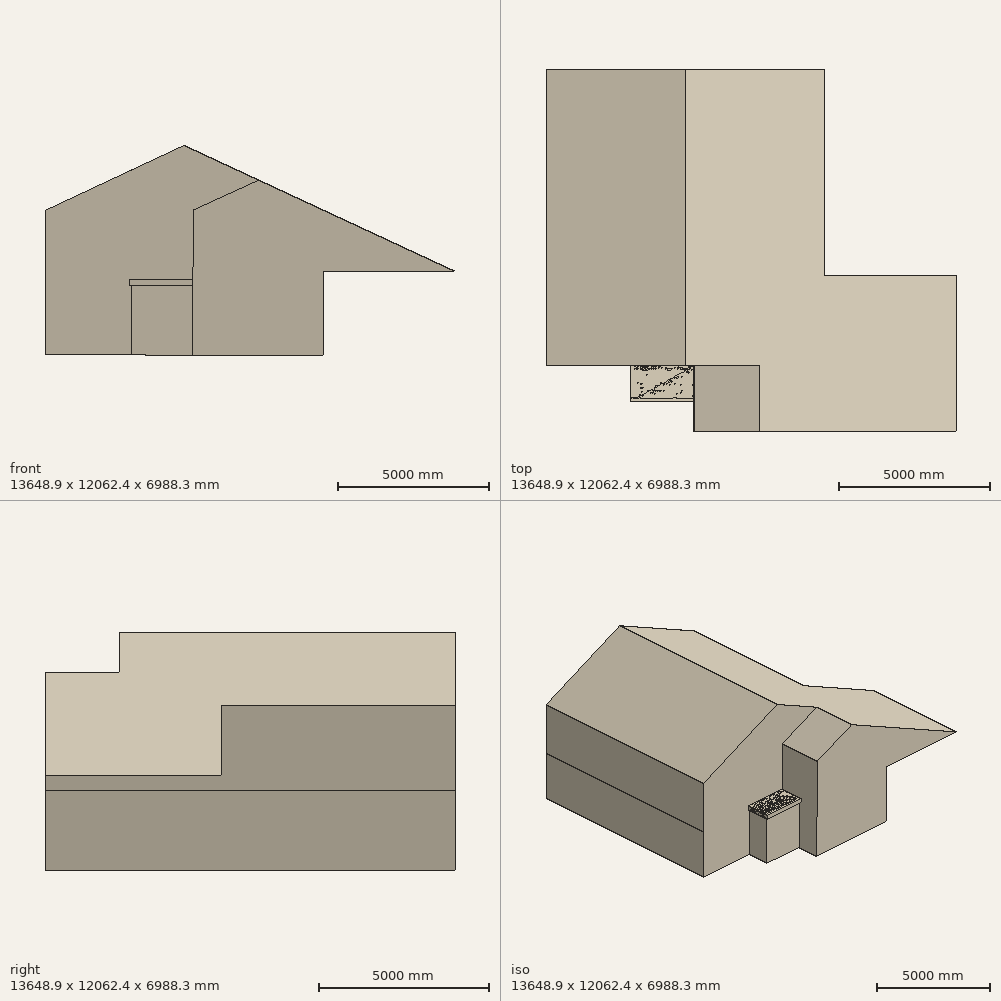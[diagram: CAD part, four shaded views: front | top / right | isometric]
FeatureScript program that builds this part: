
annotation { "Feature Type Name" : "Feature", "Feature Type Description" : "" }
export const myFeature = defineFeature(function(context is Context, id is Id, definition is map)
    precondition{}
    {
        {
            var Q0;
            Q0=qCreatedBy(makeId("Front.planeOp"),FACE);
            var sketch = newSketch(context, id + "F0", { "sketchPlane" : qUnion([Q0])});
            skLineSegment(sketch, "E0", {"start": v(18452.44, -7592.59) * mm, "end": v(18454.44, -7609.59) * mm});
            skLineSegment(sketch, "E1", {"start": v(18454.44, -7609.59) * mm, "end": v(18476.44, -7643.59) * mm});
            skLineSegment(sketch, "E2", {"start": v(18476.44, -7643.59) * mm, "end": v(21925.27, -7643.59) * mm});
            skLineSegment(sketch, "E3", {"start": v(-8455.23, 8336.41) * mm, "end": v(-8450.23, 8869.41) * mm});
            skLineSegment(sketch, "E4", {"start": v(9184.83, 9869.41) * mm, "end": v(9184.83, 10021.41) * mm});
            skLineSegment(sketch, "E5", {"start": v(9184.83, 10021.41) * mm, "end": v(9032.83, 10021.41) * mm});
            skLineSegment(sketch, "E6", {"start": v(9032.83, 10021.41) * mm, "end": v(9032.83, 9869.41) * mm});
            skLineSegment(sketch, "E7", {"start": v(9032.83, 9869.41) * mm, "end": v(9184.83, 9869.41) * mm});
            skLineSegment(sketch, "E8", {"start": v(-1174.56, -11014.59) * mm, "end": v(-1463.56, -11004.59) * mm});
            skLineSegment(sketch, "E9", {"start": v(3088.44, -8773.59) * mm, "end": v(3052.44, -8708.59) * mm});
            skLineSegment(sketch, "E10", {"start": v(3052.44, -8708.59) * mm, "end": v(2987.44, -8744.59) * mm});
            skLineSegment(sketch, "E11", {"start": v(2987.44, -8744.59) * mm, "end": v(3023.44, -8809.59) * mm});
            skLineSegment(sketch, "E12", {"start": v(3023.44, -8809.59) * mm, "end": v(3088.44, -8773.59) * mm});
            skLineSegment(sketch, "E13", {"start": v(4326.44, -9193.59) * mm, "end": v(4325.44, -9258.59) * mm});
            skLineSegment(sketch, "E14", {"start": v(4325.44, -9258.59) * mm, "end": v(4390.44, -9259.59) * mm});
            skLineSegment(sketch, "E15", {"start": v(4320.44, -9221.59) * mm, "end": v(4251.44, -9176.59) * mm});
            skLineSegment(sketch, "E16", {"start": v(4251.44, -9176.59) * mm, "end": v(4312.44, -9166.59) * mm});
            skLineSegment(sketch, "E17", {"start": v(-2874.56, -11901.59) * mm, "end": v(-2882.56, -11385.59) * mm});
            skLineSegment(sketch, "E18", {"start": v(-2949.56, -11902.59) * mm, "end": v(-2957.56, -11387.59) * mm});
            skLineSegment(sketch, "E19", {"start": v(-2882.56, -11385.59) * mm, "end": v(-2888.56, -11264.59) * mm});
            skLineSegment(sketch, "E20", {"start": v(-2957.56, -11387.59) * mm, "end": v(-2963.56, -11268.59) * mm});
            skLineSegment(sketch, "E21", {"start": v(-2888.56, -11264.59) * mm, "end": v(-2895.56, -11106.59) * mm});
            skLineSegment(sketch, "E22", {"start": v(-2963.56, -11268.59) * mm, "end": v(-2970.56, -11109.59) * mm});
            skArc(sketch, "E23", {"start": v(-10647.23, 10596.41) * mm, "mid": v(-10679.4, 10606.41) * mm, "end": v(-10711.23, 10595.41) * mm});
            skLineSegment(sketch, "E24", {"start": v(-10711.23, 10595.41) * mm, "end": v(-10798.23, 10527.41) * mm});
            skLineSegment(sketch, "E25", {"start": v(-10798.23, 10527.41) * mm, "end": v(-10806.23, 10504.41) * mm});
            skLineSegment(sketch, "E26", {"start": v(-10806.23, 10504.41) * mm, "end": v(-11091.23, 10388.41) * mm});
            skLineSegment(sketch, "E27", {"start": v(-11091.23, 10388.41) * mm, "end": v(-13024.23, 9421.41) * mm});
            skLineSegment(sketch, "E28", {"start": v(-10557.23, 10534.41) * mm, "end": v(-10611.23, 10573.41) * mm});
            skLineSegment(sketch, "E29", {"start": v(-10611.23, 10573.41) * mm, "end": v(-10647.23, 10596.41) * mm});
            skLineSegment(sketch, "E30", {"start": v(-10557.23, 10534.41) * mm, "end": v(-10550.83, 10516) * mm});
            skLineSegment(sketch, "E31", {"start": v(-10695.7, 10488.12) * mm, "end": v(-8590.23, 9450.41) * mm});
            skLineSegment(sketch, "E32", {"start": v(-8056.23, 9293.41) * mm, "end": v(-8040.23, 9323.41) * mm});
            skLineSegment(sketch, "E33", {"start": v(-8040.23, 9323.41) * mm, "end": v(-8319.23, 9433.41) * mm});
            skLineSegment(sketch, "E34", {"start": v(-8319.23, 9433.41) * mm, "end": v(-10253.23, 10396.41) * mm});
            skLineSegment(sketch, "E35", {"start": v(-10253.23, 10396.41) * mm, "end": v(-10522.23, 10504.41) * mm});
            skLineSegment(sketch, "E36", {"start": v(-10522.23, 10504.41) * mm, "end": v(-10550.83, 10516) * mm});
            skLineSegment(sketch, "E37", {"start": v(-8121.23, 9297.41) * mm, "end": v(-8056.23, 9293.41) * mm});
            skArc(sketch, "E38", {"start": v(-8144.23, 9285.42) * mm, "mid": v(-8077.27, 9212.5) * mm, "end": v(-7999.23, 9273.42) * mm});
            skLineSegment(sketch, "E39", {"start": v(-7999.23, 9273.42) * mm, "end": v(-8144.23, 9285.41) * mm});
            skArc(sketch, "E40", {"start": v(-8153.68, 9046.58) * mm, "mid": v(-8134.16, 9057.59) * mm, "end": v(-8124.4, 9077.76) * mm});
            skArc(sketch, "E41", {"start": v(-8347.8, 9005.21) * mm, "mid": v(-8418.14, 8951.74) * mm, "end": v(-8450.23, 8869.42) * mm});
            skLineSegment(sketch, "E42", {"start": v(-8347.8, 9005.21) * mm, "end": v(-8153.68, 9046.58) * mm});
            skArc(sketch, "E43", {"start": v(-8312.07, 8935.4) * mm, "mid": v(-8354.55, 8902.55) * mm, "end": v(-8376.23, 8853.42) * mm});
            skArc(sketch, "E44", {"start": v(-8112.54, 8979.42) * mm, "mid": v(-8073.98, 9001.36) * mm, "end": v(-8054.57, 9041.26) * mm});
            skLineSegment(sketch, "E45", {"start": v(-8312.07, 8935.4) * mm, "end": v(-8112.54, 8979.42) * mm});
            skLineSegment(sketch, "E46", {"start": v(-8054.57, 9041.26) * mm, "end": v(-8025.82, 9228.12) * mm});
            skLineSegment(sketch, "E47", {"start": v(-8124.4, 9077.76) * mm, "end": v(-8103.38, 9219.7) * mm});
            skLineSegment(sketch, "E48", {"start": v(-8578.23, 9283.41) * mm, "end": v(-9845.23, 9908.41) * mm});
            skLineSegment(sketch, "E49", {"start": v(-8578.23, 9165.66) * mm, "end": v(-8578.23, 9283.41) * mm});
            skLineSegment(sketch, "E50", {"start": v(-8141.4, 9155) * mm, "end": v(-8578.23, 9165.66) * mm});
            skLineSegment(sketch, "E51", {"start": v(-8135.9, 9300.67) * mm, "end": v(-8136.5, 9284.77) * mm});
            skLineSegment(sketch, "E52", {"start": v(-8137.63, 9254.9) * mm, "end": v(-8141.4, 9155) * mm});
            skLineSegment(sketch, "E53", {"start": v(-8485.65, 6827.41) * mm, "end": v(-8490.38, 9163.52) * mm});
            skLineSegment(sketch, "E54", {"start": v(-11690.04, 7524.24) * mm, "end": v(-9647.23, 7524.24) * mm});
            skLineSegment(sketch, "E55", {"start": v(-9714.9, 7595.41) * mm, "end": v(-11621.96, 7595.41) * mm});
            skLineSegment(sketch, "E56", {"start": v(-11690.04, 7524.24) * mm, "end": v(-11690.27, 7577.41) * mm});
            skLineSegment(sketch, "E57", {"start": v(-9647.23, 7577.41) * mm, "end": v(-11690.27, 7577.41) * mm});
            skLineSegment(sketch, "E58", {"start": v(-9647.23, 7524.24) * mm, "end": v(-9647.23, 7577.41) * mm});
            skLineSegment(sketch, "E59", {"start": v(-9714.9, 9403.41) * mm, "end": v(-9714.9, 7577.41) * mm});
            skLineSegment(sketch, "E60", {"start": v(-11621.96, 9403.41) * mm, "end": v(-11621.96, 7577.41) * mm});
            skLineSegment(sketch, "E61", {"start": v(-11621.96, 9403.41) * mm, "end": v(-9714.9, 9403.41) * mm});
            skLineSegment(sketch, "E62", {"start": v(-9744.23, 7627.41) * mm, "end": v(-10336.23, 7627.41) * mm});
            skLineSegment(sketch, "E63", {"start": v(-10336.23, 7627.41) * mm, "end": v(-10336.23, 8738.41) * mm});
            skLineSegment(sketch, "E64", {"start": v(-10336.23, 8738.41) * mm, "end": v(-9744.23, 8738.41) * mm});
            skLineSegment(sketch, "E65", {"start": v(-9744.23, 8738.41) * mm, "end": v(-9744.23, 7627.41) * mm});
            skLineSegment(sketch, "E66", {"start": v(-9808.23, 7689.41) * mm, "end": v(-10274.23, 7689.41) * mm});
            skLineSegment(sketch, "E67", {"start": v(-10274.23, 7689.41) * mm, "end": v(-10274.23, 8676.41) * mm});
            skLineSegment(sketch, "E68", {"start": v(-10274.23, 8676.41) * mm, "end": v(-9808.23, 8676.41) * mm});
            skLineSegment(sketch, "E69", {"start": v(-9808.23, 8676.41) * mm, "end": v(-9808.23, 7689.41) * mm});
            skLineSegment(sketch, "E70", {"start": v(-9755.23, 7636.41) * mm, "end": v(-10327.23, 7636.41) * mm});
            skLineSegment(sketch, "E71", {"start": v(-10327.23, 7636.41) * mm, "end": v(-10327.23, 8729.41) * mm});
            skLineSegment(sketch, "E72", {"start": v(-10327.23, 8729.41) * mm, "end": v(-9755.23, 8729.41) * mm});
            skLineSegment(sketch, "E73", {"start": v(-9755.23, 8729.41) * mm, "end": v(-9755.23, 7636.41) * mm});
            skLineSegment(sketch, "E74", {"start": v(-9819.23, 7700.41) * mm, "end": v(-10263.23, 7700.41) * mm});
            skLineSegment(sketch, "E75", {"start": v(-10263.23, 7700.41) * mm, "end": v(-10263.23, 8665.41) * mm});
            skLineSegment(sketch, "E76", {"start": v(-10263.23, 8665.41) * mm, "end": v(-9819.23, 8665.41) * mm});
            skLineSegment(sketch, "E77", {"start": v(-9819.23, 8665.41) * mm, "end": v(-9819.23, 7700.41) * mm});
            skLineSegment(sketch, "E78", {"start": v(-10336.23, 8751.41) * mm, "end": v(-9744.23, 8751.41) * mm});
            skLineSegment(sketch, "E79", {"start": v(-9744.23, 8751.41) * mm, "end": v(-9744.23, 9144.41) * mm});
            skLineSegment(sketch, "E80", {"start": v(-9744.23, 9144.41) * mm, "end": v(-10336.23, 9144.41) * mm});
            skLineSegment(sketch, "E81", {"start": v(-10336.23, 9144.41) * mm, "end": v(-10336.23, 8751.41) * mm});
            skLineSegment(sketch, "E82", {"start": v(-10325.23, 8762.41) * mm, "end": v(-9755.23, 8762.41) * mm});
            skLineSegment(sketch, "E83", {"start": v(-9755.23, 8762.41) * mm, "end": v(-9755.23, 9133.41) * mm});
            skLineSegment(sketch, "E84", {"start": v(-9755.23, 9133.41) * mm, "end": v(-10325.23, 9133.41) * mm});
            skLineSegment(sketch, "E85", {"start": v(-10325.23, 9133.41) * mm, "end": v(-10325.23, 8762.41) * mm});
            skLineSegment(sketch, "E86", {"start": v(-10268.23, 8805.41) * mm, "end": v(-9798.23, 8805.41) * mm});
            skLineSegment(sketch, "E87", {"start": v(-10268.23, 9090.42) * mm, "end": v(-10268.23, 8805.41) * mm});
            skLineSegment(sketch, "E88", {"start": v(-9798.23, 9090.42) * mm, "end": v(-10268.23, 9090.42) * mm});
            skLineSegment(sketch, "E89", {"start": v(-9798.43, 8805.41) * mm, "end": v(-9798.43, 9090.42) * mm});
            skLineSegment(sketch, "E90", {"start": v(-9809.23, 9079.41) * mm, "end": v(-10257.23, 9079.41) * mm});
            skLineSegment(sketch, "E91", {"start": v(-9809.23, 8816.41) * mm, "end": v(-9809.23, 9079.41) * mm});
            skLineSegment(sketch, "E92", {"start": v(-10257.23, 8816.41) * mm, "end": v(-9809.23, 8816.41) * mm});
            skLineSegment(sketch, "E93", {"start": v(-10257.23, 9079.41) * mm, "end": v(-10257.23, 8816.41) * mm});
            skLineSegment(sketch, "E94", {"start": v(-9837.23, 9118.41) * mm, "end": v(-10240.23, 9118.41) * mm});
            skLineSegment(sketch, "E95", {"start": v(-10240.23, 9118.41) * mm, "end": v(-10240.23, 9100.41) * mm});
            skLineSegment(sketch, "E96", {"start": v(-10240.23, 9100.41) * mm, "end": v(-9837.23, 9100.41) * mm});
            skLineSegment(sketch, "E97", {"start": v(-9837.23, 9100.41) * mm, "end": v(-9837.23, 9118.41) * mm});
            skLineSegment(sketch, "E98", {"start": v(-10996.23, 7627.41) * mm, "end": v(-11588.23, 7627.41) * mm});
            skLineSegment(sketch, "E99", {"start": v(-11588.23, 7627.41) * mm, "end": v(-11588.23, 8738.41) * mm});
            skLineSegment(sketch, "E100", {"start": v(-11588.23, 8738.41) * mm, "end": v(-10996.23, 8738.41) * mm});
            skLineSegment(sketch, "E101", {"start": v(-10996.23, 8738.41) * mm, "end": v(-10996.23, 7627.41) * mm});
            skLineSegment(sketch, "E102", {"start": v(-11060.23, 7689.41) * mm, "end": v(-11526.23, 7689.41) * mm});
            skLineSegment(sketch, "E103", {"start": v(-11526.23, 7689.41) * mm, "end": v(-11526.23, 8676.41) * mm});
            skLineSegment(sketch, "E104", {"start": v(-11526.23, 8676.41) * mm, "end": v(-11060.23, 8676.41) * mm});
            skLineSegment(sketch, "E105", {"start": v(-11060.23, 8676.41) * mm, "end": v(-11060.23, 7689.41) * mm});
            skLineSegment(sketch, "E106", {"start": v(-11007.23, 7636.41) * mm, "end": v(-11579.23, 7636.41) * mm});
            skLineSegment(sketch, "E107", {"start": v(-11579.23, 7636.41) * mm, "end": v(-11579.23, 8729.41) * mm});
            skLineSegment(sketch, "E108", {"start": v(-11579.23, 8729.41) * mm, "end": v(-11007.23, 8729.41) * mm});
            skLineSegment(sketch, "E109", {"start": v(-11007.23, 8729.41) * mm, "end": v(-11007.23, 7636.41) * mm});
            skLineSegment(sketch, "E110", {"start": v(-11071.23, 7700.41) * mm, "end": v(-11515.23, 7700.41) * mm});
            skLineSegment(sketch, "E111", {"start": v(-11515.23, 7700.41) * mm, "end": v(-11515.23, 8665.41) * mm});
            skLineSegment(sketch, "E112", {"start": v(-11515.23, 8665.41) * mm, "end": v(-11071.23, 8665.41) * mm});
            skLineSegment(sketch, "E113", {"start": v(-11071.23, 8665.41) * mm, "end": v(-11071.23, 7700.41) * mm});
            skLineSegment(sketch, "E114", {"start": v(-11588.23, 8751.41) * mm, "end": v(-10996.23, 8751.41) * mm});
            skLineSegment(sketch, "E115", {"start": v(-10996.23, 8751.41) * mm, "end": v(-10996.23, 9144.41) * mm});
            skLineSegment(sketch, "E116", {"start": v(-10996.23, 9144.41) * mm, "end": v(-11588.23, 9144.41) * mm});
            skLineSegment(sketch, "E117", {"start": v(-11588.23, 9144.41) * mm, "end": v(-11588.23, 8751.41) * mm});
            skLineSegment(sketch, "E118", {"start": v(-11577.23, 8762.41) * mm, "end": v(-11007.23, 8762.41) * mm});
            skLineSegment(sketch, "E119", {"start": v(-11007.23, 8762.41) * mm, "end": v(-11007.23, 9133.41) * mm});
            skLineSegment(sketch, "E120", {"start": v(-11007.23, 9133.41) * mm, "end": v(-11577.23, 9133.41) * mm});
            skLineSegment(sketch, "E121", {"start": v(-11577.23, 9133.41) * mm, "end": v(-11577.23, 8762.41) * mm});
            skLineSegment(sketch, "E122", {"start": v(-11520.23, 8805.41) * mm, "end": v(-11050.23, 8805.41) * mm});
            skLineSegment(sketch, "E123", {"start": v(-11520.23, 9090.42) * mm, "end": v(-11520.23, 8805.41) * mm});
            skLineSegment(sketch, "E124", {"start": v(-11050.23, 9090.42) * mm, "end": v(-11520.23, 9090.42) * mm});
            skLineSegment(sketch, "E125", {"start": v(-11050.43, 8805.41) * mm, "end": v(-11050.43, 9090.42) * mm});
            skLineSegment(sketch, "E126", {"start": v(-11061.23, 9079.41) * mm, "end": v(-11509.23, 9079.41) * mm});
            skLineSegment(sketch, "E127", {"start": v(-11061.23, 8816.41) * mm, "end": v(-11061.23, 9079.41) * mm});
            skLineSegment(sketch, "E128", {"start": v(-11509.23, 8816.41) * mm, "end": v(-11061.23, 8816.41) * mm});
            skLineSegment(sketch, "E129", {"start": v(-11509.23, 9079.41) * mm, "end": v(-11509.23, 8816.41) * mm});
            skLineSegment(sketch, "E130", {"start": v(-11089.23, 9118.41) * mm, "end": v(-11492.23, 9118.41) * mm});
            skLineSegment(sketch, "E131", {"start": v(-11492.23, 9118.41) * mm, "end": v(-11492.23, 9100.41) * mm});
            skLineSegment(sketch, "E132", {"start": v(-11492.23, 9100.41) * mm, "end": v(-11089.23, 9100.41) * mm});
            skLineSegment(sketch, "E133", {"start": v(-11089.23, 9100.41) * mm, "end": v(-11089.23, 9118.41) * mm});
            skLineSegment(sketch, "E134", {"start": v(-11515.23, 8663.41) * mm, "end": v(-11515.23, 8654.41) * mm});
            skLineSegment(sketch, "E135", {"start": v(-11621.96, 9177.41) * mm, "end": v(-9714.9, 9177.41) * mm});
            skLineSegment(sketch, "E136", {"start": v(-11621.96, 9150.41) * mm, "end": v(-9714.9, 9150.41) * mm});
            skLineSegment(sketch, "E137", {"start": v(-9210.23, 7574.41) * mm, "end": v(-9049.23, 7574.41) * mm});
            skLineSegment(sketch, "E138", {"start": v(-9049.23, 7574.41) * mm, "end": v(-9049.23, 7462.41) * mm});
            skLineSegment(sketch, "E139", {"start": v(-9049.23, 7462.41) * mm, "end": v(-9210.23, 7462.41) * mm});
            skLineSegment(sketch, "E140", {"start": v(-9210.23, 7462.41) * mm, "end": v(-9210.23, 7574.41) * mm});
            skLineSegment(sketch, "E141", {"start": v(-9199.23, 7421.41) * mm, "end": v(-9061.23, 7421.41) * mm});
            skLineSegment(sketch, "E142", {"start": v(-9199.23, 7462.41) * mm, "end": v(-9199.23, 7421.41) * mm});
            skLineSegment(sketch, "E143", {"start": v(-9061.23, 7421.41) * mm, "end": v(-9061.23, 7462.41) * mm});
            skCircle(sketch, "E144", {"center": v(-9756.73, 7030.41) * mm, "radius": 12 * mm});
            skLineSegment(sketch, "E145", {"start": v(-9845.23, 9908.41) * mm, "end": v(-10687.65, 10323) * mm});
            skLineSegment(sketch, "E146", {"start": v(-10687.65, 10323) * mm, "end": v(-12771.23, 9266.78) * mm});
            skLineSegment(sketch, "E147", {"start": v(-12771.23, 9266.78) * mm, "end": v(-12771.23, 9159.73) * mm});
            skLineSegment(sketch, "E148", {"start": v(-12771.23, 9159.73) * mm, "end": v(-13205.42, 9148.16) * mm});
            skLineSegment(sketch, "E149", {"start": v(-12852.09, 9157.58) * mm, "end": v(-12857.83, 6827.41) * mm});
            skArc(sketch, "E150", {"start": v(-13346.23, 9258.41) * mm, "mid": v(-13267.7, 9198.8) * mm, "end": v(-13203.24, 9273.41) * mm});
            skLineSegment(sketch, "E151", {"start": v(-13203.23, 9273.42) * mm, "end": v(-13346.23, 9258.41) * mm});
            skArc(sketch, "E152", {"start": v(-13288.68, 9031.06) * mm, "mid": v(-13273, 8995.2) * mm, "end": v(-13241.38, 8972.14) * mm});
            skArc(sketch, "E153", {"start": v(-13217.6, 9063.8) * mm, "mid": v(-13209.7, 9045.88) * mm, "end": v(-13193.84, 9034.39) * mm});
            skArc(sketch, "E154", {"start": v(-12960.23, 8838.45) * mm, "mid": v(-12966.83, 8859.69) * mm, "end": v(-12984.3, 8873.46) * mm});
            skLineSegment(sketch, "E155", {"start": v(-12984.3, 8873.46) * mm, "end": v(-13241.38, 8972.14) * mm});
            skArc(sketch, "E156", {"start": v(-12885.23, 8865.38) * mm, "mid": v(-12898.5, 8907.97) * mm, "end": v(-12933.6, 8935.5) * mm});
            skLineSegment(sketch, "E157", {"start": v(-12933.6, 8935.5) * mm, "end": v(-13193.84, 9034.39) * mm});
            skLineSegment(sketch, "E158", {"start": v(-13217.6, 9063.8) * mm, "end": v(-13239.48, 9207.9) * mm});
            skLineSegment(sketch, "E159", {"start": v(-13288.68, 9031.06) * mm, "end": v(-13315.55, 9210.76) * mm});
            skLineSegment(sketch, "E160", {"start": v(-13300.8, 9274.63) * mm, "end": v(-13042.23, 9329.41) * mm});
            skLineSegment(sketch, "E161", {"start": v(-13042.23, 9329.41) * mm, "end": v(-12947.23, 9351.41) * mm});
            skLineSegment(sketch, "E162", {"start": v(-12947.23, 9351.41) * mm, "end": v(-12906.23, 9365.41) * mm});
            skLineSegment(sketch, "E163", {"start": v(-12906.23, 9365.41) * mm, "end": v(-12630.23, 9507.41) * mm});
            skLineSegment(sketch, "E164", {"start": v(-12630.23, 9507.41) * mm, "end": v(-10695.7, 10488.12) * mm});
            skLineSegment(sketch, "E165", {"start": v(-13300.8, 9274.63) * mm, "end": v(-13311.94, 9301.29) * mm});
            skLineSegment(sketch, "E166", {"start": v(-13311.94, 9301.29) * mm, "end": v(-13024.23, 9421.41) * mm});
            skLineSegment(sketch, "E167", {"start": v(-13211.52, 9272.55) * mm, "end": v(-13212.53, 9293.33) * mm});
            skLineSegment(sketch, "E168", {"start": v(-13205.42, 9148.16) * mm, "end": v(-13209.92, 9240) * mm});
            skLineSegment(sketch, "E169", {"start": v(-13923.23, 7019.41) * mm, "end": v(-13923.23, 7048.41) * mm});
            skLineSegment(sketch, "E170", {"start": v(-13877.93, 9067.41) * mm, "end": v(-13877.93, 7043.41) * mm});
            skLineSegment(sketch, "E171", {"start": v(-13877.93, 7043.41) * mm, "end": v(-13911.9, 7043.41) * mm});
            skLineSegment(sketch, "E172", {"start": v(-13911.9, 9101.41) * mm, "end": v(-13911.9, 7043.41) * mm});
            skLineSegment(sketch, "E173", {"start": v(-13923.23, 7048.41) * mm, "end": v(-13911.9, 7048.41) * mm});
            skLineSegment(sketch, "E174", {"start": v(-13842.22, 9045.41) * mm, "end": v(-13842.22, 7058.41) * mm});
            skLineSegment(sketch, "E175", {"start": v(-13802.73, 7988.44) * mm, "end": v(-13802.23, 7957.41) * mm});
            skLineSegment(sketch, "E176", {"start": v(-13805.35, 8257.4) * mm, "end": v(-13806.23, 8288.41) * mm});
            skCircle(sketch, "E177", {"center": v(-13785.88, 8117.68) * mm, "radius": 24.33 * mm});
            skLineSegment(sketch, "E178", {"start": v(-13724.23, 8282.36) * mm, "end": v(-13724.23, 8931.41) * mm});
            skLineSegment(sketch, "E179", {"start": v(-13739.23, 8285.67) * mm, "end": v(-13739.23, 8946.41) * mm});
            skLineSegment(sketch, "E180", {"start": v(-13724.23, 7996.26) * mm, "end": v(-13724.23, 8250.03) * mm});
            skLineSegment(sketch, "E181", {"start": v(-13739.23, 7992.7) * mm, "end": v(-13739.23, 8254.02) * mm});
            skCircle(sketch, "E182", {"center": v(-13748.23, 7086.41) * mm, "radius": 14 * mm});
            skLineSegment(sketch, "E183", {"start": v(-13877.93, 7058.41) * mm, "end": v(-12978.12, 7058.41) * mm});
            skLineSegment(sketch, "E184", {"start": v(-13103.23, 7234.41) * mm, "end": v(-13739.23, 7234.41) * mm});
            skLineSegment(sketch, "E185", {"start": v(-13739.23, 7234.41) * mm, "end": v(-13739.23, 7961.24) * mm});
            skLineSegment(sketch, "E186", {"start": v(-13118.23, 7249.41) * mm, "end": v(-13724.23, 7249.41) * mm});
            skLineSegment(sketch, "E187", {"start": v(-13724.23, 7249.41) * mm, "end": v(-13724.23, 7964.14) * mm});
            skLineSegment(sketch, "E188", {"start": v(-13103.23, 8919.11) * mm, "end": v(-13103.23, 7234.41) * mm});
            skLineSegment(sketch, "E189", {"start": v(-13739.23, 8946.41) * mm, "end": v(-13174.37, 8946.41) * mm});
            skLineSegment(sketch, "E190", {"start": v(-13724.23, 8931.41) * mm, "end": v(-13135.29, 8931.41) * mm});
            skLineSegment(sketch, "E191", {"start": v(-13118.23, 8924.87) * mm, "end": v(-13118.23, 7249.41) * mm});
            skLineSegment(sketch, "E192", {"start": v(-13002.45, 8880.43) * mm, "end": v(-13002.45, 7058.41) * mm});
            skLineSegment(sketch, "E193", {"start": v(-13002.45, 9045.41) * mm, "end": v(-13002.45, 8961.66) * mm});
            skLineSegment(sketch, "E194", {"start": v(-12978.12, 9067.41) * mm, "end": v(-12978.12, 8952.41) * mm});
            skLineSegment(sketch, "E195", {"start": v(-12940.58, 9101.41) * mm, "end": v(-12940.58, 8937.76) * mm});
            skLineSegment(sketch, "E196", {"start": v(-12978.12, 8871.09) * mm, "end": v(-12978.12, 7040.41) * mm});
            skLineSegment(sketch, "E197", {"start": v(-13289.43, 9045.41) * mm, "end": v(-13842.22, 9045.41) * mm});
            skLineSegment(sketch, "E198", {"start": v(-13294.11, 9067.41) * mm, "end": v(-13877.93, 9067.41) * mm});
            skLineSegment(sketch, "E199", {"start": v(-13299.2, 9101.41) * mm, "end": v(-13911.9, 9101.41) * mm});
            skLineSegment(sketch, "E200", {"start": v(-12940.58, 9101.41) * mm, "end": v(-13223.31, 9101.41) * mm});
            skLineSegment(sketch, "E201", {"start": v(-12978.12, 9067.41) * mm, "end": v(-13218.15, 9067.41) * mm});
            skLineSegment(sketch, "E202", {"start": v(-12885.23, 6998.23) * mm, "end": v(-12885.23, 8865.38) * mm});
            skLineSegment(sketch, "E203", {"start": v(-12960.23, 6998.28) * mm, "end": v(-12960.23, 8838.45) * mm});
            skLineSegment(sketch, "E204", {"start": v(-13923.23, 7040.41) * mm, "end": v(-12960.23, 7040.41) * mm});
            skLineSegment(sketch, "E205", {"start": v(-12960.23, 7019.41) * mm, "end": v(-13923.23, 7019.41) * mm});
            skLineSegment(sketch, "E206", {"start": v(-12857.41, 6998.21) * mm, "end": v(-14857.16, 6999.45) * mm});
            skLineSegment(sketch, "E207", {"start": v(-14857.25, 6847.41) * mm, "end": v(-14857.16, 6999.45) * mm});
            skArc(sketch, "E208", {"start": v(-14372.13, 8991.8) * mm, "mid": v(-14381.35, 9001.01) * mm, "end": v(-14390.57, 8991.8) * mm});
            skLineSegment(sketch, "E209", {"start": v(-14358.23, 8899.54) * mm, "end": v(-14358.23, 8886.41) * mm});
            skLineSegment(sketch, "E210", {"start": v(-14372.13, 8899.54) * mm, "end": v(-14358.23, 8899.54) * mm});
            skLineSegment(sketch, "E211", {"start": v(-14372.13, 8991.8) * mm, "end": v(-14372.13, 8899.54) * mm});
            skLineSegment(sketch, "E212", {"start": v(-14404.47, 8899.54) * mm, "end": v(-14404.47, 8886.41) * mm});
            skLineSegment(sketch, "E213", {"start": v(-14390.57, 8899.54) * mm, "end": v(-14404.47, 8899.54) * mm});
            skLineSegment(sketch, "E214", {"start": v(-14390.57, 8991.8) * mm, "end": v(-14390.57, 8899.54) * mm});
            skLineSegment(sketch, "E215", {"start": v(-14445.47, 8846.41) * mm, "end": v(-14445.47, 8726.41) * mm});
            skArc(sketch, "E216", {"start": v(-14445.47, 8726.41) * mm, "mid": v(-14381.35, 8660.14) * mm, "end": v(-14317.23, 8726.41) * mm});
            skLineSegment(sketch, "E217", {"start": v(-14317.23, 8846.41) * mm, "end": v(-14317.23, 8726.41) * mm});
            skArc(sketch, "E218", {"start": v(-14372.13, 8937.19) * mm, "mid": v(-14381.35, 9047.17) * mm, "end": v(-14390.57, 8937.19) * mm});
            skLineSegment(sketch, "E219", {"start": v(-14445.47, 8846.41) * mm, "end": v(-14317.23, 8846.41) * mm});
            skLineSegment(sketch, "E220", {"start": v(-14404.47, 8886.41) * mm, "end": v(-14357.14, 8886.19) * mm});
            skLineSegment(sketch, "E221", {"start": v(-14372.13, 8899.54) * mm, "end": v(-14390.57, 8899.54) * mm});
            skLineSegment(sketch, "E222", {"start": v(-14529.23, 8086.41) * mm, "end": v(-14233.23, 8086.41) * mm});
            skLineSegment(sketch, "E223", {"start": v(-14233.23, 8086.41) * mm, "end": v(-14233.23, 8150.41) * mm});
            skLineSegment(sketch, "E224", {"start": v(-14233.23, 8150.41) * mm, "end": v(-14529.23, 8150.41) * mm});
            skLineSegment(sketch, "E225", {"start": v(-14529.23, 8150.41) * mm, "end": v(-14529.23, 8086.41) * mm});
            skLineSegment(sketch, "E226", {"start": v(-13956.23, 8444.41) * mm, "end": v(-13956.04, 8443.63) * mm});
            skLineSegment(sketch, "E227", {"start": v(-13956.04, 8443.63) * mm, "end": v(-13955.8, 8442.87) * mm});
            skLineSegment(sketch, "E228", {"start": v(-13955.8, 8442.87) * mm, "end": v(-13955.52, 8442.1) * mm});
            skLineSegment(sketch, "E229", {"start": v(-13955.52, 8442.1) * mm, "end": v(-13955.2, 8441.37) * mm});
            skLineSegment(sketch, "E230", {"start": v(-13955.2, 8441.37) * mm, "end": v(-13954.85, 8440.65) * mm});
            skLineSegment(sketch, "E231", {"start": v(-13954.85, 8440.65) * mm, "end": v(-13954.46, 8439.94) * mm});
            skLineSegment(sketch, "E232", {"start": v(-13954.46, 8439.94) * mm, "end": v(-13954.03, 8439.26) * mm});
            skLineSegment(sketch, "E233", {"start": v(-13954.03, 8439.26) * mm, "end": v(-13953.57, 8438.6) * mm});
            skLineSegment(sketch, "E234", {"start": v(-13953.57, 8438.6) * mm, "end": v(-13953.07, 8437.97) * mm});
            skLineSegment(sketch, "E235", {"start": v(-13953.07, 8437.97) * mm, "end": v(-13952.54, 8437.37) * mm});
            skLineSegment(sketch, "E236", {"start": v(-13952.54, 8437.37) * mm, "end": v(-13951.98, 8436.79) * mm});
            skLineSegment(sketch, "E237", {"start": v(-13951.98, 8436.79) * mm, "end": v(-13951.39, 8436.24) * mm});
            skLineSegment(sketch, "E238", {"start": v(-13951.39, 8436.24) * mm, "end": v(-13950.77, 8435.73) * mm});
            skLineSegment(sketch, "E239", {"start": v(-13950.77, 8435.73) * mm, "end": v(-13950.12, 8435.24) * mm});
            skLineSegment(sketch, "E240", {"start": v(-13950.12, 8435.24) * mm, "end": v(-13949.45, 8434.8) * mm});
            skLineSegment(sketch, "E241", {"start": v(-13949.45, 8434.8) * mm, "end": v(-13948.76, 8434.38) * mm});
            skLineSegment(sketch, "E242", {"start": v(-13948.76, 8434.38) * mm, "end": v(-13948.05, 8434) * mm});
            skLineSegment(sketch, "E243", {"start": v(-13948.05, 8434) * mm, "end": v(-13947.32, 8433.67) * mm});
            skLineSegment(sketch, "E244", {"start": v(-13947.32, 8433.67) * mm, "end": v(-13946.57, 8433.37) * mm});
            skLineSegment(sketch, "E245", {"start": v(-13946.57, 8433.37) * mm, "end": v(-13945.81, 8433.11) * mm});
            skLineSegment(sketch, "E246", {"start": v(-13945.81, 8433.11) * mm, "end": v(-13945.04, 8432.9) * mm});
            skLineSegment(sketch, "E247", {"start": v(-13945.04, 8432.9) * mm, "end": v(-13944.25, 8432.71) * mm});
            skLineSegment(sketch, "E248", {"start": v(-13944.25, 8432.71) * mm, "end": v(-13943.46, 8432.58) * mm});
            skLineSegment(sketch, "E249", {"start": v(-13943.46, 8432.58) * mm, "end": v(-13942.66, 8432.48) * mm});
            skLineSegment(sketch, "E250", {"start": v(-13942.66, 8432.48) * mm, "end": v(-13941.86, 8432.43) * mm});
            skLineSegment(sketch, "E251", {"start": v(-13941.86, 8432.43) * mm, "end": v(-13941.05, 8432.42) * mm});
            skLineSegment(sketch, "E252", {"start": v(-13941.05, 8432.42) * mm, "end": v(-13940.25, 8432.45) * mm});
            skLineSegment(sketch, "E253", {"start": v(-13940.25, 8432.45) * mm, "end": v(-13939.45, 8432.52) * mm});
            skLineSegment(sketch, "E254", {"start": v(-13939.45, 8432.52) * mm, "end": v(-13938.65, 8432.63) * mm});
            skLineSegment(sketch, "E255", {"start": v(-13938.65, 8432.63) * mm, "end": v(-13937.86, 8432.79) * mm});
            skLineSegment(sketch, "E256", {"start": v(-13937.86, 8432.79) * mm, "end": v(-13937.08, 8432.99) * mm});
            skLineSegment(sketch, "E257", {"start": v(-13937.08, 8432.99) * mm, "end": v(-13936.31, 8433.22) * mm});
            skLineSegment(sketch, "E258", {"start": v(-13936.31, 8433.22) * mm, "end": v(-13935.55, 8433.5) * mm});
            skLineSegment(sketch, "E259", {"start": v(-13935.55, 8433.5) * mm, "end": v(-13934.81, 8433.82) * mm});
            skLineSegment(sketch, "E260", {"start": v(-13934.81, 8433.82) * mm, "end": v(-13934.1, 8434.17) * mm});
            skLineSegment(sketch, "E261", {"start": v(-13934.1, 8434.17) * mm, "end": v(-13933.39, 8434.57) * mm});
            skLineSegment(sketch, "E262", {"start": v(-13933.39, 8434.57) * mm, "end": v(-13932.7, 8435) * mm});
            skLineSegment(sketch, "E263", {"start": v(-13932.7, 8435) * mm, "end": v(-13932.05, 8435.46) * mm});
            skLineSegment(sketch, "E264", {"start": v(-13932.05, 8435.46) * mm, "end": v(-13931.42, 8435.96) * mm});
            skLineSegment(sketch, "E265", {"start": v(-13931.42, 8435.96) * mm, "end": v(-13930.81, 8436.49) * mm});
            skLineSegment(sketch, "E266", {"start": v(-13930.81, 8436.49) * mm, "end": v(-13930.23, 8437.05) * mm});
            skLineSegment(sketch, "E267", {"start": v(-13930.23, 8437.05) * mm, "end": v(-13929.69, 8437.64) * mm});
            skLineSegment(sketch, "E268", {"start": v(-13929.69, 8437.64) * mm, "end": v(-13929.17, 8438.26) * mm});
            skLineSegment(sketch, "E269", {"start": v(-13929.17, 8438.26) * mm, "end": v(-13928.69, 8438.9) * mm});
            skLineSegment(sketch, "E270", {"start": v(-13928.69, 8438.9) * mm, "end": v(-13928.24, 8439.57) * mm});
            skLineSegment(sketch, "E271", {"start": v(-13928.24, 8439.57) * mm, "end": v(-13927.83, 8440.26) * mm});
            skLineSegment(sketch, "E272", {"start": v(-13927.83, 8440.26) * mm, "end": v(-13927.45, 8440.97) * mm});
            skLineSegment(sketch, "E273", {"start": v(-13927.45, 8440.97) * mm, "end": v(-13927.12, 8441.7) * mm});
            skLineSegment(sketch, "E274", {"start": v(-13927.12, 8441.7) * mm, "end": v(-13926.82, 8442.45) * mm});
            skLineSegment(sketch, "E275", {"start": v(-13926.82, 8442.45) * mm, "end": v(-13926.56, 8443.21) * mm});
            skLineSegment(sketch, "E276", {"start": v(-13926.56, 8443.21) * mm, "end": v(-13926.34, 8443.99) * mm});
            skLineSegment(sketch, "E277", {"start": v(-13926.34, 8443.99) * mm, "end": v(-13926.23, 8444.41) * mm});
            skLineSegment(sketch, "E278", {"start": v(-13926.23, 8444.41) * mm, "end": v(-13926.23, 8482.41) * mm});
            skLineSegment(sketch, "E279", {"start": v(-13926.23, 8482.41) * mm, "end": v(-13926.37, 8483.2) * mm});
            skLineSegment(sketch, "E280", {"start": v(-13926.37, 8483.2) * mm, "end": v(-13926.54, 8483.97) * mm});
            skLineSegment(sketch, "E281", {"start": v(-13926.54, 8483.97) * mm, "end": v(-13926.76, 8484.73) * mm});
            skLineSegment(sketch, "E282", {"start": v(-13926.76, 8484.73) * mm, "end": v(-13927, 8485.49) * mm});
            skLineSegment(sketch, "E283", {"start": v(-13927, 8485.49) * mm, "end": v(-13927.3, 8486.22) * mm});
            skLineSegment(sketch, "E284", {"start": v(-13927.3, 8486.22) * mm, "end": v(-13927.63, 8486.94) * mm});
            skLineSegment(sketch, "E285", {"start": v(-13927.63, 8486.94) * mm, "end": v(-13928, 8487.65) * mm});
            skLineSegment(sketch, "E286", {"start": v(-13928, 8487.65) * mm, "end": v(-13928.4, 8488.33) * mm});
            skLineSegment(sketch, "E287", {"start": v(-13928.4, 8488.33) * mm, "end": v(-13928.85, 8488.99) * mm});
            skLineSegment(sketch, "E288", {"start": v(-13928.85, 8488.99) * mm, "end": v(-13929.32, 8489.63) * mm});
            skLineSegment(sketch, "E289", {"start": v(-13929.32, 8489.63) * mm, "end": v(-13929.83, 8490.24) * mm});
            skLineSegment(sketch, "E290", {"start": v(-13929.83, 8490.24) * mm, "end": v(-13930.37, 8490.82) * mm});
            skLineSegment(sketch, "E291", {"start": v(-13930.37, 8490.82) * mm, "end": v(-13930.93, 8491.37) * mm});
            skLineSegment(sketch, "E292", {"start": v(-13930.93, 8491.37) * mm, "end": v(-13931.53, 8491.9) * mm});
            skLineSegment(sketch, "E293", {"start": v(-13931.53, 8491.9) * mm, "end": v(-13932.15, 8492.4) * mm});
            skLineSegment(sketch, "E294", {"start": v(-13932.15, 8492.4) * mm, "end": v(-13932.8, 8492.85) * mm});
            skLineSegment(sketch, "E295", {"start": v(-13932.8, 8492.85) * mm, "end": v(-13933.47, 8493.27) * mm});
            skLineSegment(sketch, "E296", {"start": v(-13933.47, 8493.27) * mm, "end": v(-13934.16, 8493.66) * mm});
            skLineSegment(sketch, "E297", {"start": v(-13934.16, 8493.66) * mm, "end": v(-13934.87, 8494.01) * mm});
            skLineSegment(sketch, "E298", {"start": v(-13934.87, 8494.01) * mm, "end": v(-13935.6, 8494.33) * mm});
            skLineSegment(sketch, "E299", {"start": v(-13935.6, 8494.33) * mm, "end": v(-13936.34, 8494.6) * mm});
            skLineSegment(sketch, "E300", {"start": v(-13936.34, 8494.6) * mm, "end": v(-13937.1, 8494.84) * mm});
            skLineSegment(sketch, "E301", {"start": v(-13937.1, 8494.84) * mm, "end": v(-13937.87, 8495.04) * mm});
            skLineSegment(sketch, "E302", {"start": v(-13937.87, 8495.04) * mm, "end": v(-13938.65, 8495.2) * mm});
            skLineSegment(sketch, "E303", {"start": v(-13938.65, 8495.2) * mm, "end": v(-13939.43, 8495.3) * mm});
            skLineSegment(sketch, "E304", {"start": v(-13939.43, 8495.3) * mm, "end": v(-13940.22, 8495.38) * mm});
            skLineSegment(sketch, "E305", {"start": v(-13940.22, 8495.38) * mm, "end": v(-13941.01, 8495.41) * mm});
            skLineSegment(sketch, "E306", {"start": v(-13941.01, 8495.41) * mm, "end": v(-13941.8, 8495.4) * mm});
            skLineSegment(sketch, "E307", {"start": v(-13941.8, 8495.4) * mm, "end": v(-13942.6, 8495.35) * mm});
            skLineSegment(sketch, "E308", {"start": v(-13942.6, 8495.35) * mm, "end": v(-13943.39, 8495.26) * mm});
            skLineSegment(sketch, "E309", {"start": v(-13943.39, 8495.26) * mm, "end": v(-13944.17, 8495.13) * mm});
            skLineSegment(sketch, "E310", {"start": v(-13944.17, 8495.13) * mm, "end": v(-13944.94, 8494.95) * mm});
            skLineSegment(sketch, "E311", {"start": v(-13944.94, 8494.95) * mm, "end": v(-13945.7, 8494.74) * mm});
            skLineSegment(sketch, "E312", {"start": v(-13945.7, 8494.74) * mm, "end": v(-13946.46, 8494.49) * mm});
            skLineSegment(sketch, "E313", {"start": v(-13946.46, 8494.49) * mm, "end": v(-13947.2, 8494.2) * mm});
            skLineSegment(sketch, "E314", {"start": v(-13947.2, 8494.2) * mm, "end": v(-13947.92, 8493.86) * mm});
            skLineSegment(sketch, "E315", {"start": v(-13947.92, 8493.86) * mm, "end": v(-13948.62, 8493.5) * mm});
            skLineSegment(sketch, "E316", {"start": v(-13948.62, 8493.5) * mm, "end": v(-13949.3, 8493.09) * mm});
            skLineSegment(sketch, "E317", {"start": v(-13949.3, 8493.09) * mm, "end": v(-13949.96, 8492.65) * mm});
            skLineSegment(sketch, "E318", {"start": v(-13949.96, 8492.65) * mm, "end": v(-13950.6, 8492.17) * mm});
            skLineSegment(sketch, "E319", {"start": v(-13950.6, 8492.17) * mm, "end": v(-13951.21, 8491.67) * mm});
            skLineSegment(sketch, "E320", {"start": v(-13951.21, 8491.67) * mm, "end": v(-13951.8, 8491.13) * mm});
            skLineSegment(sketch, "E321", {"start": v(-13951.8, 8491.13) * mm, "end": v(-13952.35, 8490.56) * mm});
            skLineSegment(sketch, "E322", {"start": v(-13952.35, 8490.56) * mm, "end": v(-13952.87, 8489.97) * mm});
            skLineSegment(sketch, "E323", {"start": v(-13952.87, 8489.97) * mm, "end": v(-13953.36, 8489.34) * mm});
            skLineSegment(sketch, "E324", {"start": v(-13953.36, 8489.34) * mm, "end": v(-13953.82, 8488.7) * mm});
            skLineSegment(sketch, "E325", {"start": v(-13953.82, 8488.7) * mm, "end": v(-13954.25, 8488.03) * mm});
            skLineSegment(sketch, "E326", {"start": v(-13954.25, 8488.03) * mm, "end": v(-13954.64, 8487.33) * mm});
            skLineSegment(sketch, "E327", {"start": v(-13954.64, 8487.33) * mm, "end": v(-13954.99, 8486.62) * mm});
            skLineSegment(sketch, "E328", {"start": v(-13954.99, 8486.62) * mm, "end": v(-13955.3, 8485.9) * mm});
            skLineSegment(sketch, "E329", {"start": v(-13955.3, 8485.9) * mm, "end": v(-13955.58, 8485.15) * mm});
            skLineSegment(sketch, "E330", {"start": v(-13955.58, 8485.15) * mm, "end": v(-13955.81, 8484.4) * mm});
            skLineSegment(sketch, "E331", {"start": v(-13955.81, 8484.4) * mm, "end": v(-13956.01, 8483.63) * mm});
            skLineSegment(sketch, "E332", {"start": v(-13956.01, 8483.63) * mm, "end": v(-13956.17, 8482.85) * mm});
            skLineSegment(sketch, "E333", {"start": v(-13956.17, 8482.85) * mm, "end": v(-13956.23, 8482.41) * mm});
            skLineSegment(sketch, "E334", {"start": v(-13956.23, 8482.41) * mm, "end": v(-13956.23, 8444.41) * mm});
            skCircle(sketch, "E335", {"center": v(-13940.73, 8462.91) * mm, "radius": 10.12 * mm});
            skLineSegment(sketch, "E336", {"start": v(-12857.83, 6827.41) * mm, "end": v(-14885.8, 6847.7) * mm});
            skLineSegment(sketch, "E337", {"start": v(-14851.53, 9154.72) * mm, "end": v(-14851.53, 6999.45) * mm});
            skLineSegment(sketch, "E338", {"start": v(-14885.8, 9154.47) * mm, "end": v(-14885.8, 6847.7) * mm});
            skLineSegment(sketch, "E339", {"start": v(-14467.23, 8390.69) * mm, "end": v(-14276.23, 8390.69) * mm});
            skLineSegment(sketch, "E340", {"start": v(-14276.23, 8390.69) * mm, "end": v(-14276.23, 8538.41) * mm});
            skLineSegment(sketch, "E341", {"start": v(-14276.23, 8538.41) * mm, "end": v(-14467.23, 8538.41) * mm});
            skLineSegment(sketch, "E342", {"start": v(-14467.23, 8538.41) * mm, "end": v(-14467.23, 8390.69) * mm});
            skLineSegment(sketch, "E343", {"start": v(-15072.23, 9268.41) * mm, "end": v(-13305.54, 9285.97) * mm});
            skLineSegment(sketch, "E344", {"start": v(-13233.16, 9166.26) * mm, "end": v(-13206.32, 9166.45) * mm});
            skLineSegment(sketch, "E345", {"start": v(-13002.45, 9045.41) * mm, "end": v(-13209.32, 9045.41) * mm});
            skLineSegment(sketch, "E346", {"start": v(-13338.72, 9236.45) * mm, "end": v(-15011.23, 9213.41) * mm});
            skLineSegment(sketch, "E347", {"start": v(-14946.3, 9214.3) * mm, "end": v(-14945.88, 9154.05) * mm});
            skLineSegment(sketch, "E348", {"start": v(-13158.35, 9365.41) * mm, "end": v(-14648.23, 9365.41) * mm});
            skLineSegment(sketch, "E349", {"start": v(-14648.23, 9365.41) * mm, "end": v(-14973.98, 9360.84) * mm});
            skLineSegment(sketch, "E350", {"start": v(-14973.98, 9360.84) * mm, "end": v(-14976.01, 9269.37) * mm});
            skLineSegment(sketch, "E351", {"start": v(-14902.57, 7834.41) * mm, "end": v(-16815.1, 7834.41) * mm});
            skLineSegment(sketch, "E352", {"start": v(-14902.57, 9133.41) * mm, "end": v(-16815.1, 9133.41) * mm});
            skLineSegment(sketch, "E353", {"start": v(-14902.57, 7801.41) * mm, "end": v(-16815.1, 7801.41) * mm});
            skLineSegment(sketch, "E354", {"start": v(-14945.88, 9154.05) * mm, "end": v(-13308.81, 9165.72) * mm});
            skLineSegment(sketch, "E355", {"start": v(-14902.57, 9154.36) * mm, "end": v(-14902.57, 7801.41) * mm});
            skLineSegment(sketch, "E356", {"start": v(-16815.1, 9157.56) * mm, "end": v(-16815.1, 7801.41) * mm});
            skLineSegment(sketch, "E357", {"start": v(-14902.57, 7858.41) * mm, "end": v(-16815.1, 7858.41) * mm});
            skLineSegment(sketch, "E358", {"start": v(-16295.23, 9086.41) * mm, "end": v(-16698.23, 9086.41) * mm});
            skLineSegment(sketch, "E359", {"start": v(-16698.23, 9086.41) * mm, "end": v(-16698.23, 9068.41) * mm});
            skLineSegment(sketch, "E360", {"start": v(-16698.23, 9068.41) * mm, "end": v(-16295.23, 9068.41) * mm});
            skLineSegment(sketch, "E361", {"start": v(-16295.23, 9068.41) * mm, "end": v(-16295.23, 9086.41) * mm});
            skLineSegment(sketch, "E362", {"start": v(-16279.23, 7970.41) * mm, "end": v(-16723.23, 7970.41) * mm});
            skLineSegment(sketch, "E363", {"start": v(-16268.23, 7959.41) * mm, "end": v(-16734.23, 7959.41) * mm});
            skLineSegment(sketch, "E364", {"start": v(-16215.23, 7906.41) * mm, "end": v(-16787.23, 7906.41) * mm});
            skLineSegment(sketch, "E365", {"start": v(-16204.23, 7897.41) * mm, "end": v(-16796.23, 7897.41) * mm});
            skLineSegment(sketch, "E366", {"start": v(-16279.23, 9038.41) * mm, "end": v(-16279.23, 7970.41) * mm});
            skLineSegment(sketch, "E367", {"start": v(-16268.23, 9049.41) * mm, "end": v(-16268.23, 7959.41) * mm});
            skLineSegment(sketch, "E368", {"start": v(-16215.23, 9102.41) * mm, "end": v(-16215.23, 7906.41) * mm});
            skLineSegment(sketch, "E369", {"start": v(-16204.23, 9111.41) * mm, "end": v(-16204.23, 7897.41) * mm});
            skLineSegment(sketch, "E370", {"start": v(-16723.23, 7970.41) * mm, "end": v(-16723.23, 9038.41) * mm});
            skLineSegment(sketch, "E371", {"start": v(-16723.23, 9038.41) * mm, "end": v(-16279.23, 9038.41) * mm});
            skLineSegment(sketch, "E372", {"start": v(-16734.23, 9049.41) * mm, "end": v(-16268.23, 9049.41) * mm});
            skLineSegment(sketch, "E373", {"start": v(-16734.23, 7959.41) * mm, "end": v(-16734.23, 9049.41) * mm});
            skLineSegment(sketch, "E374", {"start": v(-16787.23, 7906.41) * mm, "end": v(-16787.23, 9102.41) * mm});
            skLineSegment(sketch, "E375", {"start": v(-16787.23, 9102.41) * mm, "end": v(-16215.23, 9102.41) * mm});
            skLineSegment(sketch, "E376", {"start": v(-16796.23, 9111.41) * mm, "end": v(-16204.23, 9111.41) * mm});
            skLineSegment(sketch, "E377", {"start": v(-16796.23, 7897.41) * mm, "end": v(-16796.23, 9111.41) * mm});
            skLineSegment(sketch, "E378", {"start": v(-10984.23, 9133.41) * mm, "end": v(-10349.23, 9133.41) * mm});
            skLineSegment(sketch, "E379", {"start": v(-10349.23, 9133.41) * mm, "end": v(-10349.23, 7635.41) * mm});
            skLineSegment(sketch, "E380", {"start": v(-10349.23, 7635.41) * mm, "end": v(-10984.23, 7635.41) * mm});
            skLineSegment(sketch, "E381", {"start": v(-10984.23, 7635.41) * mm, "end": v(-10984.23, 9133.41) * mm});
            skLineSegment(sketch, "E382", {"start": v(-10965.23, 9114.41) * mm, "end": v(-10368.23, 9114.41) * mm});
            skLineSegment(sketch, "E383", {"start": v(-10368.23, 9114.41) * mm, "end": v(-10368.23, 7654.41) * mm});
            skLineSegment(sketch, "E384", {"start": v(-10368.23, 7654.41) * mm, "end": v(-10965.23, 7654.41) * mm});
            skLineSegment(sketch, "E385", {"start": v(-10965.23, 7654.41) * mm, "end": v(-10965.23, 9114.41) * mm});
            skLineSegment(sketch, "E386", {"start": v(-15018.23, 9085.41) * mm, "end": v(-15421.23, 9085.41) * mm});
            skLineSegment(sketch, "E387", {"start": v(-15421.23, 9085.41) * mm, "end": v(-15421.23, 9067.41) * mm});
            skLineSegment(sketch, "E388", {"start": v(-15421.23, 9067.41) * mm, "end": v(-15018.23, 9067.41) * mm});
            skLineSegment(sketch, "E389", {"start": v(-15018.23, 9067.41) * mm, "end": v(-15018.23, 9085.41) * mm});
            skLineSegment(sketch, "E390", {"start": v(-15002.23, 7969.41) * mm, "end": v(-15446.23, 7969.41) * mm});
            skLineSegment(sketch, "E391", {"start": v(-14991.23, 7958.41) * mm, "end": v(-15457.23, 7958.41) * mm});
            skLineSegment(sketch, "E392", {"start": v(-14938.23, 7905.41) * mm, "end": v(-15510.23, 7905.41) * mm});
            skLineSegment(sketch, "E393", {"start": v(-14927.23, 7896.41) * mm, "end": v(-15519.23, 7896.41) * mm});
            skLineSegment(sketch, "E394", {"start": v(-15002.23, 9037.41) * mm, "end": v(-15002.23, 7969.41) * mm});
            skLineSegment(sketch, "E395", {"start": v(-14991.23, 9048.41) * mm, "end": v(-14991.23, 7958.41) * mm});
            skLineSegment(sketch, "E396", {"start": v(-14938.23, 9101.41) * mm, "end": v(-14938.23, 7905.41) * mm});
            skLineSegment(sketch, "E397", {"start": v(-14927.23, 9110.41) * mm, "end": v(-14927.23, 7896.41) * mm});
            skLineSegment(sketch, "E398", {"start": v(-15446.23, 7969.41) * mm, "end": v(-15446.23, 9037.41) * mm});
            skLineSegment(sketch, "E399", {"start": v(-15446.23, 9037.41) * mm, "end": v(-15002.23, 9037.41) * mm});
            skLineSegment(sketch, "E400", {"start": v(-15457.23, 9048.41) * mm, "end": v(-14991.23, 9048.41) * mm});
            skLineSegment(sketch, "E401", {"start": v(-15457.23, 7958.41) * mm, "end": v(-15457.23, 9048.41) * mm});
            skLineSegment(sketch, "E402", {"start": v(-15510.23, 7905.41) * mm, "end": v(-15510.23, 9101.41) * mm});
            skLineSegment(sketch, "E403", {"start": v(-15510.23, 9101.41) * mm, "end": v(-14938.23, 9101.41) * mm});
            skLineSegment(sketch, "E404", {"start": v(-15519.23, 9110.41) * mm, "end": v(-14927.23, 9110.41) * mm});
            skLineSegment(sketch, "E405", {"start": v(-15519.23, 7896.41) * mm, "end": v(-15519.23, 9110.41) * mm});
            skLineSegment(sketch, "E406", {"start": v(-14885.8, 6847.7) * mm, "end": v(-17738.13, 6856.46) * mm});
            skLineSegment(sketch, "E407", {"start": v(-17739.24, 9152.34) * mm, "end": v(-17738.13, 6856.46) * mm});
            skLineSegment(sketch, "E408", {"start": v(-18035.63, 9266.6) * mm, "end": v(-18035.23, 9212.42) * mm});
            skLineSegment(sketch, "E409", {"start": v(-17955.57, 9275.35) * mm, "end": v(-17955.53, 9267.3) * mm});
            skLineSegment(sketch, "E410", {"start": v(-17955.22, 9213) * mm, "end": v(-17954.87, 9151.12) * mm});
            skLineSegment(sketch, "E411", {"start": v(-15053.68, 9234.01) * mm, "end": v(-18035.23, 9212.42) * mm});
            skLineSegment(sketch, "E412", {"start": v(-14975.32, 9300.73) * mm, "end": v(-16889.07, 9283.2) * mm});
            skLineSegment(sketch, "E413", {"start": v(-16889.07, 9283.2) * mm, "end": v(-17760.26, 9272.19) * mm});
            skLineSegment(sketch, "E414", {"start": v(-17760.26, 9272.19) * mm, "end": v(-18010.71, 9276.24) * mm});
            skLineSegment(sketch, "E415", {"start": v(-17954.87, 9151.12) * mm, "end": v(-14945.98, 9168.12) * mm});
            skLineSegment(sketch, "E416", {"start": v(-14975.5, 9292.69) * mm, "end": v(-18035.63, 9266.6) * mm});
            skLineSegment(sketch, "E417", {"start": v(-18010.71, 9276.24) * mm, "end": v(-18002.23, 10025.41) * mm});
            skLineSegment(sketch, "E418", {"start": v(-18002.23, 10025.41) * mm, "end": v(-17992.23, 11067.41) * mm});
            skLineSegment(sketch, "E419", {"start": v(-17992.23, 11067.41) * mm, "end": v(-18004.23, 11624.41) * mm});
            skLineSegment(sketch, "E420", {"start": v(-18004.23, 11624.41) * mm, "end": v(-18004.23, 11744.89) * mm});
            skLineSegment(sketch, "E421", {"start": v(-18004.23, 11744.89) * mm, "end": v(-17859.23, 11739.41) * mm});
            skArc(sketch, "E422", {"start": v(9151.83, 11739.42) * mm, "mid": v(9114.75, 11744.93) * mm, "end": v(9077.83, 11738.42) * mm});
            skLineSegment(sketch, "E423", {"start": v(14089.1, 9291.47) * mm, "end": v(13813.83, 9445.41) * mm});
            skLineSegment(sketch, "E424", {"start": v(13813.83, 9445.41) * mm, "end": v(11724.83, 10460.41) * mm});
            skLineSegment(sketch, "E425", {"start": v(11724.83, 10460.41) * mm, "end": v(9546.83, 11513.41) * mm});
            skLineSegment(sketch, "E426", {"start": v(9546.83, 11513.41) * mm, "end": v(9266.78, 11631.72) * mm});
            skLineSegment(sketch, "E427", {"start": v(9162.83, 11731.41) * mm, "end": v(9151.83, 11739.41) * mm});
            skLineSegment(sketch, "E428", {"start": v(9249.52, 11658.64) * mm, "end": v(9162.83, 11731.41) * mm});
            skLineSegment(sketch, "E429", {"start": v(9266.78, 11631.72) * mm, "end": v(9249.52, 11658.64) * mm});
            skLineSegment(sketch, "E430", {"start": v(-14974.98, 9315.96) * mm, "end": v(-16889.23, 9298.41) * mm});
            skLineSegment(sketch, "E431", {"start": v(-16889.23, 9298.41) * mm, "end": v(-17760.23, 9287.41) * mm});
            skLineSegment(sketch, "E432", {"start": v(-17760.23, 9287.41) * mm, "end": v(-18010.54, 9291.47) * mm});
            skLineSegment(sketch, "E433", {"start": v(13751.68, 6880.96) * mm, "end": v(13702.7, 6929.94) * mm});
            skLineSegment(sketch, "E434", {"start": v(13702.7, 6929.94) * mm, "end": v(13678.43, 6856.54) * mm});
            skLineSegment(sketch, "E435", {"start": v(13678.43, 6856.54) * mm, "end": v(13751.68, 6880.96) * mm});
            skLineSegment(sketch, "E436", {"start": v(-17762.63, 6929.96) * mm, "end": v(-17811.62, 6880.97) * mm});
            skLineSegment(sketch, "E437", {"start": v(-17811.62, 6880.97) * mm, "end": v(-17738.22, 6856.7) * mm});
            skLineSegment(sketch, "E438", {"start": v(-17738.22, 6856.7) * mm, "end": v(-17762.63, 6929.96) * mm});
            skLineSegment(sketch, "E439", {"start": v(-18028.37, 9126.62) * mm, "end": v(-17979.39, 9077.63) * mm});
            skLineSegment(sketch, "E440", {"start": v(-17979.39, 9077.63) * mm, "end": v(-17955.12, 9151.03) * mm});
            skLineSegment(sketch, "E441", {"start": v(-17955.12, 9151.03) * mm, "end": v(-18028.37, 9126.62) * mm});
            skLineSegment(sketch, "E442", {"start": v(13596.9, 9261.5) * mm, "end": v(11222.83, 10431.41) * mm});
            skLineSegment(sketch, "E443", {"start": v(13595.75, 9170.36) * mm, "end": v(13596.9, 9261.5) * mm});
            skLineSegment(sketch, "E444", {"start": v(14036.83, 9151.12) * mm, "end": v(13595.75, 9170.36) * mm});
            skLineSegment(sketch, "E445", {"start": v(13678.18, 6856.46) * mm, "end": v(13681.83, 9166.1) * mm});
            skLineSegment(sketch, "E446", {"start": v(14061.33, 9077.62) * mm, "end": v(14110.31, 9126.6) * mm});
            skLineSegment(sketch, "E447", {"start": v(14110.31, 9126.6) * mm, "end": v(14036.91, 9150.87) * mm});
            skLineSegment(sketch, "E448", {"start": v(14036.91, 9150.87) * mm, "end": v(14061.33, 9077.62) * mm});
            skLineSegment(sketch, "E449", {"start": v(14044.18, 9266.64) * mm, "end": v(14187.96, 9266.6) * mm});
            skEllipticalArc(sketch, "E450", {});
            skLineSegment(sketch, "E451", {"start": v(13927.83, 9306.41) * mm, "end": v(14086.47, 9276.24) * mm});
            skLineSegment(sketch, "E452", {"start": v(14086.47, 9276.24) * mm, "end": v(14089.1, 9291.47) * mm});
            skLineSegment(sketch, "E453", {"start": v(14036.83, 9285.68) * mm, "end": v(14036.83, 9151.12) * mm});
            skLineSegment(sketch, "E454", {"start": v(9149.75, 11814.93) * mm, "end": v(9079.77, 11814.93) * mm});
            skLineSegment(sketch, "E455", {"start": v(9079.77, 11814.93) * mm, "end": v(9114.87, 11745.16) * mm});
            skLineSegment(sketch, "E456", {"start": v(9114.87, 11745.16) * mm, "end": v(9149.75, 11814.93) * mm});
            skLineSegment(sketch, "E457", {"start": v(-17969.23, 11814.89) * mm, "end": v(-18039.2, 11814.89) * mm});
            skLineSegment(sketch, "E458", {"start": v(-18039.2, 11814.89) * mm, "end": v(-18004.12, 11745.12) * mm});
            skLineSegment(sketch, "E459", {"start": v(-18004.12, 11745.12) * mm, "end": v(-17969.23, 11814.89) * mm});
            skLineSegment(sketch, "E460", {"start": v(-8550.23, 11722.41) * mm, "end": v(-8209.23, 11726.41) * mm});
            skLineSegment(sketch, "E461", {"start": v(-8441.23, 8330.41) * mm, "end": v(-8441.23, 6827.41) * mm});
            skLineSegment(sketch, "E462", {"start": v(-8488.7, 8330.41) * mm, "end": v(-8441.23, 8330.41) * mm});
            skLineSegment(sketch, "E463", {"start": v(-12857.83, 6827.41) * mm, "end": v(-8395.83, 6827.41) * mm});
            skLineSegment(sketch, "E464", {"start": v(-8395.83, 6827.41) * mm, "end": v(-8376.23, 8853.41) * mm});
            skLineSegment(sketch, "E465", {"start": v(-8203.82, 9429.16) * mm, "end": v(-8224.23, 10783.41) * mm});
            skLineSegment(sketch, "E466", {"start": v(-8224.23, 10783.41) * mm, "end": v(-8214.23, 11626.41) * mm});
            skLineSegment(sketch, "E467", {"start": v(-8214.23, 11626.41) * mm, "end": v(-8207.23, 11656.41) * mm});
            skLineSegment(sketch, "E468", {"start": v(-8207.23, 11656.41) * mm, "end": v(-8209.23, 11726.41) * mm});
            skLineSegment(sketch, "E469", {"start": v(-8203.82, 9429.16) * mm, "end": v(-8312.13, 9430.61) * mm});
            skLineSegment(sketch, "E470", {"start": v(-8204.22, 9455.4) * mm, "end": v(-8367.8, 9457.6) * mm});
            skArc(sketch, "E471", {"start": v(3219.44, -8529.59) * mm, "mid": v(3190.47, -8523.51) * mm, "end": v(3161.63, -8530.15) * mm});
            skLineSegment(sketch, "E472", {"start": v(-1416.56, -10794.59) * mm, "end": v(-1144.56, -10627.59) * mm});
            skLineSegment(sketch, "E473", {"start": v(-1144.56, -10627.59) * mm, "end": v(-849.56, -10474.59) * mm});
            skLineSegment(sketch, "E474", {"start": v(-849.56, -10474.59) * mm, "end": v(644.44, -9754.59) * mm});
            skLineSegment(sketch, "E475", {"start": v(644.44, -9754.59) * mm, "end": v(2808.44, -8718.59) * mm});
            skLineSegment(sketch, "E476", {"start": v(2808.44, -8718.59) * mm, "end": v(3039.87, -8623.59) * mm});
            skLineSegment(sketch, "E477", {"start": v(3052.87, -8593.59) * mm, "end": v(3161.63, -8530.15) * mm});
            skLineSegment(sketch, "E478", {"start": v(3039.87, -8623.59) * mm, "end": v(3052.87, -8593.59) * mm});
            skLineSegment(sketch, "E479", {"start": v(-1400.44, -10820.84) * mm, "end": v(-1416.56, -10794.59) * mm});
            skLineSegment(sketch, "E480", {"start": v(-1197.56, -10753.59) * mm, "end": v(-1400.44, -10820.84) * mm});
            skLineSegment(sketch, "E481", {"start": v(-1335.56, -10890.02) * mm, "end": v(-1300.56, -10890.59) * mm});
            skLineSegment(sketch, "E482", {"start": v(-1335.56, -10890.02) * mm, "end": v(-1335.56, -10799.33) * mm});
            skLineSegment(sketch, "E483", {"start": v(-3775.56, -10408.59) * mm, "end": v(-3781.88, -10956.59) * mm});
            skLineSegment(sketch, "E484", {"start": v(-3781.54, -10926.59) * mm, "end": v(-2368.56, -10943.59) * mm});
            skLineSegment(sketch, "E485", {"start": v(-2368.56, -10943.59) * mm, "end": v(-1575.56, -10954.59) * mm});
            skLineSegment(sketch, "E486", {"start": v(-1575.56, -10954.59) * mm, "end": v(-1301.53, -10950.57) * mm});
            skLineSegment(sketch, "E487", {"start": v(-1300.56, -10890.59) * mm, "end": v(-1301.53, -10950.57) * mm});
            skLineSegment(sketch, "E488", {"start": v(-1301.53, -10950.57) * mm, "end": v(-1301.69, -10979.28) * mm});
            skLineSegment(sketch, "E489", {"start": v(-3781.88, -10956.59) * mm, "end": v(-2368.92, -10973.22) * mm});
            skLineSegment(sketch, "E490", {"start": v(-2368.92, -10973.22) * mm, "end": v(-1301.69, -10979.28) * mm});
            skLineSegment(sketch, "E491", {"start": v(-3793.6, -11037.57) * mm, "end": v(-3019.56, -11040.59) * mm});
            skLineSegment(sketch, "E492", {"start": v(-3790.7, -10976.58) * mm, "end": v(-3793.6, -11037.57) * mm});
            skLineSegment(sketch, "E493", {"start": v(-3790.7, -10976.58) * mm, "end": v(-3016.65, -10979.6) * mm});
            skArc(sketch, "E494", {"start": v(-1229.28, -11065.65) * mm, "mid": v(-1191.62, -11051.16) * mm, "end": v(-1174.56, -11014.58) * mm});
            skLineSegment(sketch, "E495", {"start": v(-3016.65, -10979.6) * mm, "end": v(-1463.56, -11004.59) * mm});
            skLineSegment(sketch, "E496", {"start": v(-1229.28, -11065.65) * mm, "end": v(-1447.89, -11058.08) * mm});
            skLineSegment(sketch, "E497", {"start": v(-3725, -10957.26) * mm, "end": v(-3725.23, -10976.84) * mm});
            skLineSegment(sketch, "E498", {"start": v(-3725.91, -11037.84) * mm, "end": v(-3726.55, -11095) * mm});
            skLineSegment(sketch, "E499", {"start": v(-3796.56, -9643.59) * mm, "end": v(-3793.55, -9711.34) * mm});
            skLineSegment(sketch, "E500", {"start": v(-3792.22, -9747.12) * mm, "end": v(-3775.56, -10408.59) * mm});
            skLineSegment(sketch, "E501", {"start": v(-3792.22, -9747.12) * mm, "end": v(-3793.55, -9711.34) * mm});
            skLineSegment(sketch, "E502", {"start": v(-3792.22, -9747.12) * mm, "end": v(-1944.14, -9768.06) * mm});
            skLineSegment(sketch, "E503", {"start": v(-1944.14, -9768.06) * mm, "end": v(-540.51, -9795.05) * mm});
            skLineSegment(sketch, "E504", {"start": v(-540.51, -9795.05) * mm, "end": v(519.7, -9814.7) * mm});
            skLineSegment(sketch, "E505", {"start": v(-3793.55, -9711.34) * mm, "end": v(-1943.6, -9732.3) * mm});
            skLineSegment(sketch, "E506", {"start": v(-1943.6, -9732.3) * mm, "end": v(-539.84, -9759.3) * mm});
            skLineSegment(sketch, "E507", {"start": v(-539.84, -9759.3) * mm, "end": v(591.17, -9780.26) * mm});
            skLineSegment(sketch, "E508", {"start": v(-3761.56, -9573.59) * mm, "end": v(-3831.53, -9573.59) * mm});
            skLineSegment(sketch, "E509", {"start": v(-3831.53, -9573.59) * mm, "end": v(-3796.44, -9643.35) * mm});
            skLineSegment(sketch, "E510", {"start": v(-3796.44, -9643.35) * mm, "end": v(-3761.56, -9573.59) * mm});
            skLineSegment(sketch, "E511", {"start": v(-10644.4, 10676.41) * mm, "end": v(-10714.37, 10676.41) * mm});
            skLineSegment(sketch, "E512", {"start": v(-10714.37, 10676.41) * mm, "end": v(-10679.28, 10606.65) * mm});
            skLineSegment(sketch, "E513", {"start": v(-10679.28, 10606.65) * mm, "end": v(-10644.4, 10676.41) * mm});
            skLineSegment(sketch, "E514", {"start": v(-8165.9, 9228.5) * mm, "end": v(-8214.88, 9179.52) * mm});
            skLineSegment(sketch, "E515", {"start": v(-8214.88, 9179.52) * mm, "end": v(-8141.48, 9155.25) * mm});
            skLineSegment(sketch, "E516", {"start": v(-8141.48, 9155.25) * mm, "end": v(-8165.9, 9228.5) * mm});
            skLineSegment(sketch, "E517", {"start": v(-3800.05, -11119.5) * mm, "end": v(-3751.07, -11168.48) * mm});
            skLineSegment(sketch, "E518", {"start": v(-3751.07, -11168.48) * mm, "end": v(-3726.8, -11095.08) * mm});
            skLineSegment(sketch, "E519", {"start": v(-3726.8, -11095.08) * mm, "end": v(-3800.05, -11119.5) * mm});
            skLineSegment(sketch, "E520", {"start": v(-3555.36, -13422.59) * mm, "end": v(-3560.58, -11095.96) * mm});
            skLineSegment(sketch, "E521", {"start": v(3720.44, -13344.59) * mm, "end": v(1958.44, -13366.59) * mm});
            skLineSegment(sketch, "E522", {"start": v(1958.44, -13366.59) * mm, "end": v(-1225.56, -13345.59) * mm});
            skLineSegment(sketch, "E523", {"start": v(-1225.56, -13345.59) * mm, "end": v(-3555.36, -13422.59) * mm});
            skLineSegment(sketch, "E524", {"start": v(-2850.03, -11042.47) * mm, "end": v(-1447.89, -11058.08) * mm});
            skLineSegment(sketch, "E525", {"start": v(-2895.56, -11106.59) * mm, "end": v(-2850.03, -11042.47) * mm});
            skLineSegment(sketch, "E526", {"start": v(-2970.56, -11109.59) * mm, "end": v(-3019.56, -11040.59) * mm});
            skLineSegment(sketch, "E527", {"start": v(-2890.78, -11099.85) * mm, "end": v(-2076.56, -11104.59) * mm});
            skLineSegment(sketch, "E528", {"start": v(-3726.55, -11095) * mm, "end": v(-2977.83, -11099.35) * mm});
            skLineSegment(sketch, "E529", {"start": v(-2874.56, -11901.59) * mm, "end": v(-2871.2, -13399.97) * mm});
            skLineSegment(sketch, "E530", {"start": v(-2949.56, -11902.59) * mm, "end": v(-2946.2, -13402.45) * mm});
            skLineSegment(sketch, "E531", {"start": v(-2076.56, -11104.59) * mm, "end": v(-1316.11, -11116.72) * mm});
            skLineSegment(sketch, "E532", {"start": v(-1313.08, -10979.21) * mm, "end": v(-1313.76, -11009.77) * mm});
            skLineSegment(sketch, "E533", {"start": v(-1314.92, -11062.68) * mm, "end": v(-1316.11, -11116.72) * mm});
            skLineSegment(sketch, "E534", {"start": v(-3579.86, -13349.09) * mm, "end": v(-3628.84, -13398.07) * mm});
            skLineSegment(sketch, "E535", {"start": v(-3628.84, -13398.07) * mm, "end": v(-3555.44, -13422.34) * mm});
            skLineSegment(sketch, "E536", {"start": v(-3555.44, -13422.34) * mm, "end": v(-3579.86, -13349.09) * mm});
            skLineSegment(sketch, "E537", {"start": v(-8510.15, 6900.91) * mm, "end": v(-8559.13, 6851.93) * mm});
            skLineSegment(sketch, "E538", {"start": v(-8559.13, 6851.93) * mm, "end": v(-8485.73, 6827.66) * mm});
            skLineSegment(sketch, "E539", {"start": v(-8485.73, 6827.66) * mm, "end": v(-8510.15, 6900.91) * mm});
            skLineSegment(sketch, "E540", {"start": v(-8174.23, 11796.41) * mm, "end": v(-8244.2, 11796.41) * mm});
            skLineSegment(sketch, "E541", {"start": v(-8244.2, 11796.41) * mm, "end": v(-8209.12, 11726.65) * mm});
            skLineSegment(sketch, "E542", {"start": v(-8209.12, 11726.65) * mm, "end": v(-8174.23, 11796.41) * mm});
            skLineSegment(sketch, "E543", {"start": v(3225.47, -8453.51) * mm, "end": v(3155.5, -8453.51) * mm});
            skLineSegment(sketch, "E544", {"start": v(3155.5, -8453.51) * mm, "end": v(3190.59, -8523.28) * mm});
            skLineSegment(sketch, "E545", {"start": v(3190.59, -8523.28) * mm, "end": v(3225.47, -8453.51) * mm});
            skLineSegment(sketch, "E546", {"start": v(-1381.56, -10724.59) * mm, "end": v(-1451.53, -10724.59) * mm});
            skLineSegment(sketch, "E547", {"start": v(-1451.53, -10724.59) * mm, "end": v(-1416.44, -10794.35) * mm});
            skLineSegment(sketch, "E548", {"start": v(-1416.44, -10794.35) * mm, "end": v(-1381.56, -10724.59) * mm});
            skLineSegment(sketch, "E549", {"start": v(-8214.23, 11626.41) * mm, "end": v(-10372.31, 11609.3) * mm});
            skLineSegment(sketch, "E550", {"start": v(-8207.23, 11656.41) * mm, "end": v(-10372.2, 11637.84) * mm});
            skLineSegment(sketch, "E551", {"start": v(-8550.23, 11722.41) * mm, "end": v(-10371.94, 11712.28) * mm});
            skLineSegment(sketch, "E552", {"start": v(-11065.06, 11708.42) * mm, "end": v(-12864.23, 11698.41) * mm});
            skLineSegment(sketch, "E553", {"start": v(-12864.23, 11698.41) * mm, "end": v(-17859.23, 11739.41) * mm});
            skLineSegment(sketch, "E554", {"start": v(-11064.72, 11631.9) * mm, "end": v(-12864.34, 11616.45) * mm});
            skLineSegment(sketch, "E555", {"start": v(-12864.34, 11616.45) * mm, "end": v(-18004.23, 11658.64) * mm});
            skLineSegment(sketch, "E556", {"start": v(-11064.6, 11603.8) * mm, "end": v(-12864.38, 11589.53) * mm});
            skLineSegment(sketch, "E557", {"start": v(-12864.38, 11589.53) * mm, "end": v(-18004.23, 11631.72) * mm});
            skLineSegment(sketch, "E558", {"start": v(-13131.92, 9172.66) * mm, "end": v(-13180.9, 9221.64) * mm});
            skLineSegment(sketch, "E559", {"start": v(-13180.9, 9221.64) * mm, "end": v(-13205.17, 9148.24) * mm});
            skLineSegment(sketch, "E560", {"start": v(-13205.17, 9148.24) * mm, "end": v(-13131.92, 9172.66) * mm});
            skLineSegment(sketch, "E561", {"start": v(16065.33, 9074.66) * mm, "end": v(16114.31, 9123.64) * mm});
            skLineSegment(sketch, "E562", {"start": v(16114.31, 9123.64) * mm, "end": v(16040.91, 9147.9) * mm});
            skLineSegment(sketch, "E563", {"start": v(16040.91, 9147.9) * mm, "end": v(16065.33, 9074.66) * mm});
            skLineSegment(sketch, "E564", {"start": v(-22906.23, 10772.41) * mm, "end": v(-21881.23, 10772.41) * mm});
            skLineSegment(sketch, "E565", {"start": v(-22906.23, 9303.41) * mm, "end": v(-22906.23, 10772.41) * mm});
            skLineSegment(sketch, "E566", {"start": v(-21839.4, 9303.41) * mm, "end": v(-21839.4, 9384.41) * mm});
            skLineSegment(sketch, "E567", {"start": v(-21839.4, 9303.41) * mm, "end": v(-22906.23, 9303.41) * mm});
            skLineSegment(sketch, "E568", {"start": v(-21839.4, 9384.41) * mm, "end": v(-22906.23, 9384.41) * mm});
            skLineSegment(sketch, "E569", {"start": v(-21881.23, 10772.41) * mm, "end": v(-21881.23, 9384.41) * mm});
            skLineSegment(sketch, "E570", {"start": v(-20058.56, 6357.41) * mm, "end": v(-20349.06, 6357.41) * mm});
            skLineSegment(sketch, "E571", {"start": v(-20269.26, 11272.33) * mm, "end": v(-22906, 11273.53) * mm});
            skLineSegment(sketch, "E572", {"start": v(-20269.23, 11330.41) * mm, "end": v(-20269.26, 11272.33) * mm});
            skLineSegment(sketch, "E573", {"start": v(-20269.23, 11330.41) * mm, "end": v(-22905.98, 11331.61) * mm});
            skLineSegment(sketch, "E574", {"start": v(-20349.06, 6357.41) * mm, "end": v(-20349.06, 11272.36) * mm});
            skLineSegment(sketch, "E575", {"start": v(-20349.06, 11120.7) * mm, "end": v(-22906.08, 11121.85) * mm});
            skLineSegment(sketch, "E576", {"start": v(-20349.06, 11183.07) * mm, "end": v(-22906.05, 11184.23) * mm});
            skLineSegment(sketch, "E577", {"start": v(-21873.23, 8249.41) * mm, "end": v(-21873.23, 8558.41) * mm});
            skLineSegment(sketch, "E578", {"start": v(-21873.23, 8558.41) * mm, "end": v(-22993.23, 8558.41) * mm});
            skLineSegment(sketch, "E579", {"start": v(-22993.23, 8558.41) * mm, "end": v(-22993.23, 8249.41) * mm});
            skLineSegment(sketch, "E580", {"start": v(-20126.96, 14002.1) * mm, "end": v(-20159.23, 14029.41) * mm});
            skLineSegment(sketch, "E581", {"start": v(-20159.23, 14029.41) * mm, "end": v(-20162.35, 14091.81) * mm});
            skLineSegment(sketch, "E582", {"start": v(-20099.23, 13167.41) * mm, "end": v(-20642.19, 13151.36) * mm});
            skLineSegment(sketch, "E583", {"start": v(-20099.23, 13101.41) * mm, "end": v(-20099.23, 13167.41) * mm});
            skLineSegment(sketch, "E584", {"start": v(-20099.23, 13101.41) * mm, "end": v(-20640.23, 13085.41) * mm});
            skLineSegment(sketch, "E585", {"start": v(-20112.77, 12607.03) * mm, "end": v(-20120.78, 13100.78) * mm});
            skLineSegment(sketch, "E586", {"start": v(-20640.23, 13085.41) * mm, "end": v(-20642.19, 13151.36) * mm});
            skLineSegment(sketch, "E587", {"start": v(-20609.78, 13086.32) * mm, "end": v(-20598.23, 12705.41) * mm});
            skLineSegment(sketch, "E588", {"start": v(-20598.23, 12705.41) * mm, "end": v(-20650.23, 12581.41) * mm});
            skLineSegment(sketch, "E589", {"start": v(-20650.23, 12581.41) * mm, "end": v(-20534.23, 12578.41) * mm});
            skLineSegment(sketch, "E590", {"start": v(-20534.23, 12578.41) * mm, "end": v(-20112.77, 12607.03) * mm});
            skLineSegment(sketch, "E591", {"start": v(-20616.35, 13152.12) * mm, "end": v(-20630.53, 13661.4) * mm});
            skLineSegment(sketch, "E592", {"start": v(-20128.49, 13166.55) * mm, "end": v(-20142.72, 13677.7) * mm});
            skLineSegment(sketch, "E593", {"start": v(-20102.79, 13853.96) * mm, "end": v(-20099.9, 13767.6) * mm});
            skLineSegment(sketch, "E594", {"start": v(-20089.23, 13922.41) * mm, "end": v(-20086.97, 13854.5) * mm});
            skLineSegment(sketch, "E595", {"start": v(-20162.35, 14091.81) * mm, "end": v(-20653.23, 14075.41) * mm});
            skLineSegment(sketch, "E596", {"start": v(-20159.23, 14029.41) * mm, "end": v(-20651.3, 14012.98) * mm});
            skLineSegment(sketch, "E597", {"start": v(-20686.23, 13983.42) * mm, "end": v(-20651.3, 14012.98) * mm});
            skLineSegment(sketch, "E598", {"start": v(-20126.96, 14002.1) * mm, "end": v(-20686.23, 13983.42) * mm});
            skLineSegment(sketch, "E599", {"start": v(-20683.53, 13902.57) * mm, "end": v(-20686.23, 13983.42) * mm});
            skLineSegment(sketch, "E600", {"start": v(-20122.23, 13678.38) * mm, "end": v(-20125.18, 13766.75) * mm});
            skLineSegment(sketch, "E601", {"start": v(-20099.9, 13767.6) * mm, "end": v(-20691.97, 13747.82) * mm});
            skLineSegment(sketch, "E602", {"start": v(-20086.97, 13854.5) * mm, "end": v(-20713.82, 13833.55) * mm});
            skLineSegment(sketch, "E603", {"start": v(-20122.23, 13678.38) * mm, "end": v(-20660.52, 13660.4) * mm});
            skLineSegment(sketch, "E604", {"start": v(-20660.52, 13660.4) * mm, "end": v(-20666.67, 13748.66) * mm});
            skLineSegment(sketch, "E605", {"start": v(-20698, 13834.08) * mm, "end": v(-20691.97, 13747.82) * mm});
            skLineSegment(sketch, "E606", {"start": v(-20718.56, 13901.4) * mm, "end": v(-20713.82, 13833.55) * mm});
            skLineSegment(sketch, "E607", {"start": v(-20089.23, 13922.41) * mm, "end": v(-20718.56, 13901.4) * mm});
            skLineSegment(sketch, "E608", {"start": v(-20651.3, 14012.98) * mm, "end": v(-20653.23, 14075.41) * mm});
            skLineSegment(sketch, "E609", {"start": v(-20373.23, 14697.41) * mm, "end": v(-20255.38, 14704.46) * mm});
            skLineSegment(sketch, "E610", {"start": v(-20224.08, 14180.54) * mm, "end": v(-20255.38, 14704.46) * mm});
            skLineSegment(sketch, "E611", {"start": v(-20344.68, 14219.5) * mm, "end": v(-20373.23, 14697.41) * mm});
            skLineSegment(sketch, "E612", {"start": v(-20609.63, 13081.4) * mm, "end": v(-23709.23, 13104.41) * mm});
            skLineSegment(sketch, "E613", {"start": v(-20605.9, 12958.1) * mm, "end": v(-23710.15, 12981.15) * mm});
            skLineSegment(sketch, "E614", {"start": v(-20606.47, 12977.14) * mm, "end": v(-23710, 13000.17) * mm});
            skLineSegment(sketch, "E615", {"start": v(-20318.43, 11330.44) * mm, "end": v(-20069.84, 12651.44) * mm});
            skLineSegment(sketch, "E616", {"start": v(-20113.62, 12659.68) * mm, "end": v(-20069.84, 12651.44) * mm});
            skLineSegment(sketch, "E617", {"start": v(-11103.23, 12553.41) * mm, "end": v(-11103.23, 12498.41) * mm});
            skLineSegment(sketch, "E618", {"start": v(-10337.23, 12498.41) * mm, "end": v(-11103.23, 12498.41) * mm});
            skLineSegment(sketch, "E619", {"start": v(-10337.23, 12553.41) * mm, "end": v(-10337.23, 12498.41) * mm});
            skLineSegment(sketch, "E620", {"start": v(-10337.23, 12553.41) * mm, "end": v(-11103.23, 12553.41) * mm});
            skLineSegment(sketch, "E621", {"start": v(-22124.43, 13162.91) * mm, "end": v(-22194.4, 13162.91) * mm});
            skLineSegment(sketch, "E622", {"start": v(-22194.4, 13162.91) * mm, "end": v(-22159.31, 13093.15) * mm});
            skLineSegment(sketch, "E623", {"start": v(-22159.31, 13093.15) * mm, "end": v(-22124.43, 13162.91) * mm});
            skLineSegment(sketch, "E624", {"start": v(-20195.73, 11354.91) * mm, "end": v(-20244.72, 11403.9) * mm});
            skLineSegment(sketch, "E625", {"start": v(-20244.72, 11403.9) * mm, "end": v(-20268.99, 11330.5) * mm});
            skLineSegment(sketch, "E626", {"start": v(-20268.99, 11330.5) * mm, "end": v(-20195.73, 11354.91) * mm});
            skLineSegment(sketch, "E627", {"start": v(-20023.56, 6427.41) * mm, "end": v(-20093.54, 6427.41) * mm});
            skLineSegment(sketch, "E628", {"start": v(-20093.54, 6427.41) * mm, "end": v(-20058.45, 6357.65) * mm});
            skLineSegment(sketch, "E629", {"start": v(-20058.45, 6357.65) * mm, "end": v(-20023.56, 6427.41) * mm});
            skArc(sketch, "E630", {"start": v(8137.44, -10965.58) * mm, "mid": v(8201.5, -11037.59) * mm, "end": v(8274.44, -10974.58) * mm});
            skLineSegment(sketch, "E631", {"start": v(8137.44, -10965.59) * mm, "end": v(8274.44, -10974.59) * mm});
            skArc(sketch, "E632", {"start": v(7904.59, -11388.96) * mm, "mid": v(7888.37, -11402.8) * mm, "end": v(7882.32, -11423.23) * mm});
            skArc(sketch, "E633", {"start": v(8132.6, -11203.9) * mm, "mid": v(8147.08, -11192.08) * mm, "end": v(8154.06, -11174.73) * mm});
            skArc(sketch, "E634", {"start": v(7850.89, -11333.92) * mm, "mid": v(7819.14, -11361.6) * mm, "end": v(7807.32, -11402.01) * mm});
            skLineSegment(sketch, "E635", {"start": v(8132.6, -11203.9) * mm, "end": v(7850.89, -11333.92) * mm});
            skArc(sketch, "E636", {"start": v(8183.23, -11265.12) * mm, "mid": v(8213.33, -11240.83) * mm, "end": v(8227.32, -11204.78) * mm});
            skLineSegment(sketch, "E637", {"start": v(8183.23, -11265.12) * mm, "end": v(7904.59, -11388.96) * mm});
            skLineSegment(sketch, "E638", {"start": v(8247.18, -11024.02) * mm, "end": v(8227.32, -11204.78) * mm});
            skLineSegment(sketch, "E639", {"start": v(8173.13, -11029.35) * mm, "end": v(8154.06, -11174.73) * mm});
            skLineSegment(sketch, "E640", {"start": v(8138.07, -10936.28) * mm, "end": v(8137.87, -10965.61) * mm});
            skLineSegment(sketch, "E641", {"start": v(8137.8, -10976.89) * mm, "end": v(8137.05, -11086.71) * mm});
            skLineSegment(sketch, "E642", {"start": v(7882.32, -11423.23) * mm, "end": v(7882.32, -13291.52) * mm});
            skLineSegment(sketch, "E643", {"start": v(7882.32, -13291.52) * mm, "end": v(3720.44, -13344.59) * mm});
            skLineSegment(sketch, "E644", {"start": v(7807.32, -11402.01) * mm, "end": v(7807.32, -13292.48) * mm});
            skLineSegment(sketch, "E645", {"start": v(7776.82, -11079.14) * mm, "end": v(7776.82, -11409.58) * mm});
            skLineSegment(sketch, "E646", {"start": v(7778.44, -11409.58) * mm, "end": v(7716.44, -11409.58) * mm});
            skLineSegment(sketch, "E647", {"start": v(7716.44, -11409.58) * mm, "end": v(7716.44, -13293.64) * mm});
            skLineSegment(sketch, "E648", {"start": v(7778.44, -11409.58) * mm, "end": v(7778.44, -13292.85) * mm});
            skLineSegment(sketch, "E649", {"start": v(4434.55, -10916.59) * mm, "end": v(3583.03, -10916.59) * mm});
            skLineSegment(sketch, "E650", {"start": v(4434.55, -10916.59) * mm, "end": v(4434.55, -13199.59) * mm});
            skLineSegment(sketch, "E651", {"start": v(3583.03, -13199.59) * mm, "end": v(4434.55, -13199.59) * mm});
            skLineSegment(sketch, "E652", {"start": v(3583.03, -10916.59) * mm, "end": v(3583.03, -13199.59) * mm});
            skLineSegment(sketch, "E653", {"start": v(3583.03, -13171.59) * mm, "end": v(4434.55, -13171.59) * mm});
            skLineSegment(sketch, "E654", {"start": v(4434.55, -11140.59) * mm, "end": v(3583.03, -11140.59) * mm});
            skLineSegment(sketch, "E655", {"start": v(4381.01, -11200.59) * mm, "end": v(3638.72, -11200.59) * mm});
            skLineSegment(sketch, "E656", {"start": v(4434.55, -11168.59) * mm, "end": v(3583.03, -11168.59) * mm});
            skLineSegment(sketch, "E657", {"start": v(3638.72, -11200.59) * mm, "end": v(3638.72, -13161.59) * mm});
            skLineSegment(sketch, "E658", {"start": v(4381.01, -11200.59) * mm, "end": v(4381.01, -13161.59) * mm});
            skLineSegment(sketch, "E659", {"start": v(4381.01, -13161.59) * mm, "end": v(4434.55, -13161.59) * mm});
            skLineSegment(sketch, "E660", {"start": v(3638.72, -13161.59) * mm, "end": v(3583.03, -13161.59) * mm});
            skLineSegment(sketch, "E661", {"start": v(3638.72, -13140.59) * mm, "end": v(4381.01, -13140.59) * mm});
            skLineSegment(sketch, "E662", {"start": v(3638.72, -13087.59) * mm, "end": v(4381.01, -13087.59) * mm});
            skArc(sketch, "E663", {"start": v(4341.44, -12167.58) * mm, "mid": v(4350.45, -12158.05) * mm, "end": v(4341.46, -12148.5) * mm});
            skLineSegment(sketch, "E664", {"start": v(4341.44, -12167.59) * mm, "end": v(4248.44, -12163.59) * mm});
            skLineSegment(sketch, "E665", {"start": v(4248.9, -12152.75) * mm, "end": v(4248.44, -12163.59) * mm});
            skLineSegment(sketch, "E666", {"start": v(4248.9, -12152.75) * mm, "end": v(4341.46, -12148.5) * mm});
            skLineSegment(sketch, "E667", {"start": v(4320.44, -12149.46) * mm, "end": v(4320.44, -12108.59) * mm});
            skLineSegment(sketch, "E668", {"start": v(4320.44, -12108.59) * mm, "end": v(4361.44, -12108.59) * mm});
            skLineSegment(sketch, "E669", {"start": v(4361.44, -12108.59) * mm, "end": v(4361.44, -12258.59) * mm});
            skLineSegment(sketch, "E670", {"start": v(4361.44, -12258.59) * mm, "end": v(4320.44, -12258.59) * mm});
            skLineSegment(sketch, "E671", {"start": v(4320.44, -12258.59) * mm, "end": v(4320.44, -12166.68) * mm});
            skLineSegment(sketch, "E672", {"start": v(4272.44, -12997.59) * mm, "end": v(4067.44, -12997.59) * mm});
            skLineSegment(sketch, "E673", {"start": v(4067.44, -12997.59) * mm, "end": v(4067.44, -12438.59) * mm});
            skLineSegment(sketch, "E674", {"start": v(4067.44, -12438.59) * mm, "end": v(4272.44, -12438.59) * mm});
            skLineSegment(sketch, "E675", {"start": v(4272.44, -12438.59) * mm, "end": v(4272.44, -12997.59) * mm});
            skLineSegment(sketch, "E676", {"start": v(4249.44, -12974.59) * mm, "end": v(4090.44, -12974.59) * mm});
            skLineSegment(sketch, "E677", {"start": v(4090.44, -12974.59) * mm, "end": v(4090.44, -12461.59) * mm});
            skLineSegment(sketch, "E678", {"start": v(4090.44, -12461.59) * mm, "end": v(4249.44, -12461.59) * mm});
            skLineSegment(sketch, "E679", {"start": v(4249.44, -12461.59) * mm, "end": v(4249.44, -12974.59) * mm});
            skLineSegment(sketch, "E680", {"start": v(4282.44, -13007.59) * mm, "end": v(4057.44, -13007.59) * mm});
            skLineSegment(sketch, "E681", {"start": v(4057.44, -13007.59) * mm, "end": v(4057.44, -12428.59) * mm});
            skLineSegment(sketch, "E682", {"start": v(4057.44, -12428.59) * mm, "end": v(4282.44, -12428.59) * mm});
            skLineSegment(sketch, "E683", {"start": v(4282.44, -12428.59) * mm, "end": v(4282.44, -13007.59) * mm});
            skLineSegment(sketch, "E684", {"start": v(3949.44, -12998.59) * mm, "end": v(3744.44, -12998.59) * mm});
            skLineSegment(sketch, "E685", {"start": v(3744.44, -12998.59) * mm, "end": v(3744.44, -12439.59) * mm});
            skLineSegment(sketch, "E686", {"start": v(3744.44, -12439.59) * mm, "end": v(3949.44, -12439.59) * mm});
            skLineSegment(sketch, "E687", {"start": v(3949.44, -12439.59) * mm, "end": v(3949.44, -12998.59) * mm});
            skLineSegment(sketch, "E688", {"start": v(3926.44, -12975.59) * mm, "end": v(3767.44, -12975.59) * mm});
            skLineSegment(sketch, "E689", {"start": v(3767.44, -12975.59) * mm, "end": v(3767.44, -12462.59) * mm});
            skLineSegment(sketch, "E690", {"start": v(3767.44, -12462.59) * mm, "end": v(3926.44, -12462.59) * mm});
            skLineSegment(sketch, "E691", {"start": v(3926.44, -12462.59) * mm, "end": v(3926.44, -12975.59) * mm});
            skLineSegment(sketch, "E692", {"start": v(3959.44, -13008.59) * mm, "end": v(3734.44, -13008.59) * mm});
            skLineSegment(sketch, "E693", {"start": v(3734.44, -13008.59) * mm, "end": v(3734.44, -12429.59) * mm});
            skLineSegment(sketch, "E694", {"start": v(3734.44, -12429.59) * mm, "end": v(3959.44, -12429.59) * mm});
            skLineSegment(sketch, "E695", {"start": v(3959.44, -12429.59) * mm, "end": v(3959.44, -13008.59) * mm});
            skLineSegment(sketch, "E696", {"start": v(4055.44, -12305.59) * mm, "end": v(4280.44, -12305.59) * mm});
            skLineSegment(sketch, "E697", {"start": v(4065.44, -12295.59) * mm, "end": v(4270.44, -12295.59) * mm});
            skLineSegment(sketch, "E698", {"start": v(4088.44, -12272.59) * mm, "end": v(4247.44, -12272.59) * mm});
            skLineSegment(sketch, "E699", {"start": v(4247.44, -12272.59) * mm, "end": v(4247.44, -11699.59) * mm});
            skLineSegment(sketch, "E700", {"start": v(4088.44, -11699.59) * mm, "end": v(4088.44, -12272.59) * mm});
            skLineSegment(sketch, "E701", {"start": v(4247.44, -11699.59) * mm, "end": v(4088.44, -11699.59) * mm});
            skLineSegment(sketch, "E702", {"start": v(4065.44, -11676.59) * mm, "end": v(4065.44, -12295.59) * mm});
            skLineSegment(sketch, "E703", {"start": v(4270.44, -11676.59) * mm, "end": v(4065.44, -11676.59) * mm});
            skLineSegment(sketch, "E704", {"start": v(4280.44, -11666.59) * mm, "end": v(4055.44, -11666.59) * mm});
            skLineSegment(sketch, "E705", {"start": v(4055.44, -11666.59) * mm, "end": v(4055.44, -12305.59) * mm});
            skLineSegment(sketch, "E706", {"start": v(3733.44, -12306.59) * mm, "end": v(3958.44, -12306.59) * mm});
            skLineSegment(sketch, "E707", {"start": v(3743.44, -12296.59) * mm, "end": v(3948.44, -12296.59) * mm});
            skLineSegment(sketch, "E708", {"start": v(3766.44, -12273.59) * mm, "end": v(3925.44, -12273.59) * mm});
            skLineSegment(sketch, "E709", {"start": v(3958.44, -12306.59) * mm, "end": v(3958.44, -11667.59) * mm});
            skLineSegment(sketch, "E710", {"start": v(3948.44, -12296.59) * mm, "end": v(3948.44, -11677.59) * mm});
            skLineSegment(sketch, "E711", {"start": v(3925.44, -12273.59) * mm, "end": v(3925.44, -11700.59) * mm});
            skLineSegment(sketch, "E712", {"start": v(3766.44, -11700.59) * mm, "end": v(3766.44, -12273.59) * mm});
            skLineSegment(sketch, "E713", {"start": v(3925.44, -11700.59) * mm, "end": v(3766.44, -11700.59) * mm});
            skLineSegment(sketch, "E714", {"start": v(3743.44, -11677.59) * mm, "end": v(3743.44, -12296.59) * mm});
            skLineSegment(sketch, "E715", {"start": v(3948.44, -11677.59) * mm, "end": v(3743.44, -11677.59) * mm});
            skLineSegment(sketch, "E716", {"start": v(3958.44, -11667.59) * mm, "end": v(3733.44, -11667.59) * mm});
            skLineSegment(sketch, "E717", {"start": v(3733.44, -11667.59) * mm, "end": v(3733.44, -12306.59) * mm});
            skLineSegment(sketch, "E718", {"start": v(4280.44, -12151.3) * mm, "end": v(4280.44, -11666.59) * mm});
            skLineSegment(sketch, "E719", {"start": v(4280.44, -12305.59) * mm, "end": v(4280.44, -12164.96) * mm});
            skLineSegment(sketch, "E720", {"start": v(4270.44, -12295.59) * mm, "end": v(4270.44, -12164.53) * mm});
            skLineSegment(sketch, "E721", {"start": v(4270.44, -12151.76) * mm, "end": v(4270.44, -11676.59) * mm});
            skLineSegment(sketch, "E722", {"start": v(3733.44, -11569.59) * mm, "end": v(4283.48, -11569.59) * mm});
            skLineSegment(sketch, "E723", {"start": v(4283.48, -11569.59) * mm, "end": v(4282.89, -11555.2) * mm});
            skLineSegment(sketch, "E724", {"start": v(4282.89, -11555.2) * mm, "end": v(4281.55, -11540.86) * mm});
            skLineSegment(sketch, "E725", {"start": v(4281.55, -11540.86) * mm, "end": v(4279.46, -11526.61) * mm});
            skLineSegment(sketch, "E726", {"start": v(4279.46, -11526.61) * mm, "end": v(4276.63, -11512.5) * mm});
            skLineSegment(sketch, "E727", {"start": v(4276.63, -11512.5) * mm, "end": v(4273.06, -11498.54) * mm});
            skLineSegment(sketch, "E728", {"start": v(4273.06, -11498.54) * mm, "end": v(4268.77, -11484.8) * mm});
            skLineSegment(sketch, "E729", {"start": v(4268.77, -11484.8) * mm, "end": v(4263.76, -11471.3) * mm});
            skLineSegment(sketch, "E730", {"start": v(4263.76, -11471.3) * mm, "end": v(4258.05, -11458.08) * mm});
            skLineSegment(sketch, "E731", {"start": v(4258.05, -11458.08) * mm, "end": v(4251.66, -11445.17) * mm});
            skLineSegment(sketch, "E732", {"start": v(4251.66, -11445.17) * mm, "end": v(4244.6, -11432.62) * mm});
            skLineSegment(sketch, "E733", {"start": v(4244.6, -11432.62) * mm, "end": v(4236.9, -11420.45) * mm});
            skLineSegment(sketch, "E734", {"start": v(4236.9, -11420.45) * mm, "end": v(4228.58, -11408.7) * mm});
            skLineSegment(sketch, "E735", {"start": v(4228.58, -11408.7) * mm, "end": v(4219.64, -11397.41) * mm});
            skLineSegment(sketch, "E736", {"start": v(4219.64, -11397.41) * mm, "end": v(4210.13, -11386.6) * mm});
            skLineSegment(sketch, "E737", {"start": v(4210.13, -11386.6) * mm, "end": v(4200.06, -11376.3) * mm});
            skLineSegment(sketch, "E738", {"start": v(4200.06, -11376.3) * mm, "end": v(4189.47, -11366.55) * mm});
            skLineSegment(sketch, "E739", {"start": v(4189.47, -11366.55) * mm, "end": v(4178.39, -11357.36) * mm});
            skLineSegment(sketch, "E740", {"start": v(4178.39, -11357.36) * mm, "end": v(4166.84, -11348.76) * mm});
            skLineSegment(sketch, "E741", {"start": v(4166.84, -11348.76) * mm, "end": v(4154.85, -11340.78) * mm});
            skLineSegment(sketch, "E742", {"start": v(4154.85, -11340.78) * mm, "end": v(4142.46, -11333.44) * mm});
            skLineSegment(sketch, "E743", {"start": v(4142.46, -11333.44) * mm, "end": v(4129.7, -11326.75) * mm});
            skLineSegment(sketch, "E744", {"start": v(4129.7, -11326.75) * mm, "end": v(4116.62, -11320.74) * mm});
            skLineSegment(sketch, "E745", {"start": v(4116.62, -11320.74) * mm, "end": v(4103.24, -11315.43) * mm});
            skLineSegment(sketch, "E746", {"start": v(4103.24, -11315.43) * mm, "end": v(4089.6, -11310.82) * mm});
            skLineSegment(sketch, "E747", {"start": v(4089.6, -11310.82) * mm, "end": v(4075.73, -11306.94) * mm});
            skLineSegment(sketch, "E748", {"start": v(4075.73, -11306.94) * mm, "end": v(4061.68, -11303.78) * mm});
            skLineSegment(sketch, "E749", {"start": v(4061.68, -11303.78) * mm, "end": v(4047.48, -11301.37) * mm});
            skLineSegment(sketch, "E750", {"start": v(4047.48, -11301.37) * mm, "end": v(4033.18, -11299.7) * mm});
            skLineSegment(sketch, "E751", {"start": v(4033.18, -11299.7) * mm, "end": v(4018.81, -11298.78) * mm});
            skLineSegment(sketch, "E752", {"start": v(4018.81, -11298.78) * mm, "end": v(4004.41, -11298.61) * mm});
            skLineSegment(sketch, "E753", {"start": v(4004.41, -11298.61) * mm, "end": v(3990.03, -11299.2) * mm});
            skLineSegment(sketch, "E754", {"start": v(3990.03, -11299.2) * mm, "end": v(3975.69, -11300.54) * mm});
            skLineSegment(sketch, "E755", {"start": v(3975.69, -11300.54) * mm, "end": v(3961.44, -11302.63) * mm});
            skLineSegment(sketch, "E756", {"start": v(3961.44, -11302.63) * mm, "end": v(3947.32, -11305.46) * mm});
            skLineSegment(sketch, "E757", {"start": v(3947.32, -11305.46) * mm, "end": v(3933.37, -11309.03) * mm});
            skLineSegment(sketch, "E758", {"start": v(3933.37, -11309.03) * mm, "end": v(3919.62, -11313.32) * mm});
            skLineSegment(sketch, "E759", {"start": v(3919.62, -11313.32) * mm, "end": v(3906.12, -11318.33) * mm});
            skLineSegment(sketch, "E760", {"start": v(3906.12, -11318.33) * mm, "end": v(3892.9, -11324.04) * mm});
            skLineSegment(sketch, "E761", {"start": v(3892.9, -11324.04) * mm, "end": v(3880, -11330.43) * mm});
            skLineSegment(sketch, "E762", {"start": v(3880, -11330.43) * mm, "end": v(3867.45, -11337.48) * mm});
            skLineSegment(sketch, "E763", {"start": v(3867.45, -11337.48) * mm, "end": v(3855.28, -11345.19) * mm});
            skLineSegment(sketch, "E764", {"start": v(3855.28, -11345.19) * mm, "end": v(3843.53, -11353.52) * mm});
            skLineSegment(sketch, "E765", {"start": v(3843.53, -11353.52) * mm, "end": v(3832.24, -11362.45) * mm});
            skLineSegment(sketch, "E766", {"start": v(3832.24, -11362.45) * mm, "end": v(3821.43, -11371.96) * mm});
            skLineSegment(sketch, "E767", {"start": v(3821.43, -11371.96) * mm, "end": v(3811.13, -11382.03) * mm});
            skLineSegment(sketch, "E768", {"start": v(3811.13, -11382.03) * mm, "end": v(3801.37, -11392.62) * mm});
            skLineSegment(sketch, "E769", {"start": v(3801.37, -11392.62) * mm, "end": v(3792.18, -11403.7) * mm});
            skLineSegment(sketch, "E770", {"start": v(3792.18, -11403.7) * mm, "end": v(3783.59, -11415.25) * mm});
            skLineSegment(sketch, "E771", {"start": v(3783.59, -11415.25) * mm, "end": v(3775.6, -11427.24) * mm});
            skLineSegment(sketch, "E772", {"start": v(3775.6, -11427.24) * mm, "end": v(3768.26, -11439.63) * mm});
            skLineSegment(sketch, "E773", {"start": v(3768.26, -11439.63) * mm, "end": v(3761.58, -11452.38) * mm});
            skLineSegment(sketch, "E774", {"start": v(3761.58, -11452.38) * mm, "end": v(3755.57, -11465.47) * mm});
            skLineSegment(sketch, "E775", {"start": v(3755.57, -11465.47) * mm, "end": v(3750.26, -11478.85) * mm});
            skLineSegment(sketch, "E776", {"start": v(3750.26, -11478.85) * mm, "end": v(3745.65, -11492.5) * mm});
            skLineSegment(sketch, "E777", {"start": v(3745.65, -11492.5) * mm, "end": v(3741.76, -11506.36) * mm});
            skLineSegment(sketch, "E778", {"start": v(3741.76, -11506.36) * mm, "end": v(3738.6, -11520.41) * mm});
            skLineSegment(sketch, "E779", {"start": v(3738.6, -11520.41) * mm, "end": v(3736.2, -11534.6) * mm});
            skLineSegment(sketch, "E780", {"start": v(3736.2, -11534.6) * mm, "end": v(3734.52, -11548.9) * mm});
            skLineSegment(sketch, "E781", {"start": v(3734.52, -11548.9) * mm, "end": v(3733.6, -11563.28) * mm});
            skLineSegment(sketch, "E782", {"start": v(3733.6, -11563.28) * mm, "end": v(3733.44, -11569.59) * mm});
            skLineSegment(sketch, "E783", {"start": v(4186.56, -11376.94) * mm, "end": v(4183.14, -11373.8) * mm});
            skLineSegment(sketch, "E784", {"start": v(4183.14, -11373.8) * mm, "end": v(4172.44, -11364.92) * mm});
            skLineSegment(sketch, "E785", {"start": v(4172.44, -11364.92) * mm, "end": v(4161.3, -11356.63) * mm});
            skLineSegment(sketch, "E786", {"start": v(4161.3, -11356.63) * mm, "end": v(4149.73, -11348.92) * mm});
            skLineSegment(sketch, "E787", {"start": v(4149.73, -11348.92) * mm, "end": v(4137.78, -11341.84) * mm});
            skLineSegment(sketch, "E788", {"start": v(4137.78, -11341.84) * mm, "end": v(4125.47, -11335.39) * mm});
            skLineSegment(sketch, "E789", {"start": v(4125.47, -11335.39) * mm, "end": v(4112.84, -11329.6) * mm});
            skLineSegment(sketch, "E790", {"start": v(4112.84, -11329.6) * mm, "end": v(4099.92, -11324.46) * mm});
            skLineSegment(sketch, "E791", {"start": v(4099.92, -11324.46) * mm, "end": v(4086.76, -11320.02) * mm});
            skLineSegment(sketch, "E792", {"start": v(4086.76, -11320.02) * mm, "end": v(4073.38, -11316.27) * mm});
            skLineSegment(sketch, "E793", {"start": v(4073.38, -11316.27) * mm, "end": v(4059.82, -11313.22) * mm});
            skLineSegment(sketch, "E794", {"start": v(4059.82, -11313.22) * mm, "end": v(4046.12, -11310.9) * mm});
            skLineSegment(sketch, "E795", {"start": v(4046.12, -11310.9) * mm, "end": v(4032.32, -11309.28) * mm});
            skLineSegment(sketch, "E796", {"start": v(4032.32, -11309.28) * mm, "end": v(4022.44, -11308.65) * mm});
            skLineSegment(sketch, "E797", {"start": v(3991.44, -11308.77) * mm, "end": v(3990.67, -11308.8) * mm});
            skLineSegment(sketch, "E798", {"start": v(3990.67, -11308.8) * mm, "end": v(3976.83, -11310.1) * mm});
            skLineSegment(sketch, "E799", {"start": v(3976.83, -11310.1) * mm, "end": v(3963.08, -11312.11) * mm});
            skLineSegment(sketch, "E800", {"start": v(3963.08, -11312.11) * mm, "end": v(3949.46, -11314.85) * mm});
            skLineSegment(sketch, "E801", {"start": v(3949.46, -11314.85) * mm, "end": v(3936, -11318.29) * mm});
            skLineSegment(sketch, "E802", {"start": v(3936, -11318.29) * mm, "end": v(3922.73, -11322.43) * mm});
            skLineSegment(sketch, "E803", {"start": v(3922.73, -11322.43) * mm, "end": v(3909.7, -11327.26) * mm});
            skLineSegment(sketch, "E804", {"start": v(3909.7, -11327.26) * mm, "end": v(3896.94, -11332.77) * mm});
            skLineSegment(sketch, "E805", {"start": v(3896.94, -11332.77) * mm, "end": v(3884.5, -11338.93) * mm});
            skLineSegment(sketch, "E806", {"start": v(3884.5, -11338.93) * mm, "end": v(3872.38, -11345.74) * mm});
            skLineSegment(sketch, "E807", {"start": v(3872.38, -11345.74) * mm, "end": v(3860.64, -11353.18) * mm});
            skLineSegment(sketch, "E808", {"start": v(3860.64, -11353.18) * mm, "end": v(3849.3, -11361.22) * mm});
            skLineSegment(sketch, "E809", {"start": v(3849.3, -11361.22) * mm, "end": v(3838.4, -11369.84) * mm});
            skLineSegment(sketch, "E810", {"start": v(3838.4, -11369.84) * mm, "end": v(3831.64, -11375.8) * mm});
            skArc(sketch, "E811", {"start": v(4039.9, -11527.79) * mm, "mid": v(4031.43, -11523.78) * mm, "end": v(4022.44, -11521.07) * mm});
            skArc(sketch, "E812", {"start": v(3991.44, -11522.03) * mm, "mid": v(3986.09, -11523.84) * mm, "end": v(3980.92, -11526.1) * mm});
            skLineSegment(sketch, "E813", {"start": v(4039.9, -11527.79) * mm, "end": v(4186.56, -11376.94) * mm});
            skLineSegment(sketch, "E814", {"start": v(4060.56, -11546.66) * mm, "end": v(4206.28, -11396.78) * mm});
            skLineSegment(sketch, "E815", {"start": v(4022.44, -11521.07) * mm, "end": v(4022.44, -11308.65) * mm});
            skLineSegment(sketch, "E816", {"start": v(3991.44, -11522.03) * mm, "end": v(3991.44, -11308.77) * mm});
            skLineSegment(sketch, "E817", {"start": v(3980.92, -11526.1) * mm, "end": v(3831.64, -11375.8) * mm});
            skLineSegment(sketch, "E818", {"start": v(3957.26, -11546.44) * mm, "end": v(3809.66, -11397.82) * mm});
            skLineSegment(sketch, "E819", {"start": v(3809.66, -11397.82) * mm, "end": v(3808.62, -11398.95) * mm});
            skLineSegment(sketch, "E820", {"start": v(3808.62, -11398.95) * mm, "end": v(3799.75, -11409.65) * mm});
            skLineSegment(sketch, "E821", {"start": v(3799.75, -11409.65) * mm, "end": v(3791.45, -11420.8) * mm});
            skLineSegment(sketch, "E822", {"start": v(3791.45, -11420.8) * mm, "end": v(3783.75, -11432.36) * mm});
            skLineSegment(sketch, "E823", {"start": v(3783.75, -11432.36) * mm, "end": v(3776.67, -11444.31) * mm});
            skLineSegment(sketch, "E824", {"start": v(3776.67, -11444.31) * mm, "end": v(3770.22, -11456.62) * mm});
            skLineSegment(sketch, "E825", {"start": v(3770.22, -11456.62) * mm, "end": v(3764.42, -11469.25) * mm});
            skLineSegment(sketch, "E826", {"start": v(3764.42, -11469.25) * mm, "end": v(3759.3, -11482.17) * mm});
            skLineSegment(sketch, "E827", {"start": v(3759.3, -11482.17) * mm, "end": v(3754.84, -11495.33) * mm});
            skLineSegment(sketch, "E828", {"start": v(3754.84, -11495.33) * mm, "end": v(3751.1, -11508.71) * mm});
            skLineSegment(sketch, "E829", {"start": v(3751.1, -11508.71) * mm, "end": v(3748.05, -11522.27) * mm});
            skLineSegment(sketch, "E830", {"start": v(3748.05, -11522.27) * mm, "end": v(3745.72, -11535.97) * mm});
            skLineSegment(sketch, "E831", {"start": v(3745.72, -11535.97) * mm, "end": v(3744.1, -11549.77) * mm});
            skLineSegment(sketch, "E832", {"start": v(3744.1, -11549.77) * mm, "end": v(3743.46, -11559.97) * mm});
            skArc(sketch, "E833", {"start": v(3957.26, -11546.43) * mm, "mid": v(3953.25, -11552.98) * mm, "end": v(3950.06, -11559.97) * mm});
            skArc(sketch, "E834", {"start": v(4067.6, -11559.97) * mm, "mid": v(4064.48, -11553.1) * mm, "end": v(4060.56, -11546.66) * mm});
            skLineSegment(sketch, "E835", {"start": v(4067.6, -11559.97) * mm, "end": v(4273.46, -11559.97) * mm});
            skLineSegment(sketch, "E836", {"start": v(4273.46, -11559.97) * mm, "end": v(4273.29, -11555.84) * mm});
            skLineSegment(sketch, "E837", {"start": v(4273.29, -11555.84) * mm, "end": v(4272, -11542) * mm});
            skLineSegment(sketch, "E838", {"start": v(4272, -11542) * mm, "end": v(4269.98, -11528.26) * mm});
            skLineSegment(sketch, "E839", {"start": v(4269.98, -11528.26) * mm, "end": v(4267.24, -11514.63) * mm});
            skLineSegment(sketch, "E840", {"start": v(4267.24, -11514.63) * mm, "end": v(4263.8, -11501.17) * mm});
            skLineSegment(sketch, "E841", {"start": v(4263.8, -11501.17) * mm, "end": v(4259.66, -11487.9) * mm});
            skLineSegment(sketch, "E842", {"start": v(4259.66, -11487.9) * mm, "end": v(4254.83, -11474.88) * mm});
            skLineSegment(sketch, "E843", {"start": v(4254.83, -11474.88) * mm, "end": v(4249.32, -11462.12) * mm});
            skLineSegment(sketch, "E844", {"start": v(4249.32, -11462.12) * mm, "end": v(4243.16, -11449.67) * mm});
            skLineSegment(sketch, "E845", {"start": v(4243.16, -11449.67) * mm, "end": v(4236.35, -11437.55) * mm});
            skLineSegment(sketch, "E846", {"start": v(4236.35, -11437.55) * mm, "end": v(4228.91, -11425.81) * mm});
            skLineSegment(sketch, "E847", {"start": v(4228.91, -11425.81) * mm, "end": v(4220.87, -11414.48) * mm});
            skLineSegment(sketch, "E848", {"start": v(4220.87, -11414.48) * mm, "end": v(4212.25, -11403.58) * mm});
            skLineSegment(sketch, "E849", {"start": v(4212.25, -11403.58) * mm, "end": v(4206.28, -11396.78) * mm});
            skLineSegment(sketch, "E850", {"start": v(3743.46, -11559.97) * mm, "end": v(3950.06, -11559.97) * mm});
            skLineSegment(sketch, "E851", {"start": v(4728.44, -11645.59) * mm, "end": v(4529.44, -11645.59) * mm});
            skLineSegment(sketch, "E852", {"start": v(4529.44, -11645.59) * mm, "end": v(4529.44, -11796.59) * mm});
            skLineSegment(sketch, "E853", {"start": v(4529.44, -11796.59) * mm, "end": v(4728.44, -11796.59) * mm});
            skLineSegment(sketch, "E854", {"start": v(4728.44, -11796.59) * mm, "end": v(4728.44, -11645.59) * mm});
            skLineSegment(sketch, "E855", {"start": v(5020.44, -11210.59) * mm, "end": v(7298.44, -11210.59) * mm});
            skLineSegment(sketch, "E856", {"start": v(7298.44, -11210.59) * mm, "end": v(7298.44, -10985.59) * mm});
            skLineSegment(sketch, "E857", {"start": v(7298.44, -10985.59) * mm, "end": v(5020.44, -10985.59) * mm});
            skLineSegment(sketch, "E858", {"start": v(5020.44, -10985.59) * mm, "end": v(5020.44, -11210.59) * mm});
            skLineSegment(sketch, "E859", {"start": v(3028.23, -11062.59) * mm, "end": v(1481.79, -11062.59) * mm});
            skLineSegment(sketch, "E860", {"start": v(3028.23, -12207.59) * mm, "end": v(1481.79, -12207.59) * mm});
            skLineSegment(sketch, "E861", {"start": v(3084.37, -12233.59) * mm, "end": v(1442.35, -12233.59) * mm});
            skLineSegment(sketch, "E862", {"start": v(3084.44, -12218.59) * mm, "end": v(3084.21, -12267.59) * mm});
            skLineSegment(sketch, "E863", {"start": v(3084.21, -12267.59) * mm, "end": v(1442.2, -12267.59) * mm});
            skLineSegment(sketch, "E864", {"start": v(1442.42, -12218.59) * mm, "end": v(1442.2, -12267.59) * mm});
            skLineSegment(sketch, "E865", {"start": v(3084.44, -12218.59) * mm, "end": v(1442.42, -12218.59) * mm});
            skLineSegment(sketch, "E866", {"start": v(3028.23, -10838.59) * mm, "end": v(3028.23, -12218.59) * mm});
            skLineSegment(sketch, "E867", {"start": v(1481.79, -10838.59) * mm, "end": v(1481.79, -12218.59) * mm});
            skLineSegment(sketch, "E868", {"start": v(3028.23, -10838.59) * mm, "end": v(1481.79, -10838.59) * mm});
            skLineSegment(sketch, "E869", {"start": v(1586.44, -11172.59) * mm, "end": v(1586.44, -12094.59) * mm});
            skLineSegment(sketch, "E870", {"start": v(1575.44, -11161.59) * mm, "end": v(1575.44, -12105.59) * mm});
            skLineSegment(sketch, "E871", {"start": v(1522.44, -11108.59) * mm, "end": v(1522.44, -12158.59) * mm});
            skLineSegment(sketch, "E872", {"start": v(1511.44, -11099.59) * mm, "end": v(1511.44, -12167.59) * mm});
            skLineSegment(sketch, "E873", {"start": v(1963.44, -11161.59) * mm, "end": v(1575.44, -11161.59) * mm});
            skLineSegment(sketch, "E874", {"start": v(1952.44, -11172.59) * mm, "end": v(1586.44, -11172.59) * mm});
            skLineSegment(sketch, "E875", {"start": v(1586.44, -12094.59) * mm, "end": v(1952.44, -12094.59) * mm});
            skLineSegment(sketch, "E876", {"start": v(1952.44, -12094.59) * mm, "end": v(1952.44, -11172.59) * mm});
            skLineSegment(sketch, "E877", {"start": v(1963.44, -12105.59) * mm, "end": v(1963.44, -11161.59) * mm});
            skLineSegment(sketch, "E878", {"start": v(1575.44, -12105.59) * mm, "end": v(1963.44, -12105.59) * mm});
            skLineSegment(sketch, "E879", {"start": v(1522.44, -12158.59) * mm, "end": v(2016.44, -12158.59) * mm});
            skLineSegment(sketch, "E880", {"start": v(1511.44, -12167.59) * mm, "end": v(2025.44, -12167.59) * mm});
            skLineSegment(sketch, "E881", {"start": v(2016.44, -12158.59) * mm, "end": v(2016.44, -11108.59) * mm});
            skLineSegment(sketch, "E882", {"start": v(2016.44, -11108.59) * mm, "end": v(1522.44, -11108.59) * mm});
            skLineSegment(sketch, "E883", {"start": v(2025.44, -12167.59) * mm, "end": v(2025.44, -11099.59) * mm});
            skLineSegment(sketch, "E884", {"start": v(2025.44, -11099.59) * mm, "end": v(1511.44, -11099.59) * mm});
            skLineSegment(sketch, "E885", {"start": v(-15606.23, 9038.41) * mm, "end": v(-16117.23, 9038.41) * mm});
            skLineSegment(sketch, "E886", {"start": v(-15595.43, 9049.41) * mm, "end": v(-16128.23, 9049.41) * mm});
            skLineSegment(sketch, "E887", {"start": v(-15606.23, 8842.41) * mm, "end": v(-15606.23, 9038.41) * mm});
            skLineSegment(sketch, "E888", {"start": v(-15595.43, 8831.41) * mm, "end": v(-15595.43, 9049.41) * mm});
            skLineSegment(sketch, "E889", {"start": v(-16117.23, 8842.41) * mm, "end": v(-15606.23, 8842.41) * mm});
            skLineSegment(sketch, "E890", {"start": v(-16117.23, 9038.41) * mm, "end": v(-16117.23, 8842.41) * mm});
            skLineSegment(sketch, "E891", {"start": v(-16128.23, 8831.41) * mm, "end": v(-15595.43, 8831.41) * mm});
            skLineSegment(sketch, "E892", {"start": v(-16128.23, 9049.41) * mm, "end": v(-16128.23, 8831.41) * mm});
            skLineSegment(sketch, "E893", {"start": v(-16171.43, 8788.41) * mm, "end": v(-15552.23, 8788.41) * mm});
            skLineSegment(sketch, "E894", {"start": v(-16182.43, 8777.41) * mm, "end": v(-15541.23, 8777.41) * mm});
            skLineSegment(sketch, "E895", {"start": v(-16171.43, 8788.41) * mm, "end": v(-16171.43, 9092.41) * mm});
            skLineSegment(sketch, "E896", {"start": v(-16182.43, 8777.41) * mm, "end": v(-16182.43, 9103.41) * mm});
            skLineSegment(sketch, "E897", {"start": v(-15552.23, 8788.41) * mm, "end": v(-15552.23, 9092.41) * mm});
            skLineSegment(sketch, "E898", {"start": v(-15552.23, 9092.41) * mm, "end": v(-16171.43, 9092.41) * mm});
            skLineSegment(sketch, "E899", {"start": v(-15541.23, 9103.41) * mm, "end": v(-16182.43, 9103.41) * mm});
            skLineSegment(sketch, "E900", {"start": v(-15541.23, 8777.41) * mm, "end": v(-15541.23, 9103.41) * mm});
            skLineSegment(sketch, "E901", {"start": v(-16176.23, 7904.41) * mm, "end": v(-15541.23, 7904.41) * mm});
            skLineSegment(sketch, "E902", {"start": v(-15541.23, 7904.41) * mm, "end": v(-15541.23, 8747.41) * mm});
            skLineSegment(sketch, "E903", {"start": v(-15541.23, 8747.41) * mm, "end": v(-16176.23, 8747.41) * mm});
            skLineSegment(sketch, "E904", {"start": v(-16176.23, 8747.41) * mm, "end": v(-16176.23, 7904.41) * mm});
            skLineSegment(sketch, "E905", {"start": v(-16157.23, 7923.41) * mm, "end": v(-15560.23, 7923.41) * mm});
            skLineSegment(sketch, "E906", {"start": v(-15560.23, 7923.41) * mm, "end": v(-15560.23, 8728.41) * mm});
            skLineSegment(sketch, "E907", {"start": v(-15560.23, 8728.41) * mm, "end": v(-16157.23, 8728.41) * mm});
            skLineSegment(sketch, "E908", {"start": v(-16157.23, 8728.41) * mm, "end": v(-16157.23, 7923.41) * mm});
            skLineSegment(sketch, "E909", {"start": v(2559.44, -11173.59) * mm, "end": v(2559.44, -12095.59) * mm});
            skLineSegment(sketch, "E910", {"start": v(2548.44, -11162.58) * mm, "end": v(2548.44, -12106.59) * mm});
            skLineSegment(sketch, "E911", {"start": v(2495.44, -11109.59) * mm, "end": v(2495.44, -12159.58) * mm});
            skLineSegment(sketch, "E912", {"start": v(2484.44, -11100.59) * mm, "end": v(2484.44, -12168.59) * mm});
            skLineSegment(sketch, "E913", {"start": v(2936.44, -11162.58) * mm, "end": v(2548.44, -11162.58) * mm});
            skLineSegment(sketch, "E914", {"start": v(2925.44, -11173.59) * mm, "end": v(2559.44, -11173.59) * mm});
            skLineSegment(sketch, "E915", {"start": v(2559.44, -12095.59) * mm, "end": v(2925.44, -12095.59) * mm});
            skLineSegment(sketch, "E916", {"start": v(2925.44, -12095.59) * mm, "end": v(2925.44, -11173.59) * mm});
            skLineSegment(sketch, "E917", {"start": v(2936.44, -12106.59) * mm, "end": v(2936.44, -11162.58) * mm});
            skLineSegment(sketch, "E918", {"start": v(2548.44, -12106.59) * mm, "end": v(2936.44, -12106.59) * mm});
            skLineSegment(sketch, "E919", {"start": v(2495.44, -12159.58) * mm, "end": v(2989.44, -12159.58) * mm});
            skLineSegment(sketch, "E920", {"start": v(2484.44, -12168.59) * mm, "end": v(2998.44, -12168.59) * mm});
            skLineSegment(sketch, "E921", {"start": v(2989.44, -12159.58) * mm, "end": v(2989.44, -11109.59) * mm});
            skLineSegment(sketch, "E922", {"start": v(2989.44, -11109.59) * mm, "end": v(2495.44, -11109.59) * mm});
            skLineSegment(sketch, "E923", {"start": v(2998.44, -12168.59) * mm, "end": v(2998.44, -11100.59) * mm});
            skLineSegment(sketch, "E924", {"start": v(2998.44, -11100.59) * mm, "end": v(2484.44, -11100.59) * mm});
            skLineSegment(sketch, "E925", {"start": v(2056.24, -11108.59) * mm, "end": v(2453.64, -11108.59) * mm});
            skLineSegment(sketch, "E926", {"start": v(2453.64, -11108.59) * mm, "end": v(2453.64, -11311.59) * mm});
            skLineSegment(sketch, "E927", {"start": v(2453.64, -11311.59) * mm, "end": v(2056.24, -11311.59) * mm});
            skLineSegment(sketch, "E928", {"start": v(2056.24, -11311.59) * mm, "end": v(2056.24, -11108.59) * mm});
            skLineSegment(sketch, "E929", {"start": v(2047.24, -11099.59) * mm, "end": v(2462.64, -11099.59) * mm});
            skLineSegment(sketch, "E930", {"start": v(2462.64, -11099.59) * mm, "end": v(2462.64, -11320.59) * mm});
            skLineSegment(sketch, "E931", {"start": v(2462.64, -11320.59) * mm, "end": v(2047.24, -11320.59) * mm});
            skLineSegment(sketch, "E932", {"start": v(2047.24, -11320.59) * mm, "end": v(2047.24, -11099.59) * mm});
            skLineSegment(sketch, "E933", {"start": v(2441.44, -11350.59) * mm, "end": v(2068.44, -11350.59) * mm});
            skLineSegment(sketch, "E934", {"start": v(2068.44, -11350.59) * mm, "end": v(2068.44, -12159.58) * mm});
            skLineSegment(sketch, "E935", {"start": v(2068.44, -12159.58) * mm, "end": v(2441.44, -12159.58) * mm});
            skLineSegment(sketch, "E936", {"start": v(2441.44, -12159.58) * mm, "end": v(2441.44, -11350.59) * mm});
            skLineSegment(sketch, "E937", {"start": v(2430.44, -11361.59) * mm, "end": v(2079.44, -11361.59) * mm});
            skLineSegment(sketch, "E938", {"start": v(2079.44, -11361.59) * mm, "end": v(2079.44, -12148.59) * mm});
            skLineSegment(sketch, "E939", {"start": v(2079.44, -12148.59) * mm, "end": v(2430.44, -12148.59) * mm});
            skLineSegment(sketch, "E940", {"start": v(2430.44, -12148.59) * mm, "end": v(2430.44, -11361.59) * mm});
            skLineSegment(sketch, "E941", {"start": v(1952.44, -11126.59) * mm, "end": v(1549.44, -11126.59) * mm});
            skLineSegment(sketch, "E942", {"start": v(1549.44, -11126.59) * mm, "end": v(1549.44, -11144.59) * mm});
            skLineSegment(sketch, "E943", {"start": v(1549.44, -11144.59) * mm, "end": v(1952.44, -11144.59) * mm});
            skLineSegment(sketch, "E944", {"start": v(1952.44, -11144.59) * mm, "end": v(1952.44, -11126.59) * mm});
            skLineSegment(sketch, "E945", {"start": v(2955.44, -11126.59) * mm, "end": v(2552.44, -11126.59) * mm});
            skLineSegment(sketch, "E946", {"start": v(2552.44, -11126.59) * mm, "end": v(2552.44, -11144.59) * mm});
            skLineSegment(sketch, "E947", {"start": v(2552.44, -11144.59) * mm, "end": v(2955.44, -11144.59) * mm});
            skLineSegment(sketch, "E948", {"start": v(2955.44, -11144.59) * mm, "end": v(2955.44, -11126.59) * mm});
            skLineSegment(sketch, "E949", {"start": v(2122.24, -11144.59) * mm, "end": v(2387.64, -11144.59) * mm});
            skLineSegment(sketch, "E950", {"start": v(2111.24, -11133.59) * mm, "end": v(2398.64, -11133.59) * mm});
            skLineSegment(sketch, "E951", {"start": v(2387.64, -11144.59) * mm, "end": v(2387.64, -11275.59) * mm});
            skLineSegment(sketch, "E952", {"start": v(2398.64, -11133.59) * mm, "end": v(2398.64, -11286.59) * mm});
            skLineSegment(sketch, "E953", {"start": v(2387.64, -11275.59) * mm, "end": v(2122.24, -11275.59) * mm});
            skLineSegment(sketch, "E954", {"start": v(2122.24, -11144.59) * mm, "end": v(2122.24, -11275.59) * mm});
            skLineSegment(sketch, "E955", {"start": v(2111.24, -11133.59) * mm, "end": v(2111.24, -11286.59) * mm});
            skLineSegment(sketch, "E956", {"start": v(2398.64, -11286.59) * mm, "end": v(2111.24, -11286.59) * mm});
            skLineSegment(sketch, "E957", {"start": v(1467.44, -10443.59) * mm, "end": v(1621.44, -10443.59) * mm});
            skLineSegment(sketch, "E958", {"start": v(1621.44, -10443.59) * mm, "end": v(1621.44, -10289.59) * mm});
            skLineSegment(sketch, "E959", {"start": v(1621.44, -10289.59) * mm, "end": v(1467.44, -10289.59) * mm});
            skLineSegment(sketch, "E960", {"start": v(1467.44, -10289.59) * mm, "end": v(1467.44, -10443.59) * mm});
            skLineSegment(sketch, "E961", {"start": v(3100.44, -10205.59) * mm, "end": v(3119.44, -10205.59) * mm});
            skLineSegment(sketch, "E962", {"start": v(3119.44, -10205.59) * mm, "end": v(3119.44, -10100.59) * mm});
            skLineSegment(sketch, "E963", {"start": v(3119.44, -10100.59) * mm, "end": v(3100.44, -10100.59) * mm});
            skLineSegment(sketch, "E964", {"start": v(3100.44, -10100.59) * mm, "end": v(3100.44, -10205.59) * mm});
            skCircle(sketch, "E965", {"center": v(3266.25, -9145.26) * mm, "radius": 82.28 * mm});
            skCircle(sketch, "E966", {"center": v(3266.25, -9145.26) * mm, "radius": 38.52 * mm});
            skCircle(sketch, "E967", {"center": v(3266.25, -9145.26) * mm, "radius": 12.59 * mm});
            skLineSegment(sketch, "E968", {"start": v(3333.44, -8624.59) * mm, "end": v(3313.44, -8601.58) * mm});
            skLineSegment(sketch, "E969", {"start": v(3313.44, -8601.58) * mm, "end": v(3219.44, -8529.59) * mm});
            skLineSegment(sketch, "E970", {"start": v(3185.82, -8626.6) * mm, "end": v(6261.44, -10088.59) * mm});
            skLineSegment(sketch, "E971", {"start": v(6261.44, -10088.59) * mm, "end": v(7813.44, -10863.59) * mm});
            skLineSegment(sketch, "E972", {"start": v(7813.44, -10863.59) * mm, "end": v(7846.44, -10876.59) * mm});
            skLineSegment(sketch, "E973", {"start": v(7846.44, -10876.59) * mm, "end": v(8144.44, -10937.59) * mm});
            skLineSegment(sketch, "E974", {"start": v(8144.44, -10937.59) * mm, "end": v(8191.44, -10963.59) * mm});
            skLineSegment(sketch, "E975", {"start": v(8191.44, -10963.59) * mm, "end": v(8200.44, -10937.59) * mm});
            skLineSegment(sketch, "E976", {"start": v(8200.44, -10937.59) * mm, "end": v(6094.44, -9880.59) * mm});
            skLineSegment(sketch, "E977", {"start": v(6094.44, -9880.59) * mm, "end": v(3621.44, -8731.59) * mm});
            skLineSegment(sketch, "E978", {"start": v(3621.44, -8731.59) * mm, "end": v(3333.44, -8624.59) * mm});
            skLineSegment(sketch, "E979", {"start": v(-1197.56, -10753.59) * mm, "end": v(-157.56, -10245.59) * mm});
            skLineSegment(sketch, "E980", {"start": v(-157.56, -10245.59) * mm, "end": v(2080.44, -9159.58) * mm});
            skLineSegment(sketch, "E981", {"start": v(2080.44, -9159.58) * mm, "end": v(3185.82, -8626.6) * mm});
            skLineSegment(sketch, "E982", {"start": v(3178.37, -8834.59) * mm, "end": v(3209.94, -8834.59) * mm});
            skLineSegment(sketch, "E983", {"start": v(3245.48, -8654.95) * mm, "end": v(3209.94, -8834.59) * mm});
            skLineSegment(sketch, "E984", {"start": v(3209.44, -8751.59) * mm, "end": v(3186.44, -8751.59) * mm});
            skLineSegment(sketch, "E985", {"start": v(3186.44, -8751.59) * mm, "end": v(3186.44, -8657.59) * mm});
            skLineSegment(sketch, "E986", {"start": v(3186.44, -8657.59) * mm, "end": v(3209.44, -8657.59) * mm});
            skLineSegment(sketch, "E987", {"start": v(3209.44, -8657.59) * mm, "end": v(3209.44, -8751.59) * mm});
            skLineSegment(sketch, "E988", {"start": v(3127.04, -8654.94) * mm, "end": v(3178.37, -8834.59) * mm});
            skLineSegment(sketch, "E989", {"start": v(3168.47, -8799.93) * mm, "end": v(-1275.56, -10956.59) * mm});
            skLineSegment(sketch, "E990", {"start": v(-1275.56, -10956.59) * mm, "end": v(-1301.7, -10960.8) * mm});
            skLineSegment(sketch, "E991", {"start": v(4320.44, -9221.59) * mm, "end": v(4312.44, -9166.59) * mm});
            skLineSegment(sketch, "E992", {"start": v(4390.44, -9259.59) * mm, "end": v(4391.36, -9199.65) * mm});
            skLineSegment(sketch, "E993", {"start": v(4380.36, -9194.41) * mm, "end": v(4326.44, -9193.59) * mm});
            skLineSegment(sketch, "E994", {"start": v(6268.44, -12805.59) * mm, "end": v(6471.46, -12805.59) * mm});
            skLineSegment(sketch, "E995", {"start": v(6471.46, -12805.59) * mm, "end": v(6471.52, -12800.27) * mm});
            skLineSegment(sketch, "E996", {"start": v(6471.52, -12800.27) * mm, "end": v(6471.3, -12794.95) * mm});
            skLineSegment(sketch, "E997", {"start": v(6471.3, -12794.95) * mm, "end": v(6470.8, -12789.66) * mm});
            skLineSegment(sketch, "E998", {"start": v(6470.8, -12789.66) * mm, "end": v(6470.01, -12784.4) * mm});
            skLineSegment(sketch, "E999", {"start": v(6470.01, -12784.4) * mm, "end": v(6468.96, -12779.19) * mm});
            skLineSegment(sketch, "E1000", {"start": v(6468.96, -12779.19) * mm, "end": v(6467.64, -12774.04) * mm});
            skLineSegment(sketch, "E1001", {"start": v(6467.64, -12774.04) * mm, "end": v(6466.05, -12768.96) * mm});
            skLineSegment(sketch, "E1002", {"start": v(6466.05, -12768.96) * mm, "end": v(6464.2, -12763.98) * mm});
            skLineSegment(sketch, "E1003", {"start": v(6464.2, -12763.98) * mm, "end": v(6462.08, -12759.1) * mm});
            skLineSegment(sketch, "E1004", {"start": v(6462.08, -12759.1) * mm, "end": v(6459.71, -12754.33) * mm});
            skLineSegment(sketch, "E1005", {"start": v(6459.71, -12754.33) * mm, "end": v(6457.1, -12749.7) * mm});
            skLineSegment(sketch, "E1006", {"start": v(6457.1, -12749.7) * mm, "end": v(6454.25, -12745.21) * mm});
            skLineSegment(sketch, "E1007", {"start": v(6454.25, -12745.21) * mm, "end": v(6451.17, -12740.88) * mm});
            skLineSegment(sketch, "E1008", {"start": v(6451.17, -12740.88) * mm, "end": v(6447.86, -12736.71) * mm});
            skLineSegment(sketch, "E1009", {"start": v(6447.86, -12736.71) * mm, "end": v(6444.35, -12732.72) * mm});
            skLineSegment(sketch, "E1010", {"start": v(6444.35, -12732.72) * mm, "end": v(6440.63, -12728.92) * mm});
            skLineSegment(sketch, "E1011", {"start": v(6440.63, -12728.92) * mm, "end": v(6436.7, -12725.32) * mm});
            skLineSegment(sketch, "E1012", {"start": v(6436.7, -12725.32) * mm, "end": v(6432.61, -12721.94) * mm});
            skLineSegment(sketch, "E1013", {"start": v(6432.61, -12721.94) * mm, "end": v(6428.34, -12718.77) * mm});
            skLineSegment(sketch, "E1014", {"start": v(6428.34, -12718.77) * mm, "end": v(6423.91, -12715.82) * mm});
            skLineSegment(sketch, "E1015", {"start": v(6423.91, -12715.82) * mm, "end": v(6419.33, -12713.12) * mm});
            skLineSegment(sketch, "E1016", {"start": v(6419.33, -12713.12) * mm, "end": v(6414.62, -12710.66) * mm});
            skLineSegment(sketch, "E1017", {"start": v(6414.62, -12710.66) * mm, "end": v(6409.78, -12708.44) * mm});
            skLineSegment(sketch, "E1018", {"start": v(6409.78, -12708.44) * mm, "end": v(6404.84, -12706.49) * mm});
            skLineSegment(sketch, "E1019", {"start": v(6404.84, -12706.49) * mm, "end": v(6399.8, -12704.8) * mm});
            skLineSegment(sketch, "E1020", {"start": v(6399.8, -12704.8) * mm, "end": v(6394.68, -12703.36) * mm});
            skLineSegment(sketch, "E1021", {"start": v(6394.68, -12703.36) * mm, "end": v(6389.49, -12702.2) * mm});
            skLineSegment(sketch, "E1022", {"start": v(6389.49, -12702.2) * mm, "end": v(6384.24, -12701.32) * mm});
            skLineSegment(sketch, "E1023", {"start": v(6384.24, -12701.32) * mm, "end": v(6378.96, -12700.7) * mm});
            skLineSegment(sketch, "E1024", {"start": v(6378.96, -12700.7) * mm, "end": v(6373.65, -12700.37) * mm});
            skLineSegment(sketch, "E1025", {"start": v(6373.65, -12700.37) * mm, "end": v(6368.33, -12700.32) * mm});
            skLineSegment(sketch, "E1026", {"start": v(6368.33, -12700.32) * mm, "end": v(6363.02, -12700.54) * mm});
            skLineSegment(sketch, "E1027", {"start": v(6363.02, -12700.54) * mm, "end": v(6357.73, -12701.05) * mm});
            skLineSegment(sketch, "E1028", {"start": v(6357.73, -12701.05) * mm, "end": v(6352.47, -12701.82) * mm});
            skLineSegment(sketch, "E1029", {"start": v(6352.47, -12701.82) * mm, "end": v(6347.25, -12702.88) * mm});
            skLineSegment(sketch, "E1030", {"start": v(6347.25, -12702.88) * mm, "end": v(6342.1, -12704.2) * mm});
            skLineSegment(sketch, "E1031", {"start": v(6342.1, -12704.2) * mm, "end": v(6337.03, -12705.8) * mm});
            skLineSegment(sketch, "E1032", {"start": v(6337.03, -12705.8) * mm, "end": v(6332.04, -12707.65) * mm});
            skLineSegment(sketch, "E1033", {"start": v(6332.04, -12707.65) * mm, "end": v(6327.16, -12709.76) * mm});
            skLineSegment(sketch, "E1034", {"start": v(6327.16, -12709.76) * mm, "end": v(6322.4, -12712.12) * mm});
            skLineSegment(sketch, "E1035", {"start": v(6322.4, -12712.12) * mm, "end": v(6317.77, -12714.74) * mm});
            skLineSegment(sketch, "E1036", {"start": v(6317.77, -12714.74) * mm, "end": v(6313.28, -12717.59) * mm});
            skLineSegment(sketch, "E1037", {"start": v(6313.28, -12717.59) * mm, "end": v(6308.94, -12720.67) * mm});
            skLineSegment(sketch, "E1038", {"start": v(6308.94, -12720.67) * mm, "end": v(6304.78, -12723.97) * mm});
            skLineSegment(sketch, "E1039", {"start": v(6304.78, -12723.97) * mm, "end": v(6300.79, -12727.5) * mm});
            skLineSegment(sketch, "E1040", {"start": v(6300.79, -12727.5) * mm, "end": v(6296.99, -12731.21) * mm});
            skLineSegment(sketch, "E1041", {"start": v(6296.99, -12731.21) * mm, "end": v(6293.4, -12735.13) * mm});
            skLineSegment(sketch, "E1042", {"start": v(6293.4, -12735.13) * mm, "end": v(6290, -12739.23) * mm});
            skLineSegment(sketch, "E1043", {"start": v(6290, -12739.23) * mm, "end": v(6286.83, -12743.5) * mm});
            skLineSegment(sketch, "E1044", {"start": v(6286.83, -12743.5) * mm, "end": v(6283.89, -12747.93) * mm});
            skLineSegment(sketch, "E1045", {"start": v(6283.89, -12747.93) * mm, "end": v(6281.18, -12752.5) * mm});
            skLineSegment(sketch, "E1046", {"start": v(6281.18, -12752.5) * mm, "end": v(6278.72, -12757.22) * mm});
            skLineSegment(sketch, "E1047", {"start": v(6278.72, -12757.22) * mm, "end": v(6276.5, -12762.05) * mm});
            skLineSegment(sketch, "E1048", {"start": v(6276.5, -12762.05) * mm, "end": v(6274.55, -12767) * mm});
            skLineSegment(sketch, "E1049", {"start": v(6274.55, -12767) * mm, "end": v(6272.86, -12772.04) * mm});
            skLineSegment(sketch, "E1050", {"start": v(6272.86, -12772.04) * mm, "end": v(6271.43, -12777.16) * mm});
            skLineSegment(sketch, "E1051", {"start": v(6271.43, -12777.16) * mm, "end": v(6270.27, -12782.35) * mm});
            skLineSegment(sketch, "E1052", {"start": v(6270.27, -12782.35) * mm, "end": v(6269.38, -12787.6) * mm});
            skLineSegment(sketch, "E1053", {"start": v(6269.38, -12787.6) * mm, "end": v(6268.77, -12792.88) * mm});
            skLineSegment(sketch, "E1054", {"start": v(6268.77, -12792.88) * mm, "end": v(6268.44, -12798.19) * mm});
            skLineSegment(sketch, "E1055", {"start": v(6268.44, -12798.19) * mm, "end": v(6268.39, -12803.5) * mm});
            skLineSegment(sketch, "E1056", {"start": v(6268.39, -12803.5) * mm, "end": v(6268.44, -12805.59) * mm});
            skLineSegment(sketch, "E1057", {"start": v(2135.42, -12802.59) * mm, "end": v(2338.44, -12802.59) * mm});
            skLineSegment(sketch, "E1058", {"start": v(2338.44, -12802.59) * mm, "end": v(2338.5, -12797.27) * mm});
            skLineSegment(sketch, "E1059", {"start": v(2338.5, -12797.27) * mm, "end": v(2338.27, -12791.95) * mm});
            skLineSegment(sketch, "E1060", {"start": v(2338.27, -12791.95) * mm, "end": v(2337.77, -12786.66) * mm});
            skLineSegment(sketch, "E1061", {"start": v(2337.77, -12786.66) * mm, "end": v(2337, -12781.4) * mm});
            skLineSegment(sketch, "E1062", {"start": v(2337, -12781.4) * mm, "end": v(2335.94, -12776.19) * mm});
            skLineSegment(sketch, "E1063", {"start": v(2335.94, -12776.19) * mm, "end": v(2334.61, -12771.04) * mm});
            skLineSegment(sketch, "E1064", {"start": v(2334.61, -12771.04) * mm, "end": v(2333.02, -12765.96) * mm});
            skLineSegment(sketch, "E1065", {"start": v(2333.02, -12765.96) * mm, "end": v(2331.17, -12760.98) * mm});
            skLineSegment(sketch, "E1066", {"start": v(2331.17, -12760.98) * mm, "end": v(2329.06, -12756.1) * mm});
            skLineSegment(sketch, "E1067", {"start": v(2329.06, -12756.1) * mm, "end": v(2326.7, -12751.33) * mm});
            skLineSegment(sketch, "E1068", {"start": v(2326.7, -12751.33) * mm, "end": v(2324.08, -12746.7) * mm});
            skLineSegment(sketch, "E1069", {"start": v(2324.08, -12746.7) * mm, "end": v(2321.23, -12742.21) * mm});
            skLineSegment(sketch, "E1070", {"start": v(2321.23, -12742.21) * mm, "end": v(2318.15, -12737.88) * mm});
            skLineSegment(sketch, "E1071", {"start": v(2318.15, -12737.88) * mm, "end": v(2314.84, -12733.71) * mm});
            skLineSegment(sketch, "E1072", {"start": v(2314.84, -12733.71) * mm, "end": v(2311.32, -12729.72) * mm});
            skLineSegment(sketch, "E1073", {"start": v(2311.32, -12729.72) * mm, "end": v(2307.6, -12725.92) * mm});
            skLineSegment(sketch, "E1074", {"start": v(2307.6, -12725.92) * mm, "end": v(2303.69, -12722.32) * mm});
            skLineSegment(sketch, "E1075", {"start": v(2303.69, -12722.32) * mm, "end": v(2299.59, -12718.94) * mm});
            skLineSegment(sketch, "E1076", {"start": v(2299.59, -12718.94) * mm, "end": v(2295.32, -12715.77) * mm});
            skLineSegment(sketch, "E1077", {"start": v(2295.32, -12715.77) * mm, "end": v(2290.89, -12712.82) * mm});
            skLineSegment(sketch, "E1078", {"start": v(2290.89, -12712.82) * mm, "end": v(2286.3, -12710.12) * mm});
            skLineSegment(sketch, "E1079", {"start": v(2286.3, -12710.12) * mm, "end": v(2281.6, -12707.66) * mm});
            skLineSegment(sketch, "E1080", {"start": v(2281.6, -12707.66) * mm, "end": v(2276.76, -12705.44) * mm});
            skLineSegment(sketch, "E1081", {"start": v(2276.76, -12705.44) * mm, "end": v(2271.81, -12703.49) * mm});
            skLineSegment(sketch, "E1082", {"start": v(2271.81, -12703.49) * mm, "end": v(2266.77, -12701.8) * mm});
            skLineSegment(sketch, "E1083", {"start": v(2266.77, -12701.8) * mm, "end": v(2261.65, -12700.36) * mm});
            skLineSegment(sketch, "E1084", {"start": v(2261.65, -12700.36) * mm, "end": v(2256.46, -12699.2) * mm});
            skLineSegment(sketch, "E1085", {"start": v(2256.46, -12699.2) * mm, "end": v(2251.22, -12698.32) * mm});
            skLineSegment(sketch, "E1086", {"start": v(2251.22, -12698.32) * mm, "end": v(2245.94, -12697.7) * mm});
            skLineSegment(sketch, "E1087", {"start": v(2245.94, -12697.7) * mm, "end": v(2240.63, -12697.37) * mm});
            skLineSegment(sketch, "E1088", {"start": v(2240.63, -12697.37) * mm, "end": v(2235.3, -12697.32) * mm});
            skLineSegment(sketch, "E1089", {"start": v(2235.3, -12697.32) * mm, "end": v(2230, -12697.54) * mm});
            skLineSegment(sketch, "E1090", {"start": v(2230, -12697.54) * mm, "end": v(2224.7, -12698.05) * mm});
            skLineSegment(sketch, "E1091", {"start": v(2224.7, -12698.05) * mm, "end": v(2219.44, -12698.82) * mm});
            skLineSegment(sketch, "E1092", {"start": v(2219.44, -12698.82) * mm, "end": v(2214.23, -12699.88) * mm});
            skLineSegment(sketch, "E1093", {"start": v(2214.23, -12699.88) * mm, "end": v(2209.08, -12701.2) * mm});
            skLineSegment(sketch, "E1094", {"start": v(2209.08, -12701.2) * mm, "end": v(2204, -12702.8) * mm});
            skLineSegment(sketch, "E1095", {"start": v(2204, -12702.8) * mm, "end": v(2199.02, -12704.65) * mm});
            skLineSegment(sketch, "E1096", {"start": v(2199.02, -12704.65) * mm, "end": v(2194.14, -12706.76) * mm});
            skLineSegment(sketch, "E1097", {"start": v(2194.14, -12706.76) * mm, "end": v(2189.38, -12709.12) * mm});
            skLineSegment(sketch, "E1098", {"start": v(2189.38, -12709.12) * mm, "end": v(2184.74, -12711.74) * mm});
            skLineSegment(sketch, "E1099", {"start": v(2184.74, -12711.74) * mm, "end": v(2180.25, -12714.59) * mm});
            skLineSegment(sketch, "E1100", {"start": v(2180.25, -12714.59) * mm, "end": v(2175.92, -12717.67) * mm});
            skLineSegment(sketch, "E1101", {"start": v(2175.92, -12717.67) * mm, "end": v(2171.75, -12720.97) * mm});
            skLineSegment(sketch, "E1102", {"start": v(2171.75, -12720.97) * mm, "end": v(2167.76, -12724.5) * mm});
            skLineSegment(sketch, "E1103", {"start": v(2167.76, -12724.5) * mm, "end": v(2163.97, -12728.21) * mm});
            skLineSegment(sketch, "E1104", {"start": v(2163.97, -12728.21) * mm, "end": v(2160.37, -12732.13) * mm});
            skLineSegment(sketch, "E1105", {"start": v(2160.37, -12732.13) * mm, "end": v(2156.98, -12736.23) * mm});
            skLineSegment(sketch, "E1106", {"start": v(2156.98, -12736.23) * mm, "end": v(2153.8, -12740.5) * mm});
            skLineSegment(sketch, "E1107", {"start": v(2153.8, -12740.5) * mm, "end": v(2150.87, -12744.93) * mm});
            skLineSegment(sketch, "E1108", {"start": v(2150.87, -12744.93) * mm, "end": v(2148.16, -12749.5) * mm});
            skLineSegment(sketch, "E1109", {"start": v(2148.16, -12749.5) * mm, "end": v(2145.7, -12754.22) * mm});
            skLineSegment(sketch, "E1110", {"start": v(2145.7, -12754.22) * mm, "end": v(2143.49, -12759.05) * mm});
            skLineSegment(sketch, "E1111", {"start": v(2143.49, -12759.05) * mm, "end": v(2141.53, -12764) * mm});
            skLineSegment(sketch, "E1112", {"start": v(2141.53, -12764) * mm, "end": v(2139.83, -12769.04) * mm});
            skLineSegment(sketch, "E1113", {"start": v(2139.83, -12769.04) * mm, "end": v(2138.4, -12774.16) * mm});
            skLineSegment(sketch, "E1114", {"start": v(2138.4, -12774.16) * mm, "end": v(2137.24, -12779.35) * mm});
            skLineSegment(sketch, "E1115", {"start": v(2137.24, -12779.35) * mm, "end": v(2136.36, -12784.6) * mm});
            skLineSegment(sketch, "E1116", {"start": v(2136.36, -12784.6) * mm, "end": v(2135.75, -12789.88) * mm});
            skLineSegment(sketch, "E1117", {"start": v(2135.75, -12789.88) * mm, "end": v(2135.42, -12795.19) * mm});
            skLineSegment(sketch, "E1118", {"start": v(2135.42, -12795.19) * mm, "end": v(2135.36, -12800.5) * mm});
            skLineSegment(sketch, "E1119", {"start": v(2135.36, -12800.5) * mm, "end": v(2135.42, -12802.59) * mm});
            skLineSegment(sketch, "E1120", {"start": v(94.42, -12791.59) * mm, "end": v(297.44, -12791.59) * mm});
            skLineSegment(sketch, "E1121", {"start": v(297.44, -12791.59) * mm, "end": v(297.5, -12786.27) * mm});
            skLineSegment(sketch, "E1122", {"start": v(297.5, -12786.27) * mm, "end": v(297.27, -12780.95) * mm});
            skLineSegment(sketch, "E1123", {"start": v(297.27, -12780.95) * mm, "end": v(296.77, -12775.66) * mm});
            skLineSegment(sketch, "E1124", {"start": v(296.77, -12775.66) * mm, "end": v(296, -12770.4) * mm});
            skLineSegment(sketch, "E1125", {"start": v(296, -12770.4) * mm, "end": v(294.94, -12765.19) * mm});
            skLineSegment(sketch, "E1126", {"start": v(294.94, -12765.19) * mm, "end": v(293.61, -12760.04) * mm});
            skLineSegment(sketch, "E1127", {"start": v(293.61, -12760.04) * mm, "end": v(292.02, -12754.96) * mm});
            skLineSegment(sketch, "E1128", {"start": v(292.02, -12754.96) * mm, "end": v(290.17, -12749.98) * mm});
            skLineSegment(sketch, "E1129", {"start": v(290.17, -12749.98) * mm, "end": v(288.06, -12745.1) * mm});
            skLineSegment(sketch, "E1130", {"start": v(288.06, -12745.1) * mm, "end": v(285.69, -12740.33) * mm});
            skLineSegment(sketch, "E1131", {"start": v(285.69, -12740.33) * mm, "end": v(283.08, -12735.7) * mm});
            skLineSegment(sketch, "E1132", {"start": v(283.08, -12735.7) * mm, "end": v(280.23, -12731.21) * mm});
            skLineSegment(sketch, "E1133", {"start": v(280.23, -12731.21) * mm, "end": v(277.15, -12726.88) * mm});
            skLineSegment(sketch, "E1134", {"start": v(277.15, -12726.88) * mm, "end": v(273.84, -12722.71) * mm});
            skLineSegment(sketch, "E1135", {"start": v(273.84, -12722.71) * mm, "end": v(270.32, -12718.72) * mm});
            skLineSegment(sketch, "E1136", {"start": v(270.32, -12718.72) * mm, "end": v(266.6, -12714.92) * mm});
            skLineSegment(sketch, "E1137", {"start": v(266.6, -12714.92) * mm, "end": v(262.69, -12711.32) * mm});
            skLineSegment(sketch, "E1138", {"start": v(262.69, -12711.32) * mm, "end": v(258.59, -12707.94) * mm});
            skLineSegment(sketch, "E1139", {"start": v(258.59, -12707.94) * mm, "end": v(254.32, -12704.77) * mm});
            skLineSegment(sketch, "E1140", {"start": v(254.32, -12704.77) * mm, "end": v(249.89, -12701.82) * mm});
            skLineSegment(sketch, "E1141", {"start": v(249.89, -12701.82) * mm, "end": v(245.3, -12699.12) * mm});
            skLineSegment(sketch, "E1142", {"start": v(245.3, -12699.12) * mm, "end": v(240.6, -12696.66) * mm});
            skLineSegment(sketch, "E1143", {"start": v(240.6, -12696.66) * mm, "end": v(235.76, -12694.44) * mm});
            skLineSegment(sketch, "E1144", {"start": v(235.76, -12694.44) * mm, "end": v(230.81, -12692.49) * mm});
            skLineSegment(sketch, "E1145", {"start": v(230.81, -12692.49) * mm, "end": v(225.77, -12690.8) * mm});
            skLineSegment(sketch, "E1146", {"start": v(225.77, -12690.8) * mm, "end": v(220.65, -12689.36) * mm});
            skLineSegment(sketch, "E1147", {"start": v(220.65, -12689.36) * mm, "end": v(215.46, -12688.2) * mm});
            skLineSegment(sketch, "E1148", {"start": v(215.46, -12688.2) * mm, "end": v(210.22, -12687.32) * mm});
            skLineSegment(sketch, "E1149", {"start": v(210.22, -12687.32) * mm, "end": v(204.93, -12686.7) * mm});
            skLineSegment(sketch, "E1150", {"start": v(204.93, -12686.7) * mm, "end": v(199.63, -12686.37) * mm});
            skLineSegment(sketch, "E1151", {"start": v(199.63, -12686.37) * mm, "end": v(194.3, -12686.32) * mm});
            skLineSegment(sketch, "E1152", {"start": v(194.3, -12686.32) * mm, "end": v(189, -12686.54) * mm});
            skLineSegment(sketch, "E1153", {"start": v(189, -12686.54) * mm, "end": v(183.7, -12687.05) * mm});
            skLineSegment(sketch, "E1154", {"start": v(183.7, -12687.05) * mm, "end": v(178.44, -12687.82) * mm});
            skLineSegment(sketch, "E1155", {"start": v(178.44, -12687.82) * mm, "end": v(173.23, -12688.88) * mm});
            skLineSegment(sketch, "E1156", {"start": v(173.23, -12688.88) * mm, "end": v(168.08, -12690.2) * mm});
            skLineSegment(sketch, "E1157", {"start": v(168.08, -12690.2) * mm, "end": v(163, -12691.8) * mm});
            skLineSegment(sketch, "E1158", {"start": v(163, -12691.8) * mm, "end": v(158.02, -12693.65) * mm});
            skLineSegment(sketch, "E1159", {"start": v(158.02, -12693.65) * mm, "end": v(153.14, -12695.76) * mm});
            skLineSegment(sketch, "E1160", {"start": v(153.14, -12695.76) * mm, "end": v(148.38, -12698.13) * mm});
            skLineSegment(sketch, "E1161", {"start": v(148.38, -12698.13) * mm, "end": v(143.74, -12700.74) * mm});
            skLineSegment(sketch, "E1162", {"start": v(143.74, -12700.74) * mm, "end": v(139.25, -12703.59) * mm});
            skLineSegment(sketch, "E1163", {"start": v(139.25, -12703.59) * mm, "end": v(134.92, -12706.67) * mm});
            skLineSegment(sketch, "E1164", {"start": v(134.92, -12706.67) * mm, "end": v(130.75, -12709.97) * mm});
            skLineSegment(sketch, "E1165", {"start": v(130.75, -12709.97) * mm, "end": v(126.76, -12713.5) * mm});
            skLineSegment(sketch, "E1166", {"start": v(126.76, -12713.5) * mm, "end": v(122.97, -12717.21) * mm});
            skLineSegment(sketch, "E1167", {"start": v(122.97, -12717.21) * mm, "end": v(119.37, -12721.13) * mm});
            skLineSegment(sketch, "E1168", {"start": v(119.37, -12721.13) * mm, "end": v(115.98, -12725.23) * mm});
            skLineSegment(sketch, "E1169", {"start": v(115.98, -12725.23) * mm, "end": v(112.8, -12729.5) * mm});
            skLineSegment(sketch, "E1170", {"start": v(112.8, -12729.5) * mm, "end": v(109.87, -12733.93) * mm});
            skLineSegment(sketch, "E1171", {"start": v(109.87, -12733.93) * mm, "end": v(107.16, -12738.5) * mm});
            skLineSegment(sketch, "E1172", {"start": v(107.16, -12738.5) * mm, "end": v(104.7, -12743.22) * mm});
            skLineSegment(sketch, "E1173", {"start": v(104.7, -12743.22) * mm, "end": v(102.48, -12748.05) * mm});
            skLineSegment(sketch, "E1174", {"start": v(102.48, -12748.05) * mm, "end": v(100.53, -12753) * mm});
            skLineSegment(sketch, "E1175", {"start": v(100.53, -12753) * mm, "end": v(98.83, -12758.04) * mm});
            skLineSegment(sketch, "E1176", {"start": v(98.83, -12758.04) * mm, "end": v(97.4, -12763.16) * mm});
            skLineSegment(sketch, "E1177", {"start": v(97.4, -12763.16) * mm, "end": v(96.24, -12768.35) * mm});
            skLineSegment(sketch, "E1178", {"start": v(96.24, -12768.35) * mm, "end": v(95.36, -12773.6) * mm});
            skLineSegment(sketch, "E1179", {"start": v(95.36, -12773.6) * mm, "end": v(94.75, -12778.88) * mm});
            skLineSegment(sketch, "E1180", {"start": v(94.75, -12778.88) * mm, "end": v(94.42, -12784.19) * mm});
            skLineSegment(sketch, "E1181", {"start": v(94.42, -12784.19) * mm, "end": v(94.36, -12789.5) * mm});
            skLineSegment(sketch, "E1182", {"start": v(94.36, -12789.5) * mm, "end": v(94.42, -12791.59) * mm});
            skLineSegment(sketch, "E1183", {"start": v(-1957.58, -12788.59) * mm, "end": v(-1754.56, -12788.59) * mm});
            skLineSegment(sketch, "E1184", {"start": v(-1754.56, -12788.59) * mm, "end": v(-1754.5, -12783.27) * mm});
            skLineSegment(sketch, "E1185", {"start": v(-1754.5, -12783.27) * mm, "end": v(-1754.73, -12777.95) * mm});
            skLineSegment(sketch, "E1186", {"start": v(-1754.73, -12777.95) * mm, "end": v(-1755.23, -12772.66) * mm});
            skLineSegment(sketch, "E1187", {"start": v(-1755.23, -12772.66) * mm, "end": v(-1756, -12767.4) * mm});
            skLineSegment(sketch, "E1188", {"start": v(-1756, -12767.4) * mm, "end": v(-1757.06, -12762.19) * mm});
            skLineSegment(sketch, "E1189", {"start": v(-1757.06, -12762.19) * mm, "end": v(-1758.38, -12757.04) * mm});
            skLineSegment(sketch, "E1190", {"start": v(-1758.38, -12757.04) * mm, "end": v(-1759.98, -12751.96) * mm});
            skLineSegment(sketch, "E1191", {"start": v(-1759.98, -12751.96) * mm, "end": v(-1761.83, -12746.98) * mm});
            skLineSegment(sketch, "E1192", {"start": v(-1761.83, -12746.98) * mm, "end": v(-1763.94, -12742.1) * mm});
            skLineSegment(sketch, "E1193", {"start": v(-1763.94, -12742.1) * mm, "end": v(-1766.31, -12737.33) * mm});
            skLineSegment(sketch, "E1194", {"start": v(-1766.31, -12737.33) * mm, "end": v(-1768.92, -12732.7) * mm});
            skLineSegment(sketch, "E1195", {"start": v(-1768.92, -12732.7) * mm, "end": v(-1771.77, -12728.21) * mm});
            skLineSegment(sketch, "E1196", {"start": v(-1771.77, -12728.21) * mm, "end": v(-1774.85, -12723.88) * mm});
            skLineSegment(sketch, "E1197", {"start": v(-1774.85, -12723.88) * mm, "end": v(-1778.16, -12719.71) * mm});
            skLineSegment(sketch, "E1198", {"start": v(-1778.16, -12719.71) * mm, "end": v(-1781.68, -12715.72) * mm});
            skLineSegment(sketch, "E1199", {"start": v(-1781.68, -12715.72) * mm, "end": v(-1785.4, -12711.92) * mm});
            skLineSegment(sketch, "E1200", {"start": v(-1785.4, -12711.92) * mm, "end": v(-1789.31, -12708.32) * mm});
            skLineSegment(sketch, "E1201", {"start": v(-1789.31, -12708.32) * mm, "end": v(-1793.41, -12704.94) * mm});
            skLineSegment(sketch, "E1202", {"start": v(-1793.41, -12704.94) * mm, "end": v(-1797.68, -12701.77) * mm});
            skLineSegment(sketch, "E1203", {"start": v(-1797.68, -12701.77) * mm, "end": v(-1802.11, -12698.82) * mm});
            skLineSegment(sketch, "E1204", {"start": v(-1802.11, -12698.82) * mm, "end": v(-1806.69, -12696.12) * mm});
            skLineSegment(sketch, "E1205", {"start": v(-1806.69, -12696.12) * mm, "end": v(-1811.4, -12693.66) * mm});
            skLineSegment(sketch, "E1206", {"start": v(-1811.4, -12693.66) * mm, "end": v(-1816.24, -12691.44) * mm});
            skLineSegment(sketch, "E1207", {"start": v(-1816.24, -12691.44) * mm, "end": v(-1821.19, -12689.49) * mm});
            skLineSegment(sketch, "E1208", {"start": v(-1821.19, -12689.49) * mm, "end": v(-1826.23, -12687.8) * mm});
            skLineSegment(sketch, "E1209", {"start": v(-1826.23, -12687.8) * mm, "end": v(-1831.35, -12686.36) * mm});
            skLineSegment(sketch, "E1210", {"start": v(-1831.35, -12686.36) * mm, "end": v(-1836.54, -12685.2) * mm});
            skLineSegment(sketch, "E1211", {"start": v(-1836.54, -12685.2) * mm, "end": v(-1841.78, -12684.32) * mm});
            skLineSegment(sketch, "E1212", {"start": v(-1841.78, -12684.32) * mm, "end": v(-1847.07, -12683.7) * mm});
            skLineSegment(sketch, "E1213", {"start": v(-1847.07, -12683.7) * mm, "end": v(-1852.37, -12683.37) * mm});
            skLineSegment(sketch, "E1214", {"start": v(-1852.37, -12683.37) * mm, "end": v(-1857.7, -12683.32) * mm});
            skLineSegment(sketch, "E1215", {"start": v(-1857.7, -12683.32) * mm, "end": v(-1863, -12683.54) * mm});
            skLineSegment(sketch, "E1216", {"start": v(-1863, -12683.54) * mm, "end": v(-1868.3, -12684.05) * mm});
            skLineSegment(sketch, "E1217", {"start": v(-1868.3, -12684.05) * mm, "end": v(-1873.56, -12684.82) * mm});
            skLineSegment(sketch, "E1218", {"start": v(-1873.56, -12684.82) * mm, "end": v(-1878.77, -12685.88) * mm});
            skLineSegment(sketch, "E1219", {"start": v(-1878.77, -12685.88) * mm, "end": v(-1883.92, -12687.2) * mm});
            skLineSegment(sketch, "E1220", {"start": v(-1883.92, -12687.2) * mm, "end": v(-1889, -12688.8) * mm});
            skLineSegment(sketch, "E1221", {"start": v(-1889, -12688.8) * mm, "end": v(-1893.98, -12690.65) * mm});
            skLineSegment(sketch, "E1222", {"start": v(-1893.98, -12690.65) * mm, "end": v(-1898.86, -12692.76) * mm});
            skLineSegment(sketch, "E1223", {"start": v(-1898.86, -12692.76) * mm, "end": v(-1903.62, -12695.13) * mm});
            skLineSegment(sketch, "E1224", {"start": v(-1903.62, -12695.13) * mm, "end": v(-1908.26, -12697.74) * mm});
            skLineSegment(sketch, "E1225", {"start": v(-1908.26, -12697.74) * mm, "end": v(-1912.75, -12700.59) * mm});
            skLineSegment(sketch, "E1226", {"start": v(-1912.75, -12700.59) * mm, "end": v(-1917.08, -12703.67) * mm});
            skLineSegment(sketch, "E1227", {"start": v(-1917.08, -12703.67) * mm, "end": v(-1921.25, -12706.97) * mm});
            skLineSegment(sketch, "E1228", {"start": v(-1921.25, -12706.97) * mm, "end": v(-1925.24, -12710.5) * mm});
            skLineSegment(sketch, "E1229", {"start": v(-1925.24, -12710.5) * mm, "end": v(-1929.03, -12714.21) * mm});
            skLineSegment(sketch, "E1230", {"start": v(-1929.03, -12714.21) * mm, "end": v(-1932.63, -12718.13) * mm});
            skLineSegment(sketch, "E1231", {"start": v(-1932.63, -12718.13) * mm, "end": v(-1936.02, -12722.23) * mm});
            skLineSegment(sketch, "E1232", {"start": v(-1936.02, -12722.23) * mm, "end": v(-1939.2, -12726.5) * mm});
            skLineSegment(sketch, "E1233", {"start": v(-1939.2, -12726.5) * mm, "end": v(-1942.13, -12730.93) * mm});
            skLineSegment(sketch, "E1234", {"start": v(-1942.13, -12730.93) * mm, "end": v(-1944.84, -12735.5) * mm});
            skLineSegment(sketch, "E1235", {"start": v(-1944.84, -12735.5) * mm, "end": v(-1947.3, -12740.22) * mm});
            skLineSegment(sketch, "E1236", {"start": v(-1947.3, -12740.22) * mm, "end": v(-1949.51, -12745.05) * mm});
            skLineSegment(sketch, "E1237", {"start": v(-1949.51, -12745.05) * mm, "end": v(-1951.47, -12750) * mm});
            skLineSegment(sketch, "E1238", {"start": v(-1951.47, -12750) * mm, "end": v(-1953.17, -12755.04) * mm});
            skLineSegment(sketch, "E1239", {"start": v(-1953.17, -12755.04) * mm, "end": v(-1954.6, -12760.16) * mm});
            skLineSegment(sketch, "E1240", {"start": v(-1954.6, -12760.16) * mm, "end": v(-1955.76, -12765.35) * mm});
            skLineSegment(sketch, "E1241", {"start": v(-1955.76, -12765.35) * mm, "end": v(-1956.64, -12770.6) * mm});
            skLineSegment(sketch, "E1242", {"start": v(-1956.64, -12770.6) * mm, "end": v(-1957.25, -12775.88) * mm});
            skLineSegment(sketch, "E1243", {"start": v(-1957.25, -12775.88) * mm, "end": v(-1957.58, -12781.19) * mm});
            skLineSegment(sketch, "E1244", {"start": v(-1957.58, -12781.19) * mm, "end": v(-1957.64, -12786.5) * mm});
            skLineSegment(sketch, "E1245", {"start": v(-1957.64, -12786.5) * mm, "end": v(-1957.58, -12788.59) * mm});
            skLineSegment(sketch, "E1246", {"start": v(2848.83, -12391.86) * mm, "end": v(2863.34, -12389.95) * mm});
            skLineSegment(sketch, "E1247", {"start": v(2863.34, -12389.95) * mm, "end": v(2863.58, -12390.08) * mm});
            skLineSegment(sketch, "E1248", {"start": v(2863.58, -12390.08) * mm, "end": v(2863.83, -12390.22) * mm});
            skLineSegment(sketch, "E1249", {"start": v(2863.83, -12390.22) * mm, "end": v(2864.07, -12390.36) * mm});
            skLineSegment(sketch, "E1250", {"start": v(2864.07, -12390.36) * mm, "end": v(2864.31, -12390.5) * mm});
            skLineSegment(sketch, "E1251", {"start": v(2864.31, -12390.5) * mm, "end": v(2864.55, -12390.64) * mm});
            skLineSegment(sketch, "E1252", {"start": v(2864.55, -12390.64) * mm, "end": v(2864.79, -12390.79) * mm});
            skLineSegment(sketch, "E1253", {"start": v(2864.79, -12390.79) * mm, "end": v(2865.02, -12390.93) * mm});
            skLineSegment(sketch, "E1254", {"start": v(2865.02, -12390.93) * mm, "end": v(2865.25, -12391.09) * mm});
            skLineSegment(sketch, "E1255", {"start": v(2865.25, -12391.09) * mm, "end": v(2865.47, -12391.24) * mm});
            skLineSegment(sketch, "E1256", {"start": v(2865.47, -12391.24) * mm, "end": v(2865.68, -12391.4) * mm});
            skLineSegment(sketch, "E1257", {"start": v(2865.68, -12391.4) * mm, "end": v(2865.9, -12391.57) * mm});
            skLineSegment(sketch, "E1258", {"start": v(2865.9, -12391.57) * mm, "end": v(2866.1, -12391.74) * mm});
            skLineSegment(sketch, "E1259", {"start": v(2866.1, -12391.74) * mm, "end": v(2866.29, -12391.92) * mm});
            skLineSegment(sketch, "E1260", {"start": v(2866.29, -12391.92) * mm, "end": v(2866.47, -12392.11) * mm});
            skLineSegment(sketch, "E1261", {"start": v(2866.47, -12392.11) * mm, "end": v(2866.65, -12392.3) * mm});
            skLineSegment(sketch, "E1262", {"start": v(2866.65, -12392.3) * mm, "end": v(2866.81, -12392.5) * mm});
            skLineSegment(sketch, "E1263", {"start": v(2866.81, -12392.5) * mm, "end": v(2866.97, -12392.72) * mm});
            skLineSegment(sketch, "E1264", {"start": v(2866.97, -12392.72) * mm, "end": v(2867.11, -12392.94) * mm});
            skLineSegment(sketch, "E1265", {"start": v(2867.11, -12392.94) * mm, "end": v(2867.24, -12393.17) * mm});
            skLineSegment(sketch, "E1266", {"start": v(2867.24, -12393.17) * mm, "end": v(2867.37, -12393.41) * mm});
            skLineSegment(sketch, "E1267", {"start": v(2867.37, -12393.41) * mm, "end": v(2867.47, -12393.66) * mm});
            skLineSegment(sketch, "E1268", {"start": v(2867.47, -12393.66) * mm, "end": v(2867.56, -12393.93) * mm});
            skLineSegment(sketch, "E1269", {"start": v(2867.56, -12393.93) * mm, "end": v(2867.64, -12394.2) * mm});
            skLineSegment(sketch, "E1270", {"start": v(2867.64, -12394.2) * mm, "end": v(2867.7, -12394.49) * mm});
            skLineSegment(sketch, "E1271", {"start": v(2867.7, -12394.49) * mm, "end": v(2867.76, -12394.78) * mm});
            skLineSegment(sketch, "E1272", {"start": v(2867.76, -12394.78) * mm, "end": v(2867.79, -12395.08) * mm});
            skLineSegment(sketch, "E1273", {"start": v(2867.79, -12395.08) * mm, "end": v(2867.81, -12395.38) * mm});
            skLineSegment(sketch, "E1274", {"start": v(2867.81, -12395.38) * mm, "end": v(2867.82, -12395.7) * mm});
            skLineSegment(sketch, "E1275", {"start": v(2867.82, -12395.7) * mm, "end": v(2867.82, -12396) * mm});
            skLineSegment(sketch, "E1276", {"start": v(2867.82, -12396) * mm, "end": v(2867.8, -12396.31) * mm});
            skLineSegment(sketch, "E1277", {"start": v(2867.8, -12396.31) * mm, "end": v(2867.77, -12396.62) * mm});
            skLineSegment(sketch, "E1278", {"start": v(2867.77, -12396.62) * mm, "end": v(2867.72, -12396.93) * mm});
            skLineSegment(sketch, "E1279", {"start": v(2867.72, -12396.93) * mm, "end": v(2867.66, -12397.23) * mm});
            skLineSegment(sketch, "E1280", {"start": v(2867.66, -12397.23) * mm, "end": v(2867.6, -12397.53) * mm});
            skLineSegment(sketch, "E1281", {"start": v(2867.6, -12397.53) * mm, "end": v(2867.51, -12397.81) * mm});
            skLineSegment(sketch, "E1282", {"start": v(2867.51, -12397.81) * mm, "end": v(2867.42, -12398.1) * mm});
            skLineSegment(sketch, "E1283", {"start": v(2867.42, -12398.1) * mm, "end": v(2867.3, -12398.37) * mm});
            skLineSegment(sketch, "E1284", {"start": v(2867.3, -12398.37) * mm, "end": v(2867.18, -12398.64) * mm});
            skLineSegment(sketch, "E1285", {"start": v(2867.18, -12398.64) * mm, "end": v(2867.04, -12398.9) * mm});
            skLineSegment(sketch, "E1286", {"start": v(2867.04, -12398.9) * mm, "end": v(2866.9, -12399.14) * mm});
            skLineSegment(sketch, "E1287", {"start": v(2866.9, -12399.14) * mm, "end": v(2866.74, -12399.38) * mm});
            skLineSegment(sketch, "E1288", {"start": v(2866.74, -12399.38) * mm, "end": v(2866.57, -12399.6) * mm});
            skLineSegment(sketch, "E1289", {"start": v(2866.57, -12399.6) * mm, "end": v(2866.4, -12399.83) * mm});
            skLineSegment(sketch, "E1290", {"start": v(2866.4, -12399.83) * mm, "end": v(2866.2, -12400.04) * mm});
            skLineSegment(sketch, "E1291", {"start": v(2866.2, -12400.04) * mm, "end": v(2866.01, -12400.25) * mm});
            skLineSegment(sketch, "E1292", {"start": v(2866.01, -12400.25) * mm, "end": v(2865.81, -12400.44) * mm});
            skLineSegment(sketch, "E1293", {"start": v(2865.81, -12400.44) * mm, "end": v(2865.6, -12400.64) * mm});
            skLineSegment(sketch, "E1294", {"start": v(2865.6, -12400.64) * mm, "end": v(2865.4, -12400.83) * mm});
            skLineSegment(sketch, "E1295", {"start": v(2865.4, -12400.83) * mm, "end": v(2865.18, -12401.01) * mm});
            skLineSegment(sketch, "E1296", {"start": v(2865.18, -12401.01) * mm, "end": v(2864.97, -12401.2) * mm});
            skLineSegment(sketch, "E1297", {"start": v(2864.97, -12401.2) * mm, "end": v(2864.74, -12401.37) * mm});
            skLineSegment(sketch, "E1298", {"start": v(2864.74, -12401.37) * mm, "end": v(2864.52, -12401.54) * mm});
            skLineSegment(sketch, "E1299", {"start": v(2864.52, -12401.54) * mm, "end": v(2864.3, -12401.72) * mm});
            skLineSegment(sketch, "E1300", {"start": v(2864.3, -12401.72) * mm, "end": v(2864.07, -12401.9) * mm});
            skLineSegment(sketch, "E1301", {"start": v(2864.07, -12401.9) * mm, "end": v(2848.58, -12399.75) * mm});
            skLineSegment(sketch, "E1302", {"start": v(2850.38, -12466.33) * mm, "end": v(2850.38, -12476.5) * mm});
            skLineSegment(sketch, "E1303", {"start": v(2834.5, -12466.33) * mm, "end": v(2834.5, -12476.5) * mm});
            skLineSegment(sketch, "E1304", {"start": v(2835.56, -12391.15) * mm, "end": v(2822.41, -12389.4) * mm});
            skLineSegment(sketch, "E1305", {"start": v(2822.41, -12389.4) * mm, "end": v(2820.91, -12390.33) * mm});
            skLineSegment(sketch, "E1306", {"start": v(2820.91, -12390.33) * mm, "end": v(2819.56, -12391.36) * mm});
            skLineSegment(sketch, "E1307", {"start": v(2819.56, -12391.36) * mm, "end": v(2818.5, -12392.58) * mm});
            skLineSegment(sketch, "E1308", {"start": v(2818.5, -12392.58) * mm, "end": v(2817.9, -12394.1) * mm});
            skLineSegment(sketch, "E1309", {"start": v(2817.9, -12394.1) * mm, "end": v(2817.82, -12395.83) * mm});
            skLineSegment(sketch, "E1310", {"start": v(2817.82, -12395.83) * mm, "end": v(2818.18, -12397.63) * mm});
            skLineSegment(sketch, "E1311", {"start": v(2818.18, -12397.63) * mm, "end": v(2818.91, -12399.26) * mm});
            skLineSegment(sketch, "E1312", {"start": v(2818.91, -12399.26) * mm, "end": v(2819.93, -12400.44) * mm});
            skLineSegment(sketch, "E1313", {"start": v(2819.93, -12400.44) * mm, "end": v(2821.17, -12401.01) * mm});
            skLineSegment(sketch, "E1314", {"start": v(2821.17, -12401.01) * mm, "end": v(2822.56, -12401.11) * mm});
            skLineSegment(sketch, "E1315", {"start": v(2822.56, -12401.11) * mm, "end": v(2824.01, -12400.99) * mm});
            skLineSegment(sketch, "E1316", {"start": v(2824.01, -12400.99) * mm, "end": v(2835.75, -12399.59) * mm});
            skLineSegment(sketch, "E1317", {"start": v(2835.52, -12389.22) * mm, "end": v(2835.81, -12402.43) * mm});
            skLineSegment(sketch, "E1318", {"start": v(2835.81, -12402.43) * mm, "end": v(2836.15, -12402.85) * mm});
            skLineSegment(sketch, "E1319", {"start": v(2836.15, -12402.85) * mm, "end": v(2836.52, -12403.24) * mm});
            skLineSegment(sketch, "E1320", {"start": v(2836.52, -12403.24) * mm, "end": v(2836.9, -12403.61) * mm});
            skLineSegment(sketch, "E1321", {"start": v(2836.9, -12403.61) * mm, "end": v(2837.29, -12403.96) * mm});
            skLineSegment(sketch, "E1322", {"start": v(2837.29, -12403.96) * mm, "end": v(2837.7, -12404.28) * mm});
            skLineSegment(sketch, "E1323", {"start": v(2837.7, -12404.28) * mm, "end": v(2838.11, -12404.57) * mm});
            skLineSegment(sketch, "E1324", {"start": v(2838.11, -12404.57) * mm, "end": v(2838.54, -12404.83) * mm});
            skLineSegment(sketch, "E1325", {"start": v(2838.54, -12404.83) * mm, "end": v(2838.98, -12405.06) * mm});
            skLineSegment(sketch, "E1326", {"start": v(2838.98, -12405.06) * mm, "end": v(2839.43, -12405.27) * mm});
            skLineSegment(sketch, "E1327", {"start": v(2839.43, -12405.27) * mm, "end": v(2839.9, -12405.45) * mm});
            skLineSegment(sketch, "E1328", {"start": v(2839.9, -12405.45) * mm, "end": v(2840.36, -12405.6) * mm});
            skLineSegment(sketch, "E1329", {"start": v(2840.36, -12405.6) * mm, "end": v(2840.83, -12405.71) * mm});
            skLineSegment(sketch, "E1330", {"start": v(2840.83, -12405.71) * mm, "end": v(2841.3, -12405.8) * mm});
            skLineSegment(sketch, "E1331", {"start": v(2841.3, -12405.8) * mm, "end": v(2841.78, -12405.85) * mm});
            skLineSegment(sketch, "E1332", {"start": v(2841.78, -12405.85) * mm, "end": v(2842.26, -12405.87) * mm});
            skLineSegment(sketch, "E1333", {"start": v(2842.26, -12405.87) * mm, "end": v(2842.74, -12405.86) * mm});
            skLineSegment(sketch, "E1334", {"start": v(2842.74, -12405.86) * mm, "end": v(2843.22, -12405.83) * mm});
            skLineSegment(sketch, "E1335", {"start": v(2843.22, -12405.83) * mm, "end": v(2843.7, -12405.76) * mm});
            skLineSegment(sketch, "E1336", {"start": v(2843.7, -12405.76) * mm, "end": v(2844.17, -12405.65) * mm});
            skLineSegment(sketch, "E1337", {"start": v(2844.17, -12405.65) * mm, "end": v(2844.64, -12405.52) * mm});
            skLineSegment(sketch, "E1338", {"start": v(2844.64, -12405.52) * mm, "end": v(2845.1, -12405.36) * mm});
            skLineSegment(sketch, "E1339", {"start": v(2845.1, -12405.36) * mm, "end": v(2845.55, -12405.17) * mm});
            skLineSegment(sketch, "E1340", {"start": v(2845.55, -12405.17) * mm, "end": v(2846, -12404.95) * mm});
            skLineSegment(sketch, "E1341", {"start": v(2846, -12404.95) * mm, "end": v(2846.44, -12404.7) * mm});
            skLineSegment(sketch, "E1342", {"start": v(2846.44, -12404.7) * mm, "end": v(2846.86, -12404.42) * mm});
            skLineSegment(sketch, "E1343", {"start": v(2846.86, -12404.42) * mm, "end": v(2847.27, -12404.11) * mm});
            skLineSegment(sketch, "E1344", {"start": v(2847.27, -12404.11) * mm, "end": v(2847.67, -12403.78) * mm});
            skLineSegment(sketch, "E1345", {"start": v(2847.67, -12403.78) * mm, "end": v(2848.06, -12403.42) * mm});
            skLineSegment(sketch, "E1346", {"start": v(2848.06, -12403.42) * mm, "end": v(2848.42, -12403.04) * mm});
            skLineSegment(sketch, "E1347", {"start": v(2848.42, -12403.04) * mm, "end": v(2848.48, -12402.98) * mm});
            skLineSegment(sketch, "E1348", {"start": v(2848.48, -12402.98) * mm, "end": v(2848.92, -12388.86) * mm});
            skLineSegment(sketch, "E1349", {"start": v(2848.92, -12388.86) * mm, "end": v(2848.76, -12389.28) * mm});
            skLineSegment(sketch, "E1350", {"start": v(2848.76, -12389.28) * mm, "end": v(2848.57, -12389.7) * mm});
            skLineSegment(sketch, "E1351", {"start": v(2848.57, -12389.7) * mm, "end": v(2848.37, -12390.11) * mm});
            skLineSegment(sketch, "E1352", {"start": v(2848.37, -12390.11) * mm, "end": v(2848.14, -12390.51) * mm});
            skLineSegment(sketch, "E1353", {"start": v(2848.14, -12390.51) * mm, "end": v(2847.9, -12390.9) * mm});
            skLineSegment(sketch, "E1354", {"start": v(2847.9, -12390.9) * mm, "end": v(2847.65, -12391.26) * mm});
            skLineSegment(sketch, "E1355", {"start": v(2847.65, -12391.26) * mm, "end": v(2847.38, -12391.6) * mm});
            skLineSegment(sketch, "E1356", {"start": v(2847.38, -12391.6) * mm, "end": v(2847.1, -12391.94) * mm});
            skLineSegment(sketch, "E1357", {"start": v(2847.1, -12391.94) * mm, "end": v(2846.8, -12392.25) * mm});
            skLineSegment(sketch, "E1358", {"start": v(2846.8, -12392.25) * mm, "end": v(2846.5, -12392.55) * mm});
            skLineSegment(sketch, "E1359", {"start": v(2846.5, -12392.55) * mm, "end": v(2846.18, -12392.82) * mm});
            skLineSegment(sketch, "E1360", {"start": v(2846.18, -12392.82) * mm, "end": v(2845.84, -12393.07) * mm});
            skLineSegment(sketch, "E1361", {"start": v(2845.84, -12393.07) * mm, "end": v(2845.5, -12393.3) * mm});
            skLineSegment(sketch, "E1362", {"start": v(2845.5, -12393.3) * mm, "end": v(2845.15, -12393.5) * mm});
            skLineSegment(sketch, "E1363", {"start": v(2845.15, -12393.5) * mm, "end": v(2844.79, -12393.69) * mm});
            skLineSegment(sketch, "E1364", {"start": v(2844.79, -12393.69) * mm, "end": v(2844.42, -12393.85) * mm});
            skLineSegment(sketch, "E1365", {"start": v(2844.42, -12393.85) * mm, "end": v(2844.05, -12393.98) * mm});
            skLineSegment(sketch, "E1366", {"start": v(2844.05, -12393.98) * mm, "end": v(2843.67, -12394.1) * mm});
            skLineSegment(sketch, "E1367", {"start": v(2843.67, -12394.1) * mm, "end": v(2843.29, -12394.18) * mm});
            skLineSegment(sketch, "E1368", {"start": v(2843.29, -12394.18) * mm, "end": v(2842.9, -12394.24) * mm});
            skLineSegment(sketch, "E1369", {"start": v(2842.9, -12394.24) * mm, "end": v(2842.51, -12394.28) * mm});
            skLineSegment(sketch, "E1370", {"start": v(2842.51, -12394.28) * mm, "end": v(2842.12, -12394.3) * mm});
            skLineSegment(sketch, "E1371", {"start": v(2842.12, -12394.3) * mm, "end": v(2841.74, -12394.28) * mm});
            skLineSegment(sketch, "E1372", {"start": v(2841.74, -12394.28) * mm, "end": v(2841.35, -12394.24) * mm});
            skLineSegment(sketch, "E1373", {"start": v(2841.35, -12394.24) * mm, "end": v(2840.96, -12394.17) * mm});
            skLineSegment(sketch, "E1374", {"start": v(2840.96, -12394.17) * mm, "end": v(2840.58, -12394.08) * mm});
            skLineSegment(sketch, "E1375", {"start": v(2840.58, -12394.08) * mm, "end": v(2840.2, -12393.97) * mm});
            skLineSegment(sketch, "E1376", {"start": v(2840.2, -12393.97) * mm, "end": v(2839.83, -12393.83) * mm});
            skLineSegment(sketch, "E1377", {"start": v(2839.83, -12393.83) * mm, "end": v(2839.46, -12393.67) * mm});
            skLineSegment(sketch, "E1378", {"start": v(2839.46, -12393.67) * mm, "end": v(2839.1, -12393.48) * mm});
            skLineSegment(sketch, "E1379", {"start": v(2839.1, -12393.48) * mm, "end": v(2838.75, -12393.27) * mm});
            skLineSegment(sketch, "E1380", {"start": v(2838.75, -12393.27) * mm, "end": v(2838.41, -12393.04) * mm});
            skLineSegment(sketch, "E1381", {"start": v(2838.41, -12393.04) * mm, "end": v(2838.08, -12392.78) * mm});
            skLineSegment(sketch, "E1382", {"start": v(2838.08, -12392.78) * mm, "end": v(2837.76, -12392.5) * mm});
            skLineSegment(sketch, "E1383", {"start": v(2837.76, -12392.5) * mm, "end": v(2837.46, -12392.21) * mm});
            skLineSegment(sketch, "E1384", {"start": v(2837.46, -12392.21) * mm, "end": v(2837.16, -12391.9) * mm});
            skLineSegment(sketch, "E1385", {"start": v(2837.16, -12391.9) * mm, "end": v(2836.88, -12391.56) * mm});
            skLineSegment(sketch, "E1386", {"start": v(2836.88, -12391.56) * mm, "end": v(2836.61, -12391.21) * mm});
            skLineSegment(sketch, "E1387", {"start": v(2836.61, -12391.21) * mm, "end": v(2836.36, -12390.84) * mm});
            skLineSegment(sketch, "E1388", {"start": v(2836.36, -12390.84) * mm, "end": v(2836.13, -12390.46) * mm});
            skLineSegment(sketch, "E1389", {"start": v(2836.13, -12390.46) * mm, "end": v(2835.9, -12390.06) * mm});
            skLineSegment(sketch, "E1390", {"start": v(2835.9, -12390.06) * mm, "end": v(2835.7, -12389.65) * mm});
            skLineSegment(sketch, "E1391", {"start": v(2835.7, -12389.65) * mm, "end": v(2835.52, -12389.22) * mm});
            skLineSegment(sketch, "E1392", {"start": v(2835.52, -12389.22) * mm, "end": v(2835.52, -12389.21) * mm});
            skLineSegment(sketch, "E1393", {"start": v(2835.52, -12389.21) * mm, "end": v(2835.75, -12388.78) * mm});
            skLineSegment(sketch, "E1394", {"start": v(2835.75, -12388.78) * mm, "end": v(2836, -12388.36) * mm});
            skLineSegment(sketch, "E1395", {"start": v(2836, -12388.36) * mm, "end": v(2836.27, -12387.96) * mm});
            skLineSegment(sketch, "E1396", {"start": v(2836.27, -12387.96) * mm, "end": v(2836.55, -12387.57) * mm});
            skLineSegment(sketch, "E1397", {"start": v(2836.55, -12387.57) * mm, "end": v(2836.84, -12387.2) * mm});
            skLineSegment(sketch, "E1398", {"start": v(2836.84, -12387.2) * mm, "end": v(2837.16, -12386.86) * mm});
            skLineSegment(sketch, "E1399", {"start": v(2837.16, -12386.86) * mm, "end": v(2837.48, -12386.54) * mm});
            skLineSegment(sketch, "E1400", {"start": v(2837.48, -12386.54) * mm, "end": v(2837.82, -12386.23) * mm});
            skLineSegment(sketch, "E1401", {"start": v(2837.82, -12386.23) * mm, "end": v(2838.17, -12385.95) * mm});
            skLineSegment(sketch, "E1402", {"start": v(2838.17, -12385.95) * mm, "end": v(2838.54, -12385.7) * mm});
            skLineSegment(sketch, "E1403", {"start": v(2838.54, -12385.7) * mm, "end": v(2838.91, -12385.46) * mm});
            skLineSegment(sketch, "E1404", {"start": v(2838.91, -12385.46) * mm, "end": v(2839.3, -12385.25) * mm});
            skLineSegment(sketch, "E1405", {"start": v(2839.3, -12385.25) * mm, "end": v(2839.69, -12385.07) * mm});
            skLineSegment(sketch, "E1406", {"start": v(2839.69, -12385.07) * mm, "end": v(2840.08, -12384.91) * mm});
            skLineSegment(sketch, "E1407", {"start": v(2840.08, -12384.91) * mm, "end": v(2840.49, -12384.78) * mm});
            skLineSegment(sketch, "E1408", {"start": v(2840.49, -12384.78) * mm, "end": v(2840.9, -12384.67) * mm});
            skLineSegment(sketch, "E1409", {"start": v(2840.9, -12384.67) * mm, "end": v(2841.31, -12384.6) * mm});
            skLineSegment(sketch, "E1410", {"start": v(2841.31, -12384.6) * mm, "end": v(2841.73, -12384.54) * mm});
            skLineSegment(sketch, "E1411", {"start": v(2841.73, -12384.54) * mm, "end": v(2842.15, -12384.52) * mm});
            skLineSegment(sketch, "E1412", {"start": v(2842.15, -12384.52) * mm, "end": v(2842.56, -12384.52) * mm});
            skLineSegment(sketch, "E1413", {"start": v(2842.56, -12384.52) * mm, "end": v(2842.98, -12384.55) * mm});
            skLineSegment(sketch, "E1414", {"start": v(2842.98, -12384.55) * mm, "end": v(2843.4, -12384.6) * mm});
            skLineSegment(sketch, "E1415", {"start": v(2843.4, -12384.6) * mm, "end": v(2843.8, -12384.7) * mm});
            skLineSegment(sketch, "E1416", {"start": v(2843.8, -12384.7) * mm, "end": v(2844.22, -12384.8) * mm});
            skLineSegment(sketch, "E1417", {"start": v(2844.22, -12384.8) * mm, "end": v(2844.62, -12384.94) * mm});
            skLineSegment(sketch, "E1418", {"start": v(2844.62, -12384.94) * mm, "end": v(2845.02, -12385.1) * mm});
            skLineSegment(sketch, "E1419", {"start": v(2845.02, -12385.1) * mm, "end": v(2845.4, -12385.3) * mm});
            skLineSegment(sketch, "E1420", {"start": v(2845.4, -12385.3) * mm, "end": v(2845.79, -12385.5) * mm});
            skLineSegment(sketch, "E1421", {"start": v(2845.79, -12385.5) * mm, "end": v(2846.16, -12385.74) * mm});
            skLineSegment(sketch, "E1422", {"start": v(2846.16, -12385.74) * mm, "end": v(2846.52, -12386) * mm});
            skLineSegment(sketch, "E1423", {"start": v(2846.52, -12386) * mm, "end": v(2846.87, -12386.29) * mm});
            skLineSegment(sketch, "E1424", {"start": v(2846.87, -12386.29) * mm, "end": v(2847.2, -12386.6) * mm});
            skLineSegment(sketch, "E1425", {"start": v(2847.2, -12386.6) * mm, "end": v(2847.53, -12386.93) * mm});
            skLineSegment(sketch, "E1426", {"start": v(2847.53, -12386.93) * mm, "end": v(2847.84, -12387.28) * mm});
            skLineSegment(sketch, "E1427", {"start": v(2847.84, -12387.28) * mm, "end": v(2848.14, -12387.65) * mm});
            skLineSegment(sketch, "E1428", {"start": v(2848.14, -12387.65) * mm, "end": v(2848.42, -12388.03) * mm});
            skLineSegment(sketch, "E1429", {"start": v(2848.42, -12388.03) * mm, "end": v(2848.68, -12388.44) * mm});
            skLineSegment(sketch, "E1430", {"start": v(2848.68, -12388.44) * mm, "end": v(2848.92, -12388.86) * mm});
            skLineSegment(sketch, "E1431", {"start": v(2837.85, -12408.77) * mm, "end": v(2832.75, -12414.02) * mm});
            skLineSegment(sketch, "E1432", {"start": v(2832.75, -12414.02) * mm, "end": v(2832.46, -12429.22) * mm});
            skLineSegment(sketch, "E1433", {"start": v(2832.46, -12429.22) * mm, "end": v(2833.94, -12429.82) * mm});
            skLineSegment(sketch, "E1434", {"start": v(2833.94, -12429.82) * mm, "end": v(2835.44, -12430.32) * mm});
            skLineSegment(sketch, "E1435", {"start": v(2835.44, -12430.32) * mm, "end": v(2836.96, -12430.72) * mm});
            skLineSegment(sketch, "E1436", {"start": v(2836.96, -12430.72) * mm, "end": v(2838.5, -12431.02) * mm});
            skLineSegment(sketch, "E1437", {"start": v(2838.5, -12431.02) * mm, "end": v(2840.04, -12431.23) * mm});
            skLineSegment(sketch, "E1438", {"start": v(2840.04, -12431.23) * mm, "end": v(2841.59, -12431.33) * mm});
            skLineSegment(sketch, "E1439", {"start": v(2841.59, -12431.33) * mm, "end": v(2843.14, -12431.33) * mm});
            skLineSegment(sketch, "E1440", {"start": v(2843.14, -12431.33) * mm, "end": v(2844.69, -12431.23) * mm});
            skLineSegment(sketch, "E1441", {"start": v(2844.69, -12431.23) * mm, "end": v(2846.24, -12431.03) * mm});
            skLineSegment(sketch, "E1442", {"start": v(2846.24, -12431.03) * mm, "end": v(2847.77, -12430.73) * mm});
            skLineSegment(sketch, "E1443", {"start": v(2847.77, -12430.73) * mm, "end": v(2849.29, -12430.33) * mm});
            skLineSegment(sketch, "E1444", {"start": v(2849.29, -12430.33) * mm, "end": v(2850.79, -12429.83) * mm});
            skLineSegment(sketch, "E1445", {"start": v(2850.79, -12429.83) * mm, "end": v(2852.08, -12429.31) * mm});
            skLineSegment(sketch, "E1446", {"start": v(2852.08, -12429.31) * mm, "end": v(2851.54, -12414.92) * mm});
            skLineSegment(sketch, "E1447", {"start": v(2851.54, -12414.92) * mm, "end": v(2847.03, -12408.59) * mm});
            skLineSegment(sketch, "E1448", {"start": v(2837.85, -12404.39) * mm, "end": v(2837.85, -12417.68) * mm});
            skLineSegment(sketch, "E1449", {"start": v(2837.85, -12417.68) * mm, "end": v(2838.83, -12417.94) * mm});
            skLineSegment(sketch, "E1450", {"start": v(2838.83, -12417.94) * mm, "end": v(2839.83, -12418.14) * mm});
            skLineSegment(sketch, "E1451", {"start": v(2839.83, -12418.14) * mm, "end": v(2840.83, -12418.27) * mm});
            skLineSegment(sketch, "E1452", {"start": v(2840.83, -12418.27) * mm, "end": v(2841.83, -12418.34) * mm});
            skLineSegment(sketch, "E1453", {"start": v(2841.83, -12418.34) * mm, "end": v(2842.84, -12418.34) * mm});
            skLineSegment(sketch, "E1454", {"start": v(2842.84, -12418.34) * mm, "end": v(2843.84, -12418.28) * mm});
            skLineSegment(sketch, "E1455", {"start": v(2843.84, -12418.28) * mm, "end": v(2844.84, -12418.15) * mm});
            skLineSegment(sketch, "E1456", {"start": v(2844.84, -12418.15) * mm, "end": v(2845.83, -12417.96) * mm});
            skLineSegment(sketch, "E1457", {"start": v(2845.83, -12417.96) * mm, "end": v(2846.82, -12417.7) * mm});
            skLineSegment(sketch, "E1458", {"start": v(2846.82, -12417.7) * mm, "end": v(2847.03, -12417.64) * mm});
            skLineSegment(sketch, "E1459", {"start": v(2847.03, -12417.64) * mm, "end": v(2847.03, -12404.3) * mm});
            skLineSegment(sketch, "E1460", {"start": v(2832.46, -12429.22) * mm, "end": v(2828.67, -12429.22) * mm});
            skLineSegment(sketch, "E1461", {"start": v(2828.67, -12429.22) * mm, "end": v(2828.67, -12466.33) * mm});
            skLineSegment(sketch, "E1462", {"start": v(2828.67, -12466.33) * mm, "end": v(2855.87, -12466.33) * mm});
            skLineSegment(sketch, "E1463", {"start": v(2855.87, -12466.33) * mm, "end": v(2855.87, -12429.31) * mm});
            skLineSegment(sketch, "E1464", {"start": v(2855.87, -12429.31) * mm, "end": v(2852.08, -12429.31) * mm});
            skLineSegment(sketch, "E1465", {"start": v(2828.88, -12476.5) * mm, "end": v(2856, -12476.5) * mm});
            skLineSegment(sketch, "E1466", {"start": v(2856, -12476.5) * mm, "end": v(2856, -12488.5) * mm});
            skLineSegment(sketch, "E1467", {"start": v(2856, -12488.5) * mm, "end": v(2828.88, -12488.5) * mm});
            skLineSegment(sketch, "E1468", {"start": v(2828.88, -12488.5) * mm, "end": v(2828.88, -12476.5) * mm});
            skEllipticalArc(sketch, "E1469", {});
            skEllipticalArc(sketch, "E1470", {});
            skArc(sketch, "E1471", {"start": v(2669.33, -12801.65) * mm, "mid": v(2649.44, -12781.65) * mm, "end": v(2629.34, -12801.44) * mm});
            skLineSegment(sketch, "E1472", {"start": v(2626.38, -13358.25) * mm, "end": v(2629.34, -12801.44) * mm});
            skLineSegment(sketch, "E1473", {"start": v(2666.39, -13357.75) * mm, "end": v(2669.33, -12801.65) * mm});
            skArc(sketch, "E1474", {"start": v(2738.77, -13255.22) * mm, "mid": v(2728.82, -13260.41) * mm, "end": v(2722.97, -13269.99) * mm});
            skLineSegment(sketch, "E1475", {"start": v(2722.96, -13269.99) * mm, "end": v(2719.14, -13283.38) * mm});
            skLineSegment(sketch, "E1476", {"start": v(3340.44, -13126.59) * mm, "end": v(2738.77, -13255.22) * mm});
            skArc(sketch, "E1477", {"start": v(2717.8, -13216.62) * mm, "mid": v(2697.84, -13227) * mm, "end": v(2686.09, -13246.18) * mm});
            skLineSegment(sketch, "E1478", {"start": v(2686.09, -13246.18) * mm, "end": v(2678.75, -13271.84) * mm});
            skLineSegment(sketch, "E1479", {"start": v(3334.44, -13086.59) * mm, "end": v(2717.8, -13216.62) * mm});
            skLineSegment(sketch, "E1480", {"start": v(2719.14, -13283.38) * mm, "end": v(2678.75, -13271.84) * mm});
            skArc(sketch, "E1481", {"start": v(3420.97, -13119.82) * mm, "mid": v(3448.37, -13106.4) * mm, "end": v(3459.45, -13077.98) * mm});
            skLineSegment(sketch, "E1482", {"start": v(3420.97, -13119.82) * mm, "end": v(3340.44, -13126.59) * mm});
            skArc(sketch, "E1483", {"start": v(3399.93, -13081.96) * mm, "mid": v(3413.8, -13075.33) * mm, "end": v(3419.45, -13061.02) * mm});
            skLineSegment(sketch, "E1484", {"start": v(3399.93, -13081.96) * mm, "end": v(3334.44, -13086.59) * mm});
            skArc(sketch, "E1485", {"start": v(3460.43, -10270.12) * mm, "mid": v(3440.18, -10250.64) * mm, "end": v(3420.43, -10270.64) * mm});
            skLineSegment(sketch, "E1486", {"start": v(3460.43, -10270.12) * mm, "end": v(3459.45, -13077.98) * mm});
            skLineSegment(sketch, "E1487", {"start": v(3420.43, -10270.64) * mm, "end": v(3419.45, -13061.02) * mm});
            skLineSegment(sketch, "E1488", {"start": v(3288.44, -10516.59) * mm, "end": v(3308.44, -10516.59) * mm});
            skLineSegment(sketch, "E1489", {"start": v(3295.33, -13227.3) * mm, "end": v(4218.44, -13237.59) * mm});
            skLineSegment(sketch, "E1490", {"start": v(3275.28, -13247.16) * mm, "end": v(4218.44, -13257.59) * mm});
            skLineSegment(sketch, "E1491", {"start": v(3295.77, -13136.14) * mm, "end": v(3295.33, -13227.3) * mm});
            skLineSegment(sketch, "E1492", {"start": v(3308.44, -10516.59) * mm, "end": v(3295.97, -13094.7) * mm});
            skLineSegment(sketch, "E1493", {"start": v(3275.8, -13140.4) * mm, "end": v(3275.28, -13247.16) * mm});
            skLineSegment(sketch, "E1494", {"start": v(3288.44, -10516.59) * mm, "end": v(3276, -13098.91) * mm});
            skLineSegment(sketch, "E1495", {"start": v(2236.93, -12802.59) * mm, "end": v(2236.93, -12812.59) * mm});
            skCircle(sketch, "E1496", {"center": v(4826.04, -11091.87) * mm, "radius": 32.63 * mm});
            skCircle(sketch, "E1497", {"center": v(194.44, -13279.59) * mm, "radius": 32.63 * mm});
            skCircle(sketch, "E1498", {"center": v(6361.44, -13268.59) * mm, "radius": 32.63 * mm});
            skLineSegment(sketch, "E1499", {"start": v(-1817.56, -12788.59) * mm, "end": v(-1817.56, -12812.59) * mm});
            skLineSegment(sketch, "E1500", {"start": v(94.37, -12788.59) * mm, "end": v(-1754.56, -12788.59) * mm});
            skLineSegment(sketch, "E1501", {"start": v(2135.9, -12788.59) * mm, "end": v(297.47, -12788.59) * mm});
            skLineSegment(sketch, "E1502", {"start": v(2236.93, -12812.59) * mm, "end": v(206.44, -12812.59) * mm});
            skLineSegment(sketch, "E1503", {"start": v(182.44, -12812.59) * mm, "end": v(-1817.56, -12812.59) * mm});
            skLineSegment(sketch, "E1504", {"start": v(206.44, -13249.24) * mm, "end": v(206.44, -12812.59) * mm});
            skLineSegment(sketch, "E1505", {"start": v(182.44, -13249.24) * mm, "end": v(182.44, -12812.59) * mm});
            skLineSegment(sketch, "E1506", {"start": v(6373.57, -13238.3) * mm, "end": v(6375.5, -12805.59) * mm});
            skLineSegment(sketch, "E1507", {"start": v(6349.58, -13238.2) * mm, "end": v(6351.5, -12805.59) * mm});
            skLineSegment(sketch, "E1508", {"start": v(2681.24, -13263.15) * mm, "end": v(2666.89, -13263.18) * mm});
            skLineSegment(sketch, "E1509", {"start": v(2626.76, -13287.25) * mm, "end": v(224.8, -13291.53) * mm});
            skLineSegment(sketch, "E1510", {"start": v(2626.89, -13263.25) * mm, "end": v(224.76, -13267.53) * mm});
            skLineSegment(sketch, "E1511", {"start": v(1481.44, -13174.59) * mm, "end": v(1481.44, -13156.59) * mm});
            skLineSegment(sketch, "E1512", {"start": v(1481.44, -13156.59) * mm, "end": v(2627.45, -13156.59) * mm});
            skLineSegment(sketch, "E1513", {"start": v(1481.44, -13174.59) * mm, "end": v(2627.36, -13174.59) * mm});
            skLineSegment(sketch, "E1514", {"start": v(2667.45, -13156.59) * mm, "end": v(3002.5, -13156.59) * mm});
            skLineSegment(sketch, "E1515", {"start": v(2667.36, -13174.59) * mm, "end": v(2917.15, -13174.59) * mm});
            skLineSegment(sketch, "E1516", {"start": v(3115.92, -13174.59) * mm, "end": v(3275.58, -13174.59) * mm});
            skLineSegment(sketch, "E1517", {"start": v(3200.12, -13156.59) * mm, "end": v(3275.58, -13156.59) * mm});
            skLineSegment(sketch, "E1518", {"start": v(5049.44, -12541.59) * mm, "end": v(4970.44, -12541.59) * mm});
            skLineSegment(sketch, "E1519", {"start": v(4970.44, -12541.59) * mm, "end": v(4970.44, -12640.59) * mm});
            skLineSegment(sketch, "E1520", {"start": v(4970.44, -12640.59) * mm, "end": v(5049.44, -12640.59) * mm});
            skLineSegment(sketch, "E1521", {"start": v(5049.44, -12640.59) * mm, "end": v(5049.44, -12541.59) * mm});
            skCircle(sketch, "E1522", {"center": v(5022.44, -12766.59) * mm, "radius": 32.63 * mm});
            skCircle(sketch, "E1523", {"center": v(4822.44, -12768.59) * mm, "radius": 32.63 * mm});
            skLineSegment(sketch, "E1524", {"start": v(5073.44, -13028.59) * mm, "end": v(5460.44, -13028.59) * mm});
            skLineSegment(sketch, "E1525", {"start": v(5460.44, -13028.59) * mm, "end": v(5460.44, -12536.59) * mm});
            skLineSegment(sketch, "E1526", {"start": v(5460.44, -12536.59) * mm, "end": v(5073.44, -12536.59) * mm});
            skLineSegment(sketch, "E1527", {"start": v(5073.44, -12536.59) * mm, "end": v(5073.44, -13028.59) * mm});
            skLineSegment(sketch, "E1528", {"start": v(5140.07, -13326.49) * mm, "end": v(5124.39, -13028.59) * mm});
            skLineSegment(sketch, "E1529", {"start": v(5107.14, -13326.9) * mm, "end": v(5091.44, -13028.59) * mm});
            skArc(sketch, "E1530", {"start": v(5050.28, -13258.92) * mm, "mid": v(5019.38, -13236.96) * mm, "end": v(4988.57, -13259.03) * mm});
            skArc(sketch, "E1531", {"start": v(4989.71, -13283.03) * mm, "mid": v(5019.5, -13302.21) * mm, "end": v(5049.22, -13282.93) * mm});
            skLineSegment(sketch, "E1532", {"start": v(4218.44, -13257.59) * mm, "end": v(4991.13, -13253.36) * mm});
            skLineSegment(sketch, "E1533", {"start": v(6331.12, -13280.64) * mm, "end": v(5137.77, -13282.77) * mm});
            skLineSegment(sketch, "E1534", {"start": v(6331.08, -13256.64) * mm, "end": v(5136.5, -13258.77) * mm});
            skLineSegment(sketch, "E1535", {"start": v(5136.18, -13252.57) * mm, "end": v(5423.45, -13251) * mm});
            skLineSegment(sketch, "E1536", {"start": v(5135.13, -13232.62) * mm, "end": v(5403.75, -13231.16) * mm});
            skLineSegment(sketch, "E1537", {"start": v(5047.57, -13253.05) * mm, "end": v(5103.24, -13252.75) * mm});
            skLineSegment(sketch, "E1538", {"start": v(5103.56, -13258.83) * mm, "end": v(2726.42, -13263.07) * mm});
            skLineSegment(sketch, "E1539", {"start": v(5104.82, -13282.83) * mm, "end": v(2666.76, -13287.18) * mm});
            skLineSegment(sketch, "E1540", {"start": v(5403.75, -13231.16) * mm, "end": v(5407.91, -13028.59) * mm});
            skLineSegment(sketch, "E1541", {"start": v(5423.45, -13251) * mm, "end": v(5427.9, -13028.59) * mm});
            skLineSegment(sketch, "E1542", {"start": v(4938.44, -11411.59) * mm, "end": v(4691.44, -11411.59) * mm});
            skLineSegment(sketch, "E1543", {"start": v(4895.44, -11398.59) * mm, "end": v(4734.44, -11398.59) * mm});
            skLineSegment(sketch, "E1544", {"start": v(4859.44, -11232.14) * mm, "end": v(4859.44, -11290.59) * mm});
            skLineSegment(sketch, "E1545", {"start": v(4770.44, -11232.14) * mm, "end": v(4770.44, -11290.59) * mm});
            skLineSegment(sketch, "E1546", {"start": v(4809.94, -11124.59) * mm, "end": v(4819.94, -11124.59) * mm});
            skLineSegment(sketch, "E1547", {"start": v(4819.94, -11124.59) * mm, "end": v(4819.94, -11197.59) * mm});
            skLineSegment(sketch, "E1548", {"start": v(4819.94, -11197.59) * mm, "end": v(4809.94, -11197.59) * mm});
            skLineSegment(sketch, "E1549", {"start": v(4809.94, -11197.59) * mm, "end": v(4809.94, -11124.59) * mm});
            skLineSegment(sketch, "E1550", {"start": v(4892.44, -11365.59) * mm, "end": v(4895.44, -11398.59) * mm});
            skLineSegment(sketch, "E1551", {"start": v(4895.44, -11398.59) * mm, "end": v(4938.44, -11411.59) * mm});
            skLineSegment(sketch, "E1552", {"start": v(4938.44, -11411.59) * mm, "end": v(4938.44, -11417.59) * mm});
            skLineSegment(sketch, "E1553", {"start": v(4938.44, -11417.59) * mm, "end": v(4691.44, -11417.59) * mm});
            skLineSegment(sketch, "E1554", {"start": v(4691.44, -11417.59) * mm, "end": v(4691.44, -11411.59) * mm});
            skLineSegment(sketch, "E1555", {"start": v(4691.44, -11411.59) * mm, "end": v(4734.44, -11398.59) * mm});
            skLineSegment(sketch, "E1556", {"start": v(4734.44, -11398.59) * mm, "end": v(4737.44, -11365.59) * mm});
            skLineSegment(sketch, "E1557", {"start": v(4737.44, -11365.59) * mm, "end": v(4892.44, -11365.59) * mm});
            skLineSegment(sketch, "E1558", {"start": v(4863.89, -11417.59) * mm, "end": v(4863.37, -11420.35) * mm});
            skLineSegment(sketch, "E1559", {"start": v(4863.37, -11420.35) * mm, "end": v(4862.84, -11423.1) * mm});
            skLineSegment(sketch, "E1560", {"start": v(4862.84, -11423.1) * mm, "end": v(4862.3, -11425.85) * mm});
            skLineSegment(sketch, "E1561", {"start": v(4862.3, -11425.85) * mm, "end": v(4861.75, -11428.59) * mm});
            skLineSegment(sketch, "E1562", {"start": v(4861.75, -11428.59) * mm, "end": v(4861.18, -11431.31) * mm});
            skLineSegment(sketch, "E1563", {"start": v(4861.18, -11431.31) * mm, "end": v(4860.58, -11434.02) * mm});
            skLineSegment(sketch, "E1564", {"start": v(4860.58, -11434.02) * mm, "end": v(4859.96, -11436.7) * mm});
            skLineSegment(sketch, "E1565", {"start": v(4859.96, -11436.7) * mm, "end": v(4859.3, -11439.37) * mm});
            skLineSegment(sketch, "E1566", {"start": v(4859.3, -11439.37) * mm, "end": v(4858.59, -11442) * mm});
            skLineSegment(sketch, "E1567", {"start": v(4858.59, -11442) * mm, "end": v(4857.84, -11444.6) * mm});
            skLineSegment(sketch, "E1568", {"start": v(4857.84, -11444.6) * mm, "end": v(4857.04, -11447.18) * mm});
            skLineSegment(sketch, "E1569", {"start": v(4857.04, -11447.18) * mm, "end": v(4856.19, -11449.7) * mm});
            skLineSegment(sketch, "E1570", {"start": v(4856.19, -11449.7) * mm, "end": v(4855.27, -11452.2) * mm});
            skLineSegment(sketch, "E1571", {"start": v(4855.27, -11452.2) * mm, "end": v(4854.29, -11454.64) * mm});
            skLineSegment(sketch, "E1572", {"start": v(4854.29, -11454.64) * mm, "end": v(4853.24, -11457.03) * mm});
            skLineSegment(sketch, "E1573", {"start": v(4853.24, -11457.03) * mm, "end": v(4852.1, -11459.38) * mm});
            skLineSegment(sketch, "E1574", {"start": v(4852.1, -11459.38) * mm, "end": v(4850.9, -11461.66) * mm});
            skLineSegment(sketch, "E1575", {"start": v(4850.9, -11461.66) * mm, "end": v(4849.6, -11463.9) * mm});
            skLineSegment(sketch, "E1576", {"start": v(4849.6, -11463.9) * mm, "end": v(4848.22, -11466.06) * mm});
            skLineSegment(sketch, "E1577", {"start": v(4848.22, -11466.06) * mm, "end": v(4846.74, -11468.16) * mm});
            skLineSegment(sketch, "E1578", {"start": v(4846.74, -11468.16) * mm, "end": v(4845.1, -11470.25) * mm});
            skLineSegment(sketch, "E1579", {"start": v(4845.1, -11470.25) * mm, "end": v(4843.37, -11472.28) * mm});
            skLineSegment(sketch, "E1580", {"start": v(4843.37, -11472.28) * mm, "end": v(4841.54, -11474.24) * mm});
            skLineSegment(sketch, "E1581", {"start": v(4841.54, -11474.24) * mm, "end": v(4839.63, -11476.15) * mm});
            skLineSegment(sketch, "E1582", {"start": v(4839.63, -11476.15) * mm, "end": v(4837.64, -11478) * mm});
            skLineSegment(sketch, "E1583", {"start": v(4837.64, -11478) * mm, "end": v(4835.57, -11479.8) * mm});
            skLineSegment(sketch, "E1584", {"start": v(4835.57, -11479.8) * mm, "end": v(4833.44, -11481.55) * mm});
            skLineSegment(sketch, "E1585", {"start": v(4833.44, -11481.55) * mm, "end": v(4831.25, -11483.27) * mm});
            skLineSegment(sketch, "E1586", {"start": v(4831.25, -11483.27) * mm, "end": v(4829.02, -11484.95) * mm});
            skLineSegment(sketch, "E1587", {"start": v(4829.02, -11484.95) * mm, "end": v(4826.74, -11486.6) * mm});
            skLineSegment(sketch, "E1588", {"start": v(4826.74, -11486.6) * mm, "end": v(4824.42, -11488.23) * mm});
            skLineSegment(sketch, "E1589", {"start": v(4824.42, -11488.23) * mm, "end": v(4822.08, -11489.83) * mm});
            skLineSegment(sketch, "E1590", {"start": v(4822.08, -11489.83) * mm, "end": v(4819.7, -11491.43) * mm});
            skLineSegment(sketch, "E1591", {"start": v(4819.7, -11491.43) * mm, "end": v(4817.33, -11493) * mm});
            skLineSegment(sketch, "E1592", {"start": v(4817.33, -11493) * mm, "end": v(4814.94, -11494.59) * mm});
            skLineSegment(sketch, "E1593", {"start": v(4814.94, -11494.59) * mm, "end": v(4812.55, -11493) * mm});
            skLineSegment(sketch, "E1594", {"start": v(4812.55, -11493) * mm, "end": v(4810.17, -11491.43) * mm});
            skLineSegment(sketch, "E1595", {"start": v(4810.17, -11491.43) * mm, "end": v(4807.8, -11489.83) * mm});
            skLineSegment(sketch, "E1596", {"start": v(4807.8, -11489.83) * mm, "end": v(4805.46, -11488.23) * mm});
            skLineSegment(sketch, "E1597", {"start": v(4805.46, -11488.23) * mm, "end": v(4803.14, -11486.6) * mm});
            skLineSegment(sketch, "E1598", {"start": v(4803.14, -11486.6) * mm, "end": v(4800.86, -11484.95) * mm});
            skLineSegment(sketch, "E1599", {"start": v(4800.86, -11484.95) * mm, "end": v(4798.63, -11483.27) * mm});
            skLineSegment(sketch, "E1600", {"start": v(4798.63, -11483.27) * mm, "end": v(4796.44, -11481.55) * mm});
            skLineSegment(sketch, "E1601", {"start": v(4796.44, -11481.55) * mm, "end": v(4794.31, -11479.8) * mm});
            skLineSegment(sketch, "E1602", {"start": v(4794.31, -11479.8) * mm, "end": v(4792.25, -11478) * mm});
            skLineSegment(sketch, "E1603", {"start": v(4792.25, -11478) * mm, "end": v(4790.25, -11476.15) * mm});
            skLineSegment(sketch, "E1604", {"start": v(4790.25, -11476.15) * mm, "end": v(4788.34, -11474.24) * mm});
            skLineSegment(sketch, "E1605", {"start": v(4788.34, -11474.24) * mm, "end": v(4786.51, -11472.28) * mm});
            skLineSegment(sketch, "E1606", {"start": v(4786.51, -11472.28) * mm, "end": v(4784.78, -11470.25) * mm});
            skLineSegment(sketch, "E1607", {"start": v(4784.78, -11470.25) * mm, "end": v(4783.14, -11468.16) * mm});
            skLineSegment(sketch, "E1608", {"start": v(4783.14, -11468.16) * mm, "end": v(4781.66, -11466.06) * mm});
            skLineSegment(sketch, "E1609", {"start": v(4781.66, -11466.06) * mm, "end": v(4780.28, -11463.9) * mm});
            skLineSegment(sketch, "E1610", {"start": v(4780.28, -11463.9) * mm, "end": v(4778.98, -11461.66) * mm});
            skLineSegment(sketch, "E1611", {"start": v(4778.98, -11461.66) * mm, "end": v(4777.77, -11459.38) * mm});
            skLineSegment(sketch, "E1612", {"start": v(4777.77, -11459.38) * mm, "end": v(4776.64, -11457.03) * mm});
            skLineSegment(sketch, "E1613", {"start": v(4776.64, -11457.03) * mm, "end": v(4775.6, -11454.64) * mm});
            skLineSegment(sketch, "E1614", {"start": v(4775.6, -11454.64) * mm, "end": v(4774.6, -11452.2) * mm});
            skLineSegment(sketch, "E1615", {"start": v(4774.6, -11452.2) * mm, "end": v(4773.7, -11449.7) * mm});
            skLineSegment(sketch, "E1616", {"start": v(4773.7, -11449.7) * mm, "end": v(4772.84, -11447.18) * mm});
            skLineSegment(sketch, "E1617", {"start": v(4772.84, -11447.18) * mm, "end": v(4772.04, -11444.6) * mm});
            skLineSegment(sketch, "E1618", {"start": v(4772.04, -11444.6) * mm, "end": v(4771.3, -11442) * mm});
            skLineSegment(sketch, "E1619", {"start": v(4771.3, -11442) * mm, "end": v(4770.59, -11439.37) * mm});
            skLineSegment(sketch, "E1620", {"start": v(4770.59, -11439.37) * mm, "end": v(4769.92, -11436.7) * mm});
            skLineSegment(sketch, "E1621", {"start": v(4769.92, -11436.7) * mm, "end": v(4769.3, -11434.02) * mm});
            skLineSegment(sketch, "E1622", {"start": v(4769.3, -11434.02) * mm, "end": v(4768.7, -11431.31) * mm});
            skLineSegment(sketch, "E1623", {"start": v(4768.7, -11431.31) * mm, "end": v(4768.13, -11428.59) * mm});
            skLineSegment(sketch, "E1624", {"start": v(4768.13, -11428.59) * mm, "end": v(4767.58, -11425.85) * mm});
            skLineSegment(sketch, "E1625", {"start": v(4767.58, -11425.85) * mm, "end": v(4767.04, -11423.1) * mm});
            skLineSegment(sketch, "E1626", {"start": v(4767.04, -11423.1) * mm, "end": v(4766.51, -11420.35) * mm});
            skLineSegment(sketch, "E1627", {"start": v(4766.51, -11420.35) * mm, "end": v(4766, -11417.59) * mm});
            skLineSegment(sketch, "E1628", {"start": v(4883.44, -11365.59) * mm, "end": v(4882.44, -11314.59) * mm});
            skLineSegment(sketch, "E1629", {"start": v(4882.44, -11314.59) * mm, "end": v(4882.3, -11311.1) * mm});
            skLineSegment(sketch, "E1630", {"start": v(4882.3, -11311.1) * mm, "end": v(4882.07, -11307.7) * mm});
            skLineSegment(sketch, "E1631", {"start": v(4882.07, -11307.7) * mm, "end": v(4881.66, -11304.46) * mm});
            skLineSegment(sketch, "E1632", {"start": v(4881.66, -11304.46) * mm, "end": v(4880.98, -11301.48) * mm});
            skLineSegment(sketch, "E1633", {"start": v(4880.98, -11301.48) * mm, "end": v(4879.94, -11298.82) * mm});
            skLineSegment(sketch, "E1634", {"start": v(4879.94, -11298.82) * mm, "end": v(4878.44, -11296.59) * mm});
            skLineSegment(sketch, "E1635", {"start": v(4878.44, -11296.59) * mm, "end": v(4876.6, -11294.93) * mm});
            skLineSegment(sketch, "E1636", {"start": v(4876.6, -11294.93) * mm, "end": v(4874.34, -11293.65) * mm});
            skLineSegment(sketch, "E1637", {"start": v(4874.34, -11293.65) * mm, "end": v(4871.76, -11292.67) * mm});
            skLineSegment(sketch, "E1638", {"start": v(4871.76, -11292.67) * mm, "end": v(4868.92, -11291.93) * mm});
            skLineSegment(sketch, "E1639", {"start": v(4868.92, -11291.93) * mm, "end": v(4865.87, -11291.38) * mm});
            skLineSegment(sketch, "E1640", {"start": v(4865.87, -11291.38) * mm, "end": v(4862.69, -11290.95) * mm});
            skLineSegment(sketch, "E1641", {"start": v(4862.69, -11290.95) * mm, "end": v(4859.44, -11290.59) * mm});
            skLineSegment(sketch, "E1642", {"start": v(4859.44, -11290.59) * mm, "end": v(4770.44, -11290.59) * mm});
            skLineSegment(sketch, "E1643", {"start": v(4770.44, -11290.59) * mm, "end": v(4767.6, -11290.9) * mm});
            skLineSegment(sketch, "E1644", {"start": v(4767.6, -11290.9) * mm, "end": v(4764.8, -11291.27) * mm});
            skLineSegment(sketch, "E1645", {"start": v(4764.8, -11291.27) * mm, "end": v(4762.09, -11291.7) * mm});
            skLineSegment(sketch, "E1646", {"start": v(4762.09, -11291.7) * mm, "end": v(4759.51, -11292.28) * mm});
            skLineSegment(sketch, "E1647", {"start": v(4759.51, -11292.28) * mm, "end": v(4757.11, -11293) * mm});
            skLineSegment(sketch, "E1648", {"start": v(4757.11, -11293) * mm, "end": v(4754.94, -11293.94) * mm});
            skLineSegment(sketch, "E1649", {"start": v(4754.94, -11293.94) * mm, "end": v(4753.03, -11295.12) * mm});
            skLineSegment(sketch, "E1650", {"start": v(4753.03, -11295.12) * mm, "end": v(4751.44, -11296.59) * mm});
            skLineSegment(sketch, "E1651", {"start": v(4751.44, -11296.59) * mm, "end": v(4750.27, -11298.22) * mm});
            skLineSegment(sketch, "E1652", {"start": v(4750.27, -11298.22) * mm, "end": v(4749.37, -11300.1) * mm});
            skLineSegment(sketch, "E1653", {"start": v(4749.37, -11300.1) * mm, "end": v(4748.7, -11302.2) * mm});
            skLineSegment(sketch, "E1654", {"start": v(4748.7, -11302.2) * mm, "end": v(4748.22, -11304.46) * mm});
            skLineSegment(sketch, "E1655", {"start": v(4748.22, -11304.46) * mm, "end": v(4747.89, -11306.87) * mm});
            skLineSegment(sketch, "E1656", {"start": v(4747.89, -11306.87) * mm, "end": v(4747.67, -11309.38) * mm});
            skLineSegment(sketch, "E1657", {"start": v(4747.67, -11309.38) * mm, "end": v(4747.54, -11311.97) * mm});
            skLineSegment(sketch, "E1658", {"start": v(4747.54, -11311.97) * mm, "end": v(4747.44, -11314.59) * mm});
            skLineSegment(sketch, "E1659", {"start": v(4747.44, -11314.59) * mm, "end": v(4746.44, -11365.59) * mm});
            skLineSegment(sketch, "E1660", {"start": v(4873.44, -11219.59) * mm, "end": v(4851.44, -11197.59) * mm});
            skLineSegment(sketch, "E1661", {"start": v(4851.44, -11197.59) * mm, "end": v(4778.44, -11197.59) * mm});
            skLineSegment(sketch, "E1662", {"start": v(4778.44, -11197.59) * mm, "end": v(4756.44, -11219.59) * mm});
            skLineSegment(sketch, "E1663", {"start": v(4756.44, -11219.59) * mm, "end": v(4873.44, -11219.59) * mm});
            skLineSegment(sketch, "E1664", {"start": v(4873.44, -11219.59) * mm, "end": v(4873.44, -11232.14) * mm});
            skLineSegment(sketch, "E1665", {"start": v(4873.44, -11232.14) * mm, "end": v(4756.44, -11232.14) * mm});
            skLineSegment(sketch, "E1666", {"start": v(4756.44, -11232.14) * mm, "end": v(4756.44, -11219.59) * mm});
            skLineSegment(sketch, "E1667", {"start": v(4854.38, -12775.27) * mm, "end": v(4990.64, -12773.9) * mm});
            skLineSegment(sketch, "E1668", {"start": v(4854.24, -12761.27) * mm, "end": v(4990.5, -12759.9) * mm});
            skLineSegment(sketch, "E1669", {"start": v(5029.25, -12798.5) * mm, "end": v(5026.63, -13237.76) * mm});
            skLineSegment(sketch, "E1670", {"start": v(5015.25, -12798.41) * mm, "end": v(5012.63, -13237.68) * mm});
            skLineSegment(sketch, "E1671", {"start": v(4218.44, -13237.59) * mm, "end": v(5012.66, -13233.28) * mm});
            skLineSegment(sketch, "E1672", {"start": v(5026.66, -13233.2) * mm, "end": v(5102.19, -13232.8) * mm});
            skLineSegment(sketch, "E1673", {"start": v(4830.45, -11124.2) * mm, "end": v(4830.4, -11197.59) * mm});
            skLineSegment(sketch, "E1674", {"start": v(4830.23, -11484.04) * mm, "end": v(4829.46, -12736.72) * mm});
            skLineSegment(sketch, "E1675", {"start": v(4816.45, -11123.05) * mm, "end": v(4816.45, -11124.59) * mm});
            skLineSegment(sketch, "E1676", {"start": v(4816.23, -11493.74) * mm, "end": v(4815.46, -12736.71) * mm});
            skLineSegment(sketch, "E1677", {"start": v(-3796.56, -9643.59) * mm, "end": v(-1942.56, -9664.59) * mm});
            skLineSegment(sketch, "E1678", {"start": v(-1942.56, -9664.59) * mm, "end": v(-538.56, -9691.59) * mm});
            skLineSegment(sketch, "E1679", {"start": v(-538.56, -9691.59) * mm, "end": v(432.44, -9709.59) * mm});
            skLineSegment(sketch, "E1680", {"start": v(432.44, -9709.59) * mm, "end": v(786.44, -9660.86) * mm});
            skLineSegment(sketch, "E1681", {"start": v(-11068.6, 12498.41) * mm, "end": v(-11060.05, 10588.37) * mm});
            skLineSegment(sketch, "E1682", {"start": v(-10720.25, 10588.37) * mm, "end": v(-11060.05, 10588.37) * mm});
            skLineSegment(sketch, "E1683", {"start": v(-10375.97, 10588.37) * mm, "end": v(-10634.64, 10588.37) * mm});
            skLineSegment(sketch, "E1684", {"start": v(-10375.97, 10588.37) * mm, "end": v(-10369.12, 12498.41) * mm});
            skLineSegment(sketch, "E1685", {"start": v(786.44, -9660.86) * mm, "end": v(786.44, -7751.59) * mm});
            skLineSegment(sketch, "E1686", {"start": v(755.44, -7696.59) * mm, "end": v(755.44, -7751.59) * mm});
            skLineSegment(sketch, "E1687", {"start": v(755.44, -7751.59) * mm, "end": v(1511.42, -7757.63) * mm});
            skLineSegment(sketch, "E1688", {"start": v(1511.42, -7757.63) * mm, "end": v(1511.86, -7702.64) * mm});
            skLineSegment(sketch, "E1689", {"start": v(755.44, -7696.59) * mm, "end": v(1511.86, -7702.64) * mm});
            skLineSegment(sketch, "E1690", {"start": v(1485.4, -9351.99) * mm, "end": v(1481.31, -7757.4) * mm});
            skLineSegment(sketch, "E1691", {"start": v(1290.44, -7320.59) * mm, "end": v(986.44, -7320.59) * mm});
            skLineSegment(sketch, "E1692", {"start": v(1290.44, -7700.87) * mm, "end": v(1290.44, -7320.59) * mm});
            skLineSegment(sketch, "E1693", {"start": v(986.44, -7320.59) * mm, "end": v(986.44, -7698.43) * mm});
            skLineSegment(sketch, "E1694", {"start": v(18932.44, -8839.59) * mm, "end": v(21895.44, -8839.59) * mm});
            skLineSegment(sketch, "E1695", {"start": v(18932.44, -9051.59) * mm, "end": v(21895.44, -9051.59) * mm});
            skLineSegment(sketch, "E1696", {"start": v(18932.44, -8839.59) * mm, "end": v(18932.44, -9051.59) * mm});
            skLineSegment(sketch, "E1697", {"start": v(20041.44, -8762.59) * mm, "end": v(20125.44, -8762.59) * mm});
            skLineSegment(sketch, "E1698", {"start": v(20041.44, -8800.59) * mm, "end": v(20040.44, -8762.59) * mm});
            skLineSegment(sketch, "E1699", {"start": v(20041.44, -8800.59) * mm, "end": v(21895.44, -8800.59) * mm});
            skLineSegment(sketch, "E1700", {"start": v(21895.44, -8800.59) * mm, "end": v(21896.44, -8762.59) * mm});
            skLineSegment(sketch, "E1701", {"start": v(21896.44, -8762.59) * mm, "end": v(20125.44, -8762.59) * mm});
            skLineSegment(sketch, "E1702", {"start": v(20104.44, -10272.59) * mm, "end": v(21812.44, -10272.59) * mm});
            skLineSegment(sketch, "E1703", {"start": v(21812.44, -10272.59) * mm, "end": v(21812.44, -10802.59) * mm});
            skLineSegment(sketch, "E1704", {"start": v(20104.44, -10802.59) * mm, "end": v(20104.44, -10272.59) * mm});
            skLineSegment(sketch, "E1705", {"start": v(18954.03, -12622.59) * mm, "end": v(18954.03, -9051.59) * mm});
            skLineSegment(sketch, "E1706", {"start": v(22113.03, -12622.59) * mm, "end": v(18954.03, -12622.59) * mm});
            skLineSegment(sketch, "E1707", {"start": v(21925.27, -7707.65) * mm, "end": v(18577.56, -7707.65) * mm});
            skLineSegment(sketch, "E1708", {"start": v(21811.44, -7707.65) * mm, "end": v(21811.44, -8762.59) * mm});
            skLineSegment(sketch, "E1709", {"start": v(20125.44, -8762.59) * mm, "end": v(20125.44, -7707.65) * mm});
            skLineSegment(sketch, "E1710", {"start": v(18954.03, -8839.59) * mm, "end": v(18954.03, -7707.65) * mm});
            skLineSegment(sketch, "E1711", {"start": v(21925.27, -7592.59) * mm, "end": v(18452.44, -7592.59) * mm});
            skArc(sketch, "E1712", {"start": v(18734.44, -7533.58) * mm, "mid": v(18661.9, -7448.48) * mm, "end": v(18550.44, -7439.58) * mm});
            skLineSegment(sketch, "E1713", {"start": v(18550.44, -7439.59) * mm, "end": v(20022.44, -6264.59) * mm});
            skLineSegment(sketch, "E1714", {"start": v(20022.44, -6264.59) * mm, "end": v(21485.44, -5046.59) * mm});
            skLineSegment(sketch, "E1715", {"start": v(21925.37, -7539.97) * mm, "end": v(18550.25, -7533.22) * mm});
            skLineSegment(sketch, "E1716", {"start": v(18550.44, -7439.59) * mm, "end": v(18550.25, -7533.22) * mm});
            skLineSegment(sketch, "E1717", {"start": v(18576.77, -7533.27) * mm, "end": v(18577.04, -7592.59) * mm});
            skLineSegment(sketch, "E1718", {"start": v(18577.27, -7643.59) * mm, "end": v(18577.56, -7707.65) * mm});
            skLineSegment(sketch, "E1719", {"start": v(20139.88, -6411.71) * mm, "end": v(21658.23, -5147.64) * mm});
            skLineSegment(sketch, "E1720", {"start": v(18734.44, -7533.59) * mm, "end": v(20139.88, -6411.71) * mm});
            skLineSegment(sketch, "E1721", {"start": v(19413.24, -6172.03) * mm, "end": v(18968.44, -6158.59) * mm});
            skLineSegment(sketch, "E1722", {"start": v(19395.3, -6765.19) * mm, "end": v(19413.24, -6172.03) * mm});
            skLineSegment(sketch, "E1723", {"start": v(18939.09, -7129.35) * mm, "end": v(18968.44, -6158.59) * mm});
            skLineSegment(sketch, "E1724", {"start": v(18968.44, -6158.59) * mm, "end": v(19074.44, -6089.59) * mm});
            skLineSegment(sketch, "E1725", {"start": v(19413.24, -6172.03) * mm, "end": v(19296.91, -6096.31) * mm});
            skLineSegment(sketch, "E1726", {"start": v(19296.91, -6096.31) * mm, "end": v(19074.44, -6089.59) * mm});
            skLineSegment(sketch, "E1727", {"start": v(19054.85, -6102.34) * mm, "end": v(19060.44, -5849.59) * mm});
            skLineSegment(sketch, "E1728", {"start": v(19337.7, -5857.97) * mm, "end": v(19060.44, -5849.59) * mm});
            skLineSegment(sketch, "E1729", {"start": v(19329.84, -6117.75) * mm, "end": v(19337.7, -5857.97) * mm});
            skLineSegment(sketch, "E1730", {"start": v(21443.8, -4384.07) * mm, "end": v(19108.44, -4341.59) * mm});
            skLineSegment(sketch, "E1731", {"start": v(21532.69, -4973.93) * mm, "end": v(19110.44, -4950.59) * mm});
            skLineSegment(sketch, "E1732", {"start": v(21532.44, -4999.59) * mm, "end": v(20202.44, -4987.59) * mm});
            skLineSegment(sketch, "E1733", {"start": v(20202.44, -4987.59) * mm, "end": v(19112.44, -4973.59) * mm});
            skLineSegment(sketch, "E1734", {"start": v(19112.44, -4973.59) * mm, "end": v(19110.44, -4950.59) * mm});
            skLineSegment(sketch, "E1735", {"start": v(19110.44, -4950.59) * mm, "end": v(19108.44, -4341.59) * mm});
            skLineSegment(sketch, "E1736", {"start": v(19145.84, -5142.4) * mm, "end": v(21358.1, -5152.6) * mm});
            skLineSegment(sketch, "E1737", {"start": v(19142.44, -5855.59) * mm, "end": v(19146.64, -4974.02) * mm});
            skLineSegment(sketch, "E1738", {"start": v(19108.44, -4341.59) * mm, "end": v(19119.44, -4201.59) * mm});
            skLineSegment(sketch, "E1739", {"start": v(21446.44, -4238.59) * mm, "end": v(19119.44, -4201.59) * mm});
            skLineSegment(sketch, "E1740", {"start": v(8137.05, -11086.71) * mm, "end": v(7750.44, -11078.59) * mm});
            skLineSegment(sketch, "E1741", {"start": v(7750.44, -11078.59) * mm, "end": v(7706.44, -11077.59) * mm});
            skLineSegment(sketch, "E1742", {"start": v(7706.44, -11077.59) * mm, "end": v(7706.44, -10954.37) * mm});
            skLineSegment(sketch, "E1743", {"start": v(7706.44, -10954.37) * mm, "end": v(3216.5, -8801.46) * mm});
            skLineSegment(sketch, "E1744", {"start": v(-23483.72, -10974.59) * mm, "end": v(-23483.72, -11037.55) * mm});
            skLineSegment(sketch, "E1745", {"start": v(-23472.74, -10937.59) * mm, "end": v(-23472.63, -10963.59) * mm});
            skLineSegment(sketch, "E1746", {"start": v(-23417.39, -11037.27) * mm, "end": v(-23416.78, -11086.61) * mm});
            skLineSegment(sketch, "E1747", {"start": v(-23418.3, -10963.2) * mm, "end": v(-23418.16, -10974.32) * mm});
            skLineSegment(sketch, "E1748", {"start": v(-23490.28, -11111.11) * mm, "end": v(-23441.3, -11160.1) * mm});
            skLineSegment(sketch, "E1749", {"start": v(-23441.3, -11160.1) * mm, "end": v(-23417.03, -11086.7) * mm});
            skLineSegment(sketch, "E1750", {"start": v(-23417.03, -11086.7) * mm, "end": v(-23490.28, -11111.11) * mm});
            skLineSegment(sketch, "E1751", {"start": v(8112.55, -11013.21) * mm, "end": v(8063.57, -11062.2) * mm});
            skLineSegment(sketch, "E1752", {"start": v(8063.57, -11062.2) * mm, "end": v(8136.97, -11086.47) * mm});
            skLineSegment(sketch, "E1753", {"start": v(8136.97, -11086.47) * mm, "end": v(8112.55, -11013.21) * mm});
            skLineSegment(sketch, "E1754", {"start": v(7743.44, -13362.84) * mm, "end": v(7813.42, -13362.84) * mm});
            skLineSegment(sketch, "E1755", {"start": v(7813.42, -13362.84) * mm, "end": v(7778.32, -13293.08) * mm});
            skLineSegment(sketch, "E1756", {"start": v(7778.32, -13293.08) * mm, "end": v(7743.44, -13362.84) * mm});
            skLineSegment(sketch, "E1757", {"start": v(-23238.6, -11084.43) * mm, "end": v(-23238.6, -13307.67) * mm});
            skLineSegment(sketch, "E1758", {"start": v(-23263.1, -13219.35) * mm, "end": v(-23312.09, -13268.33) * mm});
            skLineSegment(sketch, "E1759", {"start": v(-23312.09, -13268.33) * mm, "end": v(-23238.69, -13292.6) * mm});
            skLineSegment(sketch, "E1760", {"start": v(-23238.69, -13292.6) * mm, "end": v(-23263.1, -13219.35) * mm});
            skArc(sketch, "E1761", {"start": v(-22933.79, -11432.6) * mm, "mid": v(-22939.4, -11413) * mm, "end": v(-22954.45, -11399.23) * mm});
            skArc(sketch, "E1762", {"start": v(-22858.81, -11409.11) * mm, "mid": v(-22870.05, -11369.9) * mm, "end": v(-22900.14, -11342.38) * mm});
            skArc(sketch, "E1763", {"start": v(-23128.94, -11204.3) * mm, "mid": v(-23123.36, -11223.99) * mm, "end": v(-23108.27, -11237.81) * mm});
            skLineSegment(sketch, "E1764", {"start": v(-23128.94, -11085.4) * mm, "end": v(-23128.94, -11204.3) * mm});
            skLineSegment(sketch, "E1765", {"start": v(-22900.14, -11342.38) * mm, "end": v(-23108.27, -11237.81) * mm});
            skArc(sketch, "E1766", {"start": v(-23203.94, -11227.65) * mm, "mid": v(-23192.77, -11267.02) * mm, "end": v(-23162.6, -11294.67) * mm});
            skLineSegment(sketch, "E1767", {"start": v(-22954.45, -11399.23) * mm, "end": v(-23162.6, -11294.67) * mm});
            skLineSegment(sketch, "E1768", {"start": v(-23203.94, -11089.68) * mm, "end": v(-23203.94, -11227.65) * mm});
            skLineSegment(sketch, "E1769", {"start": v(-23107.72, -11036) * mm, "end": v(-23128.94, -11085.4) * mm});
            skLineSegment(sketch, "E1770", {"start": v(-23483.46, -11037.54) * mm, "end": v(-23226.78, -11036.5) * mm});
            skLineSegment(sketch, "E1771", {"start": v(-23226.78, -11036.5) * mm, "end": v(-23203.94, -11089.68) * mm});
            skLineSegment(sketch, "E1772", {"start": v(-23206.36, -11084.03) * mm, "end": v(-23416.78, -11086.61) * mm});
            skLineSegment(sketch, "E1773", {"start": v(-23503.84, -8523.35) * mm, "end": v(-18858.72, -8551.59) * mm});
            skLineSegment(sketch, "E1774", {"start": v(-18858.72, -8551.59) * mm, "end": v(-13707.04, -8504.84) * mm});
            skLineSegment(sketch, "E1775", {"start": v(-23472.74, -10937.59) * mm, "end": v(-23502.54, -8624.59) * mm});
            skLineSegment(sketch, "E1776", {"start": v(-23502.54, -8624.59) * mm, "end": v(-18858.6, -8652.81) * mm});
            skLineSegment(sketch, "E1777", {"start": v(-18858.6, -8652.81) * mm, "end": v(-13702.72, -8581.59) * mm});
            skLineSegment(sketch, "E1778", {"start": v(-23502.54, -8624.59) * mm, "end": v(-23503.84, -8523.35) * mm});
            skLineSegment(sketch, "E1779", {"start": v(-23502.83, -8601.6) * mm, "end": v(-18858.63, -8629.83) * mm});
            skLineSegment(sketch, "E1780", {"start": v(-18858.63, -8629.83) * mm, "end": v(-13703.45, -8568.59) * mm});
            skLineSegment(sketch, "E1781", {"start": v(-23468.84, -8453.35) * mm, "end": v(-23538.82, -8453.35) * mm});
            skLineSegment(sketch, "E1782", {"start": v(-23538.82, -8453.35) * mm, "end": v(-23503.72, -8523.12) * mm});
            skLineSegment(sketch, "E1783", {"start": v(-23503.72, -8523.12) * mm, "end": v(-23468.84, -8453.35) * mm});
            skLineSegment(sketch, "E1784", {"start": v(-20626.72, -7759.59) * mm, "end": v(-20625.72, -7708.59) * mm});
            skLineSegment(sketch, "E1785", {"start": v(-21381.75, -7757.63) * mm, "end": v(-21382.83, -7702.64) * mm});
            skLineSegment(sketch, "E1786", {"start": v(-21381.75, -7757.63) * mm, "end": v(-20626.72, -7759.59) * mm});
            skLineSegment(sketch, "E1787", {"start": v(-20625.72, -7708.59) * mm, "end": v(-21382.83, -7702.64) * mm});
            skLineSegment(sketch, "E1788", {"start": v(-21164.72, -7320.59) * mm, "end": v(-21164.72, -7702.64) * mm});
            skLineSegment(sketch, "E1789", {"start": v(-20860.72, -7320.59) * mm, "end": v(-21164.72, -7320.59) * mm});
            skLineSegment(sketch, "E1790", {"start": v(-20860.72, -7320.59) * mm, "end": v(-20860.72, -7706.74) * mm});
            skLineSegment(sketch, "E1791", {"start": v(-21352.68, -8536.43) * mm, "end": v(-21353.75, -7757.63) * mm});
            skLineSegment(sketch, "E1792", {"start": v(-20653.68, -8540.67) * mm, "end": v(-20654.75, -7759.51) * mm});
            skLineSegment(sketch, "E1793", {"start": v(-22238.72, -13192.59) * mm, "end": v(-20600.72, -13192.59) * mm});
            skLineSegment(sketch, "E1794", {"start": v(-20600.72, -13192.59) * mm, "end": v(-20600.72, -13218.59) * mm});
            skLineSegment(sketch, "E1795", {"start": v(-20600.72, -13218.59) * mm, "end": v(-22238.72, -13218.59) * mm});
            skLineSegment(sketch, "E1796", {"start": v(-22238.72, -13218.59) * mm, "end": v(-22238.72, -13192.59) * mm});
            skLineSegment(sketch, "E1797", {"start": v(-22199.89, -11071.7) * mm, "end": v(-22199.89, -13192.59) * mm});
            skLineSegment(sketch, "E1798", {"start": v(-20649.69, -11069.55) * mm, "end": v(-20649.69, -13192.59) * mm});
            skLineSegment(sketch, "E1799", {"start": v(-20649.69, -11112.59) * mm, "end": v(-22199.89, -11112.59) * mm});
            skLineSegment(sketch, "E1800", {"start": v(-21989.72, -11218.59) * mm, "end": v(-21592.72, -11218.59) * mm});
            skLineSegment(sketch, "E1801", {"start": v(-21592.72, -11218.59) * mm, "end": v(-21592.72, -11201.59) * mm});
            skLineSegment(sketch, "E1802", {"start": v(-21592.72, -11201.59) * mm, "end": v(-21989.72, -11201.59) * mm});
            skLineSegment(sketch, "E1803", {"start": v(-21989.72, -11201.59) * mm, "end": v(-21989.72, -11218.59) * mm});
            skLineSegment(sketch, "E1804", {"start": v(-21250.72, -11216.59) * mm, "end": v(-20853.72, -11216.59) * mm});
            skLineSegment(sketch, "E1805", {"start": v(-20853.72, -11216.59) * mm, "end": v(-20853.72, -11199.59) * mm});
            skLineSegment(sketch, "E1806", {"start": v(-20853.72, -11199.59) * mm, "end": v(-21250.72, -11199.59) * mm});
            skLineSegment(sketch, "E1807", {"start": v(-21250.72, -11199.59) * mm, "end": v(-21250.72, -11216.59) * mm});
            skLineSegment(sketch, "E1808", {"start": v(-22176.72, -12959.59) * mm, "end": v(-22082.72, -12959.59) * mm});
            skLineSegment(sketch, "E1809", {"start": v(-22082.72, -12959.59) * mm, "end": v(-22082.72, -13000.59) * mm});
            skLineSegment(sketch, "E1810", {"start": v(-22082.72, -13000.59) * mm, "end": v(-22176.72, -13000.59) * mm});
            skLineSegment(sketch, "E1811", {"start": v(-22176.72, -13000.59) * mm, "end": v(-22176.72, -12959.59) * mm});
            skLineSegment(sketch, "E1812", {"start": v(-22175.72, -12167.59) * mm, "end": v(-22081.72, -12167.59) * mm});
            skLineSegment(sketch, "E1813", {"start": v(-22081.72, -12167.59) * mm, "end": v(-22081.72, -12208.59) * mm});
            skLineSegment(sketch, "E1814", {"start": v(-22081.72, -12208.59) * mm, "end": v(-22175.72, -12208.59) * mm});
            skLineSegment(sketch, "E1815", {"start": v(-22175.72, -12208.59) * mm, "end": v(-22175.72, -12167.59) * mm});
            skLineSegment(sketch, "E1816", {"start": v(-22177.72, -11339.59) * mm, "end": v(-22083.72, -11339.59) * mm});
            skLineSegment(sketch, "E1817", {"start": v(-22083.72, -11339.59) * mm, "end": v(-22083.72, -11380.59) * mm});
            skLineSegment(sketch, "E1818", {"start": v(-22083.72, -11380.59) * mm, "end": v(-22177.72, -11380.59) * mm});
            skLineSegment(sketch, "E1819", {"start": v(-22177.72, -11380.59) * mm, "end": v(-22177.72, -11339.59) * mm});
            skLineSegment(sketch, "E1820", {"start": v(-20664.72, -12959.59) * mm, "end": v(-20758.72, -12959.59) * mm});
            skLineSegment(sketch, "E1821", {"start": v(-20758.72, -12959.59) * mm, "end": v(-20758.72, -13000.59) * mm});
            skLineSegment(sketch, "E1822", {"start": v(-20758.72, -13000.59) * mm, "end": v(-20664.72, -13000.59) * mm});
            skLineSegment(sketch, "E1823", {"start": v(-20664.72, -13000.59) * mm, "end": v(-20664.72, -12959.59) * mm});
            skLineSegment(sketch, "E1824", {"start": v(-20665.72, -12167.59) * mm, "end": v(-20759.72, -12167.59) * mm});
            skLineSegment(sketch, "E1825", {"start": v(-20759.72, -12167.59) * mm, "end": v(-20759.72, -12208.59) * mm});
            skLineSegment(sketch, "E1826", {"start": v(-20759.72, -12208.59) * mm, "end": v(-20665.72, -12208.59) * mm});
            skLineSegment(sketch, "E1827", {"start": v(-20665.72, -12208.59) * mm, "end": v(-20665.72, -12167.59) * mm});
            skLineSegment(sketch, "E1828", {"start": v(-20663.72, -11339.59) * mm, "end": v(-20757.72, -11339.59) * mm});
            skLineSegment(sketch, "E1829", {"start": v(-20757.72, -11339.59) * mm, "end": v(-20757.72, -11380.59) * mm});
            skLineSegment(sketch, "E1830", {"start": v(-20757.72, -11380.59) * mm, "end": v(-20663.72, -11380.59) * mm});
            skLineSegment(sketch, "E1831", {"start": v(-20663.72, -11380.59) * mm, "end": v(-20663.72, -11339.59) * mm});
            skLineSegment(sketch, "E1832", {"start": v(-21442.72, -11161.59) * mm, "end": v(-22137.72, -11161.59) * mm});
            skLineSegment(sketch, "E1833", {"start": v(-22137.72, -11161.59) * mm, "end": v(-22137.72, -11339.59) * mm});
            skLineSegment(sketch, "E1834", {"start": v(-21432.72, -11151.59) * mm, "end": v(-22147.72, -11151.59) * mm});
            skLineSegment(sketch, "E1835", {"start": v(-22147.72, -11151.59) * mm, "end": v(-22147.72, -11339.59) * mm});
            skLineSegment(sketch, "E1836", {"start": v(-22137.72, -11380.59) * mm, "end": v(-22137.72, -12167.59) * mm});
            skLineSegment(sketch, "E1837", {"start": v(-22147.72, -11380.59) * mm, "end": v(-22147.72, -12167.59) * mm});
            skLineSegment(sketch, "E1838", {"start": v(-22137.72, -12208.59) * mm, "end": v(-22137.72, -12959.59) * mm});
            skLineSegment(sketch, "E1839", {"start": v(-22147.72, -12208.59) * mm, "end": v(-22147.72, -12959.59) * mm});
            skLineSegment(sketch, "E1840", {"start": v(-22137.72, -13000.59) * mm, "end": v(-22137.72, -13147.59) * mm});
            skLineSegment(sketch, "E1841", {"start": v(-22137.72, -13147.59) * mm, "end": v(-21442.72, -13147.59) * mm});
            skLineSegment(sketch, "E1842", {"start": v(-21442.72, -13147.59) * mm, "end": v(-21442.72, -11161.59) * mm});
            skLineSegment(sketch, "E1843", {"start": v(-22147.72, -13000.59) * mm, "end": v(-22147.72, -13157.59) * mm});
            skLineSegment(sketch, "E1844", {"start": v(-22147.72, -13157.59) * mm, "end": v(-21432.72, -13157.59) * mm});
            skLineSegment(sketch, "E1845", {"start": v(-21432.72, -13157.59) * mm, "end": v(-21432.72, -11151.59) * mm});
            skLineSegment(sketch, "E1846", {"start": v(-20703.72, -11161.59) * mm, "end": v(-21398.72, -11161.59) * mm});
            skLineSegment(sketch, "E1847", {"start": v(-21398.72, -11161.59) * mm, "end": v(-21398.72, -13147.59) * mm});
            skLineSegment(sketch, "E1848", {"start": v(-21398.72, -13147.59) * mm, "end": v(-20703.72, -13147.59) * mm});
            skLineSegment(sketch, "E1849", {"start": v(-20703.72, -13147.59) * mm, "end": v(-20703.72, -13000.59) * mm});
            skLineSegment(sketch, "E1850", {"start": v(-20693.72, -11151.59) * mm, "end": v(-21408.72, -11151.59) * mm});
            skLineSegment(sketch, "E1851", {"start": v(-21408.72, -11151.59) * mm, "end": v(-21408.72, -13157.59) * mm});
            skLineSegment(sketch, "E1852", {"start": v(-21408.72, -13157.59) * mm, "end": v(-20693.72, -13157.59) * mm});
            skLineSegment(sketch, "E1853", {"start": v(-20693.72, -13157.59) * mm, "end": v(-20693.72, -13000.59) * mm});
            skLineSegment(sketch, "E1854", {"start": v(-20703.72, -12959.59) * mm, "end": v(-20703.72, -12208.59) * mm});
            skLineSegment(sketch, "E1855", {"start": v(-20693.72, -12959.59) * mm, "end": v(-20693.72, -12208.59) * mm});
            skLineSegment(sketch, "E1856", {"start": v(-20693.72, -11339.59) * mm, "end": v(-20693.72, -11151.59) * mm});
            skLineSegment(sketch, "E1857", {"start": v(-20703.72, -11339.59) * mm, "end": v(-20703.72, -11161.59) * mm});
            skLineSegment(sketch, "E1858", {"start": v(-20703.72, -12167.59) * mm, "end": v(-20703.72, -11380.59) * mm});
            skLineSegment(sketch, "E1859", {"start": v(-20693.72, -12167.59) * mm, "end": v(-20693.72, -11380.59) * mm});
            skArc(sketch, "E1860", {"start": v(-21377.72, -12296.58) * mm, "mid": v(-21360.72, -12305.6) * mm, "end": v(-21343.72, -12296.58) * mm});
            skLineSegment(sketch, "E1861", {"start": v(-21377.72, -12112.59) * mm, "end": v(-21377.72, -12296.59) * mm});
            skArc(sketch, "E1862", {"start": v(-21343.72, -12112.58) * mm, "mid": v(-21360.72, -12101.48) * mm, "end": v(-21377.72, -12112.58) * mm});
            skArc(sketch, "E1863", {"start": v(-21247.65, -12153.59) * mm, "mid": v(-21239.65, -12145.59) * mm, "end": v(-21247.65, -12137.59) * mm});
            skLineSegment(sketch, "E1864", {"start": v(-21247.65, -12153.59) * mm, "end": v(-21362.77, -12153.59) * mm});
            skLineSegment(sketch, "E1865", {"start": v(-21247.65, -12137.59) * mm, "end": v(-21362.77, -12137.59) * mm});
            skArc(sketch, "E1866", {"start": v(-21362.77, -12137.59) * mm, "mid": v(-21370.77, -12145.59) * mm, "end": v(-21362.77, -12153.59) * mm});
            skLineSegment(sketch, "E1867", {"start": v(-21343.72, -12137.59) * mm, "end": v(-21343.72, -12112.59) * mm});
            skLineSegment(sketch, "E1868", {"start": v(-21343.72, -12296.59) * mm, "end": v(-21343.72, -12153.59) * mm});
            skLineSegment(sketch, "E1869", {"start": v(-21317.72, -12153.59) * mm, "end": v(-21317.72, -13066.59) * mm});
            skLineSegment(sketch, "E1870", {"start": v(-21317.72, -13066.59) * mm, "end": v(-20784.72, -13066.59) * mm});
            skLineSegment(sketch, "E1871", {"start": v(-20784.72, -13066.59) * mm, "end": v(-20784.72, -11242.59) * mm});
            skLineSegment(sketch, "E1872", {"start": v(-20784.72, -11242.59) * mm, "end": v(-21317.72, -11242.59) * mm});
            skLineSegment(sketch, "E1873", {"start": v(-21317.72, -11242.59) * mm, "end": v(-21317.72, -12137.59) * mm});
            skLineSegment(sketch, "E1874", {"start": v(-20805.72, -11263.59) * mm, "end": v(-21296.72, -11263.59) * mm});
            skLineSegment(sketch, "E1875", {"start": v(-21296.72, -11263.59) * mm, "end": v(-21296.72, -12137.59) * mm});
            skLineSegment(sketch, "E1876", {"start": v(-21296.72, -12153.59) * mm, "end": v(-21296.72, -13045.59) * mm});
            skLineSegment(sketch, "E1877", {"start": v(-21296.72, -13045.59) * mm, "end": v(-20805.72, -13045.59) * mm});
            skLineSegment(sketch, "E1878", {"start": v(-20805.72, -13045.59) * mm, "end": v(-20805.72, -11263.59) * mm});
            skArc(sketch, "E1879", {"start": v(-21499.72, -12296.7) * mm, "mid": v(-21482.72, -12305.72) * mm, "end": v(-21465.72, -12296.7) * mm});
            skLineSegment(sketch, "E1880", {"start": v(-21465.72, -12112.7) * mm, "end": v(-21465.72, -12296.7) * mm});
            skArc(sketch, "E1881", {"start": v(-21465.72, -12112.7) * mm, "mid": v(-21482.72, -12101.58) * mm, "end": v(-21499.72, -12112.7) * mm});
            skArc(sketch, "E1882", {"start": v(-21595.78, -12137.7) * mm, "mid": v(-21603.78, -12145.7) * mm, "end": v(-21595.78, -12153.7) * mm});
            skLineSegment(sketch, "E1883", {"start": v(-21595.78, -12153.7) * mm, "end": v(-21480.66, -12153.7) * mm});
            skLineSegment(sketch, "E1884", {"start": v(-21595.78, -12137.7) * mm, "end": v(-21480.66, -12137.7) * mm});
            skArc(sketch, "E1885", {"start": v(-21480.66, -12153.7) * mm, "mid": v(-21472.66, -12145.7) * mm, "end": v(-21480.66, -12137.7) * mm});
            skLineSegment(sketch, "E1886", {"start": v(-21499.72, -12137.7) * mm, "end": v(-21499.72, -12112.7) * mm});
            skLineSegment(sketch, "E1887", {"start": v(-21499.72, -12296.7) * mm, "end": v(-21499.72, -12153.7) * mm});
            skLineSegment(sketch, "E1888", {"start": v(-21523.72, -12137.7) * mm, "end": v(-21523.72, -11242.59) * mm});
            skLineSegment(sketch, "E1889", {"start": v(-21523.72, -11242.59) * mm, "end": v(-22056.72, -11242.59) * mm});
            skLineSegment(sketch, "E1890", {"start": v(-22056.72, -11242.59) * mm, "end": v(-22056.72, -13066.59) * mm});
            skLineSegment(sketch, "E1891", {"start": v(-22056.72, -13066.59) * mm, "end": v(-21523.72, -13066.59) * mm});
            skLineSegment(sketch, "E1892", {"start": v(-21523.72, -13066.59) * mm, "end": v(-21523.72, -12153.7) * mm});
            skLineSegment(sketch, "E1893", {"start": v(-21544.72, -12137.7) * mm, "end": v(-21544.72, -11263.59) * mm});
            skLineSegment(sketch, "E1894", {"start": v(-21544.72, -11263.59) * mm, "end": v(-22035.72, -11263.59) * mm});
            skLineSegment(sketch, "E1895", {"start": v(-22035.72, -11263.59) * mm, "end": v(-22035.72, -13045.59) * mm});
            skLineSegment(sketch, "E1896", {"start": v(-22035.72, -13045.59) * mm, "end": v(-21544.72, -13045.59) * mm});
            skLineSegment(sketch, "E1897", {"start": v(-21544.72, -13045.59) * mm, "end": v(-21544.72, -12153.7) * mm});
            skCircle(sketch, "E1898", {"center": v(-20407.72, -11179.59) * mm, "radius": 32.63 * mm});
            skCircle(sketch, "E1899", {"center": v(-20297.72, -12963.59) * mm, "radius": 32.63 * mm});
            skCircle(sketch, "E1900", {"center": v(-22533.93, -13102.47) * mm, "radius": 21.36 * mm});
            skLineSegment(sketch, "E1901", {"start": v(-20402.68, -12932.72) * mm, "end": v(-20400.75, -11211.46) * mm});
            skCircle(sketch, "E1902", {"center": v(-20409.72, -12964.59) * mm, "radius": 32.63 * mm});
            skLineSegment(sketch, "E1903", {"start": v(-20416.68, -12932.7) * mm, "end": v(-20414.75, -11211.45) * mm});
            skLineSegment(sketch, "E1904", {"start": v(-20329.52, -12970.87) * mm, "end": v(-20377.79, -12971.3) * mm});
            skLineSegment(sketch, "E1905", {"start": v(-20329.65, -12956.87) * mm, "end": v(-20377.91, -12957.3) * mm});
            skLineSegment(sketch, "E1906", {"start": v(-19753.72, -12895.59) * mm, "end": v(-19592.72, -12895.59) * mm});
            skLineSegment(sketch, "E1907", {"start": v(-19592.72, -12895.59) * mm, "end": v(-19592.72, -13007.59) * mm});
            skLineSegment(sketch, "E1908", {"start": v(-19592.72, -13007.59) * mm, "end": v(-19753.72, -13007.59) * mm});
            skLineSegment(sketch, "E1909", {"start": v(-19753.72, -13007.59) * mm, "end": v(-19753.72, -12895.59) * mm});
            skLineSegment(sketch, "E1910", {"start": v(-19742.72, -13048.59) * mm, "end": v(-19604.72, -13048.59) * mm});
            skLineSegment(sketch, "E1911", {"start": v(-19742.72, -13007.59) * mm, "end": v(-19742.72, -13048.59) * mm});
            skLineSegment(sketch, "E1912", {"start": v(-19604.72, -13048.59) * mm, "end": v(-19604.72, -13007.59) * mm});
            skLineSegment(sketch, "E1913", {"start": v(-19753.72, -13034.58) * mm, "end": v(-19950.72, -13034.58) * mm});
            skLineSegment(sketch, "E1914", {"start": v(-19950.72, -13034.58) * mm, "end": v(-19950.72, -12896.59) * mm});
            skLineSegment(sketch, "E1915", {"start": v(-19950.72, -12896.59) * mm, "end": v(-19753.72, -12896.59) * mm});
            skLineSegment(sketch, "E1916", {"start": v(-19753.72, -12896.59) * mm, "end": v(-19753.72, -13034.58) * mm});
            skLineSegment(sketch, "E1917", {"start": v(-19950.68, -12958.59) * mm, "end": v(-20265.8, -12956.77) * mm});
            skLineSegment(sketch, "E1918", {"start": v(-19950.76, -12972.59) * mm, "end": v(-20265.89, -12970.77) * mm});
            skCircle(sketch, "E1919", {"center": v(-20302.72, -13100.59) * mm, "radius": 21.36 * mm});
            skLineSegment(sketch, "E1920", {"start": v(-18030.59, -12272.59) * mm, "end": v(-19556.9, -12272.59) * mm});
            skLineSegment(sketch, "E1921", {"start": v(-18030.59, -12238.59) * mm, "end": v(-19556.9, -12238.59) * mm});
            skLineSegment(sketch, "E1922", {"start": v(-18030.59, -12305.59) * mm, "end": v(-19556.9, -12305.59) * mm});
            skLineSegment(sketch, "E1923", {"start": v(-19556.9, -11073.67) * mm, "end": v(-19556.9, -12305.59) * mm});
            skLineSegment(sketch, "E1924", {"start": v(-18030.59, -11077.59) * mm, "end": v(-18030.59, -12305.59) * mm});
            skLineSegment(sketch, "E1925", {"start": v(-19471.72, -11203.59) * mm, "end": v(-19471.72, -12125.59) * mm});
            skLineSegment(sketch, "E1926", {"start": v(-19482.72, -11192.59) * mm, "end": v(-19482.72, -12136.59) * mm});
            skLineSegment(sketch, "E1927", {"start": v(-19535.72, -11139.59) * mm, "end": v(-19535.72, -12189.59) * mm});
            skLineSegment(sketch, "E1928", {"start": v(-19546.72, -11130.59) * mm, "end": v(-19546.72, -12198.59) * mm});
            skLineSegment(sketch, "E1929", {"start": v(-19094.72, -11192.59) * mm, "end": v(-19482.72, -11192.59) * mm});
            skLineSegment(sketch, "E1930", {"start": v(-19105.72, -11203.59) * mm, "end": v(-19471.72, -11203.59) * mm});
            skLineSegment(sketch, "E1931", {"start": v(-19471.72, -12125.59) * mm, "end": v(-19105.72, -12125.59) * mm});
            skLineSegment(sketch, "E1932", {"start": v(-19105.72, -12125.59) * mm, "end": v(-19105.72, -11203.59) * mm});
            skLineSegment(sketch, "E1933", {"start": v(-19094.72, -12136.59) * mm, "end": v(-19094.72, -11192.59) * mm});
            skLineSegment(sketch, "E1934", {"start": v(-19482.72, -12136.59) * mm, "end": v(-19094.72, -12136.59) * mm});
            skLineSegment(sketch, "E1935", {"start": v(-19535.72, -12189.59) * mm, "end": v(-19041.72, -12189.59) * mm});
            skLineSegment(sketch, "E1936", {"start": v(-19546.72, -12198.59) * mm, "end": v(-19032.72, -12198.59) * mm});
            skLineSegment(sketch, "E1937", {"start": v(-19041.72, -12189.59) * mm, "end": v(-19041.72, -11139.59) * mm});
            skLineSegment(sketch, "E1938", {"start": v(-19041.72, -11139.59) * mm, "end": v(-19535.72, -11139.59) * mm});
            skLineSegment(sketch, "E1939", {"start": v(-19032.72, -12198.59) * mm, "end": v(-19032.72, -11130.59) * mm});
            skLineSegment(sketch, "E1940", {"start": v(-19032.72, -11130.59) * mm, "end": v(-19546.72, -11130.59) * mm});
            skLineSegment(sketch, "E1941", {"start": v(-18498.72, -11204.59) * mm, "end": v(-18498.72, -12126.59) * mm});
            skLineSegment(sketch, "E1942", {"start": v(-18509.72, -11193.59) * mm, "end": v(-18509.72, -12137.59) * mm});
            skLineSegment(sketch, "E1943", {"start": v(-18562.72, -11140.59) * mm, "end": v(-18562.72, -12190.59) * mm});
            skLineSegment(sketch, "E1944", {"start": v(-18573.72, -11131.59) * mm, "end": v(-18573.72, -12199.59) * mm});
            skLineSegment(sketch, "E1945", {"start": v(-18121.72, -11193.59) * mm, "end": v(-18509.72, -11193.59) * mm});
            skLineSegment(sketch, "E1946", {"start": v(-18132.72, -11204.59) * mm, "end": v(-18498.72, -11204.59) * mm});
            skLineSegment(sketch, "E1947", {"start": v(-18498.72, -12126.59) * mm, "end": v(-18132.72, -12126.59) * mm});
            skLineSegment(sketch, "E1948", {"start": v(-18132.72, -12126.59) * mm, "end": v(-18132.72, -11204.59) * mm});
            skLineSegment(sketch, "E1949", {"start": v(-18121.72, -12137.59) * mm, "end": v(-18121.72, -11193.59) * mm});
            skLineSegment(sketch, "E1950", {"start": v(-18509.72, -12137.59) * mm, "end": v(-18121.72, -12137.59) * mm});
            skLineSegment(sketch, "E1951", {"start": v(-18562.72, -12190.59) * mm, "end": v(-18068.72, -12190.59) * mm});
            skLineSegment(sketch, "E1952", {"start": v(-18573.72, -12199.59) * mm, "end": v(-18059.72, -12199.59) * mm});
            skLineSegment(sketch, "E1953", {"start": v(-18068.72, -12190.59) * mm, "end": v(-18068.72, -11140.59) * mm});
            skLineSegment(sketch, "E1954", {"start": v(-18068.72, -11140.59) * mm, "end": v(-18562.72, -11140.59) * mm});
            skLineSegment(sketch, "E1955", {"start": v(-18059.72, -12199.59) * mm, "end": v(-18059.72, -11131.59) * mm});
            skLineSegment(sketch, "E1956", {"start": v(-18059.72, -11131.59) * mm, "end": v(-18573.72, -11131.59) * mm});
            skLineSegment(sketch, "E1957", {"start": v(-19001.92, -11139.59) * mm, "end": v(-18604.52, -11139.59) * mm});
            skLineSegment(sketch, "E1958", {"start": v(-18604.52, -11139.59) * mm, "end": v(-18604.52, -11342.59) * mm});
            skLineSegment(sketch, "E1959", {"start": v(-18604.52, -11342.59) * mm, "end": v(-19001.92, -11342.59) * mm});
            skLineSegment(sketch, "E1960", {"start": v(-19001.92, -11342.59) * mm, "end": v(-19001.92, -11139.59) * mm});
            skLineSegment(sketch, "E1961", {"start": v(-19010.92, -11130.59) * mm, "end": v(-18595.52, -11130.59) * mm});
            skLineSegment(sketch, "E1962", {"start": v(-18595.52, -11130.59) * mm, "end": v(-18595.52, -11351.58) * mm});
            skLineSegment(sketch, "E1963", {"start": v(-18595.52, -11351.58) * mm, "end": v(-19010.92, -11351.58) * mm});
            skLineSegment(sketch, "E1964", {"start": v(-19010.92, -11351.58) * mm, "end": v(-19010.92, -11130.59) * mm});
            skLineSegment(sketch, "E1965", {"start": v(-18616.72, -11381.59) * mm, "end": v(-18989.72, -11381.59) * mm});
            skLineSegment(sketch, "E1966", {"start": v(-18989.72, -11381.59) * mm, "end": v(-18989.72, -12190.59) * mm});
            skLineSegment(sketch, "E1967", {"start": v(-18989.72, -12190.59) * mm, "end": v(-18616.72, -12190.59) * mm});
            skLineSegment(sketch, "E1968", {"start": v(-18616.72, -12190.59) * mm, "end": v(-18616.72, -11381.59) * mm});
            skLineSegment(sketch, "E1969", {"start": v(-18627.72, -11392.59) * mm, "end": v(-18978.72, -11392.59) * mm});
            skLineSegment(sketch, "E1970", {"start": v(-18978.72, -11392.59) * mm, "end": v(-18978.72, -12179.59) * mm});
            skLineSegment(sketch, "E1971", {"start": v(-18978.72, -12179.59) * mm, "end": v(-18627.72, -12179.59) * mm});
            skLineSegment(sketch, "E1972", {"start": v(-18627.72, -12179.59) * mm, "end": v(-18627.72, -11392.59) * mm});
            skLineSegment(sketch, "E1973", {"start": v(-19105.72, -11157.59) * mm, "end": v(-19508.72, -11157.59) * mm});
            skLineSegment(sketch, "E1974", {"start": v(-19508.72, -11157.59) * mm, "end": v(-19508.72, -11175.59) * mm});
            skLineSegment(sketch, "E1975", {"start": v(-19508.72, -11175.59) * mm, "end": v(-19105.72, -11175.59) * mm});
            skLineSegment(sketch, "E1976", {"start": v(-19105.72, -11175.59) * mm, "end": v(-19105.72, -11157.59) * mm});
            skLineSegment(sketch, "E1977", {"start": v(-18102.72, -11157.59) * mm, "end": v(-18505.72, -11157.59) * mm});
            skLineSegment(sketch, "E1978", {"start": v(-18505.72, -11157.59) * mm, "end": v(-18505.72, -11175.59) * mm});
            skLineSegment(sketch, "E1979", {"start": v(-18505.72, -11175.59) * mm, "end": v(-18102.72, -11175.59) * mm});
            skLineSegment(sketch, "E1980", {"start": v(-18102.72, -11175.59) * mm, "end": v(-18102.72, -11157.59) * mm});
            skLineSegment(sketch, "E1981", {"start": v(-18935.92, -11175.59) * mm, "end": v(-18670.52, -11175.59) * mm});
            skLineSegment(sketch, "E1982", {"start": v(-18946.92, -11164.59) * mm, "end": v(-18659.52, -11164.59) * mm});
            skLineSegment(sketch, "E1983", {"start": v(-18670.52, -11175.59) * mm, "end": v(-18670.52, -11306.59) * mm});
            skLineSegment(sketch, "E1984", {"start": v(-18659.52, -11164.59) * mm, "end": v(-18659.52, -11317.59) * mm});
            skLineSegment(sketch, "E1985", {"start": v(-18670.52, -11306.59) * mm, "end": v(-18935.92, -11306.59) * mm});
            skLineSegment(sketch, "E1986", {"start": v(-18935.92, -11175.59) * mm, "end": v(-18935.92, -11306.59) * mm});
            skLineSegment(sketch, "E1987", {"start": v(-18946.92, -11164.59) * mm, "end": v(-18946.92, -11317.59) * mm});
            skLineSegment(sketch, "E1988", {"start": v(-18659.52, -11317.59) * mm, "end": v(-18946.92, -11317.59) * mm});
            skLineSegment(sketch, "E1989", {"start": v(-18030.59, -11122.59) * mm, "end": v(-19556.9, -11122.59) * mm});
            skLineSegment(sketch, "E1990", {"start": v(-16738.72, -12266.59) * mm, "end": v(-16738.72, -12296.59) * mm});
            skLineSegment(sketch, "E1991", {"start": v(-16689.78, -11077.59) * mm, "end": v(-16689.78, -12266.59) * mm});
            skLineSegment(sketch, "E1992", {"start": v(-16738.72, -12296.59) * mm, "end": v(-15089.78, -12296.59) * mm});
            skLineSegment(sketch, "E1993", {"start": v(-15089.78, -12266.59) * mm, "end": v(-15089.78, -12296.59) * mm});
            skLineSegment(sketch, "E1994", {"start": v(-15089.78, -12266.59) * mm, "end": v(-16738.72, -12266.59) * mm});
            skLineSegment(sketch, "E1995", {"start": v(-15137.61, -11077.59) * mm, "end": v(-15137.61, -12266.59) * mm});
            skLineSegment(sketch, "E1996", {"start": v(-15137.61, -12241.59) * mm, "end": v(-16689.78, -12241.59) * mm});
            skLineSegment(sketch, "E1997", {"start": v(-16583.72, -11215.59) * mm, "end": v(-16583.72, -12137.59) * mm});
            skLineSegment(sketch, "E1998", {"start": v(-16594.72, -11204.59) * mm, "end": v(-16594.72, -12148.59) * mm});
            skLineSegment(sketch, "E1999", {"start": v(-16647.72, -11151.59) * mm, "end": v(-16647.72, -12201.59) * mm});
            skLineSegment(sketch, "E2000", {"start": v(-16658.72, -11142.59) * mm, "end": v(-16658.72, -12210.59) * mm});
            skLineSegment(sketch, "E2001", {"start": v(-16206.72, -11204.59) * mm, "end": v(-16594.72, -11204.59) * mm});
            skLineSegment(sketch, "E2002", {"start": v(-16217.72, -11215.59) * mm, "end": v(-16583.72, -11215.59) * mm});
            skLineSegment(sketch, "E2003", {"start": v(-16583.72, -12137.59) * mm, "end": v(-16217.72, -12137.59) * mm});
            skLineSegment(sketch, "E2004", {"start": v(-16217.72, -12137.59) * mm, "end": v(-16217.72, -11215.59) * mm});
            skLineSegment(sketch, "E2005", {"start": v(-16206.72, -12148.59) * mm, "end": v(-16206.72, -11204.59) * mm});
            skLineSegment(sketch, "E2006", {"start": v(-16594.72, -12148.59) * mm, "end": v(-16206.72, -12148.59) * mm});
            skLineSegment(sketch, "E2007", {"start": v(-16647.72, -12201.59) * mm, "end": v(-16153.72, -12201.59) * mm});
            skLineSegment(sketch, "E2008", {"start": v(-16658.72, -12210.59) * mm, "end": v(-16144.72, -12210.59) * mm});
            skLineSegment(sketch, "E2009", {"start": v(-16153.72, -12201.59) * mm, "end": v(-16153.72, -11151.59) * mm});
            skLineSegment(sketch, "E2010", {"start": v(-16153.72, -11151.59) * mm, "end": v(-16647.72, -11151.59) * mm});
            skLineSegment(sketch, "E2011", {"start": v(-16144.72, -12210.59) * mm, "end": v(-16144.72, -11142.59) * mm});
            skLineSegment(sketch, "E2012", {"start": v(-16144.72, -11142.59) * mm, "end": v(-16658.72, -11142.59) * mm});
            skLineSegment(sketch, "E2013", {"start": v(-15610.72, -11216.59) * mm, "end": v(-15610.72, -12138.59) * mm});
            skLineSegment(sketch, "E2014", {"start": v(-15621.72, -11205.59) * mm, "end": v(-15621.72, -12149.59) * mm});
            skLineSegment(sketch, "E2015", {"start": v(-15674.72, -11152.59) * mm, "end": v(-15674.72, -12202.59) * mm});
            skLineSegment(sketch, "E2016", {"start": v(-15685.72, -11143.59) * mm, "end": v(-15685.72, -12211.59) * mm});
            skLineSegment(sketch, "E2017", {"start": v(-15233.72, -11205.59) * mm, "end": v(-15621.72, -11205.59) * mm});
            skLineSegment(sketch, "E2018", {"start": v(-15244.72, -11216.59) * mm, "end": v(-15610.72, -11216.59) * mm});
            skLineSegment(sketch, "E2019", {"start": v(-15610.72, -12138.59) * mm, "end": v(-15244.72, -12138.59) * mm});
            skLineSegment(sketch, "E2020", {"start": v(-15244.72, -12138.59) * mm, "end": v(-15244.72, -11216.59) * mm});
            skLineSegment(sketch, "E2021", {"start": v(-15233.72, -12149.59) * mm, "end": v(-15233.72, -11205.59) * mm});
            skLineSegment(sketch, "E2022", {"start": v(-15621.72, -12149.59) * mm, "end": v(-15233.72, -12149.59) * mm});
            skLineSegment(sketch, "E2023", {"start": v(-15674.72, -12202.59) * mm, "end": v(-15180.72, -12202.59) * mm});
            skLineSegment(sketch, "E2024", {"start": v(-15685.72, -12211.59) * mm, "end": v(-15171.72, -12211.59) * mm});
            skLineSegment(sketch, "E2025", {"start": v(-15180.72, -12202.59) * mm, "end": v(-15180.72, -11152.59) * mm});
            skLineSegment(sketch, "E2026", {"start": v(-15180.72, -11152.59) * mm, "end": v(-15674.72, -11152.59) * mm});
            skLineSegment(sketch, "E2027", {"start": v(-15171.72, -12211.59) * mm, "end": v(-15171.72, -11143.59) * mm});
            skLineSegment(sketch, "E2028", {"start": v(-15171.72, -11143.59) * mm, "end": v(-15685.72, -11143.59) * mm});
            skLineSegment(sketch, "E2029", {"start": v(-16113.92, -11151.59) * mm, "end": v(-15716.52, -11151.59) * mm});
            skLineSegment(sketch, "E2030", {"start": v(-15716.52, -11151.59) * mm, "end": v(-15716.52, -11354.59) * mm});
            skLineSegment(sketch, "E2031", {"start": v(-15716.52, -11354.59) * mm, "end": v(-16113.92, -11354.59) * mm});
            skLineSegment(sketch, "E2032", {"start": v(-16113.92, -11354.59) * mm, "end": v(-16113.92, -11151.59) * mm});
            skLineSegment(sketch, "E2033", {"start": v(-16122.92, -11142.59) * mm, "end": v(-15707.52, -11142.59) * mm});
            skLineSegment(sketch, "E2034", {"start": v(-15707.52, -11142.59) * mm, "end": v(-15707.52, -11363.59) * mm});
            skLineSegment(sketch, "E2035", {"start": v(-15707.52, -11363.59) * mm, "end": v(-16122.92, -11363.59) * mm});
            skLineSegment(sketch, "E2036", {"start": v(-16122.92, -11363.59) * mm, "end": v(-16122.92, -11142.59) * mm});
            skLineSegment(sketch, "E2037", {"start": v(-15728.72, -11393.59) * mm, "end": v(-16101.72, -11393.59) * mm});
            skLineSegment(sketch, "E2038", {"start": v(-16101.72, -11393.59) * mm, "end": v(-16101.72, -12202.59) * mm});
            skLineSegment(sketch, "E2039", {"start": v(-16101.72, -12202.59) * mm, "end": v(-15728.72, -12202.59) * mm});
            skLineSegment(sketch, "E2040", {"start": v(-15728.72, -12202.59) * mm, "end": v(-15728.72, -11393.59) * mm});
            skLineSegment(sketch, "E2041", {"start": v(-15739.72, -11404.59) * mm, "end": v(-16090.72, -11404.59) * mm});
            skLineSegment(sketch, "E2042", {"start": v(-16090.72, -11404.59) * mm, "end": v(-16090.72, -12191.59) * mm});
            skLineSegment(sketch, "E2043", {"start": v(-16090.72, -12191.59) * mm, "end": v(-15739.72, -12191.59) * mm});
            skLineSegment(sketch, "E2044", {"start": v(-15739.72, -12191.59) * mm, "end": v(-15739.72, -11404.59) * mm});
            skLineSegment(sketch, "E2045", {"start": v(-16217.72, -11169.59) * mm, "end": v(-16620.72, -11169.59) * mm});
            skLineSegment(sketch, "E2046", {"start": v(-16620.72, -11169.59) * mm, "end": v(-16620.72, -11187.59) * mm});
            skLineSegment(sketch, "E2047", {"start": v(-16620.72, -11187.59) * mm, "end": v(-16217.72, -11187.59) * mm});
            skLineSegment(sketch, "E2048", {"start": v(-16217.72, -11187.59) * mm, "end": v(-16217.72, -11169.59) * mm});
            skLineSegment(sketch, "E2049", {"start": v(-15214.72, -11169.59) * mm, "end": v(-15617.72, -11169.59) * mm});
            skLineSegment(sketch, "E2050", {"start": v(-15617.72, -11169.59) * mm, "end": v(-15617.72, -11187.59) * mm});
            skLineSegment(sketch, "E2051", {"start": v(-15617.72, -11187.59) * mm, "end": v(-15214.72, -11187.59) * mm});
            skLineSegment(sketch, "E2052", {"start": v(-15214.72, -11187.59) * mm, "end": v(-15214.72, -11169.59) * mm});
            skLineSegment(sketch, "E2053", {"start": v(-16047.92, -11187.59) * mm, "end": v(-15782.52, -11187.59) * mm});
            skLineSegment(sketch, "E2054", {"start": v(-16058.92, -11176.59) * mm, "end": v(-15771.52, -11176.59) * mm});
            skLineSegment(sketch, "E2055", {"start": v(-15782.52, -11187.59) * mm, "end": v(-15782.52, -11318.59) * mm});
            skLineSegment(sketch, "E2056", {"start": v(-15771.52, -11176.59) * mm, "end": v(-15771.52, -11329.59) * mm});
            skLineSegment(sketch, "E2057", {"start": v(-15782.52, -11318.59) * mm, "end": v(-16047.92, -11318.59) * mm});
            skLineSegment(sketch, "E2058", {"start": v(-16047.92, -11187.59) * mm, "end": v(-16047.92, -11318.59) * mm});
            skLineSegment(sketch, "E2059", {"start": v(-16058.92, -11176.59) * mm, "end": v(-16058.92, -11329.59) * mm});
            skLineSegment(sketch, "E2060", {"start": v(-15771.52, -11329.59) * mm, "end": v(-16058.92, -11329.59) * mm});
            skLineSegment(sketch, "E2061", {"start": v(-15137.61, -11128.59) * mm, "end": v(-16689.78, -11128.59) * mm});
            skLineSegment(sketch, "E2062", {"start": v(-23873.72, -13304.59) * mm, "end": v(-21400.72, -13316.59) * mm});
            skLineSegment(sketch, "E2063", {"start": v(-21400.72, -13316.59) * mm, "end": v(-18176.72, -13306.59) * mm});
            skLineSegment(sketch, "E2064", {"start": v(-18176.72, -13306.59) * mm, "end": v(-13972.46, -13334.68) * mm});
            skLineSegment(sketch, "E2065", {"start": v(-14227.72, -11649.59) * mm, "end": v(-14127.72, -11642.59) * mm});
            skLineSegment(sketch, "E2066", {"start": v(-14127.72, -11642.59) * mm, "end": v(-14115.72, -11834.59) * mm});
            skLineSegment(sketch, "E2067", {"start": v(-14227.72, -11649.59) * mm, "end": v(-14215.72, -11841.59) * mm});
            skLineSegment(sketch, "E2068", {"start": v(-14215.72, -11841.59) * mm, "end": v(-14115.72, -11834.59) * mm});
            skLineSegment(sketch, "E2069", {"start": v(-14912.72, -11468.59) * mm, "end": v(-15015.72, -11468.59) * mm});
            skLineSegment(sketch, "E2070", {"start": v(-14912.72, -13328.4) * mm, "end": v(-14912.72, -11468.59) * mm});
            skLineSegment(sketch, "E2071", {"start": v(-15015.72, -11468.59) * mm, "end": v(-15015.72, -13327.71) * mm});
            skLineSegment(sketch, "E2072", {"start": v(-13702.72, -8581.59) * mm, "end": v(-13707.04, -8504.84) * mm});
            skLineSegment(sketch, "E2073", {"start": v(-23472.74, -10937.59) * mm, "end": v(-19516.72, -10909.58) * mm});
            skLineSegment(sketch, "E2074", {"start": v(-19516.72, -10909.58) * mm, "end": v(-17169.72, -10910.59) * mm});
            skLineSegment(sketch, "E2075", {"start": v(-17169.72, -10910.59) * mm, "end": v(-13674.56, -10930) * mm});
            skLineSegment(sketch, "E2076", {"start": v(-23472.55, -10963.58) * mm, "end": v(-19516.63, -10935.59) * mm});
            skLineSegment(sketch, "E2077", {"start": v(-19516.63, -10935.59) * mm, "end": v(-17169.8, -10936.59) * mm});
            skLineSegment(sketch, "E2078", {"start": v(-17169.8, -10936.59) * mm, "end": v(-13750.86, -10955.59) * mm});
            skLineSegment(sketch, "E2079", {"start": v(-13702.72, -8581.59) * mm, "end": v(-13674.25, -10955.59) * mm});
            skLineSegment(sketch, "E2080", {"start": v(-13807.72, -11091.89) * mm, "end": v(-13807.89, -11014.81) * mm});
            skLineSegment(sketch, "E2081", {"start": v(-13807.72, -11091.89) * mm, "end": v(-15133.72, -11077.59) * mm});
            skLineSegment(sketch, "E2082", {"start": v(-15133.72, -11077.59) * mm, "end": v(-18518.72, -11077.59) * mm});
            skLineSegment(sketch, "E2083", {"start": v(-18518.72, -11077.59) * mm, "end": v(-21700.72, -11065.59) * mm});
            skLineSegment(sketch, "E2084", {"start": v(-21700.72, -11065.59) * mm, "end": v(-23127.93, -11083.07) * mm});
            skLineSegment(sketch, "E2085", {"start": v(-13972.46, -11090.11) * mm, "end": v(-13972.46, -13334.68) * mm});
            skLineSegment(sketch, "E2086", {"start": v(-23107.72, -11036) * mm, "end": v(-19579.56, -11021.55) * mm});
            skLineSegment(sketch, "E2087", {"start": v(-19579.56, -11021.55) * mm, "end": v(-15595.7, -11018.55) * mm});
            skLineSegment(sketch, "E2088", {"start": v(-15595.7, -11018.55) * mm, "end": v(-13663.6, -11014.51) * mm});
            skLineSegment(sketch, "E2089", {"start": v(-23483.72, -10974.59) * mm, "end": v(-19579.72, -10958.59) * mm});
            skLineSegment(sketch, "E2090", {"start": v(-19579.72, -10958.59) * mm, "end": v(-15595.72, -10955.59) * mm});
            skLineSegment(sketch, "E2091", {"start": v(-15595.72, -10955.59) * mm, "end": v(-13663.72, -10955.59) * mm});
            skLineSegment(sketch, "E2092", {"start": v(-13663.72, -10955.59) * mm, "end": v(-13663.6, -11014.51) * mm});
            skLineSegment(sketch, "E2093", {"start": v(4102.73, 9320) * mm, "end": v(4423.83, 9428.41) * mm});
            skLineSegment(sketch, "E2094", {"start": v(4423.83, 9428.41) * mm, "end": v(5330.83, 9879.41) * mm});
            skLineSegment(sketch, "E2095", {"start": v(5330.83, 9879.41) * mm, "end": v(6543.83, 10473.41) * mm});
            skLineSegment(sketch, "E2096", {"start": v(6543.83, 10473.41) * mm, "end": v(7781.83, 11077.41) * mm});
            skLineSegment(sketch, "E2097", {"start": v(7781.83, 11077.41) * mm, "end": v(8678.83, 11529.41) * mm});
            skLineSegment(sketch, "E2098", {"start": v(8678.83, 11529.41) * mm, "end": v(8986.83, 11667.41) * mm});
            skLineSegment(sketch, "E2099", {"start": v(8986.83, 11667.41) * mm, "end": v(8990.83, 11681.41) * mm});
            skLineSegment(sketch, "E2100", {"start": v(8990.83, 11681.41) * mm, "end": v(9051.83, 11721.41) * mm});
            skLineSegment(sketch, "E2101", {"start": v(9051.83, 11721.41) * mm, "end": v(9077.83, 11738.41) * mm});
            skLineSegment(sketch, "E2102", {"start": v(4111.37, 9294.41) * mm, "end": v(4102.73, 9320) * mm});
            skLineSegment(sketch, "E2103", {"start": v(4607, 9158.11) * mm, "end": v(4164.78, 9158.11) * mm});
            skLineSegment(sketch, "E2104", {"start": v(4612.55, 9249.3) * mm, "end": v(4607, 9158.11) * mm});
            skLineSegment(sketch, "E2105", {"start": v(-13672.04, -8434.84) * mm, "end": v(-13742.02, -8434.84) * mm});
            skLineSegment(sketch, "E2106", {"start": v(-13742.02, -8434.84) * mm, "end": v(-13706.92, -8504.6) * mm});
            skLineSegment(sketch, "E2107", {"start": v(-13706.92, -8504.6) * mm, "end": v(-13672.04, -8434.84) * mm});
            skLineSegment(sketch, "E2108", {"start": v(-12509.72, -10752.59) * mm, "end": v(-12422.72, -10752.59) * mm});
            skLineSegment(sketch, "E2109", {"start": v(-12509.72, -10792.59) * mm, "end": v(-12509.72, -10752.59) * mm});
            skLineSegment(sketch, "E2110", {"start": v(-12454.15, -10860.5) * mm, "end": v(-12509.72, -10792.59) * mm});
            skArc(sketch, "E2111", {"start": v(-9102.77, -9411.77) * mm, "mid": v(-9519.1, -9380.3) * mm, "end": v(-9935.72, -9407.59) * mm});
            skLineSegment(sketch, "E2112", {"start": v(-9935.72, -9407.59) * mm, "end": v(-9934.61, -10719.59) * mm});
            skLineSegment(sketch, "E2113", {"start": v(-10003.72, -10719.59) * mm, "end": v(-10003.72, -10773.59) * mm});
            skLineSegment(sketch, "E2114", {"start": v(-9032.56, -10719.59) * mm, "end": v(-10003.72, -10719.59) * mm});
            skLineSegment(sketch, "E2115", {"start": v(-9032.56, -10719.59) * mm, "end": v(-9032.56, -10773.59) * mm});
            skLineSegment(sketch, "E2116", {"start": v(-10003.72, -10773.59) * mm, "end": v(-9032.56, -10773.59) * mm});
            skLineSegment(sketch, "E2117", {"start": v(-9102.77, -9411.77) * mm, "end": v(-9101.67, -10719.59) * mm});
            skLineSegment(sketch, "E2118", {"start": v(-8636.72, -8048.59) * mm, "end": v(-12109.72, -10357.59) * mm});
            skLineSegment(sketch, "E2119", {"start": v(-12109.72, -10357.59) * mm, "end": v(-12514.72, -10614.59) * mm});
            skLineSegment(sketch, "E2120", {"start": v(-12422.72, -10752.59) * mm, "end": v(-12422.72, -10576.72) * mm});
            skLineSegment(sketch, "E2121", {"start": v(-12514.72, -10614.59) * mm, "end": v(-12505.43, -10629.21) * mm});
            skLineSegment(sketch, "E2122", {"start": v(-12033.39, -9140.58) * mm, "end": v(-10278.04, -9139.81) * mm});
            skLineSegment(sketch, "E2123", {"start": v(-12033.39, -9031.58) * mm, "end": v(-10113.98, -9030.73) * mm});
            skLineSegment(sketch, "E2124", {"start": v(-12138.72, -8947.6) * mm, "end": v(-12138.7, -9005.59) * mm});
            skLineSegment(sketch, "E2125", {"start": v(-12138.72, -8947.6) * mm, "end": v(-9987.5, -8946.64) * mm});
            skLineSegment(sketch, "E2126", {"start": v(-12138.7, -9005.59) * mm, "end": v(-10074.79, -9004.68) * mm});
            skLineSegment(sketch, "E2127", {"start": v(-11784.72, -7148.59) * mm, "end": v(-11784.72, -7077.59) * mm});
            skLineSegment(sketch, "E2128", {"start": v(-11202.72, -7613.59) * mm, "end": v(-11815.9, -7594.46) * mm});
            skLineSegment(sketch, "E2129", {"start": v(-11252.72, -7148.59) * mm, "end": v(-11252.72, -7077.59) * mm});
            skLineSegment(sketch, "E2130", {"start": v(-11784.72, -7148.59) * mm, "end": v(-11252.72, -7148.59) * mm});
            skLineSegment(sketch, "E2131", {"start": v(-11252.72, -7077.59) * mm, "end": v(-11784.72, -7077.59) * mm});
            skLineSegment(sketch, "E2132", {"start": v(-11286.1, -7513.2) * mm, "end": v(-11805.28, -7541.11) * mm});
            skLineSegment(sketch, "E2133", {"start": v(-11202.72, -7613.59) * mm, "end": v(-11286.1, -7513.2) * mm});
            skLineSegment(sketch, "E2134", {"start": v(-11753.63, -7148.59) * mm, "end": v(-11765.81, -7538.99) * mm});
            skLineSegment(sketch, "E2135", {"start": v(-8632.1, -8066.32) * mm, "end": v(-12100.28, -10372.11) * mm});
            skLineSegment(sketch, "E2136", {"start": v(-12100.28, -10372.11) * mm, "end": v(-12505.43, -10629.21) * mm});
            skLineSegment(sketch, "E2137", {"start": v(-8578.72, -6781.59) * mm, "end": v(-8580.72, -6830.59) * mm});
            skLineSegment(sketch, "E2138", {"start": v(-8580.72, -6830.59) * mm, "end": v(-8620.72, -6852.59) * mm});
            skLineSegment(sketch, "E2139", {"start": v(-8620.72, -6852.59) * mm, "end": v(-8625.72, -6910.59) * mm});
            skLineSegment(sketch, "E2140", {"start": v(-8655.72, -7537.59) * mm, "end": v(-8657.16, -7607.47) * mm});
            skLineSegment(sketch, "E2141", {"start": v(-8622.66, -7608.18) * mm, "end": v(-8632.1, -8066.32) * mm});
            skLineSegment(sketch, "E2142", {"start": v(-8611.29, -7093.6) * mm, "end": v(-8630.52, -7538.1) * mm});
            skLineSegment(sketch, "E2143", {"start": v(-8655.64, -7029.9) * mm, "end": v(-8408.97, -7040.57) * mm});
            skLineSegment(sketch, "E2144", {"start": v(-8580.72, -6830.59) * mm, "end": v(-8400.22, -6838.4) * mm});
            skLineSegment(sketch, "E2145", {"start": v(-8653, -6968.87) * mm, "end": v(-8655.64, -7029.9) * mm});
            skLineSegment(sketch, "E2146", {"start": v(-8667, -6968.26) * mm, "end": v(-8406.32, -6979.54) * mm});
            skLineSegment(sketch, "E2147", {"start": v(-8667, -6968.26) * mm, "end": v(-8664.43, -6908.91) * mm});
            skLineSegment(sketch, "E2148", {"start": v(-8664.43, -6908.91) * mm, "end": v(-8403.76, -6920.19) * mm});
            skLineSegment(sketch, "E2149", {"start": v(-8632.05, -7030.92) * mm, "end": v(-8634.72, -7092.59) * mm});
            skLineSegment(sketch, "E2150", {"start": v(-8411.63, -7102.24) * mm, "end": v(-8634.72, -7092.59) * mm});
            skLineSegment(sketch, "E2151", {"start": v(-8620.72, -6852.59) * mm, "end": v(-8401.24, -6862.08) * mm});
            skLineSegment(sketch, "E2152", {"start": v(-8420.7, -7542.43) * mm, "end": v(-8655.72, -7537.59) * mm});
            skLineSegment(sketch, "E2153", {"start": v(-8422.15, -7612.32) * mm, "end": v(-8657.16, -7607.47) * mm});
            skLineSegment(sketch, "E2154", {"start": v(-12033.39, -9005.54) * mm, "end": v(-12033.39, -10306.84) * mm});
            skLineSegment(sketch, "E2155", {"start": v(-12085.12, -8947.57) * mm, "end": v(-11805.28, -7541.11) * mm});
            skLineSegment(sketch, "E2156", {"start": v(-11749.65, -7077.59) * mm, "end": v(-11737.86, -6571.88) * mm});
            skLineSegment(sketch, "E2157", {"start": v(-11278.08, -7077.59) * mm, "end": v(-11266.54, -6582.87) * mm});
            skLineSegment(sketch, "E2158", {"start": v(-11765.76, -6490.8) * mm, "end": v(-11767.72, -6570.59) * mm});
            skLineSegment(sketch, "E2159", {"start": v(-11792.1, -6401.4) * mm, "end": v(-11794.27, -6489.56) * mm});
            skLineSegment(sketch, "E2160", {"start": v(-11767.72, -6570.59) * mm, "end": v(-11236.55, -6583.6) * mm});
            skLineSegment(sketch, "E2161", {"start": v(-11234.59, -6503.28) * mm, "end": v(-11236.55, -6583.6) * mm});
            skLineSegment(sketch, "E2162", {"start": v(-11794.27, -6489.56) * mm, "end": v(-11234.59, -6503.28) * mm});
            skLineSegment(sketch, "E2163", {"start": v(-11206.08, -6504.5) * mm, "end": v(-11234.59, -6503.28) * mm});
            skLineSegment(sketch, "E2164", {"start": v(-11203.9, -6415.63) * mm, "end": v(-11206.07, -6503.97) * mm});
            skLineSegment(sketch, "E2165", {"start": v(-11817.72, -6400.59) * mm, "end": v(-11178.28, -6416.25) * mm});
            skLineSegment(sketch, "E2166", {"start": v(-11178.28, -6416.25) * mm, "end": v(-11175.72, -6357.1) * mm});
            skLineSegment(sketch, "E2167", {"start": v(-11763.1, -6252.3) * mm, "end": v(-11730.84, -6224.98) * mm});
            skLineSegment(sketch, "E2168", {"start": v(-11730.84, -6224.98) * mm, "end": v(-11727.72, -6162.59) * mm});
            skLineSegment(sketch, "E2169", {"start": v(-11817.72, -6400.59) * mm, "end": v(-11815.15, -6341.24) * mm});
            skLineSegment(sketch, "E2170", {"start": v(-11815.15, -6341.24) * mm, "end": v(-11176.83, -6356.88) * mm});
            skLineSegment(sketch, "E2171", {"start": v(-11766.12, -6342.44) * mm, "end": v(-11763.1, -6252.3) * mm});
            skLineSegment(sketch, "E2172", {"start": v(-11225.86, -6355.68) * mm, "end": v(-11222.85, -6265.54) * mm});
            skLineSegment(sketch, "E2173", {"start": v(-11763.1, -6252.3) * mm, "end": v(-11222.85, -6265.54) * mm});
            skLineSegment(sketch, "E2174", {"start": v(-11222.85, -6265.54) * mm, "end": v(-11257.04, -6236.6) * mm});
            skLineSegment(sketch, "E2175", {"start": v(-11730.84, -6224.98) * mm, "end": v(-11257.04, -6236.6) * mm});
            skLineSegment(sketch, "E2176", {"start": v(-11727.72, -6162.59) * mm, "end": v(-11255.51, -6174.16) * mm});
            skLineSegment(sketch, "E2177", {"start": v(-11257.04, -6236.6) * mm, "end": v(-11255.39, -6174.16) * mm});
            skLineSegment(sketch, "E2178", {"start": v(-11274.72, -7148.59) * mm, "end": v(-11286.1, -7513.2) * mm});
            skLineSegment(sketch, "E2179", {"start": v(-8578.72, -6781.59) * mm, "end": v(-8398.1, -6789.4) * mm});
            skLineSegment(sketch, "E2180", {"start": v(-8337.94, -6597.83) * mm, "end": v(-8389.72, -6595.59) * mm});
            skArc(sketch, "E2181", {"start": v(-8342.8, -6710.44) * mm, "mid": v(-8465.06, -6731.78) * mm, "end": v(-8578.72, -6781.59) * mm});
            skLineSegment(sketch, "E2182", {"start": v(-8389.72, -6595.59) * mm, "end": v(-8394.92, -6715.84) * mm});
            skLineSegment(sketch, "E2183", {"start": v(-8337.94, -6597.83) * mm, "end": v(-8342.81, -6710.44) * mm});
            skLineSegment(sketch, "E2184", {"start": v(-11364.79, -5572.1) * mm, "end": v(-11482.65, -5565.07) * mm});
            skLineSegment(sketch, "E2185", {"start": v(-11393.34, -6050.03) * mm, "end": v(-11364.79, -5572.1) * mm});
            skLineSegment(sketch, "E2186", {"start": v(-11510.72, -6035.07) * mm, "end": v(-11482.65, -5565.07) * mm});
            skLineSegment(sketch, "E2187", {"start": v(-12454.15, -13532.59) * mm, "end": v(-12454.15, -10860.5) * mm});
            skLineSegment(sketch, "E2188", {"start": v(-12668.92, -13532.59) * mm, "end": v(-12454.15, -13532.59) * mm});
            skLineSegment(sketch, "E2189", {"start": v(4532.99, 6915.31) * mm, "end": v(4531.83, 9158.11) * mm});
            skLineSegment(sketch, "E2190", {"start": v(13678.18, 6856.46) * mm, "end": v(10410.83, 6861.41) * mm});
            skLineSegment(sketch, "E2191", {"start": v(8413.83, 8079.41) * mm, "end": v(9561.83, 8079.41) * mm});
            skLineSegment(sketch, "E2192", {"start": v(8413.83, 8119.41) * mm, "end": v(9561.83, 8119.41) * mm});
            skLineSegment(sketch, "E2193", {"start": v(8413.83, 8131.41) * mm, "end": v(8413.83, 8079.41) * mm});
            skLineSegment(sketch, "E2194", {"start": v(9561.83, 8079.41) * mm, "end": v(9561.83, 8131.41) * mm});
            skLineSegment(sketch, "E2195", {"start": v(8413.83, 8131.41) * mm, "end": v(9561.83, 8131.41) * mm});
            skLineSegment(sketch, "E2196", {"start": v(8444, 8146.41) * mm, "end": v(9504, 8146.41) * mm});
            skLineSegment(sketch, "E2197", {"start": v(9504, 9148.42) * mm, "end": v(8444, 9148.42) * mm});
            skLineSegment(sketch, "E2198", {"start": v(9477.19, 8193.41) * mm, "end": v(8470.83, 8193.41) * mm});
            skLineSegment(sketch, "E2199", {"start": v(8470.83, 8193.41) * mm, "end": v(8470.83, 8750.41) * mm});
            skLineSegment(sketch, "E2200", {"start": v(8470.83, 8750.41) * mm, "end": v(9477.19, 8750.41) * mm});
            skLineSegment(sketch, "E2201", {"start": v(9477.19, 8750.41) * mm, "end": v(9477.19, 8193.41) * mm});
            skLineSegment(sketch, "E2202", {"start": v(9451.19, 8219.41) * mm, "end": v(8496.83, 8219.41) * mm});
            skLineSegment(sketch, "E2203", {"start": v(8496.83, 8219.41) * mm, "end": v(8496.83, 8724.41) * mm});
            skLineSegment(sketch, "E2204", {"start": v(8496.83, 8724.41) * mm, "end": v(9451.19, 8724.41) * mm});
            skLineSegment(sketch, "E2205", {"start": v(9451.19, 8724.41) * mm, "end": v(9451.19, 8219.41) * mm});
            skLineSegment(sketch, "E2206", {"start": v(9470.83, 8774.41) * mm, "end": v(8477.19, 8774.41) * mm});
            skLineSegment(sketch, "E2207", {"start": v(8477.19, 8774.41) * mm, "end": v(8477.19, 9034.41) * mm});
            skLineSegment(sketch, "E2208", {"start": v(8477.19, 9034.41) * mm, "end": v(9470.83, 9034.41) * mm});
            skLineSegment(sketch, "E2209", {"start": v(9470.83, 9034.41) * mm, "end": v(9470.83, 8774.41) * mm});
            skLineSegment(sketch, "E2210", {"start": v(9459.83, 8785.41) * mm, "end": v(8488.19, 8785.41) * mm});
            skLineSegment(sketch, "E2211", {"start": v(8488.19, 8785.41) * mm, "end": v(8488.19, 9023.42) * mm});
            skLineSegment(sketch, "E2212", {"start": v(8488.19, 9023.42) * mm, "end": v(9459.83, 9023.42) * mm});
            skLineSegment(sketch, "E2213", {"start": v(9459.83, 9023.42) * mm, "end": v(9459.83, 8785.41) * mm});
            skLineSegment(sketch, "E2214", {"start": v(9416.83, 8828.41) * mm, "end": v(8531.19, 8828.41) * mm});
            skLineSegment(sketch, "E2215", {"start": v(8531.19, 8828.41) * mm, "end": v(8531.19, 8980.41) * mm});
            skLineSegment(sketch, "E2216", {"start": v(8531.19, 8980.41) * mm, "end": v(9416.83, 8980.41) * mm});
            skLineSegment(sketch, "E2217", {"start": v(9416.83, 8980.41) * mm, "end": v(9416.83, 8828.41) * mm});
            skLineSegment(sketch, "E2218", {"start": v(9405.83, 8839.41) * mm, "end": v(8542.19, 8839.41) * mm});
            skLineSegment(sketch, "E2219", {"start": v(8542.19, 8839.41) * mm, "end": v(8542.19, 8969.41) * mm});
            skLineSegment(sketch, "E2220", {"start": v(8542.19, 8969.41) * mm, "end": v(9405.83, 8969.41) * mm});
            skLineSegment(sketch, "E2221", {"start": v(9405.83, 8969.41) * mm, "end": v(9405.83, 8839.41) * mm});
            skLineSegment(sketch, "E2222", {"start": v(9172.83, 9084.41) * mm, "end": v(8769.83, 9084.41) * mm});
            skLineSegment(sketch, "E2223", {"start": v(8769.83, 9084.41) * mm, "end": v(8769.83, 9066.41) * mm});
            skLineSegment(sketch, "E2224", {"start": v(8769.83, 9066.41) * mm, "end": v(9172.83, 9066.41) * mm});
            skLineSegment(sketch, "E2225", {"start": v(9172.83, 9066.41) * mm, "end": v(9172.83, 9084.41) * mm});
            skLineSegment(sketch, "E2226", {"start": v(8444, 9344.41) * mm, "end": v(8444, 8131.41) * mm});
            skLineSegment(sketch, "E2227", {"start": v(9504, 9344.41) * mm, "end": v(9504, 8131.41) * mm});
            skLineSegment(sketch, "E2228", {"start": v(9504, 9344.41) * mm, "end": v(8444, 9344.41) * mm});
            skLineSegment(sketch, "E2229", {"start": v(9908.83, 9601.41) * mm, "end": v(9820.59, 9601.46) * mm});
            skLineSegment(sketch, "E2230", {"start": v(9919.7, 6865.92) * mm, "end": v(9908.83, 9601.41) * mm});
            skLineSegment(sketch, "E2231", {"start": v(4532.99, 6915.31) * mm, "end": v(10410.83, 6861.41) * mm});
            skLineSegment(sketch, "E2232", {"start": v(9831.45, 6866.73) * mm, "end": v(9820.59, 9601.46) * mm});
            skLineSegment(sketch, "E2233", {"start": v(4111.37, 9294.41) * mm, "end": v(4470.83, 9331.41) * mm});
            skLineSegment(sketch, "E2234", {"start": v(4470.83, 9331.41) * mm, "end": v(4735.83, 9465.42) * mm});
            skLineSegment(sketch, "E2235", {"start": v(4735.83, 9465.42) * mm, "end": v(5823.83, 10000.41) * mm});
            skLineSegment(sketch, "E2236", {"start": v(5823.83, 10000.41) * mm, "end": v(8011.83, 11058.41) * mm});
            skLineSegment(sketch, "E2237", {"start": v(8011.83, 11058.41) * mm, "end": v(9108.77, 11604.73) * mm});
            skLineSegment(sketch, "E2238", {"start": v(9108.77, 11604.73) * mm, "end": v(10180.83, 11101.41) * mm});
            skLineSegment(sketch, "E2239", {"start": v(10180.83, 11101.41) * mm, "end": v(12398.83, 10016.41) * mm});
            skLineSegment(sketch, "E2240", {"start": v(12398.83, 10016.41) * mm, "end": v(13500.83, 9456.41) * mm});
            skLineSegment(sketch, "E2241", {"start": v(13500.83, 9456.41) * mm, "end": v(13690.83, 9363.41) * mm});
            skLineSegment(sketch, "E2242", {"start": v(13690.83, 9363.41) * mm, "end": v(13776.83, 9334.41) * mm});
            skLineSegment(sketch, "E2243", {"start": v(13776.83, 9334.41) * mm, "end": v(13927.83, 9306.41) * mm});
            skLineSegment(sketch, "E2244", {"start": v(11222.83, 10431.41) * mm, "end": v(9105.09, 11450.7) * mm});
            skLineSegment(sketch, "E2245", {"start": v(9105.09, 11450.7) * mm, "end": v(6843.83, 10342.41) * mm});
            skLineSegment(sketch, "E2246", {"start": v(6843.83, 10342.41) * mm, "end": v(4612.55, 9249.3) * mm});
            skLineSegment(sketch, "E2247", {"start": v(11553.83, 12553.41) * mm, "end": v(11553.83, 12498.41) * mm});
            skLineSegment(sketch, "E2248", {"start": v(11529.44, 10588.37) * mm, "end": v(11523.74, 12498.41) * mm});
            skLineSegment(sketch, "E2249", {"start": v(10798.83, 12490.41) * mm, "end": v(10798.83, 12541.41) * mm});
            skLineSegment(sketch, "E2250", {"start": v(10798.83, 12490.41) * mm, "end": v(11553.83, 12498.41) * mm});
            skLineSegment(sketch, "E2251", {"start": v(11553.83, 12553.41) * mm, "end": v(10798.83, 12541.41) * mm});
            skLineSegment(sketch, "E2252", {"start": v(-10561.23, 12553.41) * mm, "end": v(-10561.23, 12929.41) * mm});
            skLineSegment(sketch, "E2253", {"start": v(-10561.23, 12929.41) * mm, "end": v(-10865.23, 12929.41) * mm});
            skLineSegment(sketch, "E2254", {"start": v(-10865.23, 12929.41) * mm, "end": v(-10865.23, 12553.41) * mm});
            skLineSegment(sketch, "E2255", {"start": v(11323.83, 12929.41) * mm, "end": v(11019.83, 12929.41) * mm});
            skLineSegment(sketch, "E2256", {"start": v(11323.83, 12549.76) * mm, "end": v(11323.83, 12929.41) * mm});
            skLineSegment(sketch, "E2257", {"start": v(11019.83, 12929.41) * mm, "end": v(11019.83, 12544.93) * mm});
            skLineSegment(sketch, "E2258", {"start": v(10845.59, 10885.5) * mm, "end": v(10832.64, 12490.41) * mm});
            skLineSegment(sketch, "E2259", {"start": v(16098.77, 10527.28) * mm, "end": v(16097.88, 10606.31) * mm});
            skLineSegment(sketch, "E2260", {"start": v(16097.88, 10606.31) * mm, "end": v(14252.83, 10585.41) * mm});
            skLineSegment(sketch, "E2261", {"start": v(14252.83, 10585.41) * mm, "end": v(12848.83, 10558.41) * mm});
            skLineSegment(sketch, "E2262", {"start": v(12848.83, 10558.41) * mm, "end": v(11877.83, 10540.41) * mm});
            skLineSegment(sketch, "E2263", {"start": v(11877.83, 10540.41) * mm, "end": v(11529.44, 10588.37) * mm});
            skLineSegment(sketch, "E2264", {"start": v(16098.83, 10505.41) * mm, "end": v(14254.37, 10484.52) * mm});
            skLineSegment(sketch, "E2265", {"start": v(14254.37, 10484.52) * mm, "end": v(12850.73, 10457.53) * mm});
            skLineSegment(sketch, "E2266", {"start": v(12850.73, 10457.53) * mm, "end": v(11871.85, 10439.38) * mm});
            skLineSegment(sketch, "E2267", {"start": v(11871.85, 10439.38) * mm, "end": v(11727.1, 10459.3) * mm});
            skLineSegment(sketch, "E2268", {"start": v(16098.77, 10527.28) * mm, "end": v(14254.04, 10506.38) * mm});
            skLineSegment(sketch, "E2269", {"start": v(14254.04, 10506.38) * mm, "end": v(12850.32, 10479.39) * mm});
            skLineSegment(sketch, "E2270", {"start": v(12850.32, 10479.39) * mm, "end": v(11873.14, 10461.27) * mm});
            skLineSegment(sketch, "E2271", {"start": v(11873.14, 10461.27) * mm, "end": v(11663.3, 10490.16) * mm});
            skLineSegment(sketch, "E2272", {"start": v(9186.83, 7093.41) * mm, "end": v(9068.2, 6873.73) * mm});
            skLineSegment(sketch, "E2273", {"start": v(9150.83, 7113.41) * mm, "end": v(9021.63, 6874.15) * mm});
            skLineSegment(sketch, "E2274", {"start": v(9186.83, 7093.41) * mm, "end": v(9150.83, 7113.41) * mm});
            skLineSegment(sketch, "E2275", {"start": v(8911.9, 7004) * mm, "end": v(8910.41, 6875.17) * mm});
            skLineSegment(sketch, "E2276", {"start": v(8947.06, 7036.8) * mm, "end": v(8945.47, 6874.85) * mm});
            skLineSegment(sketch, "E2277", {"start": v(14756.72, 7006.41) * mm, "end": v(14806.78, 7006.41) * mm});
            skLineSegment(sketch, "E2278", {"start": v(13678.43, 7012.8) * mm, "end": v(14756.72, 7006.41) * mm});
            skLineSegment(sketch, "E2279", {"start": v(15076.83, 7396.41) * mm, "end": v(15282.83, 7396.41) * mm});
            skLineSegment(sketch, "E2280", {"start": v(15282.83, 7396.41) * mm, "end": v(15282.83, 7268.41) * mm});
            skLineSegment(sketch, "E2281", {"start": v(15282.83, 7268.41) * mm, "end": v(15076.83, 7268.41) * mm});
            skLineSegment(sketch, "E2282", {"start": v(15076.83, 7268.41) * mm, "end": v(15076.83, 7396.41) * mm});
            skLineSegment(sketch, "E2283", {"start": v(15876.85, 6999.41) * mm, "end": v(14806.78, 7006.41) * mm});
            skLineSegment(sketch, "E2284", {"start": v(15870.1, 6847.7) * mm, "end": v(15876.85, 6999.41) * mm});
            skLineSegment(sketch, "E2285", {"start": v(13678.18, 6856.46) * mm, "end": v(15870.1, 6847.7) * mm});
            skLineSegment(sketch, "E2286", {"start": v(16119.62, 9258.36) * mm, "end": v(16117.83, 9198.45) * mm});
            skArc(sketch, "E2287", {"start": v(15538.53, 8890.04) * mm, "mid": v(15515.41, 8863.63) * mm, "end": v(15506.84, 8829.59) * mm});
            skLineSegment(sketch, "E2288", {"start": v(15487.83, 7005.41) * mm, "end": v(15506.84, 8829.59) * mm});
            skArc(sketch, "E2289", {"start": v(15596.66, 8838.27) * mm, "mid": v(15585.16, 8825.08) * mm, "end": v(15580.9, 8808.1) * mm});
            skLineSegment(sketch, "E2290", {"start": v(15561.83, 7005.41) * mm, "end": v(15580.89, 8808.1) * mm});
            skArc(sketch, "E2291", {"start": v(15744.18, 9035.47) * mm, "mid": v(15754.23, 9046.06) * mm, "end": v(15759.48, 9059.68) * mm});
            skLineSegment(sketch, "E2292", {"start": v(15538.53, 8890.04) * mm, "end": v(15744.18, 9035.47) * mm});
            skArc(sketch, "E2293", {"start": v(15799.87, 8982.68) * mm, "mid": v(15819.76, 9003.63) * mm, "end": v(15830.24, 9030.55) * mm});
            skLineSegment(sketch, "E2294", {"start": v(15596.66, 8838.27) * mm, "end": v(15799.87, 8982.68) * mm});
            skLineSegment(sketch, "E2295", {"start": v(15830.24, 9030.55) * mm, "end": v(15847.83, 9128.41) * mm});
            skLineSegment(sketch, "E2296", {"start": v(16101.84, 9301.29) * mm, "end": v(16098.77, 10527.28) * mm});
            skLineSegment(sketch, "E2297", {"start": v(16101.84, 9301.29) * mm, "end": v(16101.84, 9274.63) * mm});
            skLineSegment(sketch, "E2298", {"start": v(16040.83, 9275.65) * mm, "end": v(16040.83, 9260.19) * mm});
            skLineSegment(sketch, "E2299", {"start": v(16040.83, 9200.75) * mm, "end": v(16040.83, 9148.16) * mm});
            skLineSegment(sketch, "E2300", {"start": v(13933.82, 9378.3) * mm, "end": v(14923.83, 9360.84) * mm});
            skLineSegment(sketch, "E2301", {"start": v(14980.83, 9213.41) * mm, "end": v(14116.44, 9212.3) * mm});
            skLineSegment(sketch, "E2302", {"start": v(15043.1, 9268.41) * mm, "end": v(14187.96, 9266.62) * mm});
            skLineSegment(sketch, "E2303", {"start": v(14893.83, 9213.3) * mm, "end": v(14893.83, 9154.05) * mm});
            skLineSegment(sketch, "E2304", {"start": v(14893.83, 9154.05) * mm, "end": v(14036.83, 9169.69) * mm});
            skLineSegment(sketch, "E2305", {"start": v(14923.83, 9268.16) * mm, "end": v(14923.83, 9360.84) * mm});
            skLineSegment(sketch, "E2306", {"start": v(16101.84, 9301.29) * mm, "end": v(14923.83, 9320.9) * mm});
            skLineSegment(sketch, "E2307", {"start": v(16117.83, 9198.45) * mm, "end": v(15021.65, 9231.22) * mm});
            skLineSegment(sketch, "E2308", {"start": v(16101.4, 9274.64) * mm, "end": v(14923.83, 9294.24) * mm});
            skLineSegment(sketch, "E2309", {"start": v(16119.62, 9258.36) * mm, "end": v(14923.83, 9286.09) * mm});
            skLineSegment(sketch, "E2310", {"start": v(14893.83, 9154.05) * mm, "end": v(14893.83, 9148.16) * mm});
            skLineSegment(sketch, "E2311", {"start": v(15869.4, 6999.41) * mm, "end": v(15871.84, 9148.16) * mm});
            skLineSegment(sketch, "E2312", {"start": v(15759.48, 9059.68) * mm, "end": v(15771.4, 9128.41) * mm});
            skLineSegment(sketch, "E2313", {"start": v(15890.85, 9205.23) * mm, "end": v(15847.83, 9128.41) * mm});
            skLineSegment(sketch, "E2314", {"start": v(15725.62, 9210.17) * mm, "end": v(15771.4, 9128.41) * mm});
            skLineSegment(sketch, "E2315", {"start": v(15858.88, 9148.16) * mm, "end": v(16040.83, 9148.16) * mm});
            skLineSegment(sketch, "E2316", {"start": v(14893.83, 9148.16) * mm, "end": v(15760.35, 9148.16) * mm});
            skLineSegment(sketch, "E2317", {"start": v(14756.72, 9156.55) * mm, "end": v(14756.72, 7006.41) * mm});
            skLineSegment(sketch, "E2318", {"start": v(14806.78, 7006.41) * mm, "end": v(14808.93, 9155.6) * mm});
            skLineSegment(sketch, "E2319", {"start": v(16132.88, 10676.31) * mm, "end": v(16062.9, 10676.31) * mm});
            skLineSegment(sketch, "E2320", {"start": v(16062.9, 10676.31) * mm, "end": v(16098, 10606.55) * mm});
            skLineSegment(sketch, "E2321", {"start": v(16098, 10606.55) * mm, "end": v(16132.88, 10676.31) * mm});
            skLineSegment(sketch, "E2322", {"start": v(4041.35, 9294.44) * mm, "end": v(4043.23, 9283.58) * mm});
            skLineSegment(sketch, "E2323", {"start": v(4043.23, 9283.58) * mm, "end": v(4047.24, 9273.16) * mm});
            skLineSegment(sketch, "E2324", {"start": v(4047.24, 9273.16) * mm, "end": v(4053.25, 9263.51) * mm});
            skLineSegment(sketch, "E2325", {"start": v(4053.25, 9263.51) * mm, "end": v(4061.08, 9254.92) * mm});
            skLineSegment(sketch, "E2326", {"start": v(4061.08, 9254.92) * mm, "end": v(4070.5, 9247.66) * mm});
            skLineSegment(sketch, "E2327", {"start": v(4070.5, 9247.66) * mm, "end": v(4081.22, 9241.93) * mm});
            skLineSegment(sketch, "E2328", {"start": v(4081.22, 9241.93) * mm, "end": v(4092.91, 9237.92) * mm});
            skLineSegment(sketch, "E2329", {"start": v(4092.91, 9237.92) * mm, "end": v(4105.22, 9235.75) * mm});
            skLineSegment(sketch, "E2330", {"start": v(4105.22, 9235.75) * mm, "end": v(4117.78, 9235.49) * mm});
            skLineSegment(sketch, "E2331", {"start": v(4117.78, 9235.49) * mm, "end": v(4130.2, 9237.13) * mm});
            skLineSegment(sketch, "E2332", {"start": v(4130.2, 9237.13) * mm, "end": v(4142.1, 9240.64) * mm});
            skLineSegment(sketch, "E2333", {"start": v(4142.1, 9240.64) * mm, "end": v(4153.12, 9245.9) * mm});
            skLineSegment(sketch, "E2334", {"start": v(4153.12, 9245.9) * mm, "end": v(4162.93, 9252.76) * mm});
            skLineSegment(sketch, "E2335", {"start": v(4162.93, 9252.76) * mm, "end": v(4171.23, 9261) * mm});
            skLineSegment(sketch, "E2336", {"start": v(4171.23, 9261) * mm, "end": v(4177.77, 9270.39) * mm});
            skLineSegment(sketch, "E2337", {"start": v(4177.77, 9270.39) * mm, "end": v(4182.35, 9280.62) * mm});
            skLineSegment(sketch, "E2338", {"start": v(4182.35, 9280.62) * mm, "end": v(4184.83, 9291.4) * mm});
            skLineSegment(sketch, "E2339", {"start": v(4184.83, 9291.4) * mm, "end": v(4185.13, 9294.41) * mm});
            skLineSegment(sketch, "E2340", {"start": v(4185.13, 9294.41) * mm, "end": v(4041.35, 9294.44) * mm});
            skLineSegment(sketch, "E2341", {"start": v(4170.4, 9300.5) * mm, "end": v(4170.16, 9294.42) * mm});
            skLineSegment(sketch, "E2342", {"start": v(4168.74, 9258.54) * mm, "end": v(4164.78, 9158.11) * mm});
            skLineSegment(sketch, "E2343", {"start": v(22148.03, -12552.59) * mm, "end": v(22078.05, -12552.59) * mm});
            skLineSegment(sketch, "E2344", {"start": v(22078.05, -12552.59) * mm, "end": v(22113.14, -12622.35) * mm});
            skLineSegment(sketch, "E2345", {"start": v(22113.14, -12622.35) * mm, "end": v(22148.03, -12552.59) * mm});
            skLineSegment(sketch, "E2346", {"start": v(-13898.96, -13310.19) * mm, "end": v(-13947.94, -13261.2) * mm});
            skLineSegment(sketch, "E2347", {"start": v(-13947.94, -13261.2) * mm, "end": v(-13972.21, -13334.6) * mm});
            skLineSegment(sketch, "E2348", {"start": v(-13972.21, -13334.6) * mm, "end": v(-13898.96, -13310.19) * mm});
            skLineSegment(sketch, "E2349", {"start": v(-13783.22, -11165.39) * mm, "end": v(-13734.24, -11116.4) * mm});
            skLineSegment(sketch, "E2350", {"start": v(-13734.24, -11116.4) * mm, "end": v(-13807.64, -11092.13) * mm});
            skLineSegment(sketch, "E2351", {"start": v(-13807.64, -11092.13) * mm, "end": v(-13783.22, -11165.39) * mm});
            skLineSegment(sketch, "E2352", {"start": v(4091.28, 9133.61) * mm, "end": v(4140.26, 9084.63) * mm});
            skLineSegment(sketch, "E2353", {"start": v(4140.26, 9084.63) * mm, "end": v(4164.53, 9158.03) * mm});
            skLineSegment(sketch, "E2354", {"start": v(4164.53, 9158.03) * mm, "end": v(4091.28, 9133.61) * mm});
            skLineSegment(sketch, "E2355", {"start": v(15943.6, 6872.2) * mm, "end": v(15894.63, 6921.18) * mm});
            skLineSegment(sketch, "E2356", {"start": v(15894.63, 6921.18) * mm, "end": v(15870.36, 6847.78) * mm});
            skLineSegment(sketch, "E2357", {"start": v(15870.36, 6847.78) * mm, "end": v(15943.6, 6872.2) * mm});
            skLineSegment(sketch, "E2358", {"start": v(-14783.75, 6871.91) * mm, "end": v(-14832.73, 6920.9) * mm});
            skLineSegment(sketch, "E2359", {"start": v(-14832.73, 6920.9) * mm, "end": v(-14857, 6847.5) * mm});
            skLineSegment(sketch, "E2360", {"start": v(-14857, 6847.5) * mm, "end": v(-14783.75, 6871.91) * mm});
            skLineSegment(sketch, "E2361", {"start": v(-18141.72, -13236.59) * mm, "end": v(-18211.7, -13236.59) * mm});
            skLineSegment(sketch, "E2362", {"start": v(-18211.7, -13236.59) * mm, "end": v(-18176.6, -13306.35) * mm});
            skLineSegment(sketch, "E2363", {"start": v(-18176.6, -13306.35) * mm, "end": v(-18141.72, -13236.59) * mm});
            skLineSegment(sketch, "E2364", {"start": v(-12693.42, -13459.09) * mm, "end": v(-12742.4, -13508.07) * mm});
            skLineSegment(sketch, "E2365", {"start": v(-12742.4, -13508.07) * mm, "end": v(-12669, -13532.34) * mm});
            skLineSegment(sketch, "E2366", {"start": v(-12669, -13532.34) * mm, "end": v(-12693.42, -13459.09) * mm});
            skLineSegment(sketch, "E2367", {"start": v(-18823.72, -8481.59) * mm, "end": v(-18893.7, -8481.59) * mm});
            skLineSegment(sketch, "E2368", {"start": v(-18893.7, -8481.59) * mm, "end": v(-18858.6, -8551.35) * mm});
            skLineSegment(sketch, "E2369", {"start": v(-18858.6, -8551.35) * mm, "end": v(-18823.72, -8481.59) * mm});
            skLineSegment(sketch, "E2370", {"start": v(-12829.23, 11768.41) * mm, "end": v(-12899.2, 11768.41) * mm});
            skLineSegment(sketch, "E2371", {"start": v(-12899.2, 11768.41) * mm, "end": v(-12864.12, 11698.65) * mm});
            skLineSegment(sketch, "E2372", {"start": v(-12864.12, 11698.65) * mm, "end": v(-12829.23, 11768.41) * mm});
            skLineSegment(sketch, "E2373", {"start": v(-12539.22, -10541.09) * mm, "end": v(-12588.2, -10590.07) * mm});
            skLineSegment(sketch, "E2374", {"start": v(-12588.2, -10590.07) * mm, "end": v(-12514.8, -10614.34) * mm});
            skLineSegment(sketch, "E2375", {"start": v(-12514.8, -10614.34) * mm, "end": v(-12539.22, -10541.09) * mm});
            skLineSegment(sketch, "E2376", {"start": v(-8603.22, -6708.09) * mm, "end": v(-8652.2, -6757.07) * mm});
            skLineSegment(sketch, "E2377", {"start": v(-8652.2, -6757.07) * mm, "end": v(-8578.8, -6781.34) * mm});
            skLineSegment(sketch, "E2378", {"start": v(-8578.8, -6781.34) * mm, "end": v(-8603.22, -6708.09) * mm});
            skLineSegment(sketch, "E2379", {"start": v(-20124.26, 13921.24) * mm, "end": v(-20126.96, 14002.1) * mm});
            skLineSegment(sketch, "E2380", {"start": v(3685.44, -13414.59) * mm, "end": v(3755.42, -13414.59) * mm});
            skLineSegment(sketch, "E2381", {"start": v(3755.42, -13414.59) * mm, "end": v(3720.32, -13344.82) * mm});
            skLineSegment(sketch, "E2382", {"start": v(3720.32, -13344.82) * mm, "end": v(3685.44, -13414.59) * mm});
            skLineSegment(sketch, "E2383", {"start": v(8372.83, 6880.1) * mm, "end": v(8372.83, 8776.42) * mm});
            skLineSegment(sketch, "E2384", {"start": v(8272.83, 6880.1) * mm, "end": v(8272.83, 8776.42) * mm});
            skLineSegment(sketch, "E2385", {"start": v(8372.83, 8776.42) * mm, "end": v(8272.83, 8776.42) * mm});
            skLineSegment(sketch, "E2386", {"start": v(8372.83, 7071.02) * mm, "end": v(8947.06, 7036.8) * mm});
            skLineSegment(sketch, "E2387", {"start": v(8372.83, 7035.9) * mm, "end": v(8911.9, 7004) * mm});
            skLineSegment(sketch, "E2388", {"start": v(14806.78, 6851.95) * mm, "end": v(14806.78, 7006.41) * mm});
            skLineSegment(sketch, "E2389", {"start": v(-22851.51, -13309.55) * mm, "end": v(-22858.81, -11409.11) * mm});
            skLineSegment(sketch, "E2390", {"start": v(-22926.51, -13309.18) * mm, "end": v(-22933.79, -11432.6) * mm});
            skLineSegment(sketch, "E2391", {"start": v(-23271.72, -11409.58) * mm, "end": v(-23238.6, -11409.58) * mm});
            skLineSegment(sketch, "E2392", {"start": v(-23238.6, -13292.85) * mm, "end": v(-23899.72, -13250.59) * mm});
            skLineSegment(sketch, "E2393", {"start": v(-23271.72, -11409.58) * mm, "end": v(-23271.72, -13290.73) * mm});
            skLineSegment(sketch, "E2394", {"start": v(18504.06, -7732.15) * mm, "end": v(18553.05, -7781.14) * mm});
            skLineSegment(sketch, "E2395", {"start": v(18553.05, -7781.14) * mm, "end": v(18577.32, -7707.73) * mm});
            skLineSegment(sketch, "E2396", {"start": v(18577.32, -7707.73) * mm, "end": v(18504.06, -7732.15) * mm});
            skLineSegment(sketch, "E2397", {"start": v(19154.44, -4131.59) * mm, "end": v(19084.47, -4131.59) * mm});
            skLineSegment(sketch, "E2398", {"start": v(19084.47, -4131.59) * mm, "end": v(19119.56, -4201.35) * mm});
            skLineSegment(sketch, "E2399", {"start": v(19119.56, -4201.35) * mm, "end": v(19154.44, -4131.59) * mm});
            skLineSegment(sketch, "E2400", {"start": v(-11274.97, -7156.86) * mm, "end": v(-8614.03, -7156.86) * mm});
            skLineSegment(sketch, "E2401", {"start": v(-11188.47, -7156.86) * mm, "end": v(-11202.72, -7613.59) * mm});
            skLineSegment(sketch, "E2402", {"start": v(-9909.5, -7086.85) * mm, "end": v(-9979.48, -7086.85) * mm});
            skLineSegment(sketch, "E2403", {"start": v(-9979.48, -7086.85) * mm, "end": v(-9944.38, -7156.62) * mm});
            skLineSegment(sketch, "E2404", {"start": v(-9944.38, -7156.62) * mm, "end": v(-9909.5, -7086.85) * mm});
            skLineSegment(sketch, "E2405", {"start": v(-28500, -20252.59) * mm, "end": v(24000, -20252.59) * mm});
            skLineSegment(sketch, "E2406", {"start": v(24000, -20252.59) * mm, "end": v(24000, 20247.41) * mm});
            skLineSegment(sketch, "E2407", {"start": v(24000, 20247.41) * mm, "end": v(-28500, 20247.41) * mm});
            skLineSegment(sketch, "E2408", {"start": v(-28500, 20247.41) * mm, "end": v(-28500, -20252.59) * mm});
            skLineSegment(sketch, "E2409", {"start": v(24000, -2.59) * mm, "end": v(-28500, -2.59) * mm});
            skLineSegment(sketch, "E2410", {"start": v(-2250, -2.59) * mm, "end": v(-2250, 20247.41) * mm});
            skLineSegment(sketch, "E2411", {"start": v(-5019.68, -20252.59) * mm, "end": v(-5019.68, -2.59) * mm});
            skLineSegment(sketch, "E2412", {"start": v(24009.38, -11469.63) * mm, "end": v(28500, -11469.65) * mm});
            skLineSegment(sketch, "E2413", {"start": v(28499.98, -20252.58) * mm, "end": v(24009.35, -20252.58) * mm});
            skLineSegment(sketch, "E2414", {"start": v(24153.21, -8934.27) * mm, "end": v(24153.25, -10705.14) * mm});
            skLineSegment(sketch, "E2415", {"start": v(24551.7, -8934.34) * mm, "end": v(24551.67, -10705.1) * mm});
            skLineSegment(sketch, "E2416", {"start": v(25237.9, -8934.33) * mm, "end": v(25237.92, -10705.13) * mm});
            skLineSegment(sketch, "E2417", {"start": v(28336.68, -8934.3) * mm, "end": v(28336.64, -10705.13) * mm});
            skLineSegment(sketch, "E2418", {"start": v(28336.64, -10705.13) * mm, "end": v(24153.25, -10705.14) * mm});
            skLineSegment(sketch, "E2419", {"start": v(28336.65, -10428.38) * mm, "end": v(24153.24, -10428.37) * mm});
            skLineSegment(sketch, "E2420", {"start": v(28336.65, -10395.18) * mm, "end": v(24153.21, -10395.17) * mm});
            skLineSegment(sketch, "E2421", {"start": v(28336.61, -10145.73) * mm, "end": v(24153.22, -10145.7) * mm});
            skLineSegment(sketch, "E2422", {"start": v(28336.64, -9896.22) * mm, "end": v(24153.21, -9896.22) * mm});
            skLineSegment(sketch, "E2423", {"start": v(28336.64, -9646.74) * mm, "end": v(24153.21, -9646.74) * mm});
            skLineSegment(sketch, "E2424", {"start": v(28336.64, -9397.23) * mm, "end": v(24153.21, -9397.26) * mm});
            skLineSegment(sketch, "E2425", {"start": v(28336.65, -9147.82) * mm, "end": v(24153.21, -9147.78) * mm});
            skArc(sketch, "E2426", {"start": v(24452.64, -12095.72) * mm, "mid": v(24660.97, -13165.46) * mm, "end": v(25693.97, -12818.1) * mm});
            skLineSegment(sketch, "E2427", {"start": v(25013.02, -12568.73) * mm, "end": v(25013.01, -13370.5) * mm});
            skLineSegment(sketch, "E2428", {"start": v(24979.22, -12534.96) * mm, "end": v(24204.32, -12534.93) * mm});
            skLineSegment(sketch, "E2429", {"start": v(25013.02, -12501.07) * mm, "end": v(25012.99, -11691.81) * mm});
            skLineSegment(sketch, "E2430", {"start": v(25046.83, -12534.93) * mm, "end": v(27969.86, -12534.9) * mm});
            skLineSegment(sketch, "E2431", {"start": v(27836.62, -12606.83) * mm, "end": v(27969.86, -12534.9) * mm});
            skLineSegment(sketch, "E2432", {"start": v(27969.86, -12534.9) * mm, "end": v(27836.64, -12462.9) * mm});
            skLineSegment(sketch, "E2433", {"start": v(25634.86, -12153.53) * mm, "end": v(25558.32, -12053.03) * mm});
            skLineSegment(sketch, "E2434", {"start": v(25558.32, -12053.03) * mm, "end": v(25465.54, -11967.34) * mm});
            skLineSegment(sketch, "E2435", {"start": v(25465.54, -11967.34) * mm, "end": v(25359.43, -11899.02) * mm});
            skLineSegment(sketch, "E2436", {"start": v(25359.43, -11899.02) * mm, "end": v(25243.1, -11850.15) * mm});
            skLineSegment(sketch, "E2437", {"start": v(25243.1, -11850.15) * mm, "end": v(25120.15, -11822.25) * mm});
            skLineSegment(sketch, "E2438", {"start": v(25120.15, -11822.25) * mm, "end": v(24994.41, -11816.13) * mm});
            skLineSegment(sketch, "E2439", {"start": v(24994.41, -11816.13) * mm, "end": v(24869.58, -11831.94) * mm});
            skLineSegment(sketch, "E2440", {"start": v(24869.58, -11831.94) * mm, "end": v(24749.41, -11869.27) * mm});
            skLineSegment(sketch, "E2441", {"start": v(24749.41, -11869.27) * mm, "end": v(24637.7, -11926.98) * mm});
            skLineSegment(sketch, "E2442", {"start": v(24637.7, -11926.98) * mm, "end": v(24537.75, -12003.27) * mm});
            skLineSegment(sketch, "E2443", {"start": v(24537.75, -12003.27) * mm, "end": v(24452.64, -12095.72) * mm});
            skLineSegment(sketch, "E2444", {"start": v(25535.27, -12596.8) * mm, "end": v(25517.25, -12584.36) * mm});
            skLineSegment(sketch, "E2445", {"start": v(25517.25, -12584.36) * mm, "end": v(25482.44, -12578.18) * mm});
            skLineSegment(sketch, "E2446", {"start": v(25482.44, -12578.18) * mm, "end": v(25430.94, -12578.18) * mm});
            skLineSegment(sketch, "E2447", {"start": v(25430.94, -12578.18) * mm, "end": v(25388.58, -12584.39) * mm});
            skLineSegment(sketch, "E2448", {"start": v(25388.58, -12584.39) * mm, "end": v(25355.08, -12596.78) * mm});
            skLineSegment(sketch, "E2449", {"start": v(25355.08, -12596.78) * mm, "end": v(25347.34, -12609.22) * mm});
            skLineSegment(sketch, "E2450", {"start": v(25347.34, -12609.22) * mm, "end": v(25352.43, -12621.54) * mm});
            skLineSegment(sketch, "E2451", {"start": v(25352.43, -12621.54) * mm, "end": v(25361.47, -12627.76) * mm});
            skLineSegment(sketch, "E2452", {"start": v(25361.47, -12627.76) * mm, "end": v(25383.37, -12633.97) * mm});
            skLineSegment(sketch, "E2453", {"start": v(25383.37, -12633.97) * mm, "end": v(25452.86, -12646.37) * mm});
            skLineSegment(sketch, "E2454", {"start": v(25452.86, -12646.37) * mm, "end": v(25474.83, -12652.58) * mm});
            skLineSegment(sketch, "E2455", {"start": v(25474.83, -12652.58) * mm, "end": v(25483.8, -12658.76) * mm});
            skLineSegment(sketch, "E2456", {"start": v(25483.8, -12658.76) * mm, "end": v(25488.96, -12671.13) * mm});
            skLineSegment(sketch, "E2457", {"start": v(25488.96, -12671.13) * mm, "end": v(25477.36, -12689.7) * mm});
            skLineSegment(sketch, "E2458", {"start": v(25477.36, -12689.7) * mm, "end": v(25443.91, -12702.12) * mm});
            skLineSegment(sketch, "E2459", {"start": v(25443.91, -12702.12) * mm, "end": v(25401.35, -12708.25) * mm});
            skLineSegment(sketch, "E2460", {"start": v(25401.35, -12708.25) * mm, "end": v(25349.9, -12708.28) * mm});
            skLineSegment(sketch, "E2461", {"start": v(25349.9, -12708.28) * mm, "end": v(25315.1, -12702.1) * mm});
            skLineSegment(sketch, "E2462", {"start": v(25315.1, -12702.1) * mm, "end": v(25297.1, -12689.68) * mm});
            skLineSegment(sketch, "E2463", {"start": v(25649.87, -12578.18) * mm, "end": v(25591.97, -12671.12) * mm});
            skLineSegment(sketch, "E2464", {"start": v(25591.97, -12671.12) * mm, "end": v(25593.24, -12689.7) * mm});
            skLineSegment(sketch, "E2465", {"start": v(25593.24, -12689.7) * mm, "end": v(25611.23, -12702.12) * mm});
            skLineSegment(sketch, "E2466", {"start": v(25611.23, -12702.12) * mm, "end": v(25646.04, -12708.28) * mm});
            skLineSegment(sketch, "E2467", {"start": v(25646.04, -12708.28) * mm, "end": v(25671.77, -12708.27) * mm});
            skLineSegment(sketch, "E2468", {"start": v(25671.77, -12708.27) * mm, "end": v(25714.31, -12702.13) * mm});
            skLineSegment(sketch, "E2469", {"start": v(25714.31, -12702.13) * mm, "end": v(25747.72, -12689.67) * mm});
            skLineSegment(sketch, "E2470", {"start": v(25747.72, -12689.67) * mm, "end": v(25772.2, -12671.15) * mm});
            skLineSegment(sketch, "E2471", {"start": v(25772.2, -12671.15) * mm, "end": v(25830.15, -12578.18) * mm});
            skLineSegment(sketch, "E2472", {"start": v(25945.98, -12578.18) * mm, "end": v(25864.93, -12708.27) * mm});
            skLineSegment(sketch, "E2473", {"start": v(25945.98, -12578.18) * mm, "end": v(26061.85, -12578.18) * mm});
            skLineSegment(sketch, "E2474", {"start": v(26061.85, -12578.18) * mm, "end": v(26096.6, -12584.42) * mm});
            skLineSegment(sketch, "E2475", {"start": v(26096.6, -12584.42) * mm, "end": v(26105.69, -12590.6) * mm});
            skLineSegment(sketch, "E2476", {"start": v(26105.69, -12590.6) * mm, "end": v(26110.76, -12602.97) * mm});
            skLineSegment(sketch, "E2477", {"start": v(26110.76, -12602.97) * mm, "end": v(26103.03, -12615.34) * mm});
            skLineSegment(sketch, "E2478", {"start": v(26103.03, -12615.34) * mm, "end": v(26082.53, -12627.75) * mm});
            skLineSegment(sketch, "E2479", {"start": v(26082.53, -12627.75) * mm, "end": v(26065.75, -12633.97) * mm});
            skLineSegment(sketch, "E2480", {"start": v(26065.75, -12633.97) * mm, "end": v(26023.3, -12640.1) * mm});
            skLineSegment(sketch, "E2481", {"start": v(26023.3, -12640.1) * mm, "end": v(25907.4, -12640.16) * mm});
            skLineSegment(sketch, "E2482", {"start": v(25997.6, -12640.21) * mm, "end": v(26045.14, -12708.28) * mm});
            skLineSegment(sketch, "E2483", {"start": v(26190.58, -12578.18) * mm, "end": v(26212.44, -12708.34) * mm});
            skLineSegment(sketch, "E2484", {"start": v(26396.54, -12578.18) * mm, "end": v(26212.44, -12708.34) * mm});
            skLineSegment(sketch, "E2485", {"start": v(26473.84, -12578.18) * mm, "end": v(26392.83, -12708.28) * mm});
            skLineSegment(sketch, "E2486", {"start": v(26473.84, -12578.18) * mm, "end": v(26641.3, -12578.18) * mm});
            skLineSegment(sketch, "E2487", {"start": v(26435.26, -12640.1) * mm, "end": v(26538.28, -12640.12) * mm});
            skLineSegment(sketch, "E2488", {"start": v(26392.83, -12708.28) * mm, "end": v(26560.18, -12708.34) * mm});
            skLineSegment(sketch, "E2489", {"start": v(26692.74, -12578.18) * mm, "end": v(26757.13, -12640.13) * mm});
            skLineSegment(sketch, "E2490", {"start": v(26757.13, -12640.13) * mm, "end": v(26714.57, -12708.34) * mm});
            skLineSegment(sketch, "E2491", {"start": v(26898.8, -12578.18) * mm, "end": v(26757.13, -12640.13) * mm});
            skLineSegment(sketch, "E2492", {"start": v(27131.79, -12596.81) * mm, "end": v(27113.7, -12584.39) * mm});
            skLineSegment(sketch, "E2493", {"start": v(27113.7, -12584.39) * mm, "end": v(27079.02, -12578.21) * mm});
            skLineSegment(sketch, "E2494", {"start": v(27079.02, -12578.21) * mm, "end": v(27027.52, -12578.18) * mm});
            skLineSegment(sketch, "E2495", {"start": v(27027.52, -12578.18) * mm, "end": v(26985.04, -12584.4) * mm});
            skLineSegment(sketch, "E2496", {"start": v(26985.04, -12584.4) * mm, "end": v(26951.48, -12596.75) * mm});
            skLineSegment(sketch, "E2497", {"start": v(26951.48, -12596.75) * mm, "end": v(26943.8, -12609.15) * mm});
            skLineSegment(sketch, "E2498", {"start": v(26943.8, -12609.15) * mm, "end": v(26948.96, -12621.52) * mm});
            skLineSegment(sketch, "E2499", {"start": v(26948.96, -12621.52) * mm, "end": v(26958, -12627.75) * mm});
            skLineSegment(sketch, "E2500", {"start": v(26958, -12627.75) * mm, "end": v(26979.85, -12633.91) * mm});
            skLineSegment(sketch, "E2501", {"start": v(26979.85, -12633.91) * mm, "end": v(27049.42, -12646.34) * mm});
            skLineSegment(sketch, "E2502", {"start": v(27049.42, -12646.34) * mm, "end": v(27071.25, -12652.52) * mm});
            skLineSegment(sketch, "E2503", {"start": v(27071.25, -12652.52) * mm, "end": v(27080.27, -12658.76) * mm});
            skLineSegment(sketch, "E2504", {"start": v(27080.27, -12658.76) * mm, "end": v(27085.5, -12671.12) * mm});
            skLineSegment(sketch, "E2505", {"start": v(27085.5, -12671.12) * mm, "end": v(27073.88, -12689.77) * mm});
            skLineSegment(sketch, "E2506", {"start": v(27073.88, -12689.77) * mm, "end": v(27040.43, -12702.12) * mm});
            skLineSegment(sketch, "E2507", {"start": v(27040.43, -12702.12) * mm, "end": v(26997.92, -12708.34) * mm});
            skLineSegment(sketch, "E2508", {"start": v(26997.92, -12708.34) * mm, "end": v(26946.42, -12708.27) * mm});
            skLineSegment(sketch, "E2509", {"start": v(26946.42, -12708.27) * mm, "end": v(26911.61, -12702.15) * mm});
            skLineSegment(sketch, "E2510", {"start": v(26911.61, -12702.15) * mm, "end": v(26893.61, -12689.7) * mm});
            skLineSegment(sketch, "E2511", {"start": v(25562.25, -12240.27) * mm, "end": v(25372.83, -12482.82) * mm});
            skLineSegment(sketch, "E2512", {"start": v(25962.97, -12240.26) * mm, "end": v(25435.97, -12402.03) * mm});
            skLineSegment(sketch, "E2513", {"start": v(25624.17, -12344.27) * mm, "end": v(25773.6, -12482.88) * mm});
            skLineSegment(sketch, "E2514", {"start": v(26191.98, -12240.29) * mm, "end": v(26002.65, -12482.92) * mm});
            skLineSegment(sketch, "E2515", {"start": v(26191.98, -12240.29) * mm, "end": v(26403.43, -12482.92) * mm});
            skLineSegment(sketch, "E2516", {"start": v(26592.73, -12240.27) * mm, "end": v(26403.43, -12482.92) * mm});
            skLineSegment(sketch, "E2517", {"start": v(26850.37, -12240.3) * mm, "end": v(26661.03, -12482.95) * mm});
            skLineSegment(sketch, "E2518", {"start": v(26850.37, -12240.3) * mm, "end": v(27050.76, -12240.29) * mm});
            skLineSegment(sketch, "E2519", {"start": v(27050.76, -12240.29) * mm, "end": v(27127.6, -12251.77) * mm});
            skLineSegment(sketch, "E2520", {"start": v(27127.6, -12251.77) * mm, "end": v(27166.76, -12274.91) * mm});
            skLineSegment(sketch, "E2521", {"start": v(27166.76, -12274.91) * mm, "end": v(27177.41, -12298) * mm});
            skLineSegment(sketch, "E2522", {"start": v(27177.41, -12298) * mm, "end": v(27179.06, -12332.66) * mm});
            skLineSegment(sketch, "E2523", {"start": v(27179.06, -12332.66) * mm, "end": v(27133.93, -12390.46) * mm});
            skLineSegment(sketch, "E2524", {"start": v(27133.93, -12390.46) * mm, "end": v(27078.34, -12425.11) * mm});
            skLineSegment(sketch, "E2525", {"start": v(27078.34, -12425.11) * mm, "end": v(27031.7, -12448.17) * mm});
            skLineSegment(sketch, "E2526", {"start": v(27031.7, -12448.17) * mm, "end": v(26956.35, -12471.32) * mm});
            skLineSegment(sketch, "E2527", {"start": v(26956.35, -12471.32) * mm, "end": v(26861.42, -12482.95) * mm});
            skLineSegment(sketch, "E2528", {"start": v(26861.42, -12482.95) * mm, "end": v(26661.03, -12482.95) * mm});
            skLineSegment(sketch, "E2529", {"start": v(25552, -12240.26) * mm, "end": v(25362.7, -12482.85) * mm});
            skLineSegment(sketch, "E2530", {"start": v(25952.74, -12240.26) * mm, "end": v(25425.79, -12401.97) * mm});
            skLineSegment(sketch, "E2531", {"start": v(25614, -12344.23) * mm, "end": v(25763.47, -12482.85) * mm});
            skLineSegment(sketch, "E2532", {"start": v(26181.75, -12240.27) * mm, "end": v(25992.42, -12482.85) * mm});
            skLineSegment(sketch, "E2533", {"start": v(26181.75, -12240.27) * mm, "end": v(26393.26, -12482.86) * mm});
            skLineSegment(sketch, "E2534", {"start": v(26582.53, -12240.26) * mm, "end": v(26393.26, -12482.86) * mm});
            skLineSegment(sketch, "E2535", {"start": v(26840.1, -12240.2) * mm, "end": v(26650.83, -12482.88) * mm});
            skLineSegment(sketch, "E2536", {"start": v(26840.1, -12240.2) * mm, "end": v(27040.59, -12240.27) * mm});
            skLineSegment(sketch, "E2537", {"start": v(27040.59, -12240.27) * mm, "end": v(27117.51, -12251.83) * mm});
            skLineSegment(sketch, "E2538", {"start": v(27117.51, -12251.83) * mm, "end": v(27156.64, -12274.88) * mm});
            skLineSegment(sketch, "E2539", {"start": v(27156.64, -12274.88) * mm, "end": v(27167.34, -12298) * mm});
            skLineSegment(sketch, "E2540", {"start": v(27167.34, -12298) * mm, "end": v(27168.83, -12332.66) * mm});
            skLineSegment(sketch, "E2541", {"start": v(27168.83, -12332.66) * mm, "end": v(27123.7, -12390.49) * mm});
            skLineSegment(sketch, "E2542", {"start": v(27123.7, -12390.49) * mm, "end": v(27068.1, -12425.12) * mm});
            skLineSegment(sketch, "E2543", {"start": v(27068.1, -12425.12) * mm, "end": v(27021.45, -12448.2) * mm});
            skLineSegment(sketch, "E2544", {"start": v(27021.45, -12448.2) * mm, "end": v(26946.09, -12471.35) * mm});
            skLineSegment(sketch, "E2545", {"start": v(26946.09, -12471.35) * mm, "end": v(26851.28, -12482.85) * mm});
            skLineSegment(sketch, "E2546", {"start": v(26851.28, -12482.85) * mm, "end": v(26650.83, -12482.88) * mm});
            skLineSegment(sketch, "E2547", {"start": v(25570.51, -12240.17) * mm, "end": v(25381.18, -12482.85) * mm});
            skLineSegment(sketch, "E2548", {"start": v(25971.23, -12240.26) * mm, "end": v(25444.29, -12401.97) * mm});
            skLineSegment(sketch, "E2549", {"start": v(25632.45, -12344.24) * mm, "end": v(25781.92, -12482.86) * mm});
            skLineSegment(sketch, "E2550", {"start": v(26200.25, -12240.26) * mm, "end": v(26010.88, -12482.82) * mm});
            skLineSegment(sketch, "E2551", {"start": v(26200.25, -12240.26) * mm, "end": v(26411.71, -12482.85) * mm});
            skLineSegment(sketch, "E2552", {"start": v(26601.01, -12240.26) * mm, "end": v(26411.71, -12482.85) * mm});
            skLineSegment(sketch, "E2553", {"start": v(26858.62, -12240.26) * mm, "end": v(26669.32, -12482.86) * mm});
            skLineSegment(sketch, "E2554", {"start": v(26858.62, -12240.26) * mm, "end": v(27058.98, -12240.3) * mm});
            skLineSegment(sketch, "E2555", {"start": v(27058.98, -12240.3) * mm, "end": v(27135.94, -12251.8) * mm});
            skLineSegment(sketch, "E2556", {"start": v(27135.94, -12251.8) * mm, "end": v(27175.05, -12274.91) * mm});
            skLineSegment(sketch, "E2557", {"start": v(27175.05, -12274.91) * mm, "end": v(27185.73, -12298.03) * mm});
            skLineSegment(sketch, "E2558", {"start": v(27185.73, -12298.03) * mm, "end": v(27187.3, -12332.66) * mm});
            skLineSegment(sketch, "E2559", {"start": v(27187.3, -12332.66) * mm, "end": v(27142.2, -12390.4) * mm});
            skLineSegment(sketch, "E2560", {"start": v(27142.2, -12390.4) * mm, "end": v(27086.57, -12425.12) * mm});
            skLineSegment(sketch, "E2561", {"start": v(27086.57, -12425.12) * mm, "end": v(27039.91, -12448.24) * mm});
            skLineSegment(sketch, "E2562", {"start": v(27039.91, -12448.24) * mm, "end": v(26964.62, -12471.34) * mm});
            skLineSegment(sketch, "E2563", {"start": v(26964.62, -12471.34) * mm, "end": v(26869.75, -12482.92) * mm});
            skLineSegment(sketch, "E2564", {"start": v(26869.75, -12482.92) * mm, "end": v(26669.32, -12482.86) * mm});
            skLineSegment(sketch, "E2565", {"start": v(25560.25, -12240.26) * mm, "end": v(25370.91, -12482.92) * mm});
            skLineSegment(sketch, "E2566", {"start": v(25961.08, -12240.26) * mm, "end": v(25434.08, -12402.06) * mm});
            skLineSegment(sketch, "E2567", {"start": v(25622.22, -12344.23) * mm, "end": v(25771.75, -12482.86) * mm});
            skLineSegment(sketch, "E2568", {"start": v(26190.04, -12240.26) * mm, "end": v(26000.76, -12482.86) * mm});
            skLineSegment(sketch, "E2569", {"start": v(26190.04, -12240.26) * mm, "end": v(26401.54, -12482.85) * mm});
            skLineSegment(sketch, "E2570", {"start": v(26590.83, -12240.17) * mm, "end": v(26401.54, -12482.85) * mm});
            skLineSegment(sketch, "E2571", {"start": v(26848.45, -12240.2) * mm, "end": v(26659.18, -12482.92) * mm});
            skLineSegment(sketch, "E2572", {"start": v(26848.45, -12240.2) * mm, "end": v(27048.84, -12240.29) * mm});
            skLineSegment(sketch, "E2573", {"start": v(27048.84, -12240.29) * mm, "end": v(27125.74, -12251.77) * mm});
            skLineSegment(sketch, "E2574", {"start": v(27125.74, -12251.77) * mm, "end": v(27164.9, -12274.95) * mm});
            skLineSegment(sketch, "E2575", {"start": v(27164.9, -12274.95) * mm, "end": v(27175.62, -12298.03) * mm});
            skLineSegment(sketch, "E2576", {"start": v(27175.62, -12298.03) * mm, "end": v(27177.2, -12332.62) * mm});
            skLineSegment(sketch, "E2577", {"start": v(27177.2, -12332.62) * mm, "end": v(27132, -12390.46) * mm});
            skLineSegment(sketch, "E2578", {"start": v(27132, -12390.46) * mm, "end": v(27076.4, -12425.12) * mm});
            skLineSegment(sketch, "E2579", {"start": v(27076.4, -12425.12) * mm, "end": v(27029.66, -12448.27) * mm});
            skLineSegment(sketch, "E2580", {"start": v(27029.66, -12448.27) * mm, "end": v(26954.5, -12471.25) * mm});
            skLineSegment(sketch, "E2581", {"start": v(26954.5, -12471.25) * mm, "end": v(26859.59, -12482.95) * mm});
            skLineSegment(sketch, "E2582", {"start": v(26859.59, -12482.95) * mm, "end": v(26659.18, -12482.92) * mm});
            skLineSegment(sketch, "E2583", {"start": v(27301.92, -12616.94) * mm, "end": v(27223.92, -12716.72) * mm});
            skLineSegment(sketch, "E2584", {"start": v(27223.92, -12716.72) * mm, "end": v(27303.74, -12716.75) * mm});
            skLineSegment(sketch, "E2585", {"start": v(27448.18, -12616.95) * mm, "end": v(27370.28, -12716.74) * mm});
            skLineSegment(sketch, "E2586", {"start": v(27401.56, -12616.98) * mm, "end": v(27494.77, -12616.97) * mm});
            skLineSegment(sketch, "E2587", {"start": v(27534.64, -12616.94) * mm, "end": v(27456.74, -12716.74) * mm});
            skLineSegment(sketch, "E2588", {"start": v(27534.64, -12616.94) * mm, "end": v(27581.2, -12616.92) * mm});
            skLineSegment(sketch, "E2589", {"start": v(27581.2, -12616.92) * mm, "end": v(27597.47, -12621.7) * mm});
            skLineSegment(sketch, "E2590", {"start": v(27597.47, -12621.7) * mm, "end": v(27603.34, -12631.17) * mm});
            skLineSegment(sketch, "E2591", {"start": v(27603.34, -12631.17) * mm, "end": v(27602.54, -12640.7) * mm});
            skLineSegment(sketch, "E2592", {"start": v(27602.54, -12640.7) * mm, "end": v(27598.04, -12654.99) * mm});
            skLineSegment(sketch, "E2593", {"start": v(27598.04, -12654.99) * mm, "end": v(27579.53, -12678.73) * mm});
            skLineSegment(sketch, "E2594", {"start": v(27579.53, -12678.73) * mm, "end": v(27561.74, -12692.99) * mm});
            skLineSegment(sketch, "E2595", {"start": v(27561.74, -12692.99) * mm, "end": v(27547.76, -12702.47) * mm});
            skLineSegment(sketch, "E2596", {"start": v(27547.76, -12702.47) * mm, "end": v(27527, -12711.99) * mm});
            skLineSegment(sketch, "E2597", {"start": v(27527, -12711.99) * mm, "end": v(27503.27, -12716.74) * mm});
            skLineSegment(sketch, "E2598", {"start": v(27503.27, -12716.74) * mm, "end": v(27456.74, -12716.74) * mm});
            skLineSegment(sketch, "E2599", {"start": v(24763.97, -12568.32) * mm, "end": v(24776.45, -12578.42) * mm});
            skLineSegment(sketch, "E2600", {"start": v(24001.73, 10834.36) * mm, "end": v(28499.98, 10834.4) * mm});
            skLineSegment(sketch, "E2601", {"start": v(28499.98, 17899.32) * mm, "end": v(24000, 17899.32) * mm});
            skLineSegment(sketch, "E2602", {"start": v(26191.6, -19924.46) * mm, "end": v(25995.1, -19924.49) * mm});
            skLineSegment(sketch, "E2603", {"start": v(25995.1, -19924.49) * mm, "end": v(25995.04, -20118.05) * mm});
            skLineSegment(sketch, "E2604", {"start": v(25905.08, -20119.63) * mm, "end": v(25905.02, -19924.45) * mm});
            skLineSegment(sketch, "E2605", {"start": v(25905.02, -19924.45) * mm, "end": v(25709.9, -19924.45) * mm});
            skLineSegment(sketch, "E2606", {"start": v(26191.6, -19834.46) * mm, "end": v(25995.05, -19834.46) * mm});
            skLineSegment(sketch, "E2607", {"start": v(25995.05, -19834.46) * mm, "end": v(25995.1, -19639.37) * mm});
            skLineSegment(sketch, "E2608", {"start": v(25763.38, -19720.16) * mm, "end": v(25776.33, -19705.9) * mm});
            skLineSegment(sketch, "E2609", {"start": v(26213.52, -20000.25) * mm, "end": v(26327.6, -20000.22) * mm});
            skLineSegment(sketch, "E2610", {"start": v(26213.46, -19758.78) * mm, "end": v(26817.23, -19758.7) * mm});
            skLineSegment(sketch, "E2611", {"start": v(26817.23, -19758.7) * mm, "end": v(26884.14, -19825.6) * mm});
            skLineSegment(sketch, "E2612", {"start": v(26327.6, -20000.22) * mm, "end": v(26310.12, -20048.47) * mm});
            skLineSegment(sketch, "E2613", {"start": v(26310.12, -20048.47) * mm, "end": v(26793.09, -20048.47) * mm});
            skLineSegment(sketch, "E2614", {"start": v(26793.09, -20048.47) * mm, "end": v(26884.14, -19825.6) * mm});
            skLineSegment(sketch, "E2615", {"start": v(26480.55, -20000.22) * mm, "end": v(26463, -20048.5) * mm});
            skLineSegment(sketch, "E2616", {"start": v(26486.88, -20000.25) * mm, "end": v(26469.4, -20048.5) * mm});
            skLineSegment(sketch, "E2617", {"start": v(26480.55, -20000.22) * mm, "end": v(26486.88, -20000.25) * mm});
            skLineSegment(sketch, "E2618", {"start": v(26640.1, -20000.23) * mm, "end": v(26622.54, -20048.5) * mm});
            skLineSegment(sketch, "E2619", {"start": v(26646.43, -20000.23) * mm, "end": v(26628.88, -20048.43) * mm});
            skLineSegment(sketch, "E2620", {"start": v(26640.1, -20000.23) * mm, "end": v(26646.43, -20000.23) * mm});
            skLineSegment(sketch, "E2621", {"start": v(26807.86, -19833.1) * mm, "end": v(26756.79, -19960.51) * mm});
            skLineSegment(sketch, "E2622", {"start": v(26632.3, -19887.72) * mm, "end": v(26602.6, -19960.52) * mm});
            skLineSegment(sketch, "E2623", {"start": v(26696, -19896.83) * mm, "end": v(26669.93, -19960.5) * mm});
            skLineSegment(sketch, "E2624", {"start": v(26433.4, -19821.68) * mm, "end": v(26376.63, -19960.54) * mm});
            skLineSegment(sketch, "E2625", {"start": v(26493.18, -19887.72) * mm, "end": v(26463.54, -19960.51) * mm});
            skLineSegment(sketch, "E2626", {"start": v(26556.9, -19896.8) * mm, "end": v(26530.97, -19960.52) * mm});
            skLineSegment(sketch, "E2627", {"start": v(26433.4, -19821.68) * mm, "end": v(26516.48, -19821.64) * mm});
            skLineSegment(sketch, "E2628", {"start": v(26376.63, -19960.54) * mm, "end": v(26463.54, -19960.51) * mm});
            skLineSegment(sketch, "E2629", {"start": v(26530.97, -19960.52) * mm, "end": v(26602.6, -19960.52) * mm});
            skLineSegment(sketch, "E2630", {"start": v(26669.93, -19960.5) * mm, "end": v(26756.79, -19960.51) * mm});
            skLineSegment(sketch, "E2631", {"start": v(26516.48, -19821.64) * mm, "end": v(26508.92, -19843.35) * mm});
            skLineSegment(sketch, "E2632", {"start": v(25881.7, -19811.25) * mm, "end": v(25776.33, -19705.9) * mm});
            skLineSegment(sketch, "E2633", {"start": v(25763.38, -19720.16) * mm, "end": v(25854.5, -19811.25) * mm});
            skLineSegment(sketch, "E2634", {"start": v(25816.82, -19811.23) * mm, "end": v(25746.4, -19740.85) * mm});
            skLineSegment(sketch, "E2635", {"start": v(25881.7, -19811.25) * mm, "end": v(25854.5, -19811.25) * mm});
            skLineSegment(sketch, "E2636", {"start": v(25816.82, -19811.23) * mm, "end": v(25713.44, -19811.23) * mm});
            skLineSegment(sketch, "E2637", {"start": v(25811.9, -19676.06) * mm, "end": v(25881.9, -19746.24) * mm});
            skLineSegment(sketch, "E2638", {"start": v(25881.9, -19746.24) * mm, "end": v(25881.95, -19643.54) * mm});
            skLineSegment(sketch, "E2639", {"start": v(26109.35, -19692.8) * mm, "end": v(26123.6, -19705.7) * mm});
            skLineSegment(sketch, "E2640", {"start": v(26018.2, -19811.07) * mm, "end": v(26123.6, -19705.7) * mm});
            skLineSegment(sketch, "E2641", {"start": v(26109.35, -19692.8) * mm, "end": v(26018.2, -19783.93) * mm});
            skLineSegment(sketch, "E2642", {"start": v(26018.25, -19746.23) * mm, "end": v(26088.77, -19675.78) * mm});
            skLineSegment(sketch, "E2643", {"start": v(26018.2, -19811.07) * mm, "end": v(26018.2, -19783.93) * mm});
            skLineSegment(sketch, "E2644", {"start": v(26018.25, -19746.23) * mm, "end": v(26018.21, -19642.88) * mm});
            skLineSegment(sketch, "E2645", {"start": v(26153.46, -19741.28) * mm, "end": v(26083.3, -19811.31) * mm});
            skLineSegment(sketch, "E2646", {"start": v(26083.3, -19811.31) * mm, "end": v(26186, -19811.29) * mm});
            skLineSegment(sketch, "E2647", {"start": v(26137.72, -20039.6) * mm, "end": v(26124.69, -20053.92) * mm});
            skLineSegment(sketch, "E2648", {"start": v(26018.64, -19947.87) * mm, "end": v(26124.69, -20053.92) * mm});
            skLineSegment(sketch, "E2649", {"start": v(26137.72, -20039.6) * mm, "end": v(26046.06, -19947.87) * mm});
            skLineSegment(sketch, "E2650", {"start": v(26083.9, -19947.84) * mm, "end": v(26154.83, -20018.8) * mm});
            skLineSegment(sketch, "E2651", {"start": v(26018.64, -19947.87) * mm, "end": v(26046.06, -19947.87) * mm});
            skLineSegment(sketch, "E2652", {"start": v(26083.9, -19947.84) * mm, "end": v(26188.03, -19947.84) * mm});
            skLineSegment(sketch, "E2653", {"start": v(26089.02, -20083.87) * mm, "end": v(26018.46, -20013.25) * mm});
            skLineSegment(sketch, "E2654", {"start": v(26018.46, -20013.25) * mm, "end": v(26018.47, -20116.7) * mm});
            skLineSegment(sketch, "E2655", {"start": v(25789.91, -20067.1) * mm, "end": v(25775.69, -20054.12) * mm});
            skLineSegment(sketch, "E2656", {"start": v(25881.63, -19948.11) * mm, "end": v(25775.69, -20054.12) * mm});
            skLineSegment(sketch, "E2657", {"start": v(25789.91, -20067.1) * mm, "end": v(25881.7, -19975.4) * mm});
            skLineSegment(sketch, "E2658", {"start": v(25881.7, -20013.28) * mm, "end": v(25810.78, -20084.2) * mm});
            skLineSegment(sketch, "E2659", {"start": v(25881.63, -19948.11) * mm, "end": v(25881.7, -19975.4) * mm});
            skLineSegment(sketch, "E2660", {"start": v(25881.7, -20013.28) * mm, "end": v(25881.66, -20117.41) * mm});
            skLineSegment(sketch, "E2661", {"start": v(25745.75, -20018.37) * mm, "end": v(25816.28, -19947.87) * mm});
            skLineSegment(sketch, "E2662", {"start": v(25816.28, -19947.87) * mm, "end": v(25712.85, -19947.87) * mm});
            skLineSegment(sketch, "E2663", {"start": v(25708.57, -19834.43) * mm, "end": v(25905.05, -19834.4) * mm});
            skLineSegment(sketch, "E2664", {"start": v(25905.05, -19834.4) * mm, "end": v(25905.12, -19639.37) * mm});
            skLineSegment(sketch, "E2665", {"start": v(25950.19, -19589.64) * mm, "end": v(25899.81, -19594.12) * mm});
            skLineSegment(sketch, "E2666", {"start": v(25899.81, -19594.12) * mm, "end": v(25850.97, -19607.12) * mm});
            skLineSegment(sketch, "E2667", {"start": v(25850.97, -19607.12) * mm, "end": v(25805.2, -19628.43) * mm});
            skLineSegment(sketch, "E2668", {"start": v(25805.2, -19628.43) * mm, "end": v(25763.9, -19657.43) * mm});
            skLineSegment(sketch, "E2669", {"start": v(25763.9, -19657.43) * mm, "end": v(25728.05, -19693.15) * mm});
            skLineSegment(sketch, "E2670", {"start": v(25728.05, -19693.15) * mm, "end": v(25699.19, -19734.57) * mm});
            skLineSegment(sketch, "E2671", {"start": v(25699.19, -19734.57) * mm, "end": v(25677.77, -19780.37) * mm});
            skLineSegment(sketch, "E2672", {"start": v(25677.77, -19780.37) * mm, "end": v(25664.71, -19829.16) * mm});
            skLineSegment(sketch, "E2673", {"start": v(25664.71, -19829.16) * mm, "end": v(25660.33, -19879.43) * mm});
            skLineSegment(sketch, "E2674", {"start": v(25660.33, -19879.43) * mm, "end": v(25664.71, -19929.8) * mm});
            skLineSegment(sketch, "E2675", {"start": v(25664.71, -19929.8) * mm, "end": v(25677.75, -19978.53) * mm});
            skLineSegment(sketch, "E2676", {"start": v(25677.75, -19978.53) * mm, "end": v(25699.21, -20024.37) * mm});
            skLineSegment(sketch, "E2677", {"start": v(25699.21, -20024.37) * mm, "end": v(25728.06, -20065.76) * mm});
            skLineSegment(sketch, "E2678", {"start": v(25728.06, -20065.76) * mm, "end": v(25763.9, -20101.44) * mm});
            skLineSegment(sketch, "E2679", {"start": v(25763.9, -20101.44) * mm, "end": v(25805.16, -20130.47) * mm});
            skLineSegment(sketch, "E2680", {"start": v(25805.16, -20130.47) * mm, "end": v(25850.99, -20151.76) * mm});
            skLineSegment(sketch, "E2681", {"start": v(25850.99, -20151.76) * mm, "end": v(25899.8, -20164.85) * mm});
            skLineSegment(sketch, "E2682", {"start": v(25899.8, -20164.85) * mm, "end": v(25950.12, -20169.24) * mm});
            skLineSegment(sketch, "E2683", {"start": v(25950.12, -20169.24) * mm, "end": v(26000.5, -20164.86) * mm});
            skLineSegment(sketch, "E2684", {"start": v(26000.5, -20164.86) * mm, "end": v(26049.15, -20151.76) * mm});
            skLineSegment(sketch, "E2685", {"start": v(26049.15, -20151.76) * mm, "end": v(26094.96, -20130.44) * mm});
            skLineSegment(sketch, "E2686", {"start": v(26094.96, -20130.44) * mm, "end": v(26136.39, -20101.45) * mm});
            skLineSegment(sketch, "E2687", {"start": v(26136.39, -20101.45) * mm, "end": v(26172.07, -20065.79) * mm});
            skLineSegment(sketch, "E2688", {"start": v(26172.07, -20065.79) * mm, "end": v(26201.06, -20024.34) * mm});
            skLineSegment(sketch, "E2689", {"start": v(26201.06, -20024.34) * mm, "end": v(26213.52, -20000.25) * mm});
            skLineSegment(sketch, "E2690", {"start": v(26208.74, -19748.8) * mm, "end": v(26182.12, -19705.89) * mm});
            skLineSegment(sketch, "E2691", {"start": v(26182.12, -19705.89) * mm, "end": v(26148.45, -19668.2) * mm});
            skLineSegment(sketch, "E2692", {"start": v(26148.45, -19668.2) * mm, "end": v(26108.7, -19636.96) * mm});
            skLineSegment(sketch, "E2693", {"start": v(26108.7, -19636.96) * mm, "end": v(26064.27, -19613.1) * mm});
            skLineSegment(sketch, "E2694", {"start": v(26064.27, -19613.1) * mm, "end": v(26016.24, -19597.38) * mm});
            skLineSegment(sketch, "E2695", {"start": v(26016.24, -19597.38) * mm, "end": v(25966.24, -19590.22) * mm});
            skLineSegment(sketch, "E2696", {"start": v(25966.24, -19590.22) * mm, "end": v(25950.16, -19589.74) * mm});
            skLineSegment(sketch, "E2697", {"start": v(26213.46, -19758.78) * mm, "end": v(26208.62, -19748.82) * mm});
            skLineSegment(sketch, "E2698", {"start": v(26696, -19896.83) * mm, "end": v(26696.25, -19891.23) * mm});
            skLineSegment(sketch, "E2699", {"start": v(26696.25, -19891.23) * mm, "end": v(26695.66, -19885.6) * mm});
            skLineSegment(sketch, "E2700", {"start": v(26695.66, -19885.6) * mm, "end": v(26693.93, -19880.23) * mm});
            skLineSegment(sketch, "E2701", {"start": v(26693.93, -19880.23) * mm, "end": v(26691.49, -19875.25) * mm});
            skLineSegment(sketch, "E2702", {"start": v(26691.49, -19875.25) * mm, "end": v(26688.12, -19870.8) * mm});
            skLineSegment(sketch, "E2703", {"start": v(26688.12, -19870.8) * mm, "end": v(26683.94, -19866.99) * mm});
            skLineSegment(sketch, "E2704", {"start": v(26683.94, -19866.99) * mm, "end": v(26679.3, -19863.9) * mm});
            skLineSegment(sketch, "E2705", {"start": v(26679.3, -19863.9) * mm, "end": v(26674.08, -19861.72) * mm});
            skLineSegment(sketch, "E2706", {"start": v(26674.08, -19861.72) * mm, "end": v(26668.74, -19860.42) * mm});
            skLineSegment(sketch, "E2707", {"start": v(26668.74, -19860.42) * mm, "end": v(26663.14, -19860.14) * mm});
            skLineSegment(sketch, "E2708", {"start": v(26663.14, -19860.14) * mm, "end": v(26657.54, -19860.75) * mm});
            skLineSegment(sketch, "E2709", {"start": v(26657.54, -19860.75) * mm, "end": v(26652.18, -19862.48) * mm});
            skLineSegment(sketch, "E2710", {"start": v(26652.18, -19862.48) * mm, "end": v(26647.18, -19864.98) * mm});
            skLineSegment(sketch, "E2711", {"start": v(26647.18, -19864.98) * mm, "end": v(26642.72, -19868.3) * mm});
            skLineSegment(sketch, "E2712", {"start": v(26642.72, -19868.3) * mm, "end": v(26638.78, -19872.47) * mm});
            skLineSegment(sketch, "E2713", {"start": v(26638.78, -19872.47) * mm, "end": v(26635.73, -19877.1) * mm});
            skLineSegment(sketch, "E2714", {"start": v(26635.73, -19877.1) * mm, "end": v(26633.53, -19882.3) * mm});
            skLineSegment(sketch, "E2715", {"start": v(26633.53, -19882.3) * mm, "end": v(26632.3, -19887.72) * mm});
            skLineSegment(sketch, "E2716", {"start": v(26556.9, -19896.8) * mm, "end": v(26557.22, -19891.2) * mm});
            skLineSegment(sketch, "E2717", {"start": v(26557.22, -19891.2) * mm, "end": v(26556.52, -19885.6) * mm});
            skLineSegment(sketch, "E2718", {"start": v(26556.52, -19885.6) * mm, "end": v(26554.91, -19880.24) * mm});
            skLineSegment(sketch, "E2719", {"start": v(26554.91, -19880.24) * mm, "end": v(26552.41, -19875.28) * mm});
            skLineSegment(sketch, "E2720", {"start": v(26552.41, -19875.28) * mm, "end": v(26549, -19870.8) * mm});
            skLineSegment(sketch, "E2721", {"start": v(26549, -19870.8) * mm, "end": v(26544.94, -19866.95) * mm});
            skLineSegment(sketch, "E2722", {"start": v(26544.94, -19866.95) * mm, "end": v(26540.22, -19863.94) * mm});
            skLineSegment(sketch, "E2723", {"start": v(26540.22, -19863.94) * mm, "end": v(26535.08, -19861.72) * mm});
            skLineSegment(sketch, "E2724", {"start": v(26535.08, -19861.72) * mm, "end": v(26529.6, -19860.4) * mm});
            skLineSegment(sketch, "E2725", {"start": v(26529.6, -19860.4) * mm, "end": v(26524, -19860.13) * mm});
            skLineSegment(sketch, "E2726", {"start": v(26524, -19860.13) * mm, "end": v(26518.46, -19860.77) * mm});
            skLineSegment(sketch, "E2727", {"start": v(26518.46, -19860.77) * mm, "end": v(26513.04, -19862.45) * mm});
            skLineSegment(sketch, "E2728", {"start": v(26513.04, -19862.45) * mm, "end": v(26508.04, -19864.94) * mm});
            skLineSegment(sketch, "E2729", {"start": v(26508.04, -19864.94) * mm, "end": v(26503.57, -19868.3) * mm});
            skLineSegment(sketch, "E2730", {"start": v(26503.57, -19868.3) * mm, "end": v(26499.79, -19872.47) * mm});
            skLineSegment(sketch, "E2731", {"start": v(26499.79, -19872.47) * mm, "end": v(26496.71, -19877.07) * mm});
            skLineSegment(sketch, "E2732", {"start": v(26496.71, -19877.07) * mm, "end": v(26494.5, -19882.31) * mm});
            skLineSegment(sketch, "E2733", {"start": v(26494.5, -19882.31) * mm, "end": v(26493.18, -19887.72) * mm});
            skLineSegment(sketch, "E2734", {"start": v(26186, -19811.29) * mm, "end": v(26170.6, -19771.33) * mm});
            skLineSegment(sketch, "E2735", {"start": v(26170.6, -19771.33) * mm, "end": v(26153.28, -19741.46) * mm});
            skLineSegment(sketch, "E2736", {"start": v(26176.57, -19979.49) * mm, "end": v(26188.03, -19947.84) * mm});
            skLineSegment(sketch, "E2737", {"start": v(26154.83, -20018.8) * mm, "end": v(26176.57, -19979.49) * mm});
            skLineSegment(sketch, "E2738", {"start": v(26018.47, -20116.7) * mm, "end": v(26058.7, -20101.21) * mm});
            skLineSegment(sketch, "E2739", {"start": v(26058.7, -20101.21) * mm, "end": v(26088.86, -20083.71) * mm});
            skLineSegment(sketch, "E2740", {"start": v(25850.14, -20105.87) * mm, "end": v(25881.7, -20117.35) * mm});
            skLineSegment(sketch, "E2741", {"start": v(25810.78, -20084.2) * mm, "end": v(25850.14, -20105.87) * mm});
            skLineSegment(sketch, "E2742", {"start": v(25712.85, -19947.87) * mm, "end": v(25728.42, -19988.07) * mm});
            skLineSegment(sketch, "E2743", {"start": v(25728.42, -19988.07) * mm, "end": v(25745.87, -20018.24) * mm});
            skLineSegment(sketch, "E2744", {"start": v(25724.95, -19779.88) * mm, "end": v(25713.5, -19811.29) * mm});
            skLineSegment(sketch, "E2745", {"start": v(25746.4, -19740.85) * mm, "end": v(25724.95, -19779.88) * mm});
            skLineSegment(sketch, "E2746", {"start": v(25881.95, -19643.54) * mm, "end": v(25841.98, -19659.02) * mm});
            skLineSegment(sketch, "E2747", {"start": v(25841.98, -19659.02) * mm, "end": v(25812.08, -19676.26) * mm});
            skLineSegment(sketch, "E2748", {"start": v(26049.66, -19654.3) * mm, "end": v(26018.21, -19642.88) * mm});
            skLineSegment(sketch, "E2749", {"start": v(26088.77, -19675.78) * mm, "end": v(26049.66, -19654.3) * mm});
            skLineSegment(sketch, "E2750", {"start": v(26018.23, -19685.5) * mm, "end": v(26052.24, -19712.28) * mm});
            skLineSegment(sketch, "E2751", {"start": v(26018.22, -19663.81) * mm, "end": v(26066.95, -19697.58) * mm});
            skLineSegment(sketch, "E2752", {"start": v(26056.03, -19657.8) * mm, "end": v(26041.3, -19684.12) * mm});
            skLineSegment(sketch, "E2753", {"start": v(25506.23, -18755.68) * mm, "end": v(25506.25, -20252.59) * mm});
            skLineSegment(sketch, "E2754", {"start": v(27003.07, -18755.69) * mm, "end": v(27003.13, -20252.57) * mm});
            skLineSegment(sketch, "E2755", {"start": v(28499.48, -14326.2) * mm, "end": v(24009.36, -14326.2) * mm});
            skLineSegment(sketch, "E2756", {"start": v(28499.48, -16250.97) * mm, "end": v(24009.36, -16250.97) * mm});
            skLineSegment(sketch, "E2757", {"start": v(28499.48, -17747.8) * mm, "end": v(24009.36, -17747.8) * mm});
            skLineSegment(sketch, "E2758", {"start": v(28499.48, -18755.67) * mm, "end": v(24009.36, -18755.67) * mm});
            skLineSegment(sketch, "E2759", {"start": v(28499.48, -19504.1) * mm, "end": v(24009.36, -19504.1) * mm});
            skLineSegment(sketch, "E2760", {"start": v(24009.35, -20252.58) * mm, "end": v(28499.98, -20252.58) * mm});
            skLineSegment(sketch, "E2761", {"start": v(28499.98, -20252.58) * mm, "end": v(28499.98, 20252.58) * mm});
            skLineSegment(sketch, "E2762", {"start": v(28499.98, 20252.58) * mm, "end": v(24009.35, 20252.58) * mm});
            skLineSegment(sketch, "E2763", {"start": v(-25924.39, 3997.43) * mm, "end": v(-28500, 3997.41) * mm});
            skLineSegment(sketch, "E2764", {"start": v(325.61, 3997.43) * mm, "end": v(-2250, 3997.41) * mm});
            skLineSegment(sketch, "E2765", {"start": v(-25924.39, -16252.57) * mm, "end": v(-28500, -16252.59) * mm});
            skLineSegment(sketch, "E2766", {"start": v(-2444.06, -16252.57) * mm, "end": v(-5019.68, -16252.59) * mm});
            skLineSegment(sketch, "E2767", {"start": v(-4825.61, 3997.43) * mm, "end": v(-2250, 3997.41) * mm});
            skLineSegment(sketch, "E2768", {"start": v(21424.39, 3997.43) * mm, "end": v(24000, 3997.41) * mm});
            skLineSegment(sketch, "E2769", {"start": v(21424.39, -16252.57) * mm, "end": v(24000, -16252.59) * mm});
            skLineSegment(sketch, "E2770", {"start": v(-7595.29, -16252.57) * mm, "end": v(-5019.68, -16252.59) * mm});
            skLineSegment(sketch, "E2771", {"start": v(24000, -18752.35) * mm, "end": v(18136.78, -18752.37) * mm});
            skLineSegment(sketch, "E2772", {"start": v(18136.78, -20252.59) * mm, "end": v(18136.78, -18752.37) * mm});
            skLineSegment(sketch, "E2773", {"start": v(18564.04, -19922.05) * mm, "end": v(18564.04, -19685.23) * mm});
            skLineSegment(sketch, "E2774", {"start": v(19564.17, -19922.05) * mm, "end": v(19564.17, -19685.22) * mm});
            skLineSegment(sketch, "E2775", {"start": v(20564.3, -19922.04) * mm, "end": v(20564.3, -19685.22) * mm});
            skLineSegment(sketch, "E2776", {"start": v(21564.42, -19922.04) * mm, "end": v(21564.42, -19685.22) * mm});
            skLineSegment(sketch, "E2777", {"start": v(22564.55, -19922.04) * mm, "end": v(22564.55, -19685.21) * mm});
            skLineSegment(sketch, "E2778", {"start": v(23564.67, -19922.03) * mm, "end": v(23564.67, -19685.2) * mm});
            skLineSegment(sketch, "E2779", {"start": v(18564.04, -19685.23) * mm, "end": v(18564.04, -19448.4) * mm});
            skLineSegment(sketch, "E2780", {"start": v(23564.67, -19685.2) * mm, "end": v(23564.67, -19448.39) * mm});
            skLineSegment(sketch, "E2781", {"start": v(23564.67, -19685.2) * mm, "end": v(18564.04, -19685.23) * mm});
            skLineSegment(sketch, "E2782", {"start": v(23564.67, -19922.03) * mm, "end": v(18564.04, -19922.05) * mm});
            skLineSegment(sketch, "E2783", {"start": v(26216.14, 15128.3) * mm, "end": v(26213.51, 15127.91) * mm});
            skLineSegment(sketch, "E2784", {"start": v(26815.62, 15363.74) * mm, "end": v(27562.7, 15476.04) * mm});
            skLineSegment(sketch, "E2785", {"start": v(27742.6, 15503.15) * mm, "end": v(27810.67, 15050.91) * mm});
            skLineSegment(sketch, "E2786", {"start": v(27562.7, 15476.04) * mm, "end": v(27742.6, 15503.15) * mm});
            skLineSegment(sketch, "E2787", {"start": v(27810.67, 15050.91) * mm, "end": v(27833.01, 14905.7) * mm});
            skLineSegment(sketch, "E2788", {"start": v(27833.01, 14905.7) * mm, "end": v(27683.58, 14883.3) * mm});
            skLineSegment(sketch, "E2789", {"start": v(27722.88, 14605.44) * mm, "end": v(27722.43, 14608.41) * mm});
            skLineSegment(sketch, "E2790", {"start": v(27730.02, 14606.5) * mm, "end": v(27722.88, 14605.44) * mm});
            skLineSegment(sketch, "E2791", {"start": v(27729.43, 14611.21) * mm, "end": v(27730.02, 14606.5) * mm});
            skLineSegment(sketch, "E2792", {"start": v(27729.43, 14611.21) * mm, "end": v(27727.42, 14610.9) * mm});
            skLineSegment(sketch, "E2793", {"start": v(27688, 14872.23) * mm, "end": v(27685.43, 14871.82) * mm});
            skLineSegment(sketch, "E2794", {"start": v(27688.83, 14867.1) * mm, "end": v(27688, 14872.23) * mm});
            skLineSegment(sketch, "E2795", {"start": v(27683.58, 14883.3) * mm, "end": v(27685.43, 14871.82) * mm});
            skLineSegment(sketch, "E2796", {"start": v(27708.8, 14744.34) * mm, "end": v(27709.55, 14739.63) * mm});
            skLineSegment(sketch, "E2797", {"start": v(27709.55, 14739.63) * mm, "end": v(27706.77, 14739.18) * mm});
            skLineSegment(sketch, "E2798", {"start": v(27706.77, 14739.18) * mm, "end": v(27727.42, 14610.9) * mm});
            skLineSegment(sketch, "E2799", {"start": v(27581.67, 14584.75) * mm, "end": v(27581.28, 14587.37) * mm});
            skLineSegment(sketch, "E2800", {"start": v(27722.43, 14608.41) * mm, "end": v(27581.28, 14587.37) * mm});
            skLineSegment(sketch, "E2801", {"start": v(27576.45, 14583.98) * mm, "end": v(27581.67, 14584.75) * mm});
            skLineSegment(sketch, "E2802", {"start": v(27576.45, 14583.98) * mm, "end": v(27622.27, 14275.84) * mm});
            skLineSegment(sketch, "E2803", {"start": v(27104.39, 14113.26) * mm, "end": v(26718.12, 14054.34) * mm});
            skLineSegment(sketch, "E2804", {"start": v(27622.27, 14275.84) * mm, "end": v(27634.8, 14193.35) * mm});
            skLineSegment(sketch, "E2805", {"start": v(27634.8, 14193.35) * mm, "end": v(27104.39, 14113.26) * mm});
            skLineSegment(sketch, "E2806", {"start": v(26706.5, 13765.85) * mm, "end": v(26294.1, 13757.55) * mm});
            skLineSegment(sketch, "E2807", {"start": v(26148.06, 13753.4) * mm, "end": v(26147.5, 13755.62) * mm});
            skLineSegment(sketch, "E2808", {"start": v(27266.08, 13772.33) * mm, "end": v(27272.97, 13343.5) * mm});
            skLineSegment(sketch, "E2809", {"start": v(27266.08, 13772.33) * mm, "end": v(26706.5, 13765.85) * mm});
            skLineSegment(sketch, "E2810", {"start": v(26134.87, 13753.03) * mm, "end": v(26144.88, 13237.42) * mm});
            skLineSegment(sketch, "E2811", {"start": v(26144.88, 13237.42) * mm, "end": v(26161.47, 12546.34) * mm});
            skLineSegment(sketch, "E2812", {"start": v(26294.1, 13757.55) * mm, "end": v(26134.87, 13753.03) * mm});
            skLineSegment(sketch, "E2813", {"start": v(25178.03, 13880.63) * mm, "end": v(25127.92, 14208.9) * mm});
            skLineSegment(sketch, "E2814", {"start": v(25127.92, 14208.9) * mm, "end": v(24800.14, 14162.26) * mm});
            skLineSegment(sketch, "E2815", {"start": v(25167.91, 12957.78) * mm, "end": v(25178.03, 13880.63) * mm});
            skLineSegment(sketch, "E2816", {"start": v(25112.98, 12958.38) * mm, "end": v(25167.91, 12957.78) * mm});
            skLineSegment(sketch, "E2817", {"start": v(24800.14, 14162.26) * mm, "end": v(24668.91, 15004.64) * mm});
            skLineSegment(sketch, "E2818", {"start": v(24438.42, 14969.32) * mm, "end": v(24668.91, 15004.64) * mm});
            skLineSegment(sketch, "E2819", {"start": v(26718.12, 14054.34) * mm, "end": v(26383.82, 14002.9) * mm});
            skLineSegment(sketch, "E2820", {"start": v(27708.8, 14744.34) * mm, "end": v(27688.83, 14867.1) * mm});
            skLineSegment(sketch, "E2821", {"start": v(26383.82, 14002.9) * mm, "end": v(26311.8, 14476.42) * mm});
            skLineSegment(sketch, "E2822", {"start": v(26311.8, 14476.42) * mm, "end": v(26254.13, 14857.71) * mm});
            skLineSegment(sketch, "E2823", {"start": v(26254.13, 14857.71) * mm, "end": v(26192.16, 15269.97) * mm});
            skLineSegment(sketch, "E2824", {"start": v(26192.16, 15269.97) * mm, "end": v(26815.62, 15363.74) * mm});
            skLineSegment(sketch, "E2825", {"start": v(27717.28, 15665.7) * mm, "end": v(24410.2, 15150.5) * mm});
            skLineSegment(sketch, "E2826", {"start": v(28168.05, 13907.9) * mm, "end": v(27924.17, 15530.37) * mm});
            skLineSegment(sketch, "E2827", {"start": v(26411.65, 13822.03) * mm, "end": v(27962.82, 14060.67) * mm});
            skLineSegment(sketch, "E2828", {"start": v(26084.54, 12985.77) * mm, "end": v(25750.97, 15203.61) * mm});
            skLineSegment(sketch, "E2829", {"start": v(24410.2, 15150.5) * mm, "end": v(24438.42, 14969.32) * mm});
            skLineSegment(sketch, "E2830", {"start": v(27717.28, 15665.7) * mm, "end": v(27742.6, 15503.15) * mm});
            skLineSegment(sketch, "E2831", {"start": v(25750.97, 15203.61) * mm, "end": v(25981.37, 15238.27) * mm});
            skLineSegment(sketch, "E2832", {"start": v(26411.65, 13822.03) * mm, "end": v(26383.82, 14002.9) * mm});
            skLineSegment(sketch, "E2833", {"start": v(27962.82, 14060.67) * mm, "end": v(27934.99, 14241.54) * mm});
            skLineSegment(sketch, "E2834", {"start": v(27924.17, 15530.37) * mm, "end": v(27742.6, 15503.15) * mm});
            skLineSegment(sketch, "E2835", {"start": v(28168.05, 13907.9) * mm, "end": v(27986.48, 13880.69) * mm});
            skLineSegment(sketch, "E2836", {"start": v(26098.72, 12989.01) * mm, "end": v(26154.85, 12997.46) * mm});
            skFitSpline(sketch, "E2837", {"points": [v(-8590.23, 9450.41) * mm, v(-8545.16, 9427.62) * mm, v(-8453.88, 9381.46) * mm, v(-8294.54, 9335.91) * mm, v(-8182.69, 9311.06) * mm, v(-8121.23, 9297.41) * mm]});
            skFitSpline(sketch, "E2838", {"points": [v(-13802.23, 7957.41) * mm, v(-13767.61, 7957.94) * mm, v(-13669.6, 7959.42) * mm, v(-13554.84, 8114.03) * mm, v(-13644.31, 8257.14) * mm, v(-13740.23, 8290.32) * mm, v(-13787.84, 8288.95) * mm, v(-13806.23, 8288.41) * mm]});
            skFitSpline(sketch, "E2839", {"points": [v(-13802.73, 7988.44) * mm, v(-13799.87, 7988.48) * mm, v(-13794.2, 7988.57) * mm, v(-13785.8, 7988.74) * mm, v(-13777.57, 7988.98) * mm, v(-13769.53, 7989.35) * mm, v(-13761.69, 7989.86) * mm, v(-13754.05, 7990.56) * mm, v(-13746.64, 7991.47) * mm, v(-13739.46, 7992.61) * mm, v(-13732.5, 7994.02) * mm, v(-13725.77, 7995.72) * mm, v(-13719.38, 7997.7) * mm, v(-13711.24, 8000.73) * mm, v(-13701.5, 8005.37) * mm, v(-13690.27, 8012.2) * mm, v(-13679.52, 8020.26) * mm, v(-13669.3, 8029.47) * mm, v(-13659.81, 8039.69) * mm, v(-13651.2, 8050.73) * mm, v(-13643.6, 8062.44) * mm, v(-13637.17, 8074.62) * mm, v(-13632.02, 8087.08) * mm, v(-13628.24, 8099.64) * mm, v(-13625.9, 8112.2) * mm, v(-13625.1, 8123.84) * mm, v(-13625.6, 8134.62) * mm, v(-13627.06, 8144.58) * mm, v(-13629.49, 8154.59) * mm, v(-13632.84, 8164.54) * mm, v(-13637.1, 8174.35) * mm, v(-13642.19, 8183.94) * mm, v(-13648.06, 8193.21) * mm, v(-13654.65, 8202.08) * mm, v(-13661.89, 8210.46) * mm, v(-13669.68, 8218.27) * mm, v(-13678.02, 8225.48) * mm, v(-13685.49, 8231.02) * mm, v(-13691.91, 8235.21) * mm, v(-13697.1, 8238.27) * mm, v(-13702.46, 8241.14) * mm, v(-13707.93, 8243.78) * mm, v(-13713.52, 8246.2) * mm, v(-13719.2, 8248.37) * mm, v(-13724.95, 8250.32) * mm, v(-13730.8, 8252.04) * mm, v(-13736.7, 8253.53) * mm, v(-13742.67, 8254.79) * mm, v(-13748.72, 8255.82) * mm, v(-13754.03, 8256.53) * mm, v(-13758.65, 8257) * mm, v(-13762.53, 8257.3) * mm, v(-13766.52, 8257.54) * mm, v(-13770.58, 8257.71) * mm, v(-13774.7, 8257.82) * mm, v(-13778.89, 8257.87) * mm, v(-13783.14, 8257.87) * mm, v(-13787.46, 8257.83) * mm, v(-13791.84, 8257.76) * mm, v(-13796.3, 8257.65) * mm, v(-13800.8, 8257.53) * mm, v(-13803.82, 8257.44) * mm, v(-13805.35, 8257.4) * mm]});
            skFitSpline(sketch, "E2840", {"points": [v(-14317.23, 8846.41) * mm, v(-14317.29, 8846.78) * mm, v(-14317.4, 8847.5) * mm, v(-14317.56, 8848.58) * mm, v(-14317.72, 8849.67) * mm, v(-14317.89, 8850.75) * mm, v(-14318.06, 8851.82) * mm, v(-14318.23, 8852.9) * mm, v(-14318.42, 8853.96) * mm, v(-14318.6, 8855.01) * mm, v(-14318.8, 8856.06) * mm, v(-14319.02, 8857.1) * mm, v(-14319.24, 8858.13) * mm, v(-14319.48, 8859.15) * mm, v(-14319.72, 8860.16) * mm, v(-14319.99, 8861.15) * mm, v(-14320.26, 8862.13) * mm, v(-14320.56, 8863.1) * mm, v(-14320.87, 8864.04) * mm, v(-14321.2, 8864.97) * mm, v(-14321.55, 8865.89) * mm, v(-14321.93, 8866.78) * mm, v(-14322.32, 8867.66) * mm, v(-14322.74, 8868.5) * mm, v(-14323.18, 8869.34) * mm, v(-14323.65, 8870.15) * mm, v(-14324.15, 8870.93) * mm, v(-14324.68, 8871.69) * mm, v(-14325.23, 8872.42) * mm, v(-14325.8, 8873.11) * mm, v(-14326.41, 8873.78) * mm, v(-14327.05, 8874.43) * mm, v(-14327.7, 8875.05) * mm, v(-14328.4, 8875.65) * mm, v(-14329.1, 8876.22) * mm, v(-14329.84, 8876.77) * mm, v(-14330.6, 8877.3) * mm, v(-14331.39, 8877.8) * mm, v(-14332.2, 8878.3) * mm, v(-14333.02, 8878.77) * mm, v(-14333.87, 8879.22) * mm, v(-14334.74, 8879.65) * mm, v(-14335.63, 8880.07) * mm, v(-14336.53, 8880.47) * mm, v(-14337.45, 8880.85) * mm, v(-14338.39, 8881.22) * mm, v(-14339.34, 8881.58) * mm, v(-14340.31, 8881.92) * mm, v(-14341.3, 8882.25) * mm, v(-14342.29, 8882.57) * mm, v(-14343.3, 8882.87) * mm, v(-14344.31, 8883.17) * mm, v(-14345.35, 8883.46) * mm, v(-14346.38, 8883.73) * mm, v(-14347.43, 8884) * mm, v(-14348.5, 8884.27) * mm, v(-14349.55, 8884.52) * mm, v(-14350.62, 8884.77) * mm, v(-14351.7, 8885.02) * mm, v(-14352.78, 8885.26) * mm, v(-14353.87, 8885.5) * mm, v(-14354.96, 8885.73) * mm, v(-14356.05, 8885.96) * mm, v(-14357.14, 8886.19) * mm, v(-14357.87, 8886.34) * mm, v(-14358.23, 8886.41) * mm]});
            skFitSpline(sketch, "E2841", {"points": [v(-14445.47, 8846.41) * mm, v(-14445.41, 8846.78) * mm, v(-14445.3, 8847.5) * mm, v(-14445.15, 8848.58) * mm, v(-14444.98, 8849.67) * mm, v(-14444.81, 8850.75) * mm, v(-14444.64, 8851.82) * mm, v(-14444.47, 8852.9) * mm, v(-14444.28, 8853.96) * mm, v(-14444.1, 8855.01) * mm, v(-14443.9, 8856.06) * mm, v(-14443.68, 8857.1) * mm, v(-14443.46, 8858.13) * mm, v(-14443.22, 8859.15) * mm, v(-14442.98, 8860.16) * mm, v(-14442.72, 8861.15) * mm, v(-14442.44, 8862.13) * mm, v(-14442.14, 8863.1) * mm, v(-14441.83, 8864.04) * mm, v(-14441.5, 8864.97) * mm, v(-14441.15, 8865.89) * mm, v(-14440.78, 8866.78) * mm, v(-14440.38, 8867.66) * mm, v(-14439.96, 8868.5) * mm, v(-14439.52, 8869.34) * mm, v(-14439.05, 8870.15) * mm, v(-14438.55, 8870.93) * mm, v(-14438.03, 8871.69) * mm, v(-14437.47, 8872.42) * mm, v(-14436.9, 8873.11) * mm, v(-14436.29, 8873.78) * mm, v(-14435.66, 8874.43) * mm, v(-14435, 8875.05) * mm, v(-14434.3, 8875.65) * mm, v(-14433.6, 8876.22) * mm, v(-14432.86, 8876.77) * mm, v(-14432.1, 8877.3) * mm, v(-14431.31, 8877.8) * mm, v(-14430.5, 8878.3) * mm, v(-14429.68, 8878.77) * mm, v(-14428.83, 8879.22) * mm, v(-14427.96, 8879.65) * mm, v(-14427.08, 8880.07) * mm, v(-14426.17, 8880.47) * mm, v(-14425.25, 8880.85) * mm, v(-14424.31, 8881.22) * mm, v(-14423.36, 8881.58) * mm, v(-14422.4, 8881.92) * mm, v(-14421.4, 8882.25) * mm, v(-14420.41, 8882.57) * mm, v(-14419.4, 8882.87) * mm, v(-14418.39, 8883.17) * mm, v(-14417.36, 8883.46) * mm, v(-14416.32, 8883.73) * mm, v(-14415.27, 8884) * mm, v(-14414.21, 8884.27) * mm, v(-14413.15, 8884.52) * mm, v(-14412.08, 8884.77) * mm, v(-14411, 8885.02) * mm, v(-14409.92, 8885.26) * mm, v(-14408.83, 8885.5) * mm, v(-14407.74, 8885.73) * mm, v(-14406.65, 8885.96) * mm, v(-14405.56, 8886.19) * mm, v(-14404.83, 8886.34) * mm, v(-14404.47, 8886.41) * mm]});
            skFitSpline(sketch, "E2842", {"points": [v(-15072.23, 9268.41) * mm, v(-15066.95, 9254.93) * mm, v(-15055.86, 9226.65) * mm, v(-15026.56, 9217.96) * mm, v(-15011.23, 9213.41) * mm]});
            skFitSpline(sketch, "E2843", {"points": [v(-20598.23, 12705.41) * mm, v(-20535.5, 12691.65) * mm, v(-20408.34, 12663.75) * mm, v(-20245.07, 12671.5) * mm, v(-20146.8, 12674.72) * mm, v(-20114, 12675.8) * mm, v(-20113.88, 12675.8) * mm]});
            skFitSpline(sketch, "E2844", {"points": [v(-20162.35, 14091.81) * mm, v(-20184.68, 14131.58) * mm, v(-20234.61, 14220.52) * mm, v(-20406.2, 14221.24) * mm, v(-20574.94, 14208.3) * mm, v(-20630.45, 14114.1) * mm, v(-20653.23, 14075.41) * mm]});
            skFitSpline(sketch, "E2845", {"points": [v(21658.23, -5147.64) * mm, v(21631.94, -5093.76) * mm, v(21591.9, -5011.73) * mm, v(21512.65, -5037.68) * mm, v(21485.44, -5046.59) * mm]});
            skFitSpline(sketch, "E2846", {"points": [v(-11727.72, -6162.59) * mm, v(-11727.58, -6162.34) * mm, v(-11727.32, -6161.84) * mm, v(-11726.93, -6161.1) * mm, v(-11726.53, -6160.36) * mm, v(-11726.14, -6159.62) * mm, v(-11725.74, -6158.88) * mm, v(-11725.34, -6158.14) * mm, v(-11724.95, -6157.4) * mm, v(-11724.55, -6156.66) * mm, v(-11724.16, -6155.92) * mm, v(-11723.76, -6155.18) * mm, v(-11723.37, -6154.44) * mm, v(-11722.97, -6153.7) * mm, v(-11722.57, -6152.96) * mm, v(-11722.18, -6152.22) * mm, v(-11721.78, -6151.49) * mm, v(-11721.38, -6150.75) * mm, v(-11720.99, -6150.01) * mm, v(-11720.59, -6149.27) * mm, v(-11720.2, -6148.54) * mm, v(-11719.8, -6147.8) * mm, v(-11719.4, -6147.07) * mm, v(-11719, -6146.33) * mm, v(-11718.6, -6145.6) * mm, v(-11718.2, -6144.86) * mm, v(-11717.8, -6144.13) * mm, v(-11717.4, -6143.4) * mm, v(-11717, -6142.66) * mm, v(-11716.6, -6141.93) * mm, v(-11716.2, -6141.2) * mm, v(-11715.79, -6140.47) * mm, v(-11715.39, -6139.74) * mm, v(-11714.99, -6139.02) * mm, v(-11714.58, -6138.29) * mm, v(-11714.18, -6137.56) * mm, v(-11713.77, -6136.83) * mm, v(-11713.37, -6136.1) * mm, v(-11712.96, -6135.39) * mm, v(-11712.56, -6134.66) * mm, v(-11712.15, -6133.94) * mm, v(-11711.74, -6133.22) * mm, v(-11711.33, -6132.5) * mm, v(-11710.92, -6131.78) * mm, v(-11710.51, -6131.06) * mm, v(-11710.1, -6130.35) * mm, v(-11709.7, -6129.63) * mm, v(-11709.28, -6128.92) * mm, v(-11708.87, -6128.2) * mm, v(-11708.45, -6127.49) * mm, v(-11708.04, -6126.78) * mm, v(-11707.62, -6126.07) * mm, v(-11707.2, -6125.36) * mm, v(-11706.8, -6124.65) * mm, v(-11706.37, -6123.95) * mm, v(-11705.96, -6123.24) * mm, v(-11705.54, -6122.54) * mm, v(-11705.12, -6121.84) * mm, v(-11704.7, -6121.14) * mm, v(-11704.27, -6120.44) * mm, v(-11703.85, -6119.74) * mm, v(-11703.43, -6119.05) * mm, v(-11703, -6118.35) * mm, v(-11702.58, -6117.66) * mm, v(-11702.15, -6116.97) * mm, v(-11701.72, -6116.28) * mm, v(-11701.3, -6115.6) * mm, v(-11700.86, -6114.9) * mm, v(-11700.43, -6114.22) * mm, v(-11700, -6113.54) * mm, v(-11699.57, -6112.85) * mm, v(-11699.13, -6112.17) * mm, v(-11698.7, -6111.5) * mm, v(-11698.26, -6110.82) * mm, v(-11697.82, -6110.15) * mm, v(-11697.38, -6109.48) * mm, v(-11696.94, -6108.8) * mm, v(-11696.5, -6108.13) * mm, v(-11696.06, -6107.47) * mm, v(-11695.61, -6106.8) * mm, v(-11695.17, -6106.14) * mm, v(-11694.72, -6105.48) * mm, v(-11694.28, -6104.82) * mm, v(-11693.83, -6104.17) * mm, v(-11693.37, -6103.51) * mm, v(-11692.92, -6102.86) * mm, v(-11692.47, -6102.2) * mm, v(-11692.02, -6101.56) * mm, v(-11691.56, -6100.92) * mm, v(-11691.1, -6100.27) * mm, v(-11690.64, -6099.63) * mm, v(-11690.18, -6099) * mm, v(-11689.72, -6098.35) * mm, v(-11689.26, -6097.72) * mm, v(-11688.8, -6097.09) * mm, v(-11688.33, -6096.46) * mm, v(-11687.86, -6095.83) * mm, v(-11687.4, -6095.2) * mm, v(-11686.92, -6094.58) * mm, v(-11686.45, -6093.96) * mm, v(-11685.97, -6093.35) * mm, v(-11685.5, -6092.73) * mm, v(-11685.02, -6092.12) * mm, v(-11684.54, -6091.5) * mm, v(-11684.06, -6090.9) * mm, v(-11683.58, -6090.3) * mm, v(-11683.07, -6089.66) * mm, v(-11682.53, -6089) * mm, v(-11681.96, -6088.3) * mm, v(-11681.4, -6087.6) * mm, v(-11680.82, -6086.92) * mm, v(-11680.24, -6086.24) * mm, v(-11679.66, -6085.55) * mm, v(-11679.08, -6084.88) * mm, v(-11678.5, -6084.2) * mm, v(-11677.91, -6083.54) * mm, v(-11677.32, -6082.87) * mm, v(-11676.73, -6082.21) * mm, v(-11676.14, -6081.56) * mm, v(-11675.54, -6080.9) * mm, v(-11674.94, -6080.26) * mm, v(-11674.34, -6079.61) * mm, v(-11673.74, -6078.97) * mm, v(-11673.13, -6078.34) * mm, v(-11672.51, -6077.7) * mm, v(-11671.9, -6077.08) * mm, v(-11671.29, -6076.46) * mm, v(-11670.67, -6075.84) * mm, v(-11670.05, -6075.23) * mm, v(-11669.42, -6074.62) * mm, v(-11668.8, -6074.01) * mm, v(-11668.17, -6073.41) * mm, v(-11667.53, -6072.82) * mm, v(-11666.9, -6072.23) * mm, v(-11666.26, -6071.64) * mm, v(-11665.62, -6071.06) * mm, v(-11664.97, -6070.48) * mm, v(-11664.32, -6069.91) * mm, v(-11663.67, -6069.35) * mm, v(-11663.02, -6068.79) * mm, v(-11662.36, -6068.23) * mm, v(-11661.7, -6067.68) * mm, v(-11661.03, -6067.13) * mm, v(-11660.37, -6066.59) * mm, v(-11659.7, -6066.05) * mm, v(-11659.02, -6065.52) * mm, v(-11658.34, -6065) * mm, v(-11657.66, -6064.47) * mm, v(-11656.98, -6063.96) * mm, v(-11656.3, -6063.45) * mm, v(-11655.6, -6062.95) * mm, v(-11654.9, -6062.45) * mm, v(-11654.2, -6061.95) * mm, v(-11653.5, -6061.46) * mm, v(-11652.8, -6060.98) * mm, v(-11652.1, -6060.5) * mm, v(-11651.4, -6060.04) * mm, v(-11650.68, -6059.58) * mm, v(-11649.97, -6059.12) * mm, v(-11649.25, -6058.67) * mm, v(-11648.53, -6058.22) * mm, v(-11647.8, -6057.78) * mm, v(-11647.08, -6057.34) * mm, v(-11646.35, -6056.91) * mm, v(-11645.62, -6056.49) * mm, v(-11644.88, -6056.07) * mm, v(-11644.14, -6055.65) * mm, v(-11643.4, -6055.24) * mm, v(-11642.65, -6054.84) * mm, v(-11641.9, -6054.44) * mm, v(-11641.15, -6054.04) * mm, v(-11640.4, -6053.66) * mm, v(-11639.63, -6053.27) * mm, v(-11638.87, -6052.9) * mm, v(-11638.1, -6052.52) * mm, v(-11637.33, -6052.15) * mm, v(-11636.56, -6051.78) * mm, v(-11635.79, -6051.42) * mm, v(-11635.01, -6051.07) * mm, v(-11634.23, -6050.72) * mm, v(-11633.45, -6050.37) * mm, v(-11632.66, -6050.03) * mm, v(-11631.87, -6049.7) * mm, v(-11631.08, -6049.36) * mm, v(-11630.28, -6049.04) * mm, v(-11629.49, -6048.71) * mm, v(-11628.68, -6048.4) * mm, v(-11627.88, -6048.08) * mm, v(-11627.07, -6047.77) * mm, v(-11626.27, -6047.47) * mm, v(-11625.45, -6047.17) * mm, v(-11624.64, -6046.87) * mm, v(-11623.82, -6046.58) * mm, v(-11623, -6046.3) * mm, v(-11622.18, -6046.01) * mm, v(-11621.35, -6045.74) * mm, v(-11620.53, -6045.46) * mm, v(-11619.7, -6045.2) * mm, v(-11618.86, -6044.93) * mm, v(-11618.02, -6044.67) * mm, v(-11617.18, -6044.41) * mm, v(-11616.34, -6044.16) * mm, v(-11615.5, -6043.91) * mm, v(-11614.66, -6043.67) * mm, v(-11613.8, -6043.42) * mm, v(-11612.95, -6043.19) * mm, v(-11612.1, -6042.96) * mm, v(-11611.25, -6042.73) * mm, v(-11610.39, -6042.5) * mm, v(-11609.53, -6042.28) * mm, v(-11608.67, -6042.07) * mm, v(-11607.8, -6041.85) * mm, v(-11606.93, -6041.65) * mm, v(-11606.06, -6041.44) * mm, v(-11605.2, -6041.24) * mm, v(-11604.32, -6041.04) * mm, v(-11603.44, -6040.85) * mm, v(-11602.56, -6040.66) * mm, v(-11601.68, -6040.47) * mm, v(-11600.8, -6040.29) * mm, v(-11599.96, -6040.12) * mm, v(-11599.16, -6039.96) * mm, v(-11598.4, -6039.8) * mm, v(-11597.63, -6039.66) * mm, v(-11596.87, -6039.52) * mm, v(-11596.1, -6039.38) * mm, v(-11595.34, -6039.24) * mm, v(-11594.57, -6039.1) * mm, v(-11593.8, -6038.97) * mm, v(-11593.02, -6038.84) * mm, v(-11592.25, -6038.71) * mm, v(-11591.47, -6038.59) * mm, v(-11590.7, -6038.46) * mm, v(-11589.92, -6038.34) * mm, v(-11589.15, -6038.22) * mm, v(-11588.37, -6038.1) * mm, v(-11587.58, -6038) * mm, v(-11586.8, -6037.88) * mm, v(-11586.01, -6037.77) * mm, v(-11585.23, -6037.67) * mm, v(-11584.45, -6037.56) * mm, v(-11583.66, -6037.46) * mm, v(-11582.87, -6037.36) * mm, v(-11582.08, -6037.26) * mm, v(-11581.28, -6037.16) * mm, v(-11580.5, -6037.07) * mm, v(-11579.7, -6036.98) * mm, v(-11578.9, -6036.9) * mm, v(-11578.11, -6036.8) * mm, v(-11577.31, -6036.72) * mm, v(-11576.51, -6036.63) * mm, v(-11575.71, -6036.55) * mm, v(-11574.91, -6036.47) * mm, v(-11574.1, -6036.4) * mm, v(-11573.3, -6036.32) * mm, v(-11572.5, -6036.25) * mm, v(-11571.7, -6036.18) * mm, v(-11570.9, -6036.1) * mm, v(-11570.08, -6036.04) * mm, v(-11569.27, -6035.98) * mm, v(-11568.47, -6035.91) * mm, v(-11567.66, -6035.85) * mm, v(-11566.85, -6035.8) * mm, v(-11566.03, -6035.73) * mm, v(-11565.22, -6035.68) * mm, v(-11564.4, -6035.62) * mm, v(-11563.59, -6035.57) * mm, v(-11562.77, -6035.52) * mm, v(-11561.96, -6035.47) * mm, v(-11561.14, -6035.43) * mm, v(-11560.32, -6035.38) * mm, v(-11559.5, -6035.34) * mm, v(-11558.68, -6035.3) * mm, v(-11557.86, -6035.25) * mm, v(-11557.04, -6035.21) * mm, v(-11556.22, -6035.18) * mm, v(-11555.4, -6035.14) * mm, v(-11554.57, -6035.1) * mm, v(-11553.74, -6035.08) * mm, v(-11552.92, -6035.04) * mm, v(-11552.1, -6035.02) * mm, v(-11551.26, -6034.99) * mm, v(-11550.44, -6034.96) * mm, v(-11549.6, -6034.94) * mm, v(-11548.78, -6034.91) * mm, v(-11547.95, -6034.9) * mm, v(-11547.12, -6034.87) * mm, v(-11546.28, -6034.85) * mm, v(-11545.45, -6034.83) * mm, v(-11544.62, -6034.82) * mm, v(-11543.79, -6034.8) * mm, v(-11542.96, -6034.79) * mm, v(-11542.12, -6034.78) * mm, v(-11541.28, -6034.76) * mm, v(-11540.45, -6034.75) * mm, v(-11539.61, -6034.75) * mm, v(-11538.78, -6034.74) * mm, v(-11537.94, -6034.73) * mm, v(-11537.1, -6034.73) * mm, v(-11536.26, -6034.72) * mm, v(-11535.43, -6034.72) * mm, v(-11534.59, -6034.72) * mm, v(-11533.75, -6034.72) * mm, v(-11532.9, -6034.72) * mm, v(-11532.07, -6034.72) * mm, v(-11531.23, -6034.72) * mm, v(-11530.39, -6034.73) * mm, v(-11529.54, -6034.73) * mm, v(-11528.7, -6034.74) * mm, v(-11527.86, -6034.75) * mm, v(-11527.02, -6034.75) * mm, v(-11526.18, -6034.76) * mm, v(-11525.33, -6034.77) * mm, v(-11524.49, -6034.78) * mm, v(-11523.65, -6034.8) * mm, v(-11522.8, -6034.8) * mm, v(-11521.96, -6034.82) * mm, v(-11521.11, -6034.84) * mm, v(-11520.27, -6034.85) * mm, v(-11519.42, -6034.87) * mm, v(-11518.58, -6034.88) * mm, v(-11517.73, -6034.9) * mm, v(-11516.89, -6034.92) * mm, v(-11516.04, -6034.94) * mm, v(-11515.2, -6034.96) * mm, v(-11514.35, -6034.98) * mm, v(-11513.5, -6035) * mm, v(-11512.66, -6035.02) * mm, v(-11511.81, -6035.04) * mm, v(-11510.97, -6035.07) * mm, v(-11510.12, -6035.09) * mm, v(-11509.28, -6035.11) * mm, v(-11508.43, -6035.14) * mm, v(-11507.58, -6035.16) * mm, v(-11506.74, -6035.19) * mm, v(-11505.9, -6035.21) * mm, v(-11505.04, -6035.24) * mm, v(-11504.2, -6035.27) * mm, v(-11503.35, -6035.3) * mm, v(-11502.5, -6035.33) * mm, v(-11501.65, -6035.35) * mm, v(-11500.79, -6035.38) * mm, v(-11499.93, -6035.41) * mm, v(-11499.07, -6035.44) * mm, v(-11498.2, -6035.47) * mm, v(-11497.35, -6035.5) * mm, v(-11496.49, -6035.54) * mm, v(-11495.63, -6035.57) * mm, v(-11494.77, -6035.6) * mm, v(-11493.9, -6035.64) * mm, v(-11493.05, -6035.67) * mm, v(-11492.2, -6035.7) * mm, v(-11491.33, -6035.74) * mm, v(-11490.47, -6035.78) * mm, v(-11489.62, -6035.81) * mm, v(-11488.76, -6035.85) * mm, v(-11487.9, -6035.89) * mm, v(-11487.04, -6035.93) * mm, v(-11486.19, -6035.97) * mm, v(-11485.33, -6036) * mm, v(-11484.47, -6036.05) * mm, v(-11483.62, -6036.09) * mm, v(-11482.76, -6036.13) * mm, v(-11481.9, -6036.17) * mm, v(-11481.05, -6036.22) * mm, v(-11480.2, -6036.26) * mm, v(-11479.34, -6036.3) * mm, v(-11478.49, -6036.35) * mm, v(-11477.63, -6036.4) * mm, v(-11476.78, -6036.45) * mm, v(-11475.93, -6036.5) * mm, v(-11475.07, -6036.54) * mm, v(-11474.22, -6036.6) * mm, v(-11473.37, -6036.64) * mm, v(-11472.52, -6036.7) * mm, v(-11471.66, -6036.75) * mm, v(-11470.81, -6036.8) * mm, v(-11469.96, -6036.86) * mm, v(-11469.11, -6036.91) * mm, v(-11468.27, -6036.97) * mm, v(-11467.42, -6037.03) * mm, v(-11466.57, -6037.08) * mm, v(-11465.72, -6037.14) * mm, v(-11464.87, -6037.2) * mm, v(-11464.02, -6037.27) * mm, v(-11463.18, -6037.33) * mm, v(-11462.33, -6037.4) * mm, v(-11461.49, -6037.46) * mm, v(-11460.64, -6037.52) * mm, v(-11459.8, -6037.59) * mm, v(-11458.96, -6037.66) * mm, v(-11458.11, -6037.72) * mm, v(-11457.27, -6037.8) * mm, v(-11456.43, -6037.87) * mm, v(-11455.58, -6037.94) * mm, v(-11454.74, -6038.01) * mm, v(-11453.9, -6038.09) * mm, v(-11453.07, -6038.16) * mm, v(-11452.23, -6038.24) * mm, v(-11451.4, -6038.32) * mm, v(-11450.55, -6038.4) * mm, v(-11449.71, -6038.48) * mm, v(-11448.88, -6038.56) * mm, v(-11448.04, -6038.64) * mm, v(-11447.2, -6038.73) * mm, v(-11446.38, -6038.81) * mm, v(-11445.54, -6038.9) * mm, v(-11444.71, -6038.99) * mm, v(-11443.88, -6039.08) * mm, v(-11443.05, -6039.17) * mm, v(-11442.22, -6039.26) * mm, v(-11441.39, -6039.35) * mm, v(-11440.56, -6039.45) * mm, v(-11439.73, -6039.54) * mm, v(-11438.9, -6039.64) * mm, v(-11438.08, -6039.74) * mm, v(-11437.25, -6039.84) * mm, v(-11436.43, -6039.94) * mm, v(-11435.6, -6040.05) * mm, v(-11434.78, -6040.15) * mm, v(-11433.96, -6040.26) * mm, v(-11433.14, -6040.37) * mm, v(-11432.32, -6040.48) * mm, v(-11431.5, -6040.59) * mm, v(-11430.68, -6040.7) * mm, v(-11429.87, -6040.82) * mm, v(-11429.05, -6040.93) * mm, v(-11428.24, -6041.05) * mm, v(-11427.42, -6041.17) * mm, v(-11426.6, -6041.29) * mm, v(-11425.8, -6041.41) * mm, v(-11424.98, -6041.54) * mm, v(-11424.17, -6041.66) * mm, v(-11423.36, -6041.79) * mm, v(-11422.55, -6041.92) * mm, v(-11421.75, -6042.05) * mm, v(-11420.94, -6042.18) * mm, v(-11420.13, -6042.31) * mm, v(-11419.33, -6042.45) * mm, v(-11418.53, -6042.59) * mm, v(-11417.73, -6042.73) * mm, v(-11416.93, -6042.87) * mm, v(-11416.12, -6043) * mm, v(-11415.32, -6043.15) * mm, v(-11414.53, -6043.3) * mm, v(-11413.73, -6043.45) * mm, v(-11412.94, -6043.6) * mm, v(-11412.14, -6043.75) * mm, v(-11411.35, -6043.9) * mm, v(-11410.56, -6044.06) * mm, v(-11409.76, -6044.22) * mm, v(-11408.97, -6044.38) * mm, v(-11408.19, -6044.54) * mm, v(-11407.4, -6044.7) * mm, v(-11406.61, -6044.86) * mm, v(-11405.83, -6045.03) * mm, v(-11405.05, -6045.2) * mm, v(-11404.26, -6045.37) * mm, v(-11403.48, -6045.54) * mm, v(-11402.7, -6045.72) * mm, v(-11401.92, -6045.9) * mm, v(-11401.15, -6046.08) * mm, v(-11400.37, -6046.26) * mm, v(-11399.6, -6046.44) * mm, v(-11398.82, -6046.62) * mm, v(-11398.05, -6046.81) * mm, v(-11397.28, -6047) * mm, v(-11396.5, -6047.2) * mm, v(-11395.74, -6047.39) * mm, v(-11394.98, -6047.58) * mm, v(-11394.2, -6047.78) * mm, v(-11393.44, -6047.98) * mm, v(-11392.68, -6048.18) * mm, v(-11391.92, -6048.39) * mm, v(-11391.16, -6048.6) * mm, v(-11390.4, -6048.8) * mm, v(-11389.65, -6049.01) * mm, v(-11388.9, -6049.22) * mm, v(-11388.14, -6049.44) * mm, v(-11387.38, -6049.66) * mm, v(-11386.63, -6049.88) * mm, v(-11385.88, -6050.1) * mm, v(-11385.14, -6050.32) * mm, v(-11384.4, -6050.55) * mm, v(-11383.65, -6050.78) * mm, v(-11382.9, -6051.01) * mm, v(-11382.16, -6051.25) * mm, v(-11381.42, -6051.48) * mm, v(-11380.68, -6051.72) * mm, v(-11379.94, -6051.96) * mm, v(-11379.2, -6052.2) * mm, v(-11378.47, -6052.45) * mm, v(-11377.74, -6052.7) * mm, v(-11376.97, -6052.97) * mm, v(-11376.16, -6053.25) * mm, v(-11375.31, -6053.55) * mm, v(-11374.47, -6053.85) * mm, v(-11373.62, -6054.15) * mm, v(-11372.78, -6054.46) * mm, v(-11371.94, -6054.78) * mm, v(-11371.1, -6055.1) * mm, v(-11370.27, -6055.41) * mm, v(-11369.44, -6055.74) * mm, v(-11368.6, -6056.06) * mm, v(-11367.78, -6056.4) * mm, v(-11366.95, -6056.73) * mm, v(-11366.13, -6057.06) * mm, v(-11365.3, -6057.4) * mm, v(-11364.5, -6057.75) * mm, v(-11363.67, -6058.1) * mm, v(-11362.86, -6058.45) * mm, v(-11362.05, -6058.8) * mm, v(-11361.24, -6059.17) * mm, v(-11360.44, -6059.53) * mm, v(-11359.63, -6059.9) * mm, v(-11358.83, -6060.27) * mm, v(-11358.03, -6060.64) * mm, v(-11357.24, -6061.02) * mm, v(-11356.44, -6061.4) * mm, v(-11355.65, -6061.79) * mm, v(-11354.87, -6062.18) * mm, v(-11354.08, -6062.57) * mm, v(-11353.3, -6062.97) * mm, v(-11352.52, -6063.37) * mm, v(-11351.74, -6063.78) * mm, v(-11350.96, -6064.2) * mm, v(-11350.2, -6064.6) * mm, v(-11349.42, -6065.02) * mm, v(-11348.66, -6065.44) * mm, v(-11347.9, -6065.87) * mm, v(-11347.13, -6066.3) * mm, v(-11346.37, -6066.74) * mm, v(-11345.62, -6067.17) * mm, v(-11344.87, -6067.62) * mm, v(-11344.12, -6068.06) * mm, v(-11343.37, -6068.51) * mm, v(-11342.62, -6068.97) * mm, v(-11341.88, -6069.43) * mm, v(-11341.15, -6069.9) * mm, v(-11340.41, -6070.36) * mm, v(-11339.68, -6070.83) * mm, v(-11338.95, -6071.31) * mm, v(-11338.22, -6071.8) * mm, v(-11337.5, -6072.28) * mm, v(-11336.78, -6072.77) * mm, v(-11336.06, -6073.26) * mm, v(-11335.35, -6073.76) * mm, v(-11334.63, -6074.26) * mm, v(-11333.92, -6074.77) * mm, v(-11333.22, -6075.28) * mm, v(-11332.52, -6075.8) * mm, v(-11331.82, -6076.32) * mm, v(-11331.12, -6076.85) * mm, v(-11330.43, -6077.38) * mm, v(-11329.75, -6077.9) * mm, v(-11329.06, -6078.44) * mm, v(-11328.39, -6078.98) * mm, v(-11327.71, -6079.53) * mm, v(-11327.04, -6080.07) * mm, v(-11326.37, -6080.63) * mm, v(-11325.7, -6081.18) * mm, v(-11325.04, -6081.75) * mm, v(-11324.38, -6082.31) * mm, v(-11323.73, -6082.88) * mm, v(-11323.07, -6083.45) * mm, v(-11322.42, -6084.03) * mm, v(-11321.77, -6084.61) * mm, v(-11321.13, -6085.2) * mm, v(-11320.48, -6085.8) * mm, v(-11319.84, -6086.39) * mm, v(-11319.2, -6086.98) * mm, v(-11318.57, -6087.59) * mm, v(-11317.94, -6088.2) * mm, v(-11317.31, -6088.8) * mm, v(-11316.68, -6089.42) * mm, v(-11316.06, -6090.03) * mm, v(-11315.44, -6090.66) * mm, v(-11315.03, -6091.07) * mm, v(-11314.82, -6091.28) * mm]});
            skFitSpline(sketch, "E2847", {"points": [v(-11314.82, -6091.28) * mm, v(-11314.56, -6091.51) * mm, v(-11314.05, -6091.98) * mm, v(-11313.27, -6092.68) * mm, v(-11312.5, -6093.37) * mm, v(-11311.72, -6094.07) * mm, v(-11310.94, -6094.77) * mm, v(-11310.17, -6095.47) * mm, v(-11309.4, -6096.17) * mm, v(-11308.62, -6096.87) * mm, v(-11307.85, -6097.57) * mm, v(-11307.08, -6098.27) * mm, v(-11306.31, -6098.98) * mm, v(-11305.55, -6099.68) * mm, v(-11304.78, -6100.39) * mm, v(-11304.02, -6101.1) * mm, v(-11303.26, -6101.8) * mm, v(-11302.5, -6102.52) * mm, v(-11301.74, -6103.23) * mm, v(-11300.99, -6103.94) * mm, v(-11300.24, -6104.66) * mm, v(-11299.49, -6105.38) * mm, v(-11298.74, -6106.1) * mm, v(-11298, -6106.82) * mm, v(-11297.26, -6107.54) * mm, v(-11296.53, -6108.27) * mm, v(-11295.8, -6109) * mm, v(-11295.07, -6109.74) * mm, v(-11294.34, -6110.47) * mm, v(-11293.62, -6111.2) * mm, v(-11292.9, -6111.95) * mm, v(-11292.2, -6112.7) * mm, v(-11291.49, -6113.44) * mm, v(-11290.79, -6114.2) * mm, v(-11290.09, -6114.95) * mm, v(-11289.4, -6115.7) * mm, v(-11288.7, -6116.47) * mm, v(-11288.03, -6117.24) * mm, v(-11287.35, -6118) * mm, v(-11286.68, -6118.78) * mm, v(-11286.01, -6119.56) * mm, v(-11285.35, -6120.34) * mm, v(-11284.7, -6121.13) * mm, v(-11284.05, -6121.92) * mm, v(-11283.4, -6122.72) * mm, v(-11282.77, -6123.52) * mm, v(-11282.14, -6124.32) * mm, v(-11281.52, -6125.13) * mm, v(-11280.9, -6125.95) * mm, v(-11280.28, -6126.79) * mm, v(-11279.65, -6127.66) * mm, v(-11279, -6128.56) * mm, v(-11278.38, -6129.46) * mm, v(-11277.75, -6130.37) * mm, v(-11277.13, -6131.29) * mm, v(-11276.52, -6132.21) * mm, v(-11275.92, -6133.14) * mm, v(-11275.33, -6134.07) * mm, v(-11274.74, -6135) * mm, v(-11274.16, -6135.95) * mm, v(-11273.58, -6136.9) * mm, v(-11273.01, -6137.85) * mm, v(-11272.45, -6138.8) * mm, v(-11271.9, -6139.76) * mm, v(-11271.34, -6140.73) * mm, v(-11270.8, -6141.7) * mm, v(-11270.26, -6142.67) * mm, v(-11269.73, -6143.65) * mm, v(-11269.2, -6144.63) * mm, v(-11268.68, -6145.61) * mm, v(-11268.16, -6146.6) * mm, v(-11267.65, -6147.6) * mm, v(-11267.14, -6148.59) * mm, v(-11266.63, -6149.58) * mm, v(-11266.13, -6150.59) * mm, v(-11265.64, -6151.6) * mm, v(-11265.14, -6152.6) * mm, v(-11264.66, -6153.6) * mm, v(-11264.17, -6154.62) * mm, v(-11263.69, -6155.63) * mm, v(-11263.21, -6156.65) * mm, v(-11262.73, -6157.67) * mm, v(-11262.26, -6158.69) * mm, v(-11261.8, -6159.71) * mm, v(-11261.32, -6160.74) * mm, v(-11260.86, -6161.76) * mm, v(-11260.4, -6162.8) * mm, v(-11259.93, -6163.82) * mm, v(-11259.47, -6164.85) * mm, v(-11259.02, -6165.88) * mm, v(-11258.56, -6166.91) * mm, v(-11258.1, -6167.95) * mm, v(-11257.65, -6168.98) * mm, v(-11257.2, -6170.02) * mm, v(-11256.74, -6171.05) * mm, v(-11256.29, -6172.09) * mm, v(-11255.84, -6173.12) * mm, v(-11255.54, -6173.81) * mm, v(-11255.39, -6174.16) * mm]});
            skFitSpline(sketch, "E2848", {"points": [v(15043.1, 9268.41) * mm, v(15042.68, 9267.42) * mm, v(15037.13, 9254.33) * mm, v(15024.77, 9225.11) * mm, v(14996.08, 9217.47) * mm, v(14980.83, 9213.41) * mm]});
            skFitSpline(sketch, "E2849", {"points": [v(26191.6, -19834.46) * mm, v(26194.38, -19848.4) * mm, v(26200.36, -19878.35) * mm, v(26194.65, -19908.4) * mm, v(26191.6, -19924.46) * mm]});
            skFitSpline(sketch, "E2850", {"points": [v(25995.04, -20118.05) * mm, v(25981.12, -20122.14) * mm, v(25951.37, -20130.87) * mm, v(25921.16, -20123.53) * mm, v(25905.08, -20119.63) * mm]});
            skFitSpline(sketch, "E2851", {"points": [v(25709.9, -19924.45) * mm, v(25706.55, -19910.5) * mm, v(25699.36, -19880.66) * mm, v(25705.37, -19850.5) * mm, v(25708.57, -19834.43) * mm]});
            skFitSpline(sketch, "E2852", {"points": [v(25905.12, -19639.37) * mm, v(25919.07, -19635.9) * mm, v(25948.98, -19628.46) * mm, v(25979.06, -19635.57) * mm, v(25995.1, -19639.37) * mm]});
            skFitSpline(sketch, "E2853", {"points": [v(26508.92, -19843.35) * mm, v(26539.24, -19835.48) * mm, v(26581.54, -19824.5) * mm, v(26650.5, -19807.8) * mm, v(26656.22, -19831.26) * mm, v(26658.33, -19839.91) * mm]});
            skFitSpline(sketch, "E2854", {"points": [v(26658.33, -19839.91) * mm, v(26688.8, -19832.1) * mm, v(26731.3, -19821.22) * mm, v(26798.35, -19804.5) * mm, v(26805.46, -19825.88) * mm, v(26807.86, -19833.1) * mm]});
            const initialGuessF0  = {"E450": [14.116072, 9.270297, 0.072036, 0, 0.072036, 0.057998, 3.204606, 6.21966], "E1469": [2.842416, -12.459022, 0, -0.02719, 0.02719, 0.021881, 3.820594, 5.61589], "E1470": [2.84426, -12.457864, 0, -0.026066, 0.026066, 0.020976, 0.594348, 2.55521]};
            skSetInitialGuess(sketch, initialGuessF0);
            skSolve(sketch);
        }
        {
            var Q0;
            Q0=qCreatedBy(makeId("Front.planeOp"),FACE);
            var sketch = newSketch(context, id + "F1", { "sketchPlane" : qUnion([Q0])});
            skLineSegment(sketch, "E2855.0", {"start": v(-17739.24, 9152.34) * mm, "end": v(-17738.13, 6856.46) * mm});
            skLineSegment(sketch, "E2855.1", {"start": v(-12857.83, 6827.41) * mm, "end": v(-14885.8, 6847.7) * mm});
            skLineSegment(sketch, "E2855.2", {"start": v(-8485.65, 6827.41) * mm, "end": v(-8490.38, 9163.52) * mm});
            skLineSegment(sketch, "E2855.3", {"start": v(-12857.83, 6827.41) * mm, "end": v(-8485.65, 6827.41) * mm});
            skLineSegment(sketch, "E2855.4", {"start": v(-14885.8, 6847.7) * mm, "end": v(-17738.13, 6856.46) * mm});
            skPoint(sketch, "E2856.orphan", {"position": v(-8395.83, 6827.41) * mm});
            skLineSegment(sketch, "E2857", {"start": v(-17739.24, 9152.34) * mm, "end": v(-8490.38, 9163.52) * mm});
            skLineSegment(sketch, "E2858", {"start": v(-13114.81, 9157.93) * mm, "end": v(-13120.44, 13815.74) * mm, "construction": true});
            skLineSegment(sketch, "E2859", {"start": v(-8490.38, 11663.52) * mm, "end": v(-8490.38, 9163.52) * mm});
            skLineSegment(sketch, "E2860", {"start": v(-8490.38, 11663.52) * mm, "end": v(-13120.44, 13815.74) * mm});
            skLineSegment(sketch, "E2861", {"start": v(-14114.81, 9156.72) * mm, "end": v(-14119.88, 13347.61) * mm});
            skLineSegment(sketch, "E2862", {"start": v(-17739.24, 9152.34) * mm, "end": v(-17739.24, 11652.34) * mm});
            skLineSegment(sketch, "E2863", {"start": v(-17739.24, 11652.34) * mm, "end": v(-13120.44, 13815.74) * mm, "construction": true});
            skLineSegment(sketch, "E2864", {"start": v(-17739.24, 11652.34) * mm, "end": v(-14119.88, 13347.61) * mm});
            skLineSegment(sketch, "E2865", {"start": v(-13120.44, 13815.74) * mm, "end": v(-14121, 14280.84) * mm, "construction": true});
            skLineSegment(sketch, "E2866", {"start": v(-12857.83, 6827.41) * mm, "end": v(-12789.47, 13661.89) * mm});
            skLineSegment(sketch, "E2867", {"start": v(-14885.8, 6847.7) * mm, "end": v(-14888.6, 9155.78) * mm});
            skLineSegment(sketch, "E2868", {"start": v(-14945.89, 9155.71) * mm, "end": v(-14945.89, 9361.24) * mm});
            skLineSegment(sketch, "E2869", {"start": v(-14945.89, 9361.24) * mm, "end": v(-12832.49, 9361.24) * mm});
            skLineSegment(sketch, "E2870", {"start": v(-14119.88, 13347.61) * mm, "end": v(-13120.44, 13815.74) * mm});
            skLineSegment(sketch, "E2871", {"start": v(-14119.88, 13347.61) * mm, "end": v(-14121, 14280.84) * mm, "construction": true});
            skLineSegment(sketch, "E2872", {"start": v(-8490.38, 10413.52) * mm, "end": v(-12821.53, 10456.84) * mm, "construction": true});
            skLineSegment(sketch, "E2873", {"start": v(-10655.96, 10435.18) * mm, "end": v(-10633.7, 12659.81) * mm, "construction": true});
            skLineSegment(sketch, "E2874", {"start": v(-10633.7, 12659.81) * mm, "end": v(-12809.46, 11663.52) * mm});
            skSolve(sketch);
        }
        {
            var Q0;
            Q0=qSketchRegion(id+"F1",true);
            extrude(context, id + "F2", {"entities" : qUnion([Q0]), "oppositeDirection" : true, "depth" : 9870.42 * mm, "offsetDistance" : 25 * mm});
        }
        {
            var Q0;
            {var subQ0=sQuery(id+"F1.wireOp",EDGE,"E2859");Q0=makeQuery(id+"F1.imprint","IMPRINT",FACE,{"disambiguationData":[TD([[makeQuery(id+"F1.imprint","IMPRINT",EDGE,{"derivedFrom":subQ0}),-1.0]])]});}
            var Q1;
            {var subQ0=sQuery(id+"F1.wireOp",EDGE,"E2855.2");Q1=makeQuery(id+"F1.imprint","IMPRINT",FACE,{"disambiguationData":[TD([[makeQuery(id+"F1.imprint","IMPRINT",EDGE,{"derivedFrom":subQ0}),1.0]])]});}
            extrude(context, id + "F3", {"entities" : qUnion([Q0, Q1]), "operationType" : NewBodyOperationType.ADD, "depth" : 2192 * mm, "offsetDistance" : 25 * mm});
        }
        {
            var Q0;
            {var subQ0=sQuery(id+"F1.wireOp",EDGE,"E2861");var subQ1=sQuery(id+"F1.wireOp",EDGE,"E2857");var subQ2=makeQuery(id+"F1.imprint","INTERSECT",VERTEX,{"derivedFrom":[subQ1,subQ0]});Q0=makeQuery(id+"F1.imprint","IMPRINT",FACE,{"disambiguationData":[TD([[makeQuery(id+"F1.imprint","IMPRINT",EDGE,{"disambiguationData":[TD([[subQ2,-1.0]])],"derivedFrom":subQ1}),1.0]])]});}
            var Q1;
            {var subQ1=sQuery(id+"F1.wireOp",EDGE,"E2855.1");Q1=makeQuery(id+"F1.imprint","IMPRINT",FACE,{"disambiguationData":[TD([[makeQuery(id+"F1.imprint","IMPRINT",EDGE,{"derivedFrom":subQ1}),-1.0]])]});}
            var Q2;
            {var subQ0=sQuery(id+"F1.wireOp",EDGE,"E2868");Q2=makeQuery(id+"F1.imprint","IMPRINT",FACE,{"disambiguationData":[TD([[makeQuery(id+"F1.imprint","IMPRINT",EDGE,{"derivedFrom":subQ0}),-1.0]])]});}
            extrude(context, id + "F4", {"entities" : qUnion([Q0, Q1, Q2]), "depth" : 1100 * mm, "offsetDistance" : 25 * mm});
        }
        {
            var Q0;
            {var subQ0=sQuery(id+"F1.wireOp",EDGE,"E2868");Q0=makeQuery(id+"F1.imprint","IMPRINT",FACE,{"disambiguationData":[TD([[makeQuery(id+"F1.imprint","IMPRINT",EDGE,{"derivedFrom":subQ0}),-1.0]])]});}
            var Q1;
            {var subQ0=sQuery(id+"F1.wireOp",EDGE,"E2861");var subQ1=sQuery(id+"F1.wireOp",EDGE,"E2857");var subQ2=makeQuery(id+"F1.imprint","INTERSECT",VERTEX,{"derivedFrom":[subQ1,subQ0]});Q1=makeQuery(id+"F1.imprint","IMPRINT",FACE,{"disambiguationData":[TD([[makeQuery(id+"F1.imprint","IMPRINT",EDGE,{"disambiguationData":[TD([[subQ2,-1.0]])],"derivedFrom":subQ1}),1.0]])]});}
            extrude(context, id + "F5", {"entities" : qUnion([Q0, Q1]), "depth" : 1200 * mm, "offsetDistance" : 25 * mm});
        }
        {
            var Q0;
            Q0=qCreatedBy(makeId("Front.planeOp"),FACE);
            var sketch = newSketch(context, id + "F6", { "sketchPlane" : qUnion([Q0])});
            skLineSegment(sketch, "E2875", {"start": v(-8490.38, 11663.52) * mm, "end": v(-4090.38, 9618.23) * mm});
            skLineSegment(sketch, "E2876", {"start": v(-4090.38, 9618.23) * mm, "end": v(-8490.38, 9618.23) * mm});
            skLineSegment(sketch, "E2877", {"start": v(-8490.38, 9618.23) * mm, "end": v(-8490.38, 11663.52) * mm});
            skSolve(sketch);
        }
        {
            var Q0;
            Q0=qSketchRegion(id+"F6",true);
            var Q1;
            Q1=makeQuery(id+"F3.opExtrude","CAP_FACE",FACE,{"disambiguationData":[OSD([sQuery(id+"F1.wireOp",EDGE,"E2855.2"),sQuery(id+"F1.wireOp",EDGE,"E2855.3"),sQuery(id+"F1.wireOp",EDGE,"E2859"),sQuery(id+"F1.wireOp",EDGE,"E2860"),sQuery(id+"F1.wireOp",EDGE,"E2866"),sQuery(id+"F1.wireOp",EDGE,"E2874")])],"isStart":false});
            extrude(context, id + "F7", {"entities" : qUnion([Q0]), "operationType" : NewBodyOperationType.ADD, "endBound" : BoundingType.UP_TO_SURFACE, "depth" : 25 * mm, "endBoundEntityFace" : qUnion([Q1]), "offsetDistance" : 25 * mm, "hasSecondDirection" : true, "secondDirectionOppositeDirection" : true, "secondDirectionDepth" : 3000 * mm});
        }
    });
